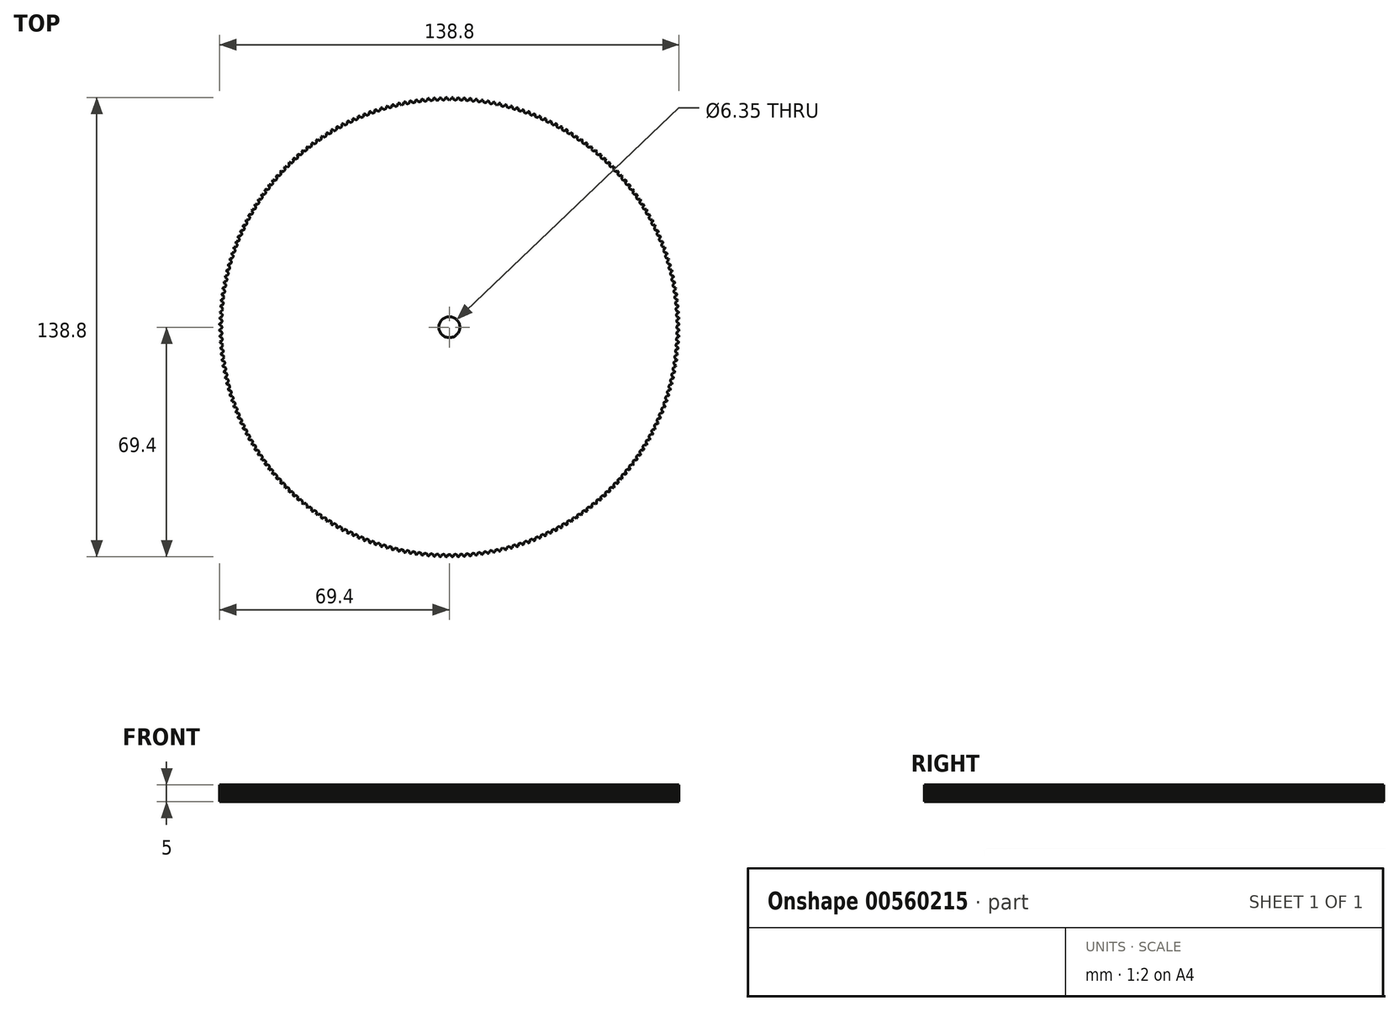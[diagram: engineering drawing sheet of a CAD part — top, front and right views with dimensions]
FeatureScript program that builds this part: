
annotation { "Feature Type Name" : "Feature", "Feature Type Description" : "" }
export const myFeature = defineFeature(function(context is Context, id is Id, definition is map)
    precondition{}
    {
        {
            var Q0;
            Q0=qCreatedBy(makeId("Top.planeOp"),FACE);
            var sketch = newSketch(context, id + "F0", { "sketchPlane" : qUnion([Q0])});
            skLineSegment(sketch, "E0", {"start": v(0.77, -69.4) * mm, "end": v(1.05, -69.4) * mm});
            skLineSegment(sketch, "E1", {"start": v(1.05, -69.4) * mm, "end": v(1.15, -69.36) * mm});
            skLineSegment(sketch, "E2", {"start": v(1.15, -69.36) * mm, "end": v(1.2, -69.27) * mm});
            skLineSegment(sketch, "E3", {"start": v(1.2, -69.27) * mm, "end": v(1.21, -69.18) * mm});
            skLineSegment(sketch, "E4", {"start": v(1.21, -69.18) * mm, "end": v(1.24, -69.08) * mm});
            skLineSegment(sketch, "E5", {"start": v(1.24, -69.08) * mm, "end": v(1.28, -68.99) * mm});
            skLineSegment(sketch, "E6", {"start": v(1.28, -68.99) * mm, "end": v(1.34, -68.9) * mm});
            skLineSegment(sketch, "E7", {"start": v(1.34, -68.9) * mm, "end": v(1.43, -68.8) * mm});
            skLineSegment(sketch, "E8", {"start": v(1.43, -68.8) * mm, "end": v(1.54, -68.74) * mm});
            skLineSegment(sketch, "E9", {"start": v(1.54, -68.74) * mm, "end": v(1.67, -68.7) * mm});
            skLineSegment(sketch, "E10", {"start": v(1.67, -68.7) * mm, "end": v(1.8, -68.68) * mm});
            skLineSegment(sketch, "E11", {"start": v(1.8, -68.68) * mm, "end": v(1.93, -68.69) * mm});
            skLineSegment(sketch, "E12", {"start": v(1.93, -68.69) * mm, "end": v(2.06, -68.73) * mm});
            skLineSegment(sketch, "E13", {"start": v(2.06, -68.73) * mm, "end": v(2.17, -68.79) * mm});
            skLineSegment(sketch, "E14", {"start": v(2.17, -68.79) * mm, "end": v(2.27, -68.87) * mm});
            skLineSegment(sketch, "E15", {"start": v(2.27, -68.87) * mm, "end": v(2.33, -68.96) * mm});
            skLineSegment(sketch, "E16", {"start": v(2.33, -68.96) * mm, "end": v(2.37, -69.05) * mm});
            skLineSegment(sketch, "E17", {"start": v(2.37, -69.05) * mm, "end": v(2.4, -69.14) * mm});
            skLineSegment(sketch, "E18", {"start": v(2.4, -69.14) * mm, "end": v(2.43, -69.24) * mm});
            skLineSegment(sketch, "E19", {"start": v(2.43, -69.24) * mm, "end": v(2.49, -69.33) * mm});
            skLineSegment(sketch, "E20", {"start": v(2.49, -69.33) * mm, "end": v(2.59, -69.36) * mm});
            skLineSegment(sketch, "E21", {"start": v(2.59, -69.36) * mm, "end": v(2.86, -69.35) * mm});
            skLineSegment(sketch, "E22", {"start": v(2.86, -69.35) * mm, "end": v(2.96, -69.3) * mm});
            skLineSegment(sketch, "E23", {"start": v(2.96, -69.3) * mm, "end": v(3, -69.22) * mm});
            skLineSegment(sketch, "E24", {"start": v(3, -69.22) * mm, "end": v(3.02, -69.12) * mm});
            skLineSegment(sketch, "E25", {"start": v(3.02, -69.12) * mm, "end": v(3.05, -69.02) * mm});
            skLineSegment(sketch, "E26", {"start": v(3.05, -69.02) * mm, "end": v(3.09, -68.93) * mm});
            skLineSegment(sketch, "E27", {"start": v(3.09, -68.93) * mm, "end": v(3.14, -68.84) * mm});
            skLineSegment(sketch, "E28", {"start": v(3.14, -68.84) * mm, "end": v(3.23, -68.75) * mm});
            skLineSegment(sketch, "E29", {"start": v(3.23, -68.75) * mm, "end": v(3.34, -68.68) * mm});
            skLineSegment(sketch, "E30", {"start": v(3.34, -68.68) * mm, "end": v(3.47, -68.63) * mm});
            skLineSegment(sketch, "E31", {"start": v(3.47, -68.63) * mm, "end": v(3.6, -68.6) * mm});
            skLineSegment(sketch, "E32", {"start": v(3.6, -68.6) * mm, "end": v(3.73, -68.62) * mm});
            skLineSegment(sketch, "E33", {"start": v(3.73, -68.62) * mm, "end": v(3.85, -68.65) * mm});
            skLineSegment(sketch, "E34", {"start": v(3.85, -68.65) * mm, "end": v(3.97, -68.7) * mm});
            skLineSegment(sketch, "E35", {"start": v(3.97, -68.7) * mm, "end": v(4.07, -68.79) * mm});
            skLineSegment(sketch, "E36", {"start": v(4.07, -68.79) * mm, "end": v(4.13, -68.87) * mm});
            skLineSegment(sketch, "E37", {"start": v(4.13, -68.87) * mm, "end": v(4.18, -68.96) * mm});
            skLineSegment(sketch, "E38", {"start": v(4.18, -68.96) * mm, "end": v(4.22, -69.06) * mm});
            skLineSegment(sketch, "E39", {"start": v(4.22, -69.06) * mm, "end": v(4.24, -69.15) * mm});
            skLineSegment(sketch, "E40", {"start": v(4.24, -69.15) * mm, "end": v(4.3, -69.24) * mm});
            skLineSegment(sketch, "E41", {"start": v(4.3, -69.24) * mm, "end": v(4.4, -69.26) * mm});
            skLineSegment(sketch, "E42", {"start": v(4.4, -69.26) * mm, "end": v(4.68, -69.25) * mm});
            skLineSegment(sketch, "E43", {"start": v(4.68, -69.25) * mm, "end": v(4.77, -69.2) * mm});
            skLineSegment(sketch, "E44", {"start": v(4.77, -69.2) * mm, "end": v(4.82, -69.12) * mm});
            skLineSegment(sketch, "E45", {"start": v(4.82, -69.12) * mm, "end": v(4.83, -69.02) * mm});
            skLineSegment(sketch, "E46", {"start": v(4.83, -69.02) * mm, "end": v(4.86, -68.92) * mm});
            skLineSegment(sketch, "E47", {"start": v(4.86, -68.92) * mm, "end": v(4.9, -68.82) * mm});
            skLineSegment(sketch, "E48", {"start": v(4.9, -68.82) * mm, "end": v(4.94, -68.73) * mm});
            skLineSegment(sketch, "E49", {"start": v(4.94, -68.73) * mm, "end": v(5.03, -68.64) * mm});
            skLineSegment(sketch, "E50", {"start": v(5.03, -68.64) * mm, "end": v(5.14, -68.56) * mm});
            skLineSegment(sketch, "E51", {"start": v(5.14, -68.56) * mm, "end": v(5.26, -68.52) * mm});
            skLineSegment(sketch, "E52", {"start": v(5.26, -68.52) * mm, "end": v(5.4, -68.5) * mm});
            skLineSegment(sketch, "E53", {"start": v(5.4, -68.5) * mm, "end": v(5.52, -68.5) * mm});
            skLineSegment(sketch, "E54", {"start": v(5.52, -68.5) * mm, "end": v(5.65, -68.52) * mm});
            skLineSegment(sketch, "E55", {"start": v(5.65, -68.52) * mm, "end": v(5.77, -68.58) * mm});
            skLineSegment(sketch, "E56", {"start": v(5.77, -68.58) * mm, "end": v(5.87, -68.66) * mm});
            skLineSegment(sketch, "E57", {"start": v(5.87, -68.66) * mm, "end": v(5.93, -68.74) * mm});
            skLineSegment(sketch, "E58", {"start": v(5.93, -68.74) * mm, "end": v(5.98, -68.83) * mm});
            skLineSegment(sketch, "E59", {"start": v(5.98, -68.83) * mm, "end": v(6.02, -68.92) * mm});
            skLineSegment(sketch, "E60", {"start": v(6.02, -68.92) * mm, "end": v(6.05, -69.02) * mm});
            skLineSegment(sketch, "E61", {"start": v(6.05, -69.02) * mm, "end": v(6.1, -69.1) * mm});
            skLineSegment(sketch, "E62", {"start": v(6.1, -69.1) * mm, "end": v(6.21, -69.13) * mm});
            skLineSegment(sketch, "E63", {"start": v(6.21, -69.13) * mm, "end": v(6.49, -69.1) * mm});
            skLineSegment(sketch, "E64", {"start": v(6.49, -69.1) * mm, "end": v(6.58, -69.06) * mm});
            skLineSegment(sketch, "E65", {"start": v(6.58, -69.06) * mm, "end": v(6.63, -68.97) * mm});
            skLineSegment(sketch, "E66", {"start": v(6.63, -68.97) * mm, "end": v(6.64, -68.87) * mm});
            skLineSegment(sketch, "E67", {"start": v(6.64, -68.87) * mm, "end": v(6.66, -68.77) * mm});
            skLineSegment(sketch, "E68", {"start": v(6.66, -68.77) * mm, "end": v(6.7, -68.67) * mm});
            skLineSegment(sketch, "E69", {"start": v(6.7, -68.67) * mm, "end": v(6.74, -68.58) * mm});
            skLineSegment(sketch, "E70", {"start": v(6.74, -68.58) * mm, "end": v(6.83, -68.48) * mm});
            skLineSegment(sketch, "E71", {"start": v(6.83, -68.48) * mm, "end": v(6.93, -68.4) * mm});
            skLineSegment(sketch, "E72", {"start": v(6.93, -68.4) * mm, "end": v(7.05, -68.35) * mm});
            skLineSegment(sketch, "E73", {"start": v(7.05, -68.35) * mm, "end": v(7.18, -68.33) * mm});
            skLineSegment(sketch, "E74", {"start": v(7.18, -68.33) * mm, "end": v(7.31, -68.33) * mm});
            skLineSegment(sketch, "E75", {"start": v(7.31, -68.33) * mm, "end": v(7.44, -68.35) * mm});
            skLineSegment(sketch, "E76", {"start": v(7.44, -68.35) * mm, "end": v(7.56, -68.4) * mm});
            skLineSegment(sketch, "E77", {"start": v(7.56, -68.4) * mm, "end": v(7.67, -68.48) * mm});
            skLineSegment(sketch, "E78", {"start": v(7.67, -68.48) * mm, "end": v(7.73, -68.56) * mm});
            skLineSegment(sketch, "E79", {"start": v(7.73, -68.56) * mm, "end": v(7.78, -68.65) * mm});
            skLineSegment(sketch, "E80", {"start": v(7.78, -68.65) * mm, "end": v(7.83, -68.74) * mm});
            skLineSegment(sketch, "E81", {"start": v(7.83, -68.74) * mm, "end": v(7.86, -68.84) * mm});
            skLineSegment(sketch, "E82", {"start": v(7.86, -68.84) * mm, "end": v(7.92, -68.92) * mm});
            skLineSegment(sketch, "E83", {"start": v(7.92, -68.92) * mm, "end": v(8.02, -68.94) * mm});
            skLineSegment(sketch, "E84", {"start": v(8.02, -68.94) * mm, "end": v(8.3, -68.9) * mm});
            skLineSegment(sketch, "E85", {"start": v(8.3, -68.9) * mm, "end": v(8.4, -68.86) * mm});
            skLineSegment(sketch, "E86", {"start": v(8.4, -68.86) * mm, "end": v(8.43, -68.77) * mm});
            skLineSegment(sketch, "E87", {"start": v(8.43, -68.77) * mm, "end": v(8.44, -68.67) * mm});
            skLineSegment(sketch, "E88", {"start": v(8.44, -68.67) * mm, "end": v(8.46, -68.57) * mm});
            skLineSegment(sketch, "E89", {"start": v(8.46, -68.57) * mm, "end": v(8.49, -68.47) * mm});
            skLineSegment(sketch, "E90", {"start": v(8.49, -68.47) * mm, "end": v(8.53, -68.38) * mm});
            skLineSegment(sketch, "E91", {"start": v(8.53, -68.38) * mm, "end": v(8.62, -68.28) * mm});
            skLineSegment(sketch, "E92", {"start": v(8.62, -68.28) * mm, "end": v(8.72, -68.2) * mm});
            skLineSegment(sketch, "E93", {"start": v(8.72, -68.2) * mm, "end": v(8.84, -68.15) * mm});
            skLineSegment(sketch, "E94", {"start": v(8.84, -68.15) * mm, "end": v(8.97, -68.12) * mm});
            skLineSegment(sketch, "E95", {"start": v(8.97, -68.12) * mm, "end": v(9.1, -68.11) * mm});
            skLineSegment(sketch, "E96", {"start": v(9.1, -68.11) * mm, "end": v(9.23, -68.13) * mm});
            skLineSegment(sketch, "E97", {"start": v(9.23, -68.13) * mm, "end": v(9.35, -68.18) * mm});
            skLineSegment(sketch, "E98", {"start": v(9.35, -68.18) * mm, "end": v(9.46, -68.26) * mm});
            skLineSegment(sketch, "E99", {"start": v(9.46, -68.26) * mm, "end": v(9.52, -68.34) * mm});
            skLineSegment(sketch, "E100", {"start": v(9.52, -68.34) * mm, "end": v(9.58, -68.42) * mm});
            skLineSegment(sketch, "E101", {"start": v(9.58, -68.42) * mm, "end": v(9.62, -68.51) * mm});
            skLineSegment(sketch, "E102", {"start": v(9.62, -68.51) * mm, "end": v(9.66, -68.6) * mm});
            skLineSegment(sketch, "E103", {"start": v(9.66, -68.6) * mm, "end": v(9.72, -68.69) * mm});
            skLineSegment(sketch, "E104", {"start": v(9.72, -68.69) * mm, "end": v(9.82, -68.7) * mm});
            skLineSegment(sketch, "E105", {"start": v(9.82, -68.7) * mm, "end": v(10.1, -68.67) * mm});
            skLineSegment(sketch, "E106", {"start": v(10.1, -68.67) * mm, "end": v(10.19, -68.62) * mm});
            skLineSegment(sketch, "E107", {"start": v(10.19, -68.62) * mm, "end": v(10.23, -68.53) * mm});
            skLineSegment(sketch, "E108", {"start": v(10.23, -68.53) * mm, "end": v(10.23, -68.43) * mm});
            skLineSegment(sketch, "E109", {"start": v(10.23, -68.43) * mm, "end": v(10.25, -68.33) * mm});
            skLineSegment(sketch, "E110", {"start": v(10.25, -68.33) * mm, "end": v(10.28, -68.23) * mm});
            skLineSegment(sketch, "E111", {"start": v(10.28, -68.23) * mm, "end": v(10.32, -68.13) * mm});
            skLineSegment(sketch, "E112", {"start": v(10.32, -68.13) * mm, "end": v(10.4, -68.03) * mm});
            skLineSegment(sketch, "E113", {"start": v(10.4, -68.03) * mm, "end": v(10.5, -67.95) * mm});
            skLineSegment(sketch, "E114", {"start": v(10.5, -67.95) * mm, "end": v(10.62, -67.9) * mm});
            skLineSegment(sketch, "E115", {"start": v(10.62, -67.9) * mm, "end": v(10.75, -67.86) * mm});
            skLineSegment(sketch, "E116", {"start": v(10.75, -67.86) * mm, "end": v(10.88, -67.85) * mm});
            skLineSegment(sketch, "E117", {"start": v(10.88, -67.85) * mm, "end": v(11, -67.87) * mm});
            skLineSegment(sketch, "E118", {"start": v(11, -67.87) * mm, "end": v(11.13, -67.91) * mm});
            skLineSegment(sketch, "E119", {"start": v(11.13, -67.91) * mm, "end": v(11.24, -67.99) * mm});
            skLineSegment(sketch, "E120", {"start": v(11.24, -67.99) * mm, "end": v(11.3, -68.07) * mm});
            skLineSegment(sketch, "E121", {"start": v(11.3, -68.07) * mm, "end": v(11.37, -68.15) * mm});
            skLineSegment(sketch, "E122", {"start": v(11.37, -68.15) * mm, "end": v(11.41, -68.24) * mm});
            skLineSegment(sketch, "E123", {"start": v(11.41, -68.24) * mm, "end": v(11.45, -68.33) * mm});
            skLineSegment(sketch, "E124", {"start": v(11.45, -68.33) * mm, "end": v(11.51, -68.4) * mm});
            skLineSegment(sketch, "E125", {"start": v(11.51, -68.4) * mm, "end": v(11.62, -68.43) * mm});
            skLineSegment(sketch, "E126", {"start": v(11.62, -68.43) * mm, "end": v(11.89, -68.38) * mm});
            skLineSegment(sketch, "E127", {"start": v(11.89, -68.38) * mm, "end": v(11.98, -68.33) * mm});
            skLineSegment(sketch, "E128", {"start": v(11.98, -68.33) * mm, "end": v(12.02, -68.23) * mm});
            skLineSegment(sketch, "E129", {"start": v(12.02, -68.23) * mm, "end": v(12.02, -68.13) * mm});
            skLineSegment(sketch, "E130", {"start": v(12.02, -68.13) * mm, "end": v(12.03, -68.03) * mm});
            skLineSegment(sketch, "E131", {"start": v(12.03, -68.03) * mm, "end": v(12.06, -67.94) * mm});
            skLineSegment(sketch, "E132", {"start": v(12.06, -67.94) * mm, "end": v(12.1, -67.84) * mm});
            skLineSegment(sketch, "E133", {"start": v(12.1, -67.84) * mm, "end": v(12.18, -67.74) * mm});
            skLineSegment(sketch, "E134", {"start": v(12.18, -67.74) * mm, "end": v(12.28, -67.65) * mm});
            skLineSegment(sketch, "E135", {"start": v(12.28, -67.65) * mm, "end": v(12.4, -67.6) * mm});
            skLineSegment(sketch, "E136", {"start": v(12.4, -67.6) * mm, "end": v(12.52, -67.55) * mm});
            skLineSegment(sketch, "E137", {"start": v(12.52, -67.55) * mm, "end": v(12.65, -67.54) * mm});
            skLineSegment(sketch, "E138", {"start": v(12.65, -67.54) * mm, "end": v(12.78, -67.56) * mm});
            skLineSegment(sketch, "E139", {"start": v(12.78, -67.56) * mm, "end": v(12.9, -67.6) * mm});
            skLineSegment(sketch, "E140", {"start": v(12.9, -67.6) * mm, "end": v(13.02, -67.67) * mm});
            skLineSegment(sketch, "E141", {"start": v(13.02, -67.67) * mm, "end": v(13.09, -67.75) * mm});
            skLineSegment(sketch, "E142", {"start": v(13.09, -67.75) * mm, "end": v(13.15, -67.83) * mm});
            skLineSegment(sketch, "E143", {"start": v(13.15, -67.83) * mm, "end": v(13.2, -67.92) * mm});
            skLineSegment(sketch, "E144", {"start": v(13.2, -67.92) * mm, "end": v(13.23, -68) * mm});
            skLineSegment(sketch, "E145", {"start": v(13.23, -68) * mm, "end": v(13.3, -68.08) * mm});
            skLineSegment(sketch, "E146", {"start": v(13.3, -68.08) * mm, "end": v(13.4, -68.1) * mm});
            skLineSegment(sketch, "E147", {"start": v(13.4, -68.1) * mm, "end": v(13.67, -68.04) * mm});
            skLineSegment(sketch, "E148", {"start": v(13.67, -68.04) * mm, "end": v(13.77, -68) * mm});
            skLineSegment(sketch, "E149", {"start": v(13.77, -68) * mm, "end": v(13.8, -67.9) * mm});
            skLineSegment(sketch, "E150", {"start": v(13.8, -67.9) * mm, "end": v(13.8, -67.8) * mm});
            skLineSegment(sketch, "E151", {"start": v(13.8, -67.8) * mm, "end": v(13.81, -67.7) * mm});
            skLineSegment(sketch, "E152", {"start": v(13.81, -67.7) * mm, "end": v(13.83, -67.6) * mm});
            skLineSegment(sketch, "E153", {"start": v(13.83, -67.6) * mm, "end": v(13.87, -67.5) * mm});
            skLineSegment(sketch, "E154", {"start": v(13.87, -67.5) * mm, "end": v(13.95, -67.4) * mm});
            skLineSegment(sketch, "E155", {"start": v(13.95, -67.4) * mm, "end": v(14.04, -67.3) * mm});
            skLineSegment(sketch, "E156", {"start": v(14.04, -67.3) * mm, "end": v(14.16, -67.24) * mm});
            skLineSegment(sketch, "E157", {"start": v(14.16, -67.24) * mm, "end": v(14.28, -67.2) * mm});
            skLineSegment(sketch, "E158", {"start": v(14.28, -67.2) * mm, "end": v(14.42, -67.19) * mm});
            skLineSegment(sketch, "E159", {"start": v(14.42, -67.19) * mm, "end": v(14.55, -67.2) * mm});
            skLineSegment(sketch, "E160", {"start": v(14.55, -67.2) * mm, "end": v(14.67, -67.24) * mm});
            skLineSegment(sketch, "E161", {"start": v(14.67, -67.24) * mm, "end": v(14.78, -67.3) * mm});
            skLineSegment(sketch, "E162", {"start": v(14.78, -67.3) * mm, "end": v(14.86, -67.38) * mm});
            skLineSegment(sketch, "E163", {"start": v(14.86, -67.38) * mm, "end": v(14.92, -67.46) * mm});
            skLineSegment(sketch, "E164", {"start": v(14.92, -67.46) * mm, "end": v(14.97, -67.55) * mm});
            skLineSegment(sketch, "E165", {"start": v(14.97, -67.55) * mm, "end": v(15, -67.64) * mm});
            skLineSegment(sketch, "E166", {"start": v(15, -67.64) * mm, "end": v(15.08, -67.71) * mm});
            skLineSegment(sketch, "E167", {"start": v(15.08, -67.71) * mm, "end": v(15.18, -67.72) * mm});
            skLineSegment(sketch, "E168", {"start": v(15.18, -67.72) * mm, "end": v(15.45, -67.66) * mm});
            skLineSegment(sketch, "E169", {"start": v(15.45, -67.66) * mm, "end": v(15.54, -67.6) * mm});
            skLineSegment(sketch, "E170", {"start": v(15.54, -67.6) * mm, "end": v(15.57, -67.51) * mm});
            skLineSegment(sketch, "E171", {"start": v(15.57, -67.51) * mm, "end": v(15.57, -67.41) * mm});
            skLineSegment(sketch, "E172", {"start": v(15.57, -67.41) * mm, "end": v(15.58, -67.31) * mm});
            skLineSegment(sketch, "E173", {"start": v(15.58, -67.31) * mm, "end": v(15.6, -67.21) * mm});
            skLineSegment(sketch, "E174", {"start": v(15.6, -67.21) * mm, "end": v(15.63, -67.11) * mm});
            skLineSegment(sketch, "E175", {"start": v(15.63, -67.11) * mm, "end": v(15.7, -67) * mm});
            skLineSegment(sketch, "E176", {"start": v(15.7, -67) * mm, "end": v(15.8, -66.92) * mm});
            skLineSegment(sketch, "E177", {"start": v(15.8, -66.92) * mm, "end": v(15.91, -66.85) * mm});
            skLineSegment(sketch, "E178", {"start": v(15.91, -66.85) * mm, "end": v(16.04, -66.8) * mm});
            skLineSegment(sketch, "E179", {"start": v(16.04, -66.8) * mm, "end": v(16.17, -66.79) * mm});
            skLineSegment(sketch, "E180", {"start": v(16.17, -66.79) * mm, "end": v(16.3, -66.8) * mm});
            skLineSegment(sketch, "E181", {"start": v(16.3, -66.8) * mm, "end": v(16.43, -66.83) * mm});
            skLineSegment(sketch, "E182", {"start": v(16.43, -66.83) * mm, "end": v(16.54, -66.9) * mm});
            skLineSegment(sketch, "E183", {"start": v(16.54, -66.9) * mm, "end": v(16.61, -66.97) * mm});
            skLineSegment(sketch, "E184", {"start": v(16.61, -66.97) * mm, "end": v(16.68, -67.05) * mm});
            skLineSegment(sketch, "E185", {"start": v(16.68, -67.05) * mm, "end": v(16.73, -67.13) * mm});
            skLineSegment(sketch, "E186", {"start": v(16.73, -67.13) * mm, "end": v(16.77, -67.22) * mm});
            skLineSegment(sketch, "E187", {"start": v(16.77, -67.22) * mm, "end": v(16.84, -67.3) * mm});
            skLineSegment(sketch, "E188", {"start": v(16.84, -67.3) * mm, "end": v(16.95, -67.3) * mm});
            skLineSegment(sketch, "E189", {"start": v(16.95, -67.3) * mm, "end": v(17.22, -67.24) * mm});
            skLineSegment(sketch, "E190", {"start": v(17.22, -67.24) * mm, "end": v(17.3, -67.18) * mm});
            skLineSegment(sketch, "E191", {"start": v(17.3, -67.18) * mm, "end": v(17.33, -67.08) * mm});
            skLineSegment(sketch, "E192", {"start": v(17.33, -67.08) * mm, "end": v(17.33, -66.98) * mm});
            skLineSegment(sketch, "E193", {"start": v(17.33, -66.98) * mm, "end": v(17.33, -66.88) * mm});
            skLineSegment(sketch, "E194", {"start": v(17.33, -66.88) * mm, "end": v(17.35, -66.78) * mm});
            skLineSegment(sketch, "E195", {"start": v(17.35, -66.78) * mm, "end": v(17.38, -66.68) * mm});
            skLineSegment(sketch, "E196", {"start": v(17.38, -66.68) * mm, "end": v(17.45, -66.57) * mm});
            skLineSegment(sketch, "E197", {"start": v(17.45, -66.57) * mm, "end": v(17.55, -66.48) * mm});
            skLineSegment(sketch, "E198", {"start": v(17.55, -66.48) * mm, "end": v(17.66, -66.4) * mm});
            skLineSegment(sketch, "E199", {"start": v(17.66, -66.4) * mm, "end": v(17.78, -66.36) * mm});
            skLineSegment(sketch, "E200", {"start": v(17.78, -66.36) * mm, "end": v(17.91, -66.34) * mm});
            skLineSegment(sketch, "E201", {"start": v(17.91, -66.34) * mm, "end": v(18.04, -66.35) * mm});
            skLineSegment(sketch, "E202", {"start": v(18.04, -66.35) * mm, "end": v(18.17, -66.38) * mm});
            skLineSegment(sketch, "E203", {"start": v(18.17, -66.38) * mm, "end": v(18.29, -66.44) * mm});
            skLineSegment(sketch, "E204", {"start": v(18.29, -66.44) * mm, "end": v(18.36, -66.51) * mm});
            skLineSegment(sketch, "E205", {"start": v(18.36, -66.51) * mm, "end": v(18.43, -66.59) * mm});
            skLineSegment(sketch, "E206", {"start": v(18.43, -66.59) * mm, "end": v(18.48, -66.67) * mm});
            skLineSegment(sketch, "E207", {"start": v(18.48, -66.67) * mm, "end": v(18.53, -66.76) * mm});
            skLineSegment(sketch, "E208", {"start": v(18.53, -66.76) * mm, "end": v(18.6, -66.83) * mm});
            skLineSegment(sketch, "E209", {"start": v(18.6, -66.83) * mm, "end": v(18.7, -66.84) * mm});
            skLineSegment(sketch, "E210", {"start": v(18.7, -66.84) * mm, "end": v(18.97, -66.76) * mm});
            skLineSegment(sketch, "E211", {"start": v(18.97, -66.76) * mm, "end": v(19.06, -66.7) * mm});
            skLineSegment(sketch, "E212", {"start": v(19.06, -66.7) * mm, "end": v(19.08, -66.6) * mm});
            skLineSegment(sketch, "E213", {"start": v(19.08, -66.6) * mm, "end": v(19.08, -66.5) * mm});
            skLineSegment(sketch, "E214", {"start": v(19.08, -66.5) * mm, "end": v(19.08, -66.4) * mm});
            skLineSegment(sketch, "E215", {"start": v(19.08, -66.4) * mm, "end": v(19.1, -66.3) * mm});
            skLineSegment(sketch, "E216", {"start": v(19.1, -66.3) * mm, "end": v(19.12, -66.2) * mm});
            skLineSegment(sketch, "E217", {"start": v(19.12, -66.2) * mm, "end": v(19.2, -66.1) * mm});
            skLineSegment(sketch, "E218", {"start": v(19.2, -66.1) * mm, "end": v(19.28, -66) * mm});
            skLineSegment(sketch, "E219", {"start": v(19.28, -66) * mm, "end": v(19.4, -65.92) * mm});
            skLineSegment(sketch, "E220", {"start": v(19.4, -65.92) * mm, "end": v(19.51, -65.87) * mm});
            skLineSegment(sketch, "E221", {"start": v(19.51, -65.87) * mm, "end": v(19.64, -65.85) * mm});
            skLineSegment(sketch, "E222", {"start": v(19.64, -65.85) * mm, "end": v(19.77, -65.85) * mm});
            skLineSegment(sketch, "E223", {"start": v(19.77, -65.85) * mm, "end": v(19.9, -65.88) * mm});
            skLineSegment(sketch, "E224", {"start": v(19.9, -65.88) * mm, "end": v(20.02, -65.94) * mm});
            skLineSegment(sketch, "E225", {"start": v(20.02, -65.94) * mm, "end": v(20.1, -66) * mm});
            skLineSegment(sketch, "E226", {"start": v(20.1, -66) * mm, "end": v(20.16, -66.08) * mm});
            skLineSegment(sketch, "E227", {"start": v(20.16, -66.08) * mm, "end": v(20.22, -66.16) * mm});
            skLineSegment(sketch, "E228", {"start": v(20.22, -66.16) * mm, "end": v(20.27, -66.25) * mm});
            skLineSegment(sketch, "E229", {"start": v(20.27, -66.25) * mm, "end": v(20.34, -66.32) * mm});
            skLineSegment(sketch, "E230", {"start": v(20.34, -66.32) * mm, "end": v(20.45, -66.32) * mm});
            skLineSegment(sketch, "E231", {"start": v(20.45, -66.32) * mm, "end": v(20.71, -66.24) * mm});
            skLineSegment(sketch, "E232", {"start": v(20.71, -66.24) * mm, "end": v(20.8, -66.18) * mm});
            skLineSegment(sketch, "E233", {"start": v(20.8, -66.18) * mm, "end": v(20.82, -66.08) * mm});
            skLineSegment(sketch, "E234", {"start": v(20.82, -66.08) * mm, "end": v(20.81, -65.98) * mm});
            skLineSegment(sketch, "E235", {"start": v(20.81, -65.98) * mm, "end": v(20.81, -65.88) * mm});
            skLineSegment(sketch, "E236", {"start": v(20.81, -65.88) * mm, "end": v(20.82, -65.78) * mm});
            skLineSegment(sketch, "E237", {"start": v(20.82, -65.78) * mm, "end": v(20.85, -65.68) * mm});
            skLineSegment(sketch, "E238", {"start": v(20.85, -65.68) * mm, "end": v(20.91, -65.57) * mm});
            skLineSegment(sketch, "E239", {"start": v(20.91, -65.57) * mm, "end": v(21, -65.47) * mm});
            skLineSegment(sketch, "E240", {"start": v(21, -65.47) * mm, "end": v(21.1, -65.4) * mm});
            skLineSegment(sketch, "E241", {"start": v(21.1, -65.4) * mm, "end": v(21.23, -65.34) * mm});
            skLineSegment(sketch, "E242", {"start": v(21.23, -65.34) * mm, "end": v(21.36, -65.31) * mm});
            skLineSegment(sketch, "E243", {"start": v(21.36, -65.31) * mm, "end": v(21.5, -65.31) * mm});
            skLineSegment(sketch, "E244", {"start": v(21.5, -65.31) * mm, "end": v(21.62, -65.34) * mm});
            skLineSegment(sketch, "E245", {"start": v(21.62, -65.34) * mm, "end": v(21.74, -65.4) * mm});
            skLineSegment(sketch, "E246", {"start": v(21.74, -65.4) * mm, "end": v(21.82, -65.46) * mm});
            skLineSegment(sketch, "E247", {"start": v(21.82, -65.46) * mm, "end": v(21.89, -65.53) * mm});
            skLineSegment(sketch, "E248", {"start": v(21.89, -65.53) * mm, "end": v(21.95, -65.61) * mm});
            skLineSegment(sketch, "E249", {"start": v(21.95, -65.61) * mm, "end": v(22, -65.7) * mm});
            skLineSegment(sketch, "E250", {"start": v(22, -65.7) * mm, "end": v(22.07, -65.76) * mm});
            skLineSegment(sketch, "E251", {"start": v(22.07, -65.76) * mm, "end": v(22.18, -65.77) * mm});
            skLineSegment(sketch, "E252", {"start": v(22.18, -65.77) * mm, "end": v(22.44, -65.68) * mm});
            skLineSegment(sketch, "E253", {"start": v(22.44, -65.68) * mm, "end": v(22.52, -65.61) * mm});
            skLineSegment(sketch, "E254", {"start": v(22.52, -65.61) * mm, "end": v(22.54, -65.51) * mm});
            skLineSegment(sketch, "E255", {"start": v(22.54, -65.51) * mm, "end": v(22.53, -65.41) * mm});
            skLineSegment(sketch, "E256", {"start": v(22.53, -65.41) * mm, "end": v(22.53, -65.31) * mm});
            skLineSegment(sketch, "E257", {"start": v(22.53, -65.31) * mm, "end": v(22.54, -65.21) * mm});
            skLineSegment(sketch, "E258", {"start": v(22.54, -65.21) * mm, "end": v(22.56, -65.11) * mm});
            skLineSegment(sketch, "E259", {"start": v(22.56, -65.11) * mm, "end": v(22.62, -65) * mm});
            skLineSegment(sketch, "E260", {"start": v(22.62, -65) * mm, "end": v(22.7, -64.9) * mm});
            skLineSegment(sketch, "E261", {"start": v(22.7, -64.9) * mm, "end": v(22.81, -64.82) * mm});
            skLineSegment(sketch, "E262", {"start": v(22.81, -64.82) * mm, "end": v(22.93, -64.76) * mm});
            skLineSegment(sketch, "E263", {"start": v(22.93, -64.76) * mm, "end": v(23.06, -64.73) * mm});
            skLineSegment(sketch, "E264", {"start": v(23.06, -64.73) * mm, "end": v(23.2, -64.73) * mm});
            skLineSegment(sketch, "E265", {"start": v(23.2, -64.73) * mm, "end": v(23.32, -64.75) * mm});
            skLineSegment(sketch, "E266", {"start": v(23.32, -64.75) * mm, "end": v(23.44, -64.8) * mm});
            skLineSegment(sketch, "E267", {"start": v(23.44, -64.8) * mm, "end": v(23.52, -64.86) * mm});
            skLineSegment(sketch, "E268", {"start": v(23.52, -64.86) * mm, "end": v(23.6, -64.94) * mm});
            skLineSegment(sketch, "E269", {"start": v(23.6, -64.94) * mm, "end": v(23.66, -65.02) * mm});
            skLineSegment(sketch, "E270", {"start": v(23.66, -65.02) * mm, "end": v(23.7, -65.1) * mm});
            skLineSegment(sketch, "E271", {"start": v(23.7, -65.1) * mm, "end": v(23.79, -65.16) * mm});
            skLineSegment(sketch, "E272", {"start": v(23.79, -65.16) * mm, "end": v(23.9, -65.16) * mm});
            skLineSegment(sketch, "E273", {"start": v(23.9, -65.16) * mm, "end": v(24.15, -65.07) * mm});
            skLineSegment(sketch, "E274", {"start": v(24.15, -65.07) * mm, "end": v(24.23, -65) * mm});
            skLineSegment(sketch, "E275", {"start": v(24.23, -65) * mm, "end": v(24.25, -64.9) * mm});
            skLineSegment(sketch, "E276", {"start": v(24.25, -64.9) * mm, "end": v(24.23, -64.8) * mm});
            skLineSegment(sketch, "E277", {"start": v(24.23, -64.8) * mm, "end": v(24.23, -64.7) * mm});
            skLineSegment(sketch, "E278", {"start": v(24.23, -64.7) * mm, "end": v(24.24, -64.6) * mm});
            skLineSegment(sketch, "E279", {"start": v(24.24, -64.6) * mm, "end": v(24.26, -64.5) * mm});
            skLineSegment(sketch, "E280", {"start": v(24.26, -64.5) * mm, "end": v(24.32, -64.38) * mm});
            skLineSegment(sketch, "E281", {"start": v(24.32, -64.38) * mm, "end": v(24.4, -64.28) * mm});
            skLineSegment(sketch, "E282", {"start": v(24.4, -64.28) * mm, "end": v(24.5, -64.2) * mm});
            skLineSegment(sketch, "E283", {"start": v(24.5, -64.2) * mm, "end": v(24.62, -64.14) * mm});
            skLineSegment(sketch, "E284", {"start": v(24.62, -64.14) * mm, "end": v(24.75, -64.1) * mm});
            skLineSegment(sketch, "E285", {"start": v(24.75, -64.1) * mm, "end": v(24.88, -64.1) * mm});
            skLineSegment(sketch, "E286", {"start": v(24.88, -64.1) * mm, "end": v(25, -64.12) * mm});
            skLineSegment(sketch, "E287", {"start": v(25, -64.12) * mm, "end": v(25.13, -64.16) * mm});
            skLineSegment(sketch, "E288", {"start": v(25.13, -64.16) * mm, "end": v(25.21, -64.23) * mm});
            skLineSegment(sketch, "E289", {"start": v(25.21, -64.23) * mm, "end": v(25.29, -64.3) * mm});
            skLineSegment(sketch, "E290", {"start": v(25.29, -64.3) * mm, "end": v(25.35, -64.37) * mm});
            skLineSegment(sketch, "E291", {"start": v(25.35, -64.37) * mm, "end": v(25.4, -64.46) * mm});
            skLineSegment(sketch, "E292", {"start": v(25.4, -64.46) * mm, "end": v(25.48, -64.52) * mm});
            skLineSegment(sketch, "E293", {"start": v(25.48, -64.52) * mm, "end": v(25.6, -64.51) * mm});
            skLineSegment(sketch, "E294", {"start": v(25.6, -64.51) * mm, "end": v(25.85, -64.41) * mm});
            skLineSegment(sketch, "E295", {"start": v(25.85, -64.41) * mm, "end": v(25.93, -64.34) * mm});
            skLineSegment(sketch, "E296", {"start": v(25.93, -64.34) * mm, "end": v(25.94, -64.24) * mm});
            skLineSegment(sketch, "E297", {"start": v(25.94, -64.24) * mm, "end": v(25.92, -64.15) * mm});
            skLineSegment(sketch, "E298", {"start": v(25.92, -64.15) * mm, "end": v(25.92, -64.05) * mm});
            skLineSegment(sketch, "E299", {"start": v(25.92, -64.05) * mm, "end": v(25.92, -63.94) * mm});
            skLineSegment(sketch, "E300", {"start": v(25.92, -63.94) * mm, "end": v(25.94, -63.84) * mm});
            skLineSegment(sketch, "E301", {"start": v(25.94, -63.84) * mm, "end": v(26, -63.72) * mm});
            skLineSegment(sketch, "E302", {"start": v(26, -63.72) * mm, "end": v(26.07, -63.62) * mm});
            skLineSegment(sketch, "E303", {"start": v(26.07, -63.62) * mm, "end": v(26.18, -63.54) * mm});
            skLineSegment(sketch, "E304", {"start": v(26.18, -63.54) * mm, "end": v(26.3, -63.47) * mm});
            skLineSegment(sketch, "E305", {"start": v(26.3, -63.47) * mm, "end": v(26.42, -63.44) * mm});
            skLineSegment(sketch, "E306", {"start": v(26.42, -63.44) * mm, "end": v(26.55, -63.42) * mm});
            skLineSegment(sketch, "E307", {"start": v(26.55, -63.42) * mm, "end": v(26.68, -63.44) * mm});
            skLineSegment(sketch, "E308", {"start": v(26.68, -63.44) * mm, "end": v(26.8, -63.48) * mm});
            skLineSegment(sketch, "E309", {"start": v(26.8, -63.48) * mm, "end": v(26.89, -63.54) * mm});
            skLineSegment(sketch, "E310", {"start": v(26.89, -63.54) * mm, "end": v(26.96, -63.61) * mm});
            skLineSegment(sketch, "E311", {"start": v(26.96, -63.61) * mm, "end": v(27.03, -63.69) * mm});
            skLineSegment(sketch, "E312", {"start": v(27.03, -63.69) * mm, "end": v(27.08, -63.77) * mm});
            skLineSegment(sketch, "E313", {"start": v(27.08, -63.77) * mm, "end": v(27.16, -63.83) * mm});
            skLineSegment(sketch, "E314", {"start": v(27.16, -63.83) * mm, "end": v(27.27, -63.82) * mm});
            skLineSegment(sketch, "E315", {"start": v(27.27, -63.82) * mm, "end": v(27.52, -63.71) * mm});
            skLineSegment(sketch, "E316", {"start": v(27.52, -63.71) * mm, "end": v(27.6, -63.64) * mm});
            skLineSegment(sketch, "E317", {"start": v(27.6, -63.64) * mm, "end": v(27.61, -63.54) * mm});
            skLineSegment(sketch, "E318", {"start": v(27.61, -63.54) * mm, "end": v(27.6, -63.45) * mm});
            skLineSegment(sketch, "E319", {"start": v(27.6, -63.45) * mm, "end": v(27.58, -63.34) * mm});
            skLineSegment(sketch, "E320", {"start": v(27.58, -63.34) * mm, "end": v(27.59, -63.24) * mm});
            skLineSegment(sketch, "E321", {"start": v(27.59, -63.24) * mm, "end": v(27.6, -63.14) * mm});
            skLineSegment(sketch, "E322", {"start": v(27.6, -63.14) * mm, "end": v(27.65, -63.02) * mm});
            skLineSegment(sketch, "E323", {"start": v(27.65, -63.02) * mm, "end": v(27.73, -62.92) * mm});
            skLineSegment(sketch, "E324", {"start": v(27.73, -62.92) * mm, "end": v(27.83, -62.83) * mm});
            skLineSegment(sketch, "E325", {"start": v(27.83, -62.83) * mm, "end": v(27.94, -62.76) * mm});
            skLineSegment(sketch, "E326", {"start": v(27.94, -62.76) * mm, "end": v(28.07, -62.72) * mm});
            skLineSegment(sketch, "E327", {"start": v(28.07, -62.72) * mm, "end": v(28.2, -62.7) * mm});
            skLineSegment(sketch, "E328", {"start": v(28.2, -62.7) * mm, "end": v(28.33, -62.72) * mm});
            skLineSegment(sketch, "E329", {"start": v(28.33, -62.72) * mm, "end": v(28.45, -62.76) * mm});
            skLineSegment(sketch, "E330", {"start": v(28.45, -62.76) * mm, "end": v(28.54, -62.82) * mm});
            skLineSegment(sketch, "E331", {"start": v(28.54, -62.82) * mm, "end": v(28.62, -62.88) * mm});
            skLineSegment(sketch, "E332", {"start": v(28.62, -62.88) * mm, "end": v(28.69, -62.96) * mm});
            skLineSegment(sketch, "E333", {"start": v(28.69, -62.96) * mm, "end": v(28.74, -63.04) * mm});
            skLineSegment(sketch, "E334", {"start": v(28.74, -63.04) * mm, "end": v(28.83, -63.1) * mm});
            skLineSegment(sketch, "E335", {"start": v(28.83, -63.1) * mm, "end": v(28.93, -63.09) * mm});
            skLineSegment(sketch, "E336", {"start": v(28.93, -63.09) * mm, "end": v(29.18, -62.97) * mm});
            skLineSegment(sketch, "E337", {"start": v(29.18, -62.97) * mm, "end": v(29.26, -62.9) * mm});
            skLineSegment(sketch, "E338", {"start": v(29.26, -62.9) * mm, "end": v(29.27, -62.8) * mm});
            skLineSegment(sketch, "E339", {"start": v(29.27, -62.8) * mm, "end": v(29.24, -62.7) * mm});
            skLineSegment(sketch, "E340", {"start": v(29.24, -62.7) * mm, "end": v(29.23, -62.6) * mm});
            skLineSegment(sketch, "E341", {"start": v(29.23, -62.6) * mm, "end": v(29.23, -62.5) * mm});
            skLineSegment(sketch, "E342", {"start": v(29.23, -62.5) * mm, "end": v(29.24, -62.4) * mm});
            skLineSegment(sketch, "E343", {"start": v(29.24, -62.4) * mm, "end": v(29.3, -62.28) * mm});
            skLineSegment(sketch, "E344", {"start": v(29.3, -62.28) * mm, "end": v(29.37, -62.17) * mm});
            skLineSegment(sketch, "E345", {"start": v(29.37, -62.17) * mm, "end": v(29.46, -62.08) * mm});
            skLineSegment(sketch, "E346", {"start": v(29.46, -62.08) * mm, "end": v(29.58, -62.01) * mm});
            skLineSegment(sketch, "E347", {"start": v(29.58, -62.01) * mm, "end": v(29.7, -61.97) * mm});
            skLineSegment(sketch, "E348", {"start": v(29.7, -61.97) * mm, "end": v(29.83, -61.95) * mm});
            skLineSegment(sketch, "E349", {"start": v(29.83, -61.95) * mm, "end": v(29.96, -61.96) * mm});
            skLineSegment(sketch, "E350", {"start": v(29.96, -61.96) * mm, "end": v(30.09, -62) * mm});
            skLineSegment(sketch, "E351", {"start": v(30.09, -62) * mm, "end": v(30.17, -62.05) * mm});
            skLineSegment(sketch, "E352", {"start": v(30.17, -62.05) * mm, "end": v(30.25, -62.11) * mm});
            skLineSegment(sketch, "E353", {"start": v(30.25, -62.11) * mm, "end": v(30.32, -62.19) * mm});
            skLineSegment(sketch, "E354", {"start": v(30.32, -62.19) * mm, "end": v(30.38, -62.27) * mm});
            skLineSegment(sketch, "E355", {"start": v(30.38, -62.27) * mm, "end": v(30.47, -62.32) * mm});
            skLineSegment(sketch, "E356", {"start": v(30.47, -62.32) * mm, "end": v(30.57, -62.3) * mm});
            skLineSegment(sketch, "E357", {"start": v(30.57, -62.3) * mm, "end": v(30.82, -62.19) * mm});
            skLineSegment(sketch, "E358", {"start": v(30.82, -62.19) * mm, "end": v(30.9, -62.11) * mm});
            skLineSegment(sketch, "E359", {"start": v(30.9, -62.11) * mm, "end": v(30.9, -62.01) * mm});
            skLineSegment(sketch, "E360", {"start": v(30.9, -62.01) * mm, "end": v(30.88, -61.91) * mm});
            skLineSegment(sketch, "E361", {"start": v(30.88, -61.91) * mm, "end": v(30.86, -61.81) * mm});
            skLineSegment(sketch, "E362", {"start": v(30.86, -61.81) * mm, "end": v(30.86, -61.71) * mm});
            skLineSegment(sketch, "E363", {"start": v(30.86, -61.71) * mm, "end": v(30.87, -61.6) * mm});
            skLineSegment(sketch, "E364", {"start": v(30.87, -61.6) * mm, "end": v(30.91, -61.49) * mm});
            skLineSegment(sketch, "E365", {"start": v(30.91, -61.49) * mm, "end": v(30.99, -61.38) * mm});
            skLineSegment(sketch, "E366", {"start": v(30.99, -61.38) * mm, "end": v(31.08, -61.29) * mm});
            skLineSegment(sketch, "E367", {"start": v(31.08, -61.29) * mm, "end": v(31.2, -61.22) * mm});
            skLineSegment(sketch, "E368", {"start": v(31.2, -61.22) * mm, "end": v(31.31, -61.17) * mm});
            skLineSegment(sketch, "E369", {"start": v(31.31, -61.17) * mm, "end": v(31.44, -61.15) * mm});
            skLineSegment(sketch, "E370", {"start": v(31.44, -61.15) * mm, "end": v(31.57, -61.15) * mm});
            skLineSegment(sketch, "E371", {"start": v(31.57, -61.15) * mm, "end": v(31.7, -61.19) * mm});
            skLineSegment(sketch, "E372", {"start": v(31.7, -61.19) * mm, "end": v(31.79, -61.24) * mm});
            skLineSegment(sketch, "E373", {"start": v(31.79, -61.24) * mm, "end": v(31.87, -61.3) * mm});
            skLineSegment(sketch, "E374", {"start": v(31.87, -61.3) * mm, "end": v(31.94, -61.37) * mm});
            skLineSegment(sketch, "E375", {"start": v(31.94, -61.37) * mm, "end": v(32, -61.45) * mm});
            skLineSegment(sketch, "E376", {"start": v(32, -61.45) * mm, "end": v(32.09, -61.5) * mm});
            skLineSegment(sketch, "E377", {"start": v(32.09, -61.5) * mm, "end": v(32.2, -61.49) * mm});
            skLineSegment(sketch, "E378", {"start": v(32.2, -61.49) * mm, "end": v(32.44, -61.36) * mm});
            skLineSegment(sketch, "E379", {"start": v(32.44, -61.36) * mm, "end": v(32.51, -61.28) * mm});
            skLineSegment(sketch, "E380", {"start": v(32.51, -61.28) * mm, "end": v(32.51, -61.18) * mm});
            skLineSegment(sketch, "E381", {"start": v(32.51, -61.18) * mm, "end": v(32.49, -61.08) * mm});
            skLineSegment(sketch, "E382", {"start": v(32.49, -61.08) * mm, "end": v(32.47, -60.99) * mm});
            skLineSegment(sketch, "E383", {"start": v(32.47, -60.99) * mm, "end": v(32.46, -60.88) * mm});
            skLineSegment(sketch, "E384", {"start": v(32.46, -60.88) * mm, "end": v(32.47, -60.78) * mm});
            skLineSegment(sketch, "E385", {"start": v(32.47, -60.78) * mm, "end": v(32.51, -60.66) * mm});
            skLineSegment(sketch, "E386", {"start": v(32.51, -60.66) * mm, "end": v(32.58, -60.55) * mm});
            skLineSegment(sketch, "E387", {"start": v(32.58, -60.55) * mm, "end": v(32.67, -60.45) * mm});
            skLineSegment(sketch, "E388", {"start": v(32.67, -60.45) * mm, "end": v(32.78, -60.38) * mm});
            skLineSegment(sketch, "E389", {"start": v(32.78, -60.38) * mm, "end": v(32.9, -60.33) * mm});
            skLineSegment(sketch, "E390", {"start": v(32.9, -60.33) * mm, "end": v(33.03, -60.3) * mm});
            skLineSegment(sketch, "E391", {"start": v(33.03, -60.3) * mm, "end": v(33.16, -60.3) * mm});
            skLineSegment(sketch, "E392", {"start": v(33.16, -60.3) * mm, "end": v(33.3, -60.34) * mm});
            skLineSegment(sketch, "E393", {"start": v(33.3, -60.34) * mm, "end": v(33.38, -60.39) * mm});
            skLineSegment(sketch, "E394", {"start": v(33.38, -60.39) * mm, "end": v(33.46, -60.45) * mm});
            skLineSegment(sketch, "E395", {"start": v(33.46, -60.45) * mm, "end": v(33.54, -60.51) * mm});
            skLineSegment(sketch, "E396", {"start": v(33.54, -60.51) * mm, "end": v(33.6, -60.6) * mm});
            skLineSegment(sketch, "E397", {"start": v(33.6, -60.6) * mm, "end": v(33.69, -60.64) * mm});
            skLineSegment(sketch, "E398", {"start": v(33.69, -60.64) * mm, "end": v(33.8, -60.62) * mm});
            skLineSegment(sketch, "E399", {"start": v(33.8, -60.62) * mm, "end": v(34.03, -60.49) * mm});
            skLineSegment(sketch, "E400", {"start": v(34.03, -60.49) * mm, "end": v(34.1, -60.4) * mm});
            skLineSegment(sketch, "E401", {"start": v(34.1, -60.4) * mm, "end": v(34.1, -60.3) * mm});
            skLineSegment(sketch, "E402", {"start": v(34.1, -60.3) * mm, "end": v(34.07, -60.21) * mm});
            skLineSegment(sketch, "E403", {"start": v(34.07, -60.21) * mm, "end": v(34.05, -60.11) * mm});
            skLineSegment(sketch, "E404", {"start": v(34.05, -60.11) * mm, "end": v(34.05, -60.01) * mm});
            skLineSegment(sketch, "E405", {"start": v(34.05, -60.01) * mm, "end": v(34.05, -59.9) * mm});
            skLineSegment(sketch, "E406", {"start": v(34.05, -59.9) * mm, "end": v(34.09, -59.78) * mm});
            skLineSegment(sketch, "E407", {"start": v(34.09, -59.78) * mm, "end": v(34.16, -59.67) * mm});
            skLineSegment(sketch, "E408", {"start": v(34.16, -59.67) * mm, "end": v(34.24, -59.58) * mm});
            skLineSegment(sketch, "E409", {"start": v(34.24, -59.58) * mm, "end": v(34.35, -59.5) * mm});
            skLineSegment(sketch, "E410", {"start": v(34.35, -59.5) * mm, "end": v(34.47, -59.44) * mm});
            skLineSegment(sketch, "E411", {"start": v(34.47, -59.44) * mm, "end": v(34.6, -59.42) * mm});
            skLineSegment(sketch, "E412", {"start": v(34.6, -59.42) * mm, "end": v(34.73, -59.41) * mm});
            skLineSegment(sketch, "E413", {"start": v(34.73, -59.41) * mm, "end": v(34.86, -59.44) * mm});
            skLineSegment(sketch, "E414", {"start": v(34.86, -59.44) * mm, "end": v(34.95, -59.5) * mm});
            skLineSegment(sketch, "E415", {"start": v(34.95, -59.5) * mm, "end": v(35.03, -59.55) * mm});
            skLineSegment(sketch, "E416", {"start": v(35.03, -59.55) * mm, "end": v(35.1, -59.62) * mm});
            skLineSegment(sketch, "E417", {"start": v(35.1, -59.62) * mm, "end": v(35.18, -59.7) * mm});
            skLineSegment(sketch, "E418", {"start": v(35.18, -59.7) * mm, "end": v(35.26, -59.74) * mm});
            skLineSegment(sketch, "E419", {"start": v(35.26, -59.74) * mm, "end": v(35.37, -59.72) * mm});
            skLineSegment(sketch, "E420", {"start": v(35.37, -59.72) * mm, "end": v(35.6, -59.58) * mm});
            skLineSegment(sketch, "E421", {"start": v(35.6, -59.58) * mm, "end": v(35.67, -59.5) * mm});
            skLineSegment(sketch, "E422", {"start": v(35.67, -59.5) * mm, "end": v(35.67, -59.4) * mm});
            skLineSegment(sketch, "E423", {"start": v(35.67, -59.4) * mm, "end": v(35.64, -59.3) * mm});
            skLineSegment(sketch, "E424", {"start": v(35.64, -59.3) * mm, "end": v(35.62, -59.2) * mm});
            skLineSegment(sketch, "E425", {"start": v(35.62, -59.2) * mm, "end": v(35.6, -59.1) * mm});
            skLineSegment(sketch, "E426", {"start": v(35.6, -59.1) * mm, "end": v(35.6, -59) * mm});
            skLineSegment(sketch, "E427", {"start": v(35.6, -59) * mm, "end": v(35.64, -58.87) * mm});
            skLineSegment(sketch, "E428", {"start": v(35.64, -58.87) * mm, "end": v(35.7, -58.76) * mm});
            skLineSegment(sketch, "E429", {"start": v(35.7, -58.76) * mm, "end": v(35.8, -58.66) * mm});
            skLineSegment(sketch, "E430", {"start": v(35.8, -58.66) * mm, "end": v(35.9, -58.58) * mm});
            skLineSegment(sketch, "E431", {"start": v(35.9, -58.58) * mm, "end": v(36.02, -58.52) * mm});
            skLineSegment(sketch, "E432", {"start": v(36.02, -58.52) * mm, "end": v(36.14, -58.49) * mm});
            skLineSegment(sketch, "E433", {"start": v(36.14, -58.49) * mm, "end": v(36.27, -58.49) * mm});
            skLineSegment(sketch, "E434", {"start": v(36.27, -58.49) * mm, "end": v(36.4, -58.51) * mm});
            skLineSegment(sketch, "E435", {"start": v(36.4, -58.51) * mm, "end": v(36.5, -58.56) * mm});
            skLineSegment(sketch, "E436", {"start": v(36.5, -58.56) * mm, "end": v(36.58, -58.61) * mm});
            skLineSegment(sketch, "E437", {"start": v(36.58, -58.61) * mm, "end": v(36.66, -58.68) * mm});
            skLineSegment(sketch, "E438", {"start": v(36.66, -58.68) * mm, "end": v(36.73, -58.75) * mm});
            skLineSegment(sketch, "E439", {"start": v(36.73, -58.75) * mm, "end": v(36.81, -58.8) * mm});
            skLineSegment(sketch, "E440", {"start": v(36.81, -58.8) * mm, "end": v(36.92, -58.77) * mm});
            skLineSegment(sketch, "E441", {"start": v(36.92, -58.77) * mm, "end": v(37.15, -58.62) * mm});
            skLineSegment(sketch, "E442", {"start": v(37.15, -58.62) * mm, "end": v(37.22, -58.54) * mm});
            skLineSegment(sketch, "E443", {"start": v(37.22, -58.54) * mm, "end": v(37.21, -58.44) * mm});
            skLineSegment(sketch, "E444", {"start": v(37.21, -58.44) * mm, "end": v(37.18, -58.35) * mm});
            skLineSegment(sketch, "E445", {"start": v(37.18, -58.35) * mm, "end": v(37.15, -58.25) * mm});
            skLineSegment(sketch, "E446", {"start": v(37.15, -58.25) * mm, "end": v(37.14, -58.15) * mm});
            skLineSegment(sketch, "E447", {"start": v(37.14, -58.15) * mm, "end": v(37.14, -58.05) * mm});
            skLineSegment(sketch, "E448", {"start": v(37.14, -58.05) * mm, "end": v(37.17, -57.92) * mm});
            skLineSegment(sketch, "E449", {"start": v(37.17, -57.92) * mm, "end": v(37.23, -57.8) * mm});
            skLineSegment(sketch, "E450", {"start": v(37.23, -57.8) * mm, "end": v(37.32, -57.7) * mm});
            skLineSegment(sketch, "E451", {"start": v(37.32, -57.7) * mm, "end": v(37.42, -57.62) * mm});
            skLineSegment(sketch, "E452", {"start": v(37.42, -57.62) * mm, "end": v(37.54, -57.56) * mm});
            skLineSegment(sketch, "E453", {"start": v(37.54, -57.56) * mm, "end": v(37.66, -57.52) * mm});
            skLineSegment(sketch, "E454", {"start": v(37.66, -57.52) * mm, "end": v(37.8, -57.52) * mm});
            skLineSegment(sketch, "E455", {"start": v(37.8, -57.52) * mm, "end": v(37.92, -57.54) * mm});
            skLineSegment(sketch, "E456", {"start": v(37.92, -57.54) * mm, "end": v(38.02, -57.58) * mm});
            skLineSegment(sketch, "E457", {"start": v(38.02, -57.58) * mm, "end": v(38.1, -57.63) * mm});
            skLineSegment(sketch, "E458", {"start": v(38.1, -57.63) * mm, "end": v(38.18, -57.7) * mm});
            skLineSegment(sketch, "E459", {"start": v(38.18, -57.7) * mm, "end": v(38.25, -57.77) * mm});
            skLineSegment(sketch, "E460", {"start": v(38.25, -57.77) * mm, "end": v(38.34, -57.81) * mm});
            skLineSegment(sketch, "E461", {"start": v(38.34, -57.81) * mm, "end": v(38.44, -57.78) * mm});
            skLineSegment(sketch, "E462", {"start": v(38.44, -57.78) * mm, "end": v(38.67, -57.63) * mm});
            skLineSegment(sketch, "E463", {"start": v(38.67, -57.63) * mm, "end": v(38.74, -57.55) * mm});
            skLineSegment(sketch, "E464", {"start": v(38.74, -57.55) * mm, "end": v(38.73, -57.45) * mm});
            skLineSegment(sketch, "E465", {"start": v(38.73, -57.45) * mm, "end": v(38.7, -57.35) * mm});
            skLineSegment(sketch, "E466", {"start": v(38.7, -57.35) * mm, "end": v(38.67, -57.26) * mm});
            skLineSegment(sketch, "E467", {"start": v(38.67, -57.26) * mm, "end": v(38.65, -57.16) * mm});
            skLineSegment(sketch, "E468", {"start": v(38.65, -57.16) * mm, "end": v(38.65, -57.05) * mm});
            skLineSegment(sketch, "E469", {"start": v(38.65, -57.05) * mm, "end": v(38.67, -56.93) * mm});
            skLineSegment(sketch, "E470", {"start": v(38.67, -56.93) * mm, "end": v(38.73, -56.8) * mm});
            skLineSegment(sketch, "E471", {"start": v(38.73, -56.8) * mm, "end": v(38.81, -56.7) * mm});
            skLineSegment(sketch, "E472", {"start": v(38.81, -56.7) * mm, "end": v(38.91, -56.62) * mm});
            skLineSegment(sketch, "E473", {"start": v(38.91, -56.62) * mm, "end": v(39.03, -56.56) * mm});
            skLineSegment(sketch, "E474", {"start": v(39.03, -56.56) * mm, "end": v(39.16, -56.52) * mm});
            skLineSegment(sketch, "E475", {"start": v(39.16, -56.52) * mm, "end": v(39.29, -56.5) * mm});
            skLineSegment(sketch, "E476", {"start": v(39.29, -56.5) * mm, "end": v(39.41, -56.53) * mm});
            skLineSegment(sketch, "E477", {"start": v(39.41, -56.53) * mm, "end": v(39.5, -56.57) * mm});
            skLineSegment(sketch, "E478", {"start": v(39.5, -56.57) * mm, "end": v(39.6, -56.62) * mm});
            skLineSegment(sketch, "E479", {"start": v(39.6, -56.62) * mm, "end": v(39.68, -56.68) * mm});
            skLineSegment(sketch, "E480", {"start": v(39.68, -56.68) * mm, "end": v(39.75, -56.75) * mm});
            skLineSegment(sketch, "E481", {"start": v(39.75, -56.75) * mm, "end": v(39.84, -56.79) * mm});
            skLineSegment(sketch, "E482", {"start": v(39.84, -56.79) * mm, "end": v(39.94, -56.76) * mm});
            skLineSegment(sketch, "E483", {"start": v(39.94, -56.76) * mm, "end": v(40.17, -56.6) * mm});
            skLineSegment(sketch, "E484", {"start": v(40.17, -56.6) * mm, "end": v(40.23, -56.51) * mm});
            skLineSegment(sketch, "E485", {"start": v(40.23, -56.51) * mm, "end": v(40.22, -56.41) * mm});
            skLineSegment(sketch, "E486", {"start": v(40.22, -56.41) * mm, "end": v(40.18, -56.32) * mm});
            skLineSegment(sketch, "E487", {"start": v(40.18, -56.32) * mm, "end": v(40.15, -56.23) * mm});
            skLineSegment(sketch, "E488", {"start": v(40.15, -56.23) * mm, "end": v(40.13, -56.13) * mm});
            skLineSegment(sketch, "E489", {"start": v(40.13, -56.13) * mm, "end": v(40.13, -56.02) * mm});
            skLineSegment(sketch, "E490", {"start": v(40.13, -56.02) * mm, "end": v(40.15, -55.9) * mm});
            skLineSegment(sketch, "E491", {"start": v(40.15, -55.9) * mm, "end": v(40.2, -55.78) * mm});
            skLineSegment(sketch, "E492", {"start": v(40.2, -55.78) * mm, "end": v(40.28, -55.67) * mm});
            skLineSegment(sketch, "E493", {"start": v(40.28, -55.67) * mm, "end": v(40.38, -55.58) * mm});
            skLineSegment(sketch, "E494", {"start": v(40.38, -55.58) * mm, "end": v(40.5, -55.52) * mm});
            skLineSegment(sketch, "E495", {"start": v(40.5, -55.52) * mm, "end": v(40.62, -55.47) * mm});
            skLineSegment(sketch, "E496", {"start": v(40.62, -55.47) * mm, "end": v(40.75, -55.46) * mm});
            skLineSegment(sketch, "E497", {"start": v(40.75, -55.46) * mm, "end": v(40.88, -55.47) * mm});
            skLineSegment(sketch, "E498", {"start": v(40.88, -55.47) * mm, "end": v(40.98, -55.51) * mm});
            skLineSegment(sketch, "E499", {"start": v(40.98, -55.51) * mm, "end": v(41.07, -55.56) * mm});
            skLineSegment(sketch, "E500", {"start": v(41.07, -55.56) * mm, "end": v(41.15, -55.62) * mm});
            skLineSegment(sketch, "E501", {"start": v(41.15, -55.62) * mm, "end": v(41.22, -55.69) * mm});
            skLineSegment(sketch, "E502", {"start": v(41.22, -55.69) * mm, "end": v(41.31, -55.73) * mm});
            skLineSegment(sketch, "E503", {"start": v(41.31, -55.73) * mm, "end": v(41.42, -55.7) * mm});
            skLineSegment(sketch, "E504", {"start": v(41.42, -55.7) * mm, "end": v(41.64, -55.53) * mm});
            skLineSegment(sketch, "E505", {"start": v(41.64, -55.53) * mm, "end": v(41.7, -55.44) * mm});
            skLineSegment(sketch, "E506", {"start": v(41.7, -55.44) * mm, "end": v(41.69, -55.34) * mm});
            skLineSegment(sketch, "E507", {"start": v(41.69, -55.34) * mm, "end": v(41.64, -55.25) * mm});
            skLineSegment(sketch, "E508", {"start": v(41.64, -55.25) * mm, "end": v(41.6, -55.16) * mm});
            skLineSegment(sketch, "E509", {"start": v(41.6, -55.16) * mm, "end": v(41.59, -55.06) * mm});
            skLineSegment(sketch, "E510", {"start": v(41.59, -55.06) * mm, "end": v(41.58, -54.95) * mm});
            skLineSegment(sketch, "E511", {"start": v(41.58, -54.95) * mm, "end": v(41.6, -54.82) * mm});
            skLineSegment(sketch, "E512", {"start": v(41.6, -54.82) * mm, "end": v(41.65, -54.7) * mm});
            skLineSegment(sketch, "E513", {"start": v(41.65, -54.7) * mm, "end": v(41.73, -54.6) * mm});
            skLineSegment(sketch, "E514", {"start": v(41.73, -54.6) * mm, "end": v(41.82, -54.5) * mm});
            skLineSegment(sketch, "E515", {"start": v(41.82, -54.5) * mm, "end": v(41.94, -54.44) * mm});
            skLineSegment(sketch, "E516", {"start": v(41.94, -54.44) * mm, "end": v(42.06, -54.4) * mm});
            skLineSegment(sketch, "E517", {"start": v(42.06, -54.4) * mm, "end": v(42.19, -54.37) * mm});
            skLineSegment(sketch, "E518", {"start": v(42.19, -54.37) * mm, "end": v(42.32, -54.38) * mm});
            skLineSegment(sketch, "E519", {"start": v(42.32, -54.38) * mm, "end": v(42.42, -54.42) * mm});
            skLineSegment(sketch, "E520", {"start": v(42.42, -54.42) * mm, "end": v(42.5, -54.47) * mm});
            skLineSegment(sketch, "E521", {"start": v(42.5, -54.47) * mm, "end": v(42.6, -54.52) * mm});
            skLineSegment(sketch, "E522", {"start": v(42.6, -54.52) * mm, "end": v(42.67, -54.59) * mm});
            skLineSegment(sketch, "E523", {"start": v(42.67, -54.59) * mm, "end": v(42.76, -54.62) * mm});
            skLineSegment(sketch, "E524", {"start": v(42.76, -54.62) * mm, "end": v(42.86, -54.59) * mm});
            skLineSegment(sketch, "E525", {"start": v(42.86, -54.59) * mm, "end": v(43.08, -54.42) * mm});
            skLineSegment(sketch, "E526", {"start": v(43.08, -54.42) * mm, "end": v(43.13, -54.33) * mm});
            skLineSegment(sketch, "E527", {"start": v(43.13, -54.33) * mm, "end": v(43.12, -54.23) * mm});
            skLineSegment(sketch, "E528", {"start": v(43.12, -54.23) * mm, "end": v(43.07, -54.14) * mm});
            skLineSegment(sketch, "E529", {"start": v(43.07, -54.14) * mm, "end": v(43.04, -54.05) * mm});
            skLineSegment(sketch, "E530", {"start": v(43.04, -54.05) * mm, "end": v(43.02, -53.95) * mm});
            skLineSegment(sketch, "E531", {"start": v(43.02, -53.95) * mm, "end": v(43, -53.85) * mm});
            skLineSegment(sketch, "E532", {"start": v(43, -53.85) * mm, "end": v(43.02, -53.72) * mm});
            skLineSegment(sketch, "E533", {"start": v(43.02, -53.72) * mm, "end": v(43.07, -53.6) * mm});
            skLineSegment(sketch, "E534", {"start": v(43.07, -53.6) * mm, "end": v(43.14, -53.49) * mm});
            skLineSegment(sketch, "E535", {"start": v(43.14, -53.49) * mm, "end": v(43.24, -53.4) * mm});
            skLineSegment(sketch, "E536", {"start": v(43.24, -53.4) * mm, "end": v(43.35, -53.32) * mm});
            skLineSegment(sketch, "E537", {"start": v(43.35, -53.32) * mm, "end": v(43.47, -53.27) * mm});
            skLineSegment(sketch, "E538", {"start": v(43.47, -53.27) * mm, "end": v(43.6, -53.25) * mm});
            skLineSegment(sketch, "E539", {"start": v(43.6, -53.25) * mm, "end": v(43.73, -53.26) * mm});
            skLineSegment(sketch, "E540", {"start": v(43.73, -53.26) * mm, "end": v(43.83, -53.3) * mm});
            skLineSegment(sketch, "E541", {"start": v(43.83, -53.3) * mm, "end": v(43.92, -53.34) * mm});
            skLineSegment(sketch, "E542", {"start": v(43.92, -53.34) * mm, "end": v(44, -53.39) * mm});
            skLineSegment(sketch, "E543", {"start": v(44, -53.39) * mm, "end": v(44.08, -53.45) * mm});
            skLineSegment(sketch, "E544", {"start": v(44.08, -53.45) * mm, "end": v(44.17, -53.49) * mm});
            skLineSegment(sketch, "E545", {"start": v(44.17, -53.49) * mm, "end": v(44.27, -53.45) * mm});
            skLineSegment(sketch, "E546", {"start": v(44.27, -53.45) * mm, "end": v(44.49, -53.27) * mm});
            skLineSegment(sketch, "E547", {"start": v(44.49, -53.27) * mm, "end": v(44.54, -53.18) * mm});
            skLineSegment(sketch, "E548", {"start": v(44.54, -53.18) * mm, "end": v(44.52, -53.08) * mm});
            skLineSegment(sketch, "E549", {"start": v(44.52, -53.08) * mm, "end": v(44.48, -53) * mm});
            skLineSegment(sketch, "E550", {"start": v(44.48, -53) * mm, "end": v(44.44, -52.9) * mm});
            skLineSegment(sketch, "E551", {"start": v(44.44, -52.9) * mm, "end": v(44.41, -52.8) * mm});
            skLineSegment(sketch, "E552", {"start": v(44.41, -52.8) * mm, "end": v(44.4, -52.7) * mm});
            skLineSegment(sketch, "E553", {"start": v(44.4, -52.7) * mm, "end": v(44.41, -52.57) * mm});
            skLineSegment(sketch, "E554", {"start": v(44.41, -52.57) * mm, "end": v(44.46, -52.45) * mm});
            skLineSegment(sketch, "E555", {"start": v(44.46, -52.45) * mm, "end": v(44.53, -52.34) * mm});
            skLineSegment(sketch, "E556", {"start": v(44.53, -52.34) * mm, "end": v(44.62, -52.24) * mm});
            skLineSegment(sketch, "E557", {"start": v(44.62, -52.24) * mm, "end": v(44.73, -52.17) * mm});
            skLineSegment(sketch, "E558", {"start": v(44.73, -52.17) * mm, "end": v(44.85, -52.12) * mm});
            skLineSegment(sketch, "E559", {"start": v(44.85, -52.12) * mm, "end": v(44.98, -52.1) * mm});
            skLineSegment(sketch, "E560", {"start": v(44.98, -52.1) * mm, "end": v(45.1, -52.1) * mm});
            skLineSegment(sketch, "E561", {"start": v(45.1, -52.1) * mm, "end": v(45.2, -52.13) * mm});
            skLineSegment(sketch, "E562", {"start": v(45.2, -52.13) * mm, "end": v(45.3, -52.17) * mm});
            skLineSegment(sketch, "E563", {"start": v(45.3, -52.17) * mm, "end": v(45.39, -52.22) * mm});
            skLineSegment(sketch, "E564", {"start": v(45.39, -52.22) * mm, "end": v(45.46, -52.28) * mm});
            skLineSegment(sketch, "E565", {"start": v(45.46, -52.28) * mm, "end": v(45.56, -52.31) * mm});
            skLineSegment(sketch, "E566", {"start": v(45.56, -52.31) * mm, "end": v(45.66, -52.27) * mm});
            skLineSegment(sketch, "E567", {"start": v(45.66, -52.27) * mm, "end": v(45.86, -52.1) * mm});
            skLineSegment(sketch, "E568", {"start": v(45.86, -52.1) * mm, "end": v(45.92, -52) * mm});
            skLineSegment(sketch, "E569", {"start": v(45.92, -52) * mm, "end": v(45.9, -51.9) * mm});
            skLineSegment(sketch, "E570", {"start": v(45.9, -51.9) * mm, "end": v(45.85, -51.81) * mm});
            skLineSegment(sketch, "E571", {"start": v(45.85, -51.81) * mm, "end": v(45.8, -51.72) * mm});
            skLineSegment(sketch, "E572", {"start": v(45.8, -51.72) * mm, "end": v(45.78, -51.62) * mm});
            skLineSegment(sketch, "E573", {"start": v(45.78, -51.62) * mm, "end": v(45.76, -51.52) * mm});
            skLineSegment(sketch, "E574", {"start": v(45.76, -51.52) * mm, "end": v(45.77, -51.4) * mm});
            skLineSegment(sketch, "E575", {"start": v(45.77, -51.4) * mm, "end": v(45.82, -51.27) * mm});
            skLineSegment(sketch, "E576", {"start": v(45.82, -51.27) * mm, "end": v(45.88, -51.15) * mm});
            skLineSegment(sketch, "E577", {"start": v(45.88, -51.15) * mm, "end": v(45.97, -51.06) * mm});
            skLineSegment(sketch, "E578", {"start": v(45.97, -51.06) * mm, "end": v(46.08, -50.98) * mm});
            skLineSegment(sketch, "E579", {"start": v(46.08, -50.98) * mm, "end": v(46.2, -50.92) * mm});
            skLineSegment(sketch, "E580", {"start": v(46.2, -50.92) * mm, "end": v(46.32, -50.9) * mm});
            skLineSegment(sketch, "E581", {"start": v(46.32, -50.9) * mm, "end": v(46.46, -50.9) * mm});
            skLineSegment(sketch, "E582", {"start": v(46.46, -50.9) * mm, "end": v(46.55, -50.93) * mm});
            skLineSegment(sketch, "E583", {"start": v(46.55, -50.93) * mm, "end": v(46.65, -50.96) * mm});
            skLineSegment(sketch, "E584", {"start": v(46.65, -50.96) * mm, "end": v(46.74, -51.01) * mm});
            skLineSegment(sketch, "E585", {"start": v(46.74, -51.01) * mm, "end": v(46.82, -51.07) * mm});
            skLineSegment(sketch, "E586", {"start": v(46.82, -51.07) * mm, "end": v(46.91, -51.1) * mm});
            skLineSegment(sketch, "E587", {"start": v(46.91, -51.1) * mm, "end": v(47.01, -51.06) * mm});
            skLineSegment(sketch, "E588", {"start": v(47.01, -51.06) * mm, "end": v(47.21, -50.87) * mm});
            skLineSegment(sketch, "E589", {"start": v(47.21, -50.87) * mm, "end": v(47.26, -50.78) * mm});
            skLineSegment(sketch, "E590", {"start": v(47.26, -50.78) * mm, "end": v(47.24, -50.68) * mm});
            skLineSegment(sketch, "E591", {"start": v(47.24, -50.68) * mm, "end": v(47.19, -50.6) * mm});
            skLineSegment(sketch, "E592", {"start": v(47.19, -50.6) * mm, "end": v(47.15, -50.5) * mm});
            skLineSegment(sketch, "E593", {"start": v(47.15, -50.5) * mm, "end": v(47.12, -50.4) * mm});
            skLineSegment(sketch, "E594", {"start": v(47.12, -50.4) * mm, "end": v(47.1, -50.3) * mm});
            skLineSegment(sketch, "E595", {"start": v(47.1, -50.3) * mm, "end": v(47.1, -50.18) * mm});
            skLineSegment(sketch, "E596", {"start": v(47.1, -50.18) * mm, "end": v(47.14, -50.05) * mm});
            skLineSegment(sketch, "E597", {"start": v(47.14, -50.05) * mm, "end": v(47.2, -49.94) * mm});
            skLineSegment(sketch, "E598", {"start": v(47.2, -49.94) * mm, "end": v(47.3, -49.84) * mm});
            skLineSegment(sketch, "E599", {"start": v(47.3, -49.84) * mm, "end": v(47.4, -49.75) * mm});
            skLineSegment(sketch, "E600", {"start": v(47.4, -49.75) * mm, "end": v(47.51, -49.7) * mm});
            skLineSegment(sketch, "E601", {"start": v(47.51, -49.7) * mm, "end": v(47.64, -49.67) * mm});
            skLineSegment(sketch, "E602", {"start": v(47.64, -49.67) * mm, "end": v(47.77, -49.66) * mm});
            skLineSegment(sketch, "E603", {"start": v(47.77, -49.66) * mm, "end": v(47.87, -49.69) * mm});
            skLineSegment(sketch, "E604", {"start": v(47.87, -49.69) * mm, "end": v(47.97, -49.73) * mm});
            skLineSegment(sketch, "E605", {"start": v(47.97, -49.73) * mm, "end": v(48.06, -49.77) * mm});
            skLineSegment(sketch, "E606", {"start": v(48.06, -49.77) * mm, "end": v(48.14, -49.83) * mm});
            skLineSegment(sketch, "E607", {"start": v(48.14, -49.83) * mm, "end": v(48.23, -49.86) * mm});
            skLineSegment(sketch, "E608", {"start": v(48.23, -49.86) * mm, "end": v(48.33, -49.81) * mm});
            skLineSegment(sketch, "E609", {"start": v(48.33, -49.81) * mm, "end": v(48.53, -49.62) * mm});
            skLineSegment(sketch, "E610", {"start": v(48.53, -49.62) * mm, "end": v(48.58, -49.52) * mm});
            skLineSegment(sketch, "E611", {"start": v(48.58, -49.52) * mm, "end": v(48.55, -49.43) * mm});
            skLineSegment(sketch, "E612", {"start": v(48.55, -49.43) * mm, "end": v(48.5, -49.34) * mm});
            skLineSegment(sketch, "E613", {"start": v(48.5, -49.34) * mm, "end": v(48.45, -49.25) * mm});
            skLineSegment(sketch, "E614", {"start": v(48.45, -49.25) * mm, "end": v(48.42, -49.16) * mm});
            skLineSegment(sketch, "E615", {"start": v(48.42, -49.16) * mm, "end": v(48.4, -49.06) * mm});
            skLineSegment(sketch, "E616", {"start": v(48.4, -49.06) * mm, "end": v(48.4, -48.92) * mm});
            skLineSegment(sketch, "E617", {"start": v(48.4, -48.92) * mm, "end": v(48.44, -48.8) * mm});
            skLineSegment(sketch, "E618", {"start": v(48.44, -48.8) * mm, "end": v(48.5, -48.68) * mm});
            skLineSegment(sketch, "E619", {"start": v(48.5, -48.68) * mm, "end": v(48.58, -48.58) * mm});
            skLineSegment(sketch, "E620", {"start": v(48.58, -48.58) * mm, "end": v(48.68, -48.5) * mm});
            skLineSegment(sketch, "E621", {"start": v(48.68, -48.5) * mm, "end": v(48.8, -48.44) * mm});
            skLineSegment(sketch, "E622", {"start": v(48.8, -48.44) * mm, "end": v(48.92, -48.4) * mm});
            skLineSegment(sketch, "E623", {"start": v(48.92, -48.4) * mm, "end": v(49.06, -48.4) * mm});
            skLineSegment(sketch, "E624", {"start": v(49.06, -48.4) * mm, "end": v(49.16, -48.42) * mm});
            skLineSegment(sketch, "E625", {"start": v(49.16, -48.42) * mm, "end": v(49.25, -48.45) * mm});
            skLineSegment(sketch, "E626", {"start": v(49.25, -48.45) * mm, "end": v(49.34, -48.5) * mm});
            skLineSegment(sketch, "E627", {"start": v(49.34, -48.5) * mm, "end": v(49.43, -48.55) * mm});
            skLineSegment(sketch, "E628", {"start": v(49.43, -48.55) * mm, "end": v(49.52, -48.58) * mm});
            skLineSegment(sketch, "E629", {"start": v(49.52, -48.58) * mm, "end": v(49.62, -48.53) * mm});
            skLineSegment(sketch, "E630", {"start": v(49.62, -48.53) * mm, "end": v(49.81, -48.33) * mm});
            skLineSegment(sketch, "E631", {"start": v(49.81, -48.33) * mm, "end": v(49.86, -48.23) * mm});
            skLineSegment(sketch, "E632", {"start": v(49.86, -48.23) * mm, "end": v(49.83, -48.14) * mm});
            skLineSegment(sketch, "E633", {"start": v(49.83, -48.14) * mm, "end": v(49.77, -48.06) * mm});
            skLineSegment(sketch, "E634", {"start": v(49.77, -48.06) * mm, "end": v(49.73, -47.97) * mm});
            skLineSegment(sketch, "E635", {"start": v(49.73, -47.97) * mm, "end": v(49.69, -47.87) * mm});
            skLineSegment(sketch, "E636", {"start": v(49.69, -47.87) * mm, "end": v(49.66, -47.77) * mm});
            skLineSegment(sketch, "E637", {"start": v(49.66, -47.77) * mm, "end": v(49.67, -47.64) * mm});
            skLineSegment(sketch, "E638", {"start": v(49.67, -47.64) * mm, "end": v(49.7, -47.51) * mm});
            skLineSegment(sketch, "E639", {"start": v(49.7, -47.51) * mm, "end": v(49.75, -47.4) * mm});
            skLineSegment(sketch, "E640", {"start": v(49.75, -47.4) * mm, "end": v(49.84, -47.3) * mm});
            skLineSegment(sketch, "E641", {"start": v(49.84, -47.3) * mm, "end": v(49.94, -47.2) * mm});
            skLineSegment(sketch, "E642", {"start": v(49.94, -47.2) * mm, "end": v(50.05, -47.14) * mm});
            skLineSegment(sketch, "E643", {"start": v(50.05, -47.14) * mm, "end": v(50.18, -47.1) * mm});
            skLineSegment(sketch, "E644", {"start": v(50.18, -47.1) * mm, "end": v(50.3, -47.1) * mm});
            skLineSegment(sketch, "E645", {"start": v(50.3, -47.1) * mm, "end": v(50.4, -47.12) * mm});
            skLineSegment(sketch, "E646", {"start": v(50.4, -47.12) * mm, "end": v(50.5, -47.15) * mm});
            skLineSegment(sketch, "E647", {"start": v(50.5, -47.15) * mm, "end": v(50.6, -47.19) * mm});
            skLineSegment(sketch, "E648", {"start": v(50.6, -47.19) * mm, "end": v(50.68, -47.24) * mm});
            skLineSegment(sketch, "E649", {"start": v(50.68, -47.24) * mm, "end": v(50.78, -47.26) * mm});
            skLineSegment(sketch, "E650", {"start": v(50.78, -47.26) * mm, "end": v(50.87, -47.21) * mm});
            skLineSegment(sketch, "E651", {"start": v(50.87, -47.21) * mm, "end": v(51.06, -47.01) * mm});
            skLineSegment(sketch, "E652", {"start": v(51.06, -47.01) * mm, "end": v(51.1, -46.91) * mm});
            skLineSegment(sketch, "E653", {"start": v(51.1, -46.91) * mm, "end": v(51.07, -46.82) * mm});
            skLineSegment(sketch, "E654", {"start": v(51.07, -46.82) * mm, "end": v(51.01, -46.74) * mm});
            skLineSegment(sketch, "E655", {"start": v(51.01, -46.74) * mm, "end": v(50.96, -46.65) * mm});
            skLineSegment(sketch, "E656", {"start": v(50.96, -46.65) * mm, "end": v(50.93, -46.56) * mm});
            skLineSegment(sketch, "E657", {"start": v(50.93, -46.56) * mm, "end": v(50.9, -46.46) * mm});
            skLineSegment(sketch, "E658", {"start": v(50.9, -46.46) * mm, "end": v(50.9, -46.32) * mm});
            skLineSegment(sketch, "E659", {"start": v(50.9, -46.32) * mm, "end": v(50.92, -46.2) * mm});
            skLineSegment(sketch, "E660", {"start": v(50.92, -46.2) * mm, "end": v(50.98, -46.08) * mm});
            skLineSegment(sketch, "E661", {"start": v(50.98, -46.08) * mm, "end": v(51.06, -45.97) * mm});
            skLineSegment(sketch, "E662", {"start": v(51.06, -45.97) * mm, "end": v(51.15, -45.88) * mm});
            skLineSegment(sketch, "E663", {"start": v(51.15, -45.88) * mm, "end": v(51.27, -45.82) * mm});
            skLineSegment(sketch, "E664", {"start": v(51.27, -45.82) * mm, "end": v(51.4, -45.77) * mm});
            skLineSegment(sketch, "E665", {"start": v(51.4, -45.77) * mm, "end": v(51.52, -45.76) * mm});
            skLineSegment(sketch, "E666", {"start": v(51.52, -45.76) * mm, "end": v(51.62, -45.78) * mm});
            skLineSegment(sketch, "E667", {"start": v(51.62, -45.78) * mm, "end": v(51.72, -45.8) * mm});
            skLineSegment(sketch, "E668", {"start": v(51.72, -45.8) * mm, "end": v(51.81, -45.85) * mm});
            skLineSegment(sketch, "E669", {"start": v(51.81, -45.85) * mm, "end": v(51.9, -45.9) * mm});
            skLineSegment(sketch, "E670", {"start": v(51.9, -45.9) * mm, "end": v(52, -45.92) * mm});
            skLineSegment(sketch, "E671", {"start": v(52, -45.92) * mm, "end": v(52.1, -45.86) * mm});
            skLineSegment(sketch, "E672", {"start": v(52.1, -45.86) * mm, "end": v(52.27, -45.66) * mm});
            skLineSegment(sketch, "E673", {"start": v(52.27, -45.66) * mm, "end": v(52.31, -45.56) * mm});
            skLineSegment(sketch, "E674", {"start": v(52.31, -45.56) * mm, "end": v(52.28, -45.46) * mm});
            skLineSegment(sketch, "E675", {"start": v(52.28, -45.46) * mm, "end": v(52.22, -45.39) * mm});
            skLineSegment(sketch, "E676", {"start": v(52.22, -45.39) * mm, "end": v(52.17, -45.3) * mm});
            skLineSegment(sketch, "E677", {"start": v(52.17, -45.3) * mm, "end": v(52.13, -45.2) * mm});
            skLineSegment(sketch, "E678", {"start": v(52.13, -45.2) * mm, "end": v(52.1, -45.1) * mm});
            skLineSegment(sketch, "E679", {"start": v(52.1, -45.1) * mm, "end": v(52.1, -44.98) * mm});
            skLineSegment(sketch, "E680", {"start": v(52.1, -44.98) * mm, "end": v(52.12, -44.85) * mm});
            skLineSegment(sketch, "E681", {"start": v(52.12, -44.85) * mm, "end": v(52.17, -44.73) * mm});
            skLineSegment(sketch, "E682", {"start": v(52.17, -44.73) * mm, "end": v(52.24, -44.62) * mm});
            skLineSegment(sketch, "E683", {"start": v(52.24, -44.62) * mm, "end": v(52.34, -44.53) * mm});
            skLineSegment(sketch, "E684", {"start": v(52.34, -44.53) * mm, "end": v(52.45, -44.46) * mm});
            skLineSegment(sketch, "E685", {"start": v(52.45, -44.46) * mm, "end": v(52.57, -44.41) * mm});
            skLineSegment(sketch, "E686", {"start": v(52.57, -44.41) * mm, "end": v(52.7, -44.4) * mm});
            skLineSegment(sketch, "E687", {"start": v(52.7, -44.4) * mm, "end": v(52.8, -44.41) * mm});
            skLineSegment(sketch, "E688", {"start": v(52.8, -44.41) * mm, "end": v(52.9, -44.44) * mm});
            skLineSegment(sketch, "E689", {"start": v(52.9, -44.44) * mm, "end": v(53, -44.48) * mm});
            skLineSegment(sketch, "E690", {"start": v(53, -44.48) * mm, "end": v(53.08, -44.52) * mm});
            skLineSegment(sketch, "E691", {"start": v(53.08, -44.52) * mm, "end": v(53.18, -44.54) * mm});
            skLineSegment(sketch, "E692", {"start": v(53.18, -44.54) * mm, "end": v(53.27, -44.49) * mm});
            skLineSegment(sketch, "E693", {"start": v(53.27, -44.49) * mm, "end": v(53.45, -44.27) * mm});
            skLineSegment(sketch, "E694", {"start": v(53.45, -44.27) * mm, "end": v(53.49, -44.17) * mm});
            skLineSegment(sketch, "E695", {"start": v(53.49, -44.17) * mm, "end": v(53.45, -44.08) * mm});
            skLineSegment(sketch, "E696", {"start": v(53.45, -44.08) * mm, "end": v(53.39, -44) * mm});
            skLineSegment(sketch, "E697", {"start": v(53.39, -44) * mm, "end": v(53.34, -43.92) * mm});
            skLineSegment(sketch, "E698", {"start": v(53.34, -43.92) * mm, "end": v(53.3, -43.83) * mm});
            skLineSegment(sketch, "E699", {"start": v(53.3, -43.83) * mm, "end": v(53.26, -43.73) * mm});
            skLineSegment(sketch, "E700", {"start": v(53.26, -43.73) * mm, "end": v(53.25, -43.6) * mm});
            skLineSegment(sketch, "E701", {"start": v(53.25, -43.6) * mm, "end": v(53.27, -43.47) * mm});
            skLineSegment(sketch, "E702", {"start": v(53.27, -43.47) * mm, "end": v(53.32, -43.35) * mm});
            skLineSegment(sketch, "E703", {"start": v(53.32, -43.35) * mm, "end": v(53.4, -43.24) * mm});
            skLineSegment(sketch, "E704", {"start": v(53.4, -43.24) * mm, "end": v(53.49, -43.14) * mm});
            skLineSegment(sketch, "E705", {"start": v(53.49, -43.14) * mm, "end": v(53.6, -43.07) * mm});
            skLineSegment(sketch, "E706", {"start": v(53.6, -43.07) * mm, "end": v(53.72, -43.02) * mm});
            skLineSegment(sketch, "E707", {"start": v(53.72, -43.02) * mm, "end": v(53.85, -43) * mm});
            skLineSegment(sketch, "E708", {"start": v(53.85, -43) * mm, "end": v(53.95, -43.02) * mm});
            skLineSegment(sketch, "E709", {"start": v(53.95, -43.02) * mm, "end": v(54.05, -43.04) * mm});
            skLineSegment(sketch, "E710", {"start": v(54.05, -43.04) * mm, "end": v(54.14, -43.07) * mm});
            skLineSegment(sketch, "E711", {"start": v(54.14, -43.07) * mm, "end": v(54.23, -43.12) * mm});
            skLineSegment(sketch, "E712", {"start": v(54.23, -43.12) * mm, "end": v(54.33, -43.13) * mm});
            skLineSegment(sketch, "E713", {"start": v(54.33, -43.13) * mm, "end": v(54.42, -43.08) * mm});
            skLineSegment(sketch, "E714", {"start": v(54.42, -43.08) * mm, "end": v(54.59, -42.86) * mm});
            skLineSegment(sketch, "E715", {"start": v(54.59, -42.86) * mm, "end": v(54.62, -42.76) * mm});
            skLineSegment(sketch, "E716", {"start": v(54.62, -42.76) * mm, "end": v(54.59, -42.67) * mm});
            skLineSegment(sketch, "E717", {"start": v(54.59, -42.67) * mm, "end": v(54.52, -42.6) * mm});
            skLineSegment(sketch, "E718", {"start": v(54.52, -42.6) * mm, "end": v(54.47, -42.5) * mm});
            skLineSegment(sketch, "E719", {"start": v(54.47, -42.5) * mm, "end": v(54.42, -42.42) * mm});
            skLineSegment(sketch, "E720", {"start": v(54.42, -42.42) * mm, "end": v(54.38, -42.32) * mm});
            skLineSegment(sketch, "E721", {"start": v(54.38, -42.32) * mm, "end": v(54.37, -42.19) * mm});
            skLineSegment(sketch, "E722", {"start": v(54.37, -42.19) * mm, "end": v(54.4, -42.06) * mm});
            skLineSegment(sketch, "E723", {"start": v(54.4, -42.06) * mm, "end": v(54.44, -41.94) * mm});
            skLineSegment(sketch, "E724", {"start": v(54.44, -41.94) * mm, "end": v(54.5, -41.82) * mm});
            skLineSegment(sketch, "E725", {"start": v(54.5, -41.82) * mm, "end": v(54.6, -41.73) * mm});
            skLineSegment(sketch, "E726", {"start": v(54.6, -41.73) * mm, "end": v(54.7, -41.65) * mm});
            skLineSegment(sketch, "E727", {"start": v(54.7, -41.65) * mm, "end": v(54.82, -41.6) * mm});
            skLineSegment(sketch, "E728", {"start": v(54.82, -41.6) * mm, "end": v(54.95, -41.58) * mm});
            skLineSegment(sketch, "E729", {"start": v(54.95, -41.58) * mm, "end": v(55.06, -41.59) * mm});
            skLineSegment(sketch, "E730", {"start": v(55.06, -41.59) * mm, "end": v(55.16, -41.6) * mm});
            skLineSegment(sketch, "E731", {"start": v(55.16, -41.6) * mm, "end": v(55.25, -41.64) * mm});
            skLineSegment(sketch, "E732", {"start": v(55.25, -41.64) * mm, "end": v(55.34, -41.69) * mm});
            skLineSegment(sketch, "E733", {"start": v(55.34, -41.69) * mm, "end": v(55.44, -41.7) * mm});
            skLineSegment(sketch, "E734", {"start": v(55.44, -41.7) * mm, "end": v(55.53, -41.64) * mm});
            skLineSegment(sketch, "E735", {"start": v(55.53, -41.64) * mm, "end": v(55.7, -41.42) * mm});
            skLineSegment(sketch, "E736", {"start": v(55.7, -41.42) * mm, "end": v(55.73, -41.31) * mm});
            skLineSegment(sketch, "E737", {"start": v(55.73, -41.31) * mm, "end": v(55.69, -41.22) * mm});
            skLineSegment(sketch, "E738", {"start": v(55.69, -41.22) * mm, "end": v(55.62, -41.15) * mm});
            skLineSegment(sketch, "E739", {"start": v(55.62, -41.15) * mm, "end": v(55.56, -41.07) * mm});
            skLineSegment(sketch, "E740", {"start": v(55.56, -41.07) * mm, "end": v(55.51, -40.98) * mm});
            skLineSegment(sketch, "E741", {"start": v(55.51, -40.98) * mm, "end": v(55.47, -40.88) * mm});
            skLineSegment(sketch, "E742", {"start": v(55.47, -40.88) * mm, "end": v(55.46, -40.75) * mm});
            skLineSegment(sketch, "E743", {"start": v(55.46, -40.75) * mm, "end": v(55.47, -40.62) * mm});
            skLineSegment(sketch, "E744", {"start": v(55.47, -40.62) * mm, "end": v(55.52, -40.5) * mm});
            skLineSegment(sketch, "E745", {"start": v(55.52, -40.5) * mm, "end": v(55.58, -40.38) * mm});
            skLineSegment(sketch, "E746", {"start": v(55.58, -40.38) * mm, "end": v(55.67, -40.28) * mm});
            skLineSegment(sketch, "E747", {"start": v(55.67, -40.28) * mm, "end": v(55.78, -40.2) * mm});
            skLineSegment(sketch, "E748", {"start": v(55.78, -40.2) * mm, "end": v(55.9, -40.15) * mm});
            skLineSegment(sketch, "E749", {"start": v(55.9, -40.15) * mm, "end": v(56.02, -40.13) * mm});
            skLineSegment(sketch, "E750", {"start": v(56.02, -40.13) * mm, "end": v(56.13, -40.13) * mm});
            skLineSegment(sketch, "E751", {"start": v(56.13, -40.13) * mm, "end": v(56.23, -40.15) * mm});
            skLineSegment(sketch, "E752", {"start": v(56.23, -40.15) * mm, "end": v(56.32, -40.18) * mm});
            skLineSegment(sketch, "E753", {"start": v(56.32, -40.18) * mm, "end": v(56.41, -40.22) * mm});
            skLineSegment(sketch, "E754", {"start": v(56.41, -40.22) * mm, "end": v(56.51, -40.23) * mm});
            skLineSegment(sketch, "E755", {"start": v(56.51, -40.23) * mm, "end": v(56.6, -40.17) * mm});
            skLineSegment(sketch, "E756", {"start": v(56.6, -40.17) * mm, "end": v(56.76, -39.94) * mm});
            skLineSegment(sketch, "E757", {"start": v(56.76, -39.94) * mm, "end": v(56.79, -39.84) * mm});
            skLineSegment(sketch, "E758", {"start": v(56.79, -39.84) * mm, "end": v(56.75, -39.75) * mm});
            skLineSegment(sketch, "E759", {"start": v(56.75, -39.75) * mm, "end": v(56.68, -39.68) * mm});
            skLineSegment(sketch, "E760", {"start": v(56.68, -39.68) * mm, "end": v(56.62, -39.6) * mm});
            skLineSegment(sketch, "E761", {"start": v(56.62, -39.6) * mm, "end": v(56.57, -39.5) * mm});
            skLineSegment(sketch, "E762", {"start": v(56.57, -39.5) * mm, "end": v(56.53, -39.41) * mm});
            skLineSegment(sketch, "E763", {"start": v(56.53, -39.41) * mm, "end": v(56.5, -39.29) * mm});
            skLineSegment(sketch, "E764", {"start": v(56.5, -39.29) * mm, "end": v(56.52, -39.16) * mm});
            skLineSegment(sketch, "E765", {"start": v(56.52, -39.16) * mm, "end": v(56.56, -39.03) * mm});
            skLineSegment(sketch, "E766", {"start": v(56.56, -39.03) * mm, "end": v(56.62, -38.91) * mm});
            skLineSegment(sketch, "E767", {"start": v(56.62, -38.91) * mm, "end": v(56.7, -38.81) * mm});
            skLineSegment(sketch, "E768", {"start": v(56.7, -38.81) * mm, "end": v(56.8, -38.73) * mm});
            skLineSegment(sketch, "E769", {"start": v(56.8, -38.73) * mm, "end": v(56.93, -38.67) * mm});
            skLineSegment(sketch, "E770", {"start": v(56.93, -38.67) * mm, "end": v(57.05, -38.65) * mm});
            skLineSegment(sketch, "E771", {"start": v(57.05, -38.65) * mm, "end": v(57.16, -38.65) * mm});
            skLineSegment(sketch, "E772", {"start": v(57.16, -38.65) * mm, "end": v(57.26, -38.67) * mm});
            skLineSegment(sketch, "E773", {"start": v(57.26, -38.67) * mm, "end": v(57.35, -38.7) * mm});
            skLineSegment(sketch, "E774", {"start": v(57.35, -38.7) * mm, "end": v(57.45, -38.73) * mm});
            skLineSegment(sketch, "E775", {"start": v(57.45, -38.73) * mm, "end": v(57.55, -38.74) * mm});
            skLineSegment(sketch, "E776", {"start": v(57.55, -38.74) * mm, "end": v(57.63, -38.67) * mm});
            skLineSegment(sketch, "E777", {"start": v(57.63, -38.67) * mm, "end": v(57.78, -38.44) * mm});
            skLineSegment(sketch, "E778", {"start": v(57.78, -38.44) * mm, "end": v(57.81, -38.34) * mm});
            skLineSegment(sketch, "E779", {"start": v(57.81, -38.34) * mm, "end": v(57.77, -38.25) * mm});
            skLineSegment(sketch, "E780", {"start": v(57.77, -38.25) * mm, "end": v(57.7, -38.18) * mm});
            skLineSegment(sketch, "E781", {"start": v(57.7, -38.18) * mm, "end": v(57.63, -38.1) * mm});
            skLineSegment(sketch, "E782", {"start": v(57.63, -38.1) * mm, "end": v(57.58, -38.02) * mm});
            skLineSegment(sketch, "E783", {"start": v(57.58, -38.02) * mm, "end": v(57.54, -37.92) * mm});
            skLineSegment(sketch, "E784", {"start": v(57.54, -37.92) * mm, "end": v(57.52, -37.8) * mm});
            skLineSegment(sketch, "E785", {"start": v(57.52, -37.8) * mm, "end": v(57.52, -37.66) * mm});
            skLineSegment(sketch, "E786", {"start": v(57.52, -37.66) * mm, "end": v(57.56, -37.54) * mm});
            skLineSegment(sketch, "E787", {"start": v(57.56, -37.54) * mm, "end": v(57.62, -37.42) * mm});
            skLineSegment(sketch, "E788", {"start": v(57.62, -37.42) * mm, "end": v(57.7, -37.32) * mm});
            skLineSegment(sketch, "E789", {"start": v(57.7, -37.32) * mm, "end": v(57.8, -37.23) * mm});
            skLineSegment(sketch, "E790", {"start": v(57.8, -37.23) * mm, "end": v(57.92, -37.17) * mm});
            skLineSegment(sketch, "E791", {"start": v(57.92, -37.17) * mm, "end": v(58.05, -37.14) * mm});
            skLineSegment(sketch, "E792", {"start": v(58.05, -37.14) * mm, "end": v(58.15, -37.14) * mm});
            skLineSegment(sketch, "E793", {"start": v(58.15, -37.14) * mm, "end": v(58.25, -37.15) * mm});
            skLineSegment(sketch, "E794", {"start": v(58.25, -37.15) * mm, "end": v(58.35, -37.18) * mm});
            skLineSegment(sketch, "E795", {"start": v(58.35, -37.18) * mm, "end": v(58.44, -37.21) * mm});
            skLineSegment(sketch, "E796", {"start": v(58.44, -37.21) * mm, "end": v(58.54, -37.22) * mm});
            skLineSegment(sketch, "E797", {"start": v(58.54, -37.22) * mm, "end": v(58.62, -37.15) * mm});
            skLineSegment(sketch, "E798", {"start": v(58.62, -37.15) * mm, "end": v(58.77, -36.92) * mm});
            skLineSegment(sketch, "E799", {"start": v(58.77, -36.92) * mm, "end": v(58.8, -36.82) * mm});
            skLineSegment(sketch, "E800", {"start": v(58.8, -36.82) * mm, "end": v(58.75, -36.73) * mm});
            skLineSegment(sketch, "E801", {"start": v(58.75, -36.73) * mm, "end": v(58.68, -36.66) * mm});
            skLineSegment(sketch, "E802", {"start": v(58.68, -36.66) * mm, "end": v(58.61, -36.58) * mm});
            skLineSegment(sketch, "E803", {"start": v(58.61, -36.58) * mm, "end": v(58.56, -36.5) * mm});
            skLineSegment(sketch, "E804", {"start": v(58.56, -36.5) * mm, "end": v(58.51, -36.4) * mm});
            skLineSegment(sketch, "E805", {"start": v(58.51, -36.4) * mm, "end": v(58.49, -36.27) * mm});
            skLineSegment(sketch, "E806", {"start": v(58.49, -36.27) * mm, "end": v(58.49, -36.14) * mm});
            skLineSegment(sketch, "E807", {"start": v(58.49, -36.14) * mm, "end": v(58.52, -36.02) * mm});
            skLineSegment(sketch, "E808", {"start": v(58.52, -36.02) * mm, "end": v(58.58, -35.9) * mm});
            skLineSegment(sketch, "E809", {"start": v(58.58, -35.9) * mm, "end": v(58.66, -35.8) * mm});
            skLineSegment(sketch, "E810", {"start": v(58.66, -35.8) * mm, "end": v(58.76, -35.7) * mm});
            skLineSegment(sketch, "E811", {"start": v(58.76, -35.7) * mm, "end": v(58.87, -35.64) * mm});
            skLineSegment(sketch, "E812", {"start": v(58.87, -35.64) * mm, "end": v(59, -35.6) * mm});
            skLineSegment(sketch, "E813", {"start": v(59, -35.6) * mm, "end": v(59.1, -35.6) * mm});
            skLineSegment(sketch, "E814", {"start": v(59.1, -35.6) * mm, "end": v(59.2, -35.62) * mm});
            skLineSegment(sketch, "E815", {"start": v(59.2, -35.62) * mm, "end": v(59.3, -35.64) * mm});
            skLineSegment(sketch, "E816", {"start": v(59.3, -35.64) * mm, "end": v(59.4, -35.67) * mm});
            skLineSegment(sketch, "E817", {"start": v(59.4, -35.67) * mm, "end": v(59.5, -35.67) * mm});
            skLineSegment(sketch, "E818", {"start": v(59.5, -35.67) * mm, "end": v(59.58, -35.6) * mm});
            skLineSegment(sketch, "E819", {"start": v(59.58, -35.6) * mm, "end": v(59.72, -35.37) * mm});
            skLineSegment(sketch, "E820", {"start": v(59.72, -35.37) * mm, "end": v(59.74, -35.26) * mm});
            skLineSegment(sketch, "E821", {"start": v(59.74, -35.26) * mm, "end": v(59.7, -35.18) * mm});
            skLineSegment(sketch, "E822", {"start": v(59.7, -35.18) * mm, "end": v(59.62, -35.1) * mm});
            skLineSegment(sketch, "E823", {"start": v(59.62, -35.1) * mm, "end": v(59.55, -35.03) * mm});
            skLineSegment(sketch, "E824", {"start": v(59.55, -35.03) * mm, "end": v(59.5, -34.95) * mm});
            skLineSegment(sketch, "E825", {"start": v(59.5, -34.95) * mm, "end": v(59.44, -34.86) * mm});
            skLineSegment(sketch, "E826", {"start": v(59.44, -34.86) * mm, "end": v(59.41, -34.73) * mm});
            skLineSegment(sketch, "E827", {"start": v(59.41, -34.73) * mm, "end": v(59.42, -34.6) * mm});
            skLineSegment(sketch, "E828", {"start": v(59.42, -34.6) * mm, "end": v(59.44, -34.47) * mm});
            skLineSegment(sketch, "E829", {"start": v(59.44, -34.47) * mm, "end": v(59.5, -34.35) * mm});
            skLineSegment(sketch, "E830", {"start": v(59.5, -34.35) * mm, "end": v(59.58, -34.24) * mm});
            skLineSegment(sketch, "E831", {"start": v(59.58, -34.24) * mm, "end": v(59.67, -34.16) * mm});
            skLineSegment(sketch, "E832", {"start": v(59.67, -34.16) * mm, "end": v(59.78, -34.09) * mm});
            skLineSegment(sketch, "E833", {"start": v(59.78, -34.09) * mm, "end": v(59.9, -34.05) * mm});
            skLineSegment(sketch, "E834", {"start": v(59.9, -34.05) * mm, "end": v(60.01, -34.05) * mm});
            skLineSegment(sketch, "E835", {"start": v(60.01, -34.05) * mm, "end": v(60.11, -34.05) * mm});
            skLineSegment(sketch, "E836", {"start": v(60.11, -34.05) * mm, "end": v(60.21, -34.07) * mm});
            skLineSegment(sketch, "E837", {"start": v(60.21, -34.07) * mm, "end": v(60.3, -34.1) * mm});
            skLineSegment(sketch, "E838", {"start": v(60.3, -34.1) * mm, "end": v(60.4, -34.1) * mm});
            skLineSegment(sketch, "E839", {"start": v(60.4, -34.1) * mm, "end": v(60.49, -34.03) * mm});
            skLineSegment(sketch, "E840", {"start": v(60.49, -34.03) * mm, "end": v(60.62, -33.8) * mm});
            skLineSegment(sketch, "E841", {"start": v(60.62, -33.8) * mm, "end": v(60.64, -33.69) * mm});
            skLineSegment(sketch, "E842", {"start": v(60.64, -33.69) * mm, "end": v(60.6, -33.6) * mm});
            skLineSegment(sketch, "E843", {"start": v(60.6, -33.6) * mm, "end": v(60.51, -33.54) * mm});
            skLineSegment(sketch, "E844", {"start": v(60.51, -33.54) * mm, "end": v(60.45, -33.46) * mm});
            skLineSegment(sketch, "E845", {"start": v(60.45, -33.46) * mm, "end": v(60.39, -33.38) * mm});
            skLineSegment(sketch, "E846", {"start": v(60.39, -33.38) * mm, "end": v(60.34, -33.3) * mm});
            skLineSegment(sketch, "E847", {"start": v(60.34, -33.3) * mm, "end": v(60.3, -33.16) * mm});
            skLineSegment(sketch, "E848", {"start": v(60.3, -33.16) * mm, "end": v(60.3, -33.03) * mm});
            skLineSegment(sketch, "E849", {"start": v(60.3, -33.03) * mm, "end": v(60.33, -32.9) * mm});
            skLineSegment(sketch, "E850", {"start": v(60.33, -32.9) * mm, "end": v(60.38, -32.78) * mm});
            skLineSegment(sketch, "E851", {"start": v(60.38, -32.78) * mm, "end": v(60.45, -32.67) * mm});
            skLineSegment(sketch, "E852", {"start": v(60.45, -32.67) * mm, "end": v(60.55, -32.58) * mm});
            skLineSegment(sketch, "E853", {"start": v(60.55, -32.58) * mm, "end": v(60.66, -32.51) * mm});
            skLineSegment(sketch, "E854", {"start": v(60.66, -32.51) * mm, "end": v(60.78, -32.47) * mm});
            skLineSegment(sketch, "E855", {"start": v(60.78, -32.47) * mm, "end": v(60.88, -32.46) * mm});
            skLineSegment(sketch, "E856", {"start": v(60.88, -32.46) * mm, "end": v(60.99, -32.47) * mm});
            skLineSegment(sketch, "E857", {"start": v(60.99, -32.47) * mm, "end": v(61.08, -32.49) * mm});
            skLineSegment(sketch, "E858", {"start": v(61.08, -32.49) * mm, "end": v(61.18, -32.51) * mm});
            skLineSegment(sketch, "E859", {"start": v(61.18, -32.51) * mm, "end": v(61.28, -32.51) * mm});
            skLineSegment(sketch, "E860", {"start": v(61.28, -32.51) * mm, "end": v(61.36, -32.44) * mm});
            skLineSegment(sketch, "E861", {"start": v(61.36, -32.44) * mm, "end": v(61.49, -32.2) * mm});
            skLineSegment(sketch, "E862", {"start": v(61.49, -32.2) * mm, "end": v(61.5, -32.09) * mm});
            skLineSegment(sketch, "E863", {"start": v(61.5, -32.09) * mm, "end": v(61.45, -32) * mm});
            skLineSegment(sketch, "E864", {"start": v(61.45, -32) * mm, "end": v(61.37, -31.94) * mm});
            skLineSegment(sketch, "E865", {"start": v(61.37, -31.94) * mm, "end": v(61.3, -31.87) * mm});
            skLineSegment(sketch, "E866", {"start": v(61.3, -31.87) * mm, "end": v(61.24, -31.79) * mm});
            skLineSegment(sketch, "E867", {"start": v(61.24, -31.79) * mm, "end": v(61.19, -31.7) * mm});
            skLineSegment(sketch, "E868", {"start": v(61.19, -31.7) * mm, "end": v(61.15, -31.57) * mm});
            skLineSegment(sketch, "E869", {"start": v(61.15, -31.57) * mm, "end": v(61.15, -31.44) * mm});
            skLineSegment(sketch, "E870", {"start": v(61.15, -31.44) * mm, "end": v(61.17, -31.31) * mm});
            skLineSegment(sketch, "E871", {"start": v(61.17, -31.31) * mm, "end": v(61.22, -31.2) * mm});
            skLineSegment(sketch, "E872", {"start": v(61.22, -31.2) * mm, "end": v(61.29, -31.08) * mm});
            skLineSegment(sketch, "E873", {"start": v(61.29, -31.08) * mm, "end": v(61.38, -30.99) * mm});
            skLineSegment(sketch, "E874", {"start": v(61.38, -30.99) * mm, "end": v(61.49, -30.91) * mm});
            skLineSegment(sketch, "E875", {"start": v(61.49, -30.91) * mm, "end": v(61.6, -30.87) * mm});
            skLineSegment(sketch, "E876", {"start": v(61.6, -30.87) * mm, "end": v(61.71, -30.86) * mm});
            skLineSegment(sketch, "E877", {"start": v(61.71, -30.86) * mm, "end": v(61.81, -30.86) * mm});
            skLineSegment(sketch, "E878", {"start": v(61.81, -30.86) * mm, "end": v(61.91, -30.88) * mm});
            skLineSegment(sketch, "E879", {"start": v(61.91, -30.88) * mm, "end": v(62.01, -30.9) * mm});
            skLineSegment(sketch, "E880", {"start": v(62.01, -30.9) * mm, "end": v(62.11, -30.9) * mm});
            skLineSegment(sketch, "E881", {"start": v(62.11, -30.9) * mm, "end": v(62.19, -30.82) * mm});
            skLineSegment(sketch, "E882", {"start": v(62.19, -30.82) * mm, "end": v(62.3, -30.57) * mm});
            skLineSegment(sketch, "E883", {"start": v(62.3, -30.57) * mm, "end": v(62.32, -30.47) * mm});
            skLineSegment(sketch, "E884", {"start": v(62.32, -30.47) * mm, "end": v(62.27, -30.38) * mm});
            skLineSegment(sketch, "E885", {"start": v(62.27, -30.38) * mm, "end": v(62.19, -30.32) * mm});
            skLineSegment(sketch, "E886", {"start": v(62.19, -30.32) * mm, "end": v(62.11, -30.25) * mm});
            skLineSegment(sketch, "E887", {"start": v(62.11, -30.25) * mm, "end": v(62.05, -30.17) * mm});
            skLineSegment(sketch, "E888", {"start": v(62.05, -30.17) * mm, "end": v(62, -30.09) * mm});
            skLineSegment(sketch, "E889", {"start": v(62, -30.09) * mm, "end": v(61.96, -29.96) * mm});
            skLineSegment(sketch, "E890", {"start": v(61.96, -29.96) * mm, "end": v(61.95, -29.83) * mm});
            skLineSegment(sketch, "E891", {"start": v(61.95, -29.83) * mm, "end": v(61.97, -29.7) * mm});
            skLineSegment(sketch, "E892", {"start": v(61.97, -29.7) * mm, "end": v(62.01, -29.58) * mm});
            skLineSegment(sketch, "E893", {"start": v(62.01, -29.58) * mm, "end": v(62.08, -29.46) * mm});
            skLineSegment(sketch, "E894", {"start": v(62.08, -29.46) * mm, "end": v(62.17, -29.37) * mm});
            skLineSegment(sketch, "E895", {"start": v(62.17, -29.37) * mm, "end": v(62.28, -29.3) * mm});
            skLineSegment(sketch, "E896", {"start": v(62.28, -29.3) * mm, "end": v(62.4, -29.24) * mm});
            skLineSegment(sketch, "E897", {"start": v(62.4, -29.24) * mm, "end": v(62.5, -29.23) * mm});
            skLineSegment(sketch, "E898", {"start": v(62.5, -29.23) * mm, "end": v(62.6, -29.23) * mm});
            skLineSegment(sketch, "E899", {"start": v(62.6, -29.23) * mm, "end": v(62.7, -29.24) * mm});
            skLineSegment(sketch, "E900", {"start": v(62.7, -29.24) * mm, "end": v(62.8, -29.27) * mm});
            skLineSegment(sketch, "E901", {"start": v(62.8, -29.27) * mm, "end": v(62.9, -29.26) * mm});
            skLineSegment(sketch, "E902", {"start": v(62.9, -29.26) * mm, "end": v(62.97, -29.18) * mm});
            skLineSegment(sketch, "E903", {"start": v(62.97, -29.18) * mm, "end": v(63.09, -28.93) * mm});
            skLineSegment(sketch, "E904", {"start": v(63.09, -28.93) * mm, "end": v(63.1, -28.83) * mm});
            skLineSegment(sketch, "E905", {"start": v(63.1, -28.83) * mm, "end": v(63.04, -28.74) * mm});
            skLineSegment(sketch, "E906", {"start": v(63.04, -28.74) * mm, "end": v(62.96, -28.69) * mm});
            skLineSegment(sketch, "E907", {"start": v(62.96, -28.69) * mm, "end": v(62.88, -28.62) * mm});
            skLineSegment(sketch, "E908", {"start": v(62.88, -28.62) * mm, "end": v(62.82, -28.54) * mm});
            skLineSegment(sketch, "E909", {"start": v(62.82, -28.54) * mm, "end": v(62.76, -28.45) * mm});
            skLineSegment(sketch, "E910", {"start": v(62.76, -28.45) * mm, "end": v(62.72, -28.33) * mm});
            skLineSegment(sketch, "E911", {"start": v(62.72, -28.33) * mm, "end": v(62.7, -28.2) * mm});
            skLineSegment(sketch, "E912", {"start": v(62.7, -28.2) * mm, "end": v(62.72, -28.07) * mm});
            skLineSegment(sketch, "E913", {"start": v(62.72, -28.07) * mm, "end": v(62.76, -27.94) * mm});
            skLineSegment(sketch, "E914", {"start": v(62.76, -27.94) * mm, "end": v(62.83, -27.83) * mm});
            skLineSegment(sketch, "E915", {"start": v(62.83, -27.83) * mm, "end": v(62.92, -27.73) * mm});
            skLineSegment(sketch, "E916", {"start": v(62.92, -27.73) * mm, "end": v(63.02, -27.65) * mm});
            skLineSegment(sketch, "E917", {"start": v(63.02, -27.65) * mm, "end": v(63.14, -27.6) * mm});
            skLineSegment(sketch, "E918", {"start": v(63.14, -27.6) * mm, "end": v(63.24, -27.59) * mm});
            skLineSegment(sketch, "E919", {"start": v(63.24, -27.59) * mm, "end": v(63.34, -27.58) * mm});
            skLineSegment(sketch, "E920", {"start": v(63.34, -27.58) * mm, "end": v(63.45, -27.6) * mm});
            skLineSegment(sketch, "E921", {"start": v(63.45, -27.6) * mm, "end": v(63.54, -27.61) * mm});
            skLineSegment(sketch, "E922", {"start": v(63.54, -27.61) * mm, "end": v(63.64, -27.6) * mm});
            skLineSegment(sketch, "E923", {"start": v(63.64, -27.6) * mm, "end": v(63.71, -27.52) * mm});
            skLineSegment(sketch, "E924", {"start": v(63.71, -27.52) * mm, "end": v(63.82, -27.27) * mm});
            skLineSegment(sketch, "E925", {"start": v(63.82, -27.27) * mm, "end": v(63.83, -27.16) * mm});
            skLineSegment(sketch, "E926", {"start": v(63.83, -27.16) * mm, "end": v(63.77, -27.08) * mm});
            skLineSegment(sketch, "E927", {"start": v(63.77, -27.08) * mm, "end": v(63.69, -27.03) * mm});
            skLineSegment(sketch, "E928", {"start": v(63.69, -27.03) * mm, "end": v(63.61, -26.96) * mm});
            skLineSegment(sketch, "E929", {"start": v(63.61, -26.96) * mm, "end": v(63.54, -26.89) * mm});
            skLineSegment(sketch, "E930", {"start": v(63.54, -26.89) * mm, "end": v(63.48, -26.8) * mm});
            skLineSegment(sketch, "E931", {"start": v(63.48, -26.8) * mm, "end": v(63.44, -26.68) * mm});
            skLineSegment(sketch, "E932", {"start": v(63.44, -26.68) * mm, "end": v(63.42, -26.55) * mm});
            skLineSegment(sketch, "E933", {"start": v(63.42, -26.55) * mm, "end": v(63.44, -26.42) * mm});
            skLineSegment(sketch, "E934", {"start": v(63.44, -26.42) * mm, "end": v(63.47, -26.3) * mm});
            skLineSegment(sketch, "E935", {"start": v(63.47, -26.3) * mm, "end": v(63.54, -26.18) * mm});
            skLineSegment(sketch, "E936", {"start": v(63.54, -26.18) * mm, "end": v(63.62, -26.07) * mm});
            skLineSegment(sketch, "E937", {"start": v(63.62, -26.07) * mm, "end": v(63.72, -26) * mm});
            skLineSegment(sketch, "E938", {"start": v(63.72, -26) * mm, "end": v(63.84, -25.94) * mm});
            skLineSegment(sketch, "E939", {"start": v(63.84, -25.94) * mm, "end": v(63.94, -25.92) * mm});
            skLineSegment(sketch, "E940", {"start": v(63.94, -25.92) * mm, "end": v(64.05, -25.92) * mm});
            skLineSegment(sketch, "E941", {"start": v(64.05, -25.92) * mm, "end": v(64.15, -25.92) * mm});
            skLineSegment(sketch, "E942", {"start": v(64.15, -25.92) * mm, "end": v(64.24, -25.94) * mm});
            skLineSegment(sketch, "E943", {"start": v(64.24, -25.94) * mm, "end": v(64.34, -25.93) * mm});
            skLineSegment(sketch, "E944", {"start": v(64.34, -25.93) * mm, "end": v(64.41, -25.85) * mm});
            skLineSegment(sketch, "E945", {"start": v(64.41, -25.85) * mm, "end": v(64.51, -25.6) * mm});
            skLineSegment(sketch, "E946", {"start": v(64.51, -25.6) * mm, "end": v(64.52, -25.48) * mm});
            skLineSegment(sketch, "E947", {"start": v(64.52, -25.48) * mm, "end": v(64.46, -25.4) * mm});
            skLineSegment(sketch, "E948", {"start": v(64.46, -25.4) * mm, "end": v(64.37, -25.35) * mm});
            skLineSegment(sketch, "E949", {"start": v(64.37, -25.35) * mm, "end": v(64.3, -25.29) * mm});
            skLineSegment(sketch, "E950", {"start": v(64.3, -25.29) * mm, "end": v(64.23, -25.21) * mm});
            skLineSegment(sketch, "E951", {"start": v(64.23, -25.21) * mm, "end": v(64.16, -25.13) * mm});
            skLineSegment(sketch, "E952", {"start": v(64.16, -25.13) * mm, "end": v(64.12, -25) * mm});
            skLineSegment(sketch, "E953", {"start": v(64.12, -25) * mm, "end": v(64.1, -24.88) * mm});
            skLineSegment(sketch, "E954", {"start": v(64.1, -24.88) * mm, "end": v(64.1, -24.75) * mm});
            skLineSegment(sketch, "E955", {"start": v(64.1, -24.75) * mm, "end": v(64.14, -24.62) * mm});
            skLineSegment(sketch, "E956", {"start": v(64.14, -24.62) * mm, "end": v(64.2, -24.5) * mm});
            skLineSegment(sketch, "E957", {"start": v(64.2, -24.5) * mm, "end": v(64.28, -24.4) * mm});
            skLineSegment(sketch, "E958", {"start": v(64.28, -24.4) * mm, "end": v(64.38, -24.32) * mm});
            skLineSegment(sketch, "E959", {"start": v(64.38, -24.32) * mm, "end": v(64.5, -24.26) * mm});
            skLineSegment(sketch, "E960", {"start": v(64.5, -24.26) * mm, "end": v(64.6, -24.24) * mm});
            skLineSegment(sketch, "E961", {"start": v(64.6, -24.24) * mm, "end": v(64.7, -24.23) * mm});
            skLineSegment(sketch, "E962", {"start": v(64.7, -24.23) * mm, "end": v(64.8, -24.23) * mm});
            skLineSegment(sketch, "E963", {"start": v(64.8, -24.23) * mm, "end": v(64.9, -24.25) * mm});
            skLineSegment(sketch, "E964", {"start": v(64.9, -24.25) * mm, "end": v(65, -24.23) * mm});
            skLineSegment(sketch, "E965", {"start": v(65, -24.23) * mm, "end": v(65.07, -24.15) * mm});
            skLineSegment(sketch, "E966", {"start": v(65.07, -24.15) * mm, "end": v(65.16, -23.9) * mm});
            skLineSegment(sketch, "E967", {"start": v(65.16, -23.9) * mm, "end": v(65.16, -23.79) * mm});
            skLineSegment(sketch, "E968", {"start": v(65.16, -23.79) * mm, "end": v(65.1, -23.7) * mm});
            skLineSegment(sketch, "E969", {"start": v(65.1, -23.7) * mm, "end": v(65.02, -23.66) * mm});
            skLineSegment(sketch, "E970", {"start": v(65.02, -23.66) * mm, "end": v(64.94, -23.6) * mm});
            skLineSegment(sketch, "E971", {"start": v(64.94, -23.6) * mm, "end": v(64.86, -23.52) * mm});
            skLineSegment(sketch, "E972", {"start": v(64.86, -23.52) * mm, "end": v(64.8, -23.44) * mm});
            skLineSegment(sketch, "E973", {"start": v(64.8, -23.44) * mm, "end": v(64.75, -23.32) * mm});
            skLineSegment(sketch, "E974", {"start": v(64.75, -23.32) * mm, "end": v(64.73, -23.2) * mm});
            skLineSegment(sketch, "E975", {"start": v(64.73, -23.2) * mm, "end": v(64.73, -23.06) * mm});
            skLineSegment(sketch, "E976", {"start": v(64.73, -23.06) * mm, "end": v(64.76, -22.93) * mm});
            skLineSegment(sketch, "E977", {"start": v(64.76, -22.93) * mm, "end": v(64.82, -22.81) * mm});
            skLineSegment(sketch, "E978", {"start": v(64.82, -22.81) * mm, "end": v(64.9, -22.7) * mm});
            skLineSegment(sketch, "E979", {"start": v(64.9, -22.7) * mm, "end": v(65, -22.62) * mm});
            skLineSegment(sketch, "E980", {"start": v(65, -22.62) * mm, "end": v(65.11, -22.56) * mm});
            skLineSegment(sketch, "E981", {"start": v(65.11, -22.56) * mm, "end": v(65.21, -22.54) * mm});
            skLineSegment(sketch, "E982", {"start": v(65.21, -22.54) * mm, "end": v(65.31, -22.53) * mm});
            skLineSegment(sketch, "E983", {"start": v(65.31, -22.53) * mm, "end": v(65.41, -22.53) * mm});
            skLineSegment(sketch, "E984", {"start": v(65.41, -22.53) * mm, "end": v(65.51, -22.54) * mm});
            skLineSegment(sketch, "E985", {"start": v(65.51, -22.54) * mm, "end": v(65.61, -22.52) * mm});
            skLineSegment(sketch, "E986", {"start": v(65.61, -22.52) * mm, "end": v(65.68, -22.44) * mm});
            skLineSegment(sketch, "E987", {"start": v(65.68, -22.44) * mm, "end": v(65.77, -22.18) * mm});
            skLineSegment(sketch, "E988", {"start": v(65.77, -22.18) * mm, "end": v(65.76, -22.07) * mm});
            skLineSegment(sketch, "E989", {"start": v(65.76, -22.07) * mm, "end": v(65.7, -22) * mm});
            skLineSegment(sketch, "E990", {"start": v(65.7, -22) * mm, "end": v(65.61, -21.95) * mm});
            skLineSegment(sketch, "E991", {"start": v(65.61, -21.95) * mm, "end": v(65.53, -21.89) * mm});
            skLineSegment(sketch, "E992", {"start": v(65.53, -21.89) * mm, "end": v(65.46, -21.82) * mm});
            skLineSegment(sketch, "E993", {"start": v(65.46, -21.82) * mm, "end": v(65.4, -21.74) * mm});
            skLineSegment(sketch, "E994", {"start": v(65.4, -21.74) * mm, "end": v(65.34, -21.62) * mm});
            skLineSegment(sketch, "E995", {"start": v(65.34, -21.62) * mm, "end": v(65.31, -21.5) * mm});
            skLineSegment(sketch, "E996", {"start": v(65.31, -21.5) * mm, "end": v(65.31, -21.36) * mm});
            skLineSegment(sketch, "E997", {"start": v(65.31, -21.36) * mm, "end": v(65.34, -21.23) * mm});
            skLineSegment(sketch, "E998", {"start": v(65.34, -21.23) * mm, "end": v(65.4, -21.1) * mm});
            skLineSegment(sketch, "E999", {"start": v(65.4, -21.1) * mm, "end": v(65.47, -21) * mm});
            skLineSegment(sketch, "E1000", {"start": v(65.47, -21) * mm, "end": v(65.57, -20.91) * mm});
            skLineSegment(sketch, "E1001", {"start": v(65.57, -20.91) * mm, "end": v(65.68, -20.85) * mm});
            skLineSegment(sketch, "E1002", {"start": v(65.68, -20.85) * mm, "end": v(65.78, -20.82) * mm});
            skLineSegment(sketch, "E1003", {"start": v(65.78, -20.82) * mm, "end": v(65.88, -20.81) * mm});
            skLineSegment(sketch, "E1004", {"start": v(65.88, -20.81) * mm, "end": v(65.98, -20.81) * mm});
            skLineSegment(sketch, "E1005", {"start": v(65.98, -20.81) * mm, "end": v(66.08, -20.82) * mm});
            skLineSegment(sketch, "E1006", {"start": v(66.08, -20.82) * mm, "end": v(66.18, -20.8) * mm});
            skLineSegment(sketch, "E1007", {"start": v(66.18, -20.8) * mm, "end": v(66.24, -20.71) * mm});
            skLineSegment(sketch, "E1008", {"start": v(66.24, -20.71) * mm, "end": v(66.32, -20.45) * mm});
            skLineSegment(sketch, "E1009", {"start": v(66.32, -20.45) * mm, "end": v(66.32, -20.34) * mm});
            skLineSegment(sketch, "E1010", {"start": v(66.32, -20.34) * mm, "end": v(66.25, -20.27) * mm});
            skLineSegment(sketch, "E1011", {"start": v(66.25, -20.27) * mm, "end": v(66.16, -20.22) * mm});
            skLineSegment(sketch, "E1012", {"start": v(66.16, -20.22) * mm, "end": v(66.08, -20.16) * mm});
            skLineSegment(sketch, "E1013", {"start": v(66.08, -20.16) * mm, "end": v(66, -20.1) * mm});
            skLineSegment(sketch, "E1014", {"start": v(66, -20.1) * mm, "end": v(65.94, -20.02) * mm});
            skLineSegment(sketch, "E1015", {"start": v(65.94, -20.02) * mm, "end": v(65.88, -19.9) * mm});
            skLineSegment(sketch, "E1016", {"start": v(65.88, -19.9) * mm, "end": v(65.85, -19.77) * mm});
            skLineSegment(sketch, "E1017", {"start": v(65.85, -19.77) * mm, "end": v(65.85, -19.64) * mm});
            skLineSegment(sketch, "E1018", {"start": v(65.85, -19.64) * mm, "end": v(65.87, -19.51) * mm});
            skLineSegment(sketch, "E1019", {"start": v(65.87, -19.51) * mm, "end": v(65.92, -19.4) * mm});
            skLineSegment(sketch, "E1020", {"start": v(65.92, -19.4) * mm, "end": v(66, -19.28) * mm});
            skLineSegment(sketch, "E1021", {"start": v(66, -19.28) * mm, "end": v(66.1, -19.2) * mm});
            skLineSegment(sketch, "E1022", {"start": v(66.1, -19.2) * mm, "end": v(66.2, -19.12) * mm});
            skLineSegment(sketch, "E1023", {"start": v(66.2, -19.12) * mm, "end": v(66.3, -19.1) * mm});
            skLineSegment(sketch, "E1024", {"start": v(66.3, -19.1) * mm, "end": v(66.4, -19.08) * mm});
            skLineSegment(sketch, "E1025", {"start": v(66.4, -19.08) * mm, "end": v(66.5, -19.08) * mm});
            skLineSegment(sketch, "E1026", {"start": v(66.5, -19.08) * mm, "end": v(66.6, -19.08) * mm});
            skLineSegment(sketch, "E1027", {"start": v(66.6, -19.08) * mm, "end": v(66.7, -19.06) * mm});
            skLineSegment(sketch, "E1028", {"start": v(66.7, -19.06) * mm, "end": v(66.76, -18.97) * mm});
            skLineSegment(sketch, "E1029", {"start": v(66.76, -18.97) * mm, "end": v(66.84, -18.7) * mm});
            skLineSegment(sketch, "E1030", {"start": v(66.84, -18.7) * mm, "end": v(66.83, -18.6) * mm});
            skLineSegment(sketch, "E1031", {"start": v(66.83, -18.6) * mm, "end": v(66.76, -18.53) * mm});
            skLineSegment(sketch, "E1032", {"start": v(66.76, -18.53) * mm, "end": v(66.67, -18.48) * mm});
            skLineSegment(sketch, "E1033", {"start": v(66.67, -18.48) * mm, "end": v(66.59, -18.43) * mm});
            skLineSegment(sketch, "E1034", {"start": v(66.59, -18.43) * mm, "end": v(66.51, -18.36) * mm});
            skLineSegment(sketch, "E1035", {"start": v(66.51, -18.36) * mm, "end": v(66.44, -18.29) * mm});
            skLineSegment(sketch, "E1036", {"start": v(66.44, -18.29) * mm, "end": v(66.38, -18.17) * mm});
            skLineSegment(sketch, "E1037", {"start": v(66.38, -18.17) * mm, "end": v(66.35, -18.04) * mm});
            skLineSegment(sketch, "E1038", {"start": v(66.35, -18.04) * mm, "end": v(66.34, -17.91) * mm});
            skLineSegment(sketch, "E1039", {"start": v(66.34, -17.91) * mm, "end": v(66.36, -17.78) * mm});
            skLineSegment(sketch, "E1040", {"start": v(66.36, -17.78) * mm, "end": v(66.4, -17.66) * mm});
            skLineSegment(sketch, "E1041", {"start": v(66.4, -17.66) * mm, "end": v(66.48, -17.55) * mm});
            skLineSegment(sketch, "E1042", {"start": v(66.48, -17.55) * mm, "end": v(66.57, -17.45) * mm});
            skLineSegment(sketch, "E1043", {"start": v(66.57, -17.45) * mm, "end": v(66.68, -17.38) * mm});
            skLineSegment(sketch, "E1044", {"start": v(66.68, -17.38) * mm, "end": v(66.78, -17.35) * mm});
            skLineSegment(sketch, "E1045", {"start": v(66.78, -17.35) * mm, "end": v(66.88, -17.33) * mm});
            skLineSegment(sketch, "E1046", {"start": v(66.88, -17.33) * mm, "end": v(66.98, -17.33) * mm});
            skLineSegment(sketch, "E1047", {"start": v(66.98, -17.33) * mm, "end": v(67.08, -17.33) * mm});
            skLineSegment(sketch, "E1048", {"start": v(67.08, -17.33) * mm, "end": v(67.18, -17.3) * mm});
            skLineSegment(sketch, "E1049", {"start": v(67.18, -17.3) * mm, "end": v(67.24, -17.22) * mm});
            skLineSegment(sketch, "E1050", {"start": v(67.24, -17.22) * mm, "end": v(67.3, -16.95) * mm});
            skLineSegment(sketch, "E1051", {"start": v(67.3, -16.95) * mm, "end": v(67.3, -16.84) * mm});
            skLineSegment(sketch, "E1052", {"start": v(67.3, -16.84) * mm, "end": v(67.22, -16.77) * mm});
            skLineSegment(sketch, "E1053", {"start": v(67.22, -16.77) * mm, "end": v(67.13, -16.73) * mm});
            skLineSegment(sketch, "E1054", {"start": v(67.13, -16.73) * mm, "end": v(67.05, -16.68) * mm});
            skLineSegment(sketch, "E1055", {"start": v(67.05, -16.68) * mm, "end": v(66.97, -16.61) * mm});
            skLineSegment(sketch, "E1056", {"start": v(66.97, -16.61) * mm, "end": v(66.9, -16.54) * mm});
            skLineSegment(sketch, "E1057", {"start": v(66.9, -16.54) * mm, "end": v(66.83, -16.43) * mm});
            skLineSegment(sketch, "E1058", {"start": v(66.83, -16.43) * mm, "end": v(66.8, -16.3) * mm});
            skLineSegment(sketch, "E1059", {"start": v(66.8, -16.3) * mm, "end": v(66.79, -16.17) * mm});
            skLineSegment(sketch, "E1060", {"start": v(66.79, -16.17) * mm, "end": v(66.8, -16.04) * mm});
            skLineSegment(sketch, "E1061", {"start": v(66.8, -16.04) * mm, "end": v(66.85, -15.91) * mm});
            skLineSegment(sketch, "E1062", {"start": v(66.85, -15.91) * mm, "end": v(66.92, -15.8) * mm});
            skLineSegment(sketch, "E1063", {"start": v(66.92, -15.8) * mm, "end": v(67, -15.7) * mm});
            skLineSegment(sketch, "E1064", {"start": v(67, -15.7) * mm, "end": v(67.11, -15.63) * mm});
            skLineSegment(sketch, "E1065", {"start": v(67.11, -15.63) * mm, "end": v(67.21, -15.6) * mm});
            skLineSegment(sketch, "E1066", {"start": v(67.21, -15.6) * mm, "end": v(67.31, -15.58) * mm});
            skLineSegment(sketch, "E1067", {"start": v(67.31, -15.58) * mm, "end": v(67.41, -15.57) * mm});
            skLineSegment(sketch, "E1068", {"start": v(67.41, -15.57) * mm, "end": v(67.51, -15.57) * mm});
            skLineSegment(sketch, "E1069", {"start": v(67.51, -15.57) * mm, "end": v(67.6, -15.54) * mm});
            skLineSegment(sketch, "E1070", {"start": v(67.6, -15.54) * mm, "end": v(67.66, -15.45) * mm});
            skLineSegment(sketch, "E1071", {"start": v(67.66, -15.45) * mm, "end": v(67.72, -15.18) * mm});
            skLineSegment(sketch, "E1072", {"start": v(67.72, -15.18) * mm, "end": v(67.71, -15.08) * mm});
            skLineSegment(sketch, "E1073", {"start": v(67.71, -15.08) * mm, "end": v(67.64, -15) * mm});
            skLineSegment(sketch, "E1074", {"start": v(67.64, -15) * mm, "end": v(67.55, -14.97) * mm});
            skLineSegment(sketch, "E1075", {"start": v(67.55, -14.97) * mm, "end": v(67.46, -14.92) * mm});
            skLineSegment(sketch, "E1076", {"start": v(67.46, -14.92) * mm, "end": v(67.38, -14.86) * mm});
            skLineSegment(sketch, "E1077", {"start": v(67.38, -14.86) * mm, "end": v(67.3, -14.78) * mm});
            skLineSegment(sketch, "E1078", {"start": v(67.3, -14.78) * mm, "end": v(67.24, -14.67) * mm});
            skLineSegment(sketch, "E1079", {"start": v(67.24, -14.67) * mm, "end": v(67.2, -14.55) * mm});
            skLineSegment(sketch, "E1080", {"start": v(67.2, -14.55) * mm, "end": v(67.19, -14.42) * mm});
            skLineSegment(sketch, "E1081", {"start": v(67.19, -14.42) * mm, "end": v(67.2, -14.28) * mm});
            skLineSegment(sketch, "E1082", {"start": v(67.2, -14.28) * mm, "end": v(67.24, -14.16) * mm});
            skLineSegment(sketch, "E1083", {"start": v(67.24, -14.16) * mm, "end": v(67.3, -14.04) * mm});
            skLineSegment(sketch, "E1084", {"start": v(67.3, -14.04) * mm, "end": v(67.4, -13.95) * mm});
            skLineSegment(sketch, "E1085", {"start": v(67.4, -13.95) * mm, "end": v(67.5, -13.87) * mm});
            skLineSegment(sketch, "E1086", {"start": v(67.5, -13.87) * mm, "end": v(67.6, -13.83) * mm});
            skLineSegment(sketch, "E1087", {"start": v(67.6, -13.83) * mm, "end": v(67.7, -13.81) * mm});
            skLineSegment(sketch, "E1088", {"start": v(67.7, -13.81) * mm, "end": v(67.8, -13.8) * mm});
            skLineSegment(sketch, "E1089", {"start": v(67.8, -13.8) * mm, "end": v(67.9, -13.8) * mm});
            skLineSegment(sketch, "E1090", {"start": v(67.9, -13.8) * mm, "end": v(68, -13.77) * mm});
            skLineSegment(sketch, "E1091", {"start": v(68, -13.77) * mm, "end": v(68.04, -13.67) * mm});
            skLineSegment(sketch, "E1092", {"start": v(68.04, -13.67) * mm, "end": v(68.1, -13.4) * mm});
            skLineSegment(sketch, "E1093", {"start": v(68.1, -13.4) * mm, "end": v(68.08, -13.3) * mm});
            skLineSegment(sketch, "E1094", {"start": v(68.08, -13.3) * mm, "end": v(68, -13.23) * mm});
            skLineSegment(sketch, "E1095", {"start": v(68, -13.23) * mm, "end": v(67.92, -13.2) * mm});
            skLineSegment(sketch, "E1096", {"start": v(67.92, -13.2) * mm, "end": v(67.83, -13.15) * mm});
            skLineSegment(sketch, "E1097", {"start": v(67.83, -13.15) * mm, "end": v(67.75, -13.09) * mm});
            skLineSegment(sketch, "E1098", {"start": v(67.75, -13.09) * mm, "end": v(67.67, -13.02) * mm});
            skLineSegment(sketch, "E1099", {"start": v(67.67, -13.02) * mm, "end": v(67.6, -12.9) * mm});
            skLineSegment(sketch, "E1100", {"start": v(67.6, -12.9) * mm, "end": v(67.56, -12.78) * mm});
            skLineSegment(sketch, "E1101", {"start": v(67.56, -12.78) * mm, "end": v(67.54, -12.65) * mm});
            skLineSegment(sketch, "E1102", {"start": v(67.54, -12.65) * mm, "end": v(67.55, -12.52) * mm});
            skLineSegment(sketch, "E1103", {"start": v(67.55, -12.52) * mm, "end": v(67.6, -12.4) * mm});
            skLineSegment(sketch, "E1104", {"start": v(67.6, -12.4) * mm, "end": v(67.65, -12.28) * mm});
            skLineSegment(sketch, "E1105", {"start": v(67.65, -12.28) * mm, "end": v(67.74, -12.18) * mm});
            skLineSegment(sketch, "E1106", {"start": v(67.74, -12.18) * mm, "end": v(67.84, -12.1) * mm});
            skLineSegment(sketch, "E1107", {"start": v(67.84, -12.1) * mm, "end": v(67.94, -12.06) * mm});
            skLineSegment(sketch, "E1108", {"start": v(67.94, -12.06) * mm, "end": v(68.03, -12.03) * mm});
            skLineSegment(sketch, "E1109", {"start": v(68.03, -12.03) * mm, "end": v(68.13, -12.02) * mm});
            skLineSegment(sketch, "E1110", {"start": v(68.13, -12.02) * mm, "end": v(68.23, -12.02) * mm});
            skLineSegment(sketch, "E1111", {"start": v(68.23, -12.02) * mm, "end": v(68.33, -11.98) * mm});
            skLineSegment(sketch, "E1112", {"start": v(68.33, -11.98) * mm, "end": v(68.38, -11.89) * mm});
            skLineSegment(sketch, "E1113", {"start": v(68.38, -11.89) * mm, "end": v(68.43, -11.62) * mm});
            skLineSegment(sketch, "E1114", {"start": v(68.43, -11.62) * mm, "end": v(68.4, -11.51) * mm});
            skLineSegment(sketch, "E1115", {"start": v(68.4, -11.51) * mm, "end": v(68.33, -11.45) * mm});
            skLineSegment(sketch, "E1116", {"start": v(68.33, -11.45) * mm, "end": v(68.24, -11.41) * mm});
            skLineSegment(sketch, "E1117", {"start": v(68.24, -11.41) * mm, "end": v(68.15, -11.37) * mm});
            skLineSegment(sketch, "E1118", {"start": v(68.15, -11.37) * mm, "end": v(68.07, -11.3) * mm});
            skLineSegment(sketch, "E1119", {"start": v(68.07, -11.3) * mm, "end": v(67.99, -11.24) * mm});
            skLineSegment(sketch, "E1120", {"start": v(67.99, -11.24) * mm, "end": v(67.91, -11.13) * mm});
            skLineSegment(sketch, "E1121", {"start": v(67.91, -11.13) * mm, "end": v(67.87, -11) * mm});
            skLineSegment(sketch, "E1122", {"start": v(67.87, -11) * mm, "end": v(67.85, -10.88) * mm});
            skLineSegment(sketch, "E1123", {"start": v(67.85, -10.88) * mm, "end": v(67.86, -10.75) * mm});
            skLineSegment(sketch, "E1124", {"start": v(67.86, -10.75) * mm, "end": v(67.9, -10.62) * mm});
            skLineSegment(sketch, "E1125", {"start": v(67.9, -10.62) * mm, "end": v(67.95, -10.5) * mm});
            skLineSegment(sketch, "E1126", {"start": v(67.95, -10.5) * mm, "end": v(68.03, -10.4) * mm});
            skLineSegment(sketch, "E1127", {"start": v(68.03, -10.4) * mm, "end": v(68.13, -10.32) * mm});
            skLineSegment(sketch, "E1128", {"start": v(68.13, -10.32) * mm, "end": v(68.23, -10.28) * mm});
            skLineSegment(sketch, "E1129", {"start": v(68.23, -10.28) * mm, "end": v(68.33, -10.25) * mm});
            skLineSegment(sketch, "E1130", {"start": v(68.33, -10.25) * mm, "end": v(68.42, -10.23) * mm});
            skLineSegment(sketch, "E1131", {"start": v(68.42, -10.23) * mm, "end": v(68.53, -10.23) * mm});
            skLineSegment(sketch, "E1132", {"start": v(68.53, -10.23) * mm, "end": v(68.62, -10.19) * mm});
            skLineSegment(sketch, "E1133", {"start": v(68.62, -10.19) * mm, "end": v(68.67, -10.1) * mm});
            skLineSegment(sketch, "E1134", {"start": v(68.67, -10.1) * mm, "end": v(68.7, -9.82) * mm});
            skLineSegment(sketch, "E1135", {"start": v(68.7, -9.82) * mm, "end": v(68.69, -9.72) * mm});
            skLineSegment(sketch, "E1136", {"start": v(68.69, -9.72) * mm, "end": v(68.6, -9.66) * mm});
            skLineSegment(sketch, "E1137", {"start": v(68.6, -9.66) * mm, "end": v(68.51, -9.62) * mm});
            skLineSegment(sketch, "E1138", {"start": v(68.51, -9.62) * mm, "end": v(68.42, -9.58) * mm});
            skLineSegment(sketch, "E1139", {"start": v(68.42, -9.58) * mm, "end": v(68.34, -9.52) * mm});
            skLineSegment(sketch, "E1140", {"start": v(68.34, -9.52) * mm, "end": v(68.26, -9.46) * mm});
            skLineSegment(sketch, "E1141", {"start": v(68.26, -9.46) * mm, "end": v(68.18, -9.35) * mm});
            skLineSegment(sketch, "E1142", {"start": v(68.18, -9.35) * mm, "end": v(68.13, -9.23) * mm});
            skLineSegment(sketch, "E1143", {"start": v(68.13, -9.23) * mm, "end": v(68.11, -9.1) * mm});
            skLineSegment(sketch, "E1144", {"start": v(68.11, -9.1) * mm, "end": v(68.12, -8.97) * mm});
            skLineSegment(sketch, "E1145", {"start": v(68.12, -8.97) * mm, "end": v(68.15, -8.84) * mm});
            skLineSegment(sketch, "E1146", {"start": v(68.15, -8.84) * mm, "end": v(68.2, -8.72) * mm});
            skLineSegment(sketch, "E1147", {"start": v(68.2, -8.72) * mm, "end": v(68.28, -8.62) * mm});
            skLineSegment(sketch, "E1148", {"start": v(68.28, -8.62) * mm, "end": v(68.38, -8.53) * mm});
            skLineSegment(sketch, "E1149", {"start": v(68.38, -8.53) * mm, "end": v(68.47, -8.49) * mm});
            skLineSegment(sketch, "E1150", {"start": v(68.47, -8.49) * mm, "end": v(68.57, -8.46) * mm});
            skLineSegment(sketch, "E1151", {"start": v(68.57, -8.46) * mm, "end": v(68.67, -8.44) * mm});
            skLineSegment(sketch, "E1152", {"start": v(68.67, -8.44) * mm, "end": v(68.77, -8.43) * mm});
            skLineSegment(sketch, "E1153", {"start": v(68.77, -8.43) * mm, "end": v(68.86, -8.4) * mm});
            skLineSegment(sketch, "E1154", {"start": v(68.86, -8.4) * mm, "end": v(68.9, -8.3) * mm});
            skLineSegment(sketch, "E1155", {"start": v(68.9, -8.3) * mm, "end": v(68.94, -8.02) * mm});
            skLineSegment(sketch, "E1156", {"start": v(68.94, -8.02) * mm, "end": v(68.92, -7.92) * mm});
            skLineSegment(sketch, "E1157", {"start": v(68.92, -7.92) * mm, "end": v(68.84, -7.86) * mm});
            skLineSegment(sketch, "E1158", {"start": v(68.84, -7.86) * mm, "end": v(68.74, -7.83) * mm});
            skLineSegment(sketch, "E1159", {"start": v(68.74, -7.83) * mm, "end": v(68.65, -7.78) * mm});
            skLineSegment(sketch, "E1160", {"start": v(68.65, -7.78) * mm, "end": v(68.56, -7.73) * mm});
            skLineSegment(sketch, "E1161", {"start": v(68.56, -7.73) * mm, "end": v(68.48, -7.67) * mm});
            skLineSegment(sketch, "E1162", {"start": v(68.48, -7.67) * mm, "end": v(68.4, -7.56) * mm});
            skLineSegment(sketch, "E1163", {"start": v(68.4, -7.56) * mm, "end": v(68.35, -7.44) * mm});
            skLineSegment(sketch, "E1164", {"start": v(68.35, -7.44) * mm, "end": v(68.33, -7.31) * mm});
            skLineSegment(sketch, "E1165", {"start": v(68.33, -7.31) * mm, "end": v(68.33, -7.18) * mm});
            skLineSegment(sketch, "E1166", {"start": v(68.33, -7.18) * mm, "end": v(68.35, -7.05) * mm});
            skLineSegment(sketch, "E1167", {"start": v(68.35, -7.05) * mm, "end": v(68.4, -6.93) * mm});
            skLineSegment(sketch, "E1168", {"start": v(68.4, -6.93) * mm, "end": v(68.48, -6.83) * mm});
            skLineSegment(sketch, "E1169", {"start": v(68.48, -6.83) * mm, "end": v(68.58, -6.74) * mm});
            skLineSegment(sketch, "E1170", {"start": v(68.58, -6.74) * mm, "end": v(68.67, -6.7) * mm});
            skLineSegment(sketch, "E1171", {"start": v(68.67, -6.7) * mm, "end": v(68.77, -6.66) * mm});
            skLineSegment(sketch, "E1172", {"start": v(68.77, -6.66) * mm, "end": v(68.87, -6.64) * mm});
            skLineSegment(sketch, "E1173", {"start": v(68.87, -6.64) * mm, "end": v(68.97, -6.63) * mm});
            skLineSegment(sketch, "E1174", {"start": v(68.97, -6.63) * mm, "end": v(69.06, -6.58) * mm});
            skLineSegment(sketch, "E1175", {"start": v(69.06, -6.58) * mm, "end": v(69.1, -6.49) * mm});
            skLineSegment(sketch, "E1176", {"start": v(69.1, -6.49) * mm, "end": v(69.13, -6.21) * mm});
            skLineSegment(sketch, "E1177", {"start": v(69.13, -6.21) * mm, "end": v(69.1, -6.11) * mm});
            skLineSegment(sketch, "E1178", {"start": v(69.1, -6.11) * mm, "end": v(69.02, -6.05) * mm});
            skLineSegment(sketch, "E1179", {"start": v(69.02, -6.05) * mm, "end": v(68.92, -6.02) * mm});
            skLineSegment(sketch, "E1180", {"start": v(68.92, -6.02) * mm, "end": v(68.83, -5.98) * mm});
            skLineSegment(sketch, "E1181", {"start": v(68.83, -5.98) * mm, "end": v(68.74, -5.93) * mm});
            skLineSegment(sketch, "E1182", {"start": v(68.74, -5.93) * mm, "end": v(68.66, -5.87) * mm});
            skLineSegment(sketch, "E1183", {"start": v(68.66, -5.87) * mm, "end": v(68.58, -5.77) * mm});
            skLineSegment(sketch, "E1184", {"start": v(68.58, -5.77) * mm, "end": v(68.52, -5.65) * mm});
            skLineSegment(sketch, "E1185", {"start": v(68.52, -5.65) * mm, "end": v(68.5, -5.52) * mm});
            skLineSegment(sketch, "E1186", {"start": v(68.5, -5.52) * mm, "end": v(68.5, -5.4) * mm});
            skLineSegment(sketch, "E1187", {"start": v(68.5, -5.4) * mm, "end": v(68.52, -5.26) * mm});
            skLineSegment(sketch, "E1188", {"start": v(68.52, -5.26) * mm, "end": v(68.56, -5.14) * mm});
            skLineSegment(sketch, "E1189", {"start": v(68.56, -5.14) * mm, "end": v(68.64, -5.03) * mm});
            skLineSegment(sketch, "E1190", {"start": v(68.64, -5.03) * mm, "end": v(68.73, -4.94) * mm});
            skLineSegment(sketch, "E1191", {"start": v(68.73, -4.94) * mm, "end": v(68.82, -4.9) * mm});
            skLineSegment(sketch, "E1192", {"start": v(68.82, -4.9) * mm, "end": v(68.92, -4.86) * mm});
            skLineSegment(sketch, "E1193", {"start": v(68.92, -4.86) * mm, "end": v(69.02, -4.83) * mm});
            skLineSegment(sketch, "E1194", {"start": v(69.02, -4.83) * mm, "end": v(69.12, -4.82) * mm});
            skLineSegment(sketch, "E1195", {"start": v(69.12, -4.82) * mm, "end": v(69.2, -4.77) * mm});
            skLineSegment(sketch, "E1196", {"start": v(69.2, -4.77) * mm, "end": v(69.25, -4.68) * mm});
            skLineSegment(sketch, "E1197", {"start": v(69.25, -4.68) * mm, "end": v(69.26, -4.4) * mm});
            skLineSegment(sketch, "E1198", {"start": v(69.26, -4.4) * mm, "end": v(69.24, -4.3) * mm});
            skLineSegment(sketch, "E1199", {"start": v(69.24, -4.3) * mm, "end": v(69.15, -4.24) * mm});
            skLineSegment(sketch, "E1200", {"start": v(69.15, -4.24) * mm, "end": v(69.06, -4.22) * mm});
            skLineSegment(sketch, "E1201", {"start": v(69.06, -4.22) * mm, "end": v(68.96, -4.18) * mm});
            skLineSegment(sketch, "E1202", {"start": v(68.96, -4.18) * mm, "end": v(68.87, -4.13) * mm});
            skLineSegment(sketch, "E1203", {"start": v(68.87, -4.13) * mm, "end": v(68.79, -4.07) * mm});
            skLineSegment(sketch, "E1204", {"start": v(68.79, -4.07) * mm, "end": v(68.7, -3.97) * mm});
            skLineSegment(sketch, "E1205", {"start": v(68.7, -3.97) * mm, "end": v(68.65, -3.85) * mm});
            skLineSegment(sketch, "E1206", {"start": v(68.65, -3.85) * mm, "end": v(68.62, -3.73) * mm});
            skLineSegment(sketch, "E1207", {"start": v(68.62, -3.73) * mm, "end": v(68.6, -3.6) * mm});
            skLineSegment(sketch, "E1208", {"start": v(68.6, -3.6) * mm, "end": v(68.63, -3.47) * mm});
            skLineSegment(sketch, "E1209", {"start": v(68.63, -3.47) * mm, "end": v(68.68, -3.34) * mm});
            skLineSegment(sketch, "E1210", {"start": v(68.68, -3.34) * mm, "end": v(68.75, -3.23) * mm});
            skLineSegment(sketch, "E1211", {"start": v(68.75, -3.23) * mm, "end": v(68.84, -3.14) * mm});
            skLineSegment(sketch, "E1212", {"start": v(68.84, -3.14) * mm, "end": v(68.93, -3.1) * mm});
            skLineSegment(sketch, "E1213", {"start": v(68.93, -3.1) * mm, "end": v(69.02, -3.05) * mm});
            skLineSegment(sketch, "E1214", {"start": v(69.02, -3.05) * mm, "end": v(69.12, -3.02) * mm});
            skLineSegment(sketch, "E1215", {"start": v(69.12, -3.02) * mm, "end": v(69.22, -3) * mm});
            skLineSegment(sketch, "E1216", {"start": v(69.22, -3) * mm, "end": v(69.3, -2.96) * mm});
            skLineSegment(sketch, "E1217", {"start": v(69.3, -2.96) * mm, "end": v(69.35, -2.86) * mm});
            skLineSegment(sketch, "E1218", {"start": v(69.35, -2.86) * mm, "end": v(69.36, -2.59) * mm});
            skLineSegment(sketch, "E1219", {"start": v(69.36, -2.59) * mm, "end": v(69.33, -2.49) * mm});
            skLineSegment(sketch, "E1220", {"start": v(69.33, -2.49) * mm, "end": v(69.24, -2.43) * mm});
            skLineSegment(sketch, "E1221", {"start": v(69.24, -2.43) * mm, "end": v(69.14, -2.4) * mm});
            skLineSegment(sketch, "E1222", {"start": v(69.14, -2.4) * mm, "end": v(69.05, -2.37) * mm});
            skLineSegment(sketch, "E1223", {"start": v(69.05, -2.37) * mm, "end": v(68.96, -2.33) * mm});
            skLineSegment(sketch, "E1224", {"start": v(68.96, -2.33) * mm, "end": v(68.87, -2.27) * mm});
            skLineSegment(sketch, "E1225", {"start": v(68.87, -2.27) * mm, "end": v(68.79, -2.17) * mm});
            skLineSegment(sketch, "E1226", {"start": v(68.79, -2.17) * mm, "end": v(68.73, -2.06) * mm});
            skLineSegment(sketch, "E1227", {"start": v(68.73, -2.06) * mm, "end": v(68.69, -1.93) * mm});
            skLineSegment(sketch, "E1228", {"start": v(68.69, -1.93) * mm, "end": v(68.68, -1.8) * mm});
            skLineSegment(sketch, "E1229", {"start": v(68.68, -1.8) * mm, "end": v(68.7, -1.67) * mm});
            skLineSegment(sketch, "E1230", {"start": v(68.7, -1.67) * mm, "end": v(68.74, -1.54) * mm});
            skLineSegment(sketch, "E1231", {"start": v(68.74, -1.54) * mm, "end": v(68.8, -1.43) * mm});
            skLineSegment(sketch, "E1232", {"start": v(68.8, -1.43) * mm, "end": v(68.9, -1.34) * mm});
            skLineSegment(sketch, "E1233", {"start": v(68.9, -1.34) * mm, "end": v(68.99, -1.28) * mm});
            skLineSegment(sketch, "E1234", {"start": v(68.99, -1.28) * mm, "end": v(69.08, -1.24) * mm});
            skLineSegment(sketch, "E1235", {"start": v(69.08, -1.24) * mm, "end": v(69.18, -1.21) * mm});
            skLineSegment(sketch, "E1236", {"start": v(69.18, -1.21) * mm, "end": v(69.27, -1.2) * mm});
            skLineSegment(sketch, "E1237", {"start": v(69.27, -1.2) * mm, "end": v(69.36, -1.15) * mm});
            skLineSegment(sketch, "E1238", {"start": v(69.36, -1.15) * mm, "end": v(69.4, -1.05) * mm});
            skLineSegment(sketch, "E1239", {"start": v(69.4, -1.05) * mm, "end": v(69.4, -0.77) * mm});
            skLineSegment(sketch, "E1240", {"start": v(69.4, -0.77) * mm, "end": v(69.37, -0.67) * mm});
            skLineSegment(sketch, "E1241", {"start": v(69.37, -0.67) * mm, "end": v(69.28, -0.62) * mm});
            skLineSegment(sketch, "E1242", {"start": v(69.28, -0.62) * mm, "end": v(69.18, -0.6) * mm});
            skLineSegment(sketch, "E1243", {"start": v(69.18, -0.6) * mm, "end": v(69.09, -0.57) * mm});
            skLineSegment(sketch, "E1244", {"start": v(69.09, -0.57) * mm, "end": v(69, -0.52) * mm});
            skLineSegment(sketch, "E1245", {"start": v(69, -0.52) * mm, "end": v(68.9, -0.47) * mm});
            skLineSegment(sketch, "E1246", {"start": v(68.9, -0.47) * mm, "end": v(68.82, -0.37) * mm});
            skLineSegment(sketch, "E1247", {"start": v(68.82, -0.37) * mm, "end": v(68.76, -0.26) * mm});
            skLineSegment(sketch, "E1248", {"start": v(68.76, -0.26) * mm, "end": v(68.72, -0.13) * mm});
            skLineSegment(sketch, "E1249", {"start": v(68.72, -0.13) * mm, "end": v(68.7, 0) * mm});
            skLineSegment(sketch, "E1250", {"start": v(68.7, 0) * mm, "end": v(68.72, 0.13) * mm});
            skLineSegment(sketch, "E1251", {"start": v(68.72, 0.13) * mm, "end": v(68.76, 0.26) * mm});
            skLineSegment(sketch, "E1252", {"start": v(68.76, 0.26) * mm, "end": v(68.82, 0.37) * mm});
            skLineSegment(sketch, "E1253", {"start": v(68.82, 0.37) * mm, "end": v(68.9, 0.47) * mm});
            skLineSegment(sketch, "E1254", {"start": v(68.9, 0.47) * mm, "end": v(69, 0.52) * mm});
            skLineSegment(sketch, "E1255", {"start": v(69, 0.52) * mm, "end": v(69.09, 0.57) * mm});
            skLineSegment(sketch, "E1256", {"start": v(69.09, 0.57) * mm, "end": v(69.18, 0.6) * mm});
            skLineSegment(sketch, "E1257", {"start": v(69.18, 0.6) * mm, "end": v(69.28, 0.62) * mm});
            skLineSegment(sketch, "E1258", {"start": v(69.28, 0.62) * mm, "end": v(69.37, 0.67) * mm});
            skLineSegment(sketch, "E1259", {"start": v(69.37, 0.67) * mm, "end": v(69.4, 0.77) * mm});
            skLineSegment(sketch, "E1260", {"start": v(69.4, 0.77) * mm, "end": v(69.4, 1.05) * mm});
            skLineSegment(sketch, "E1261", {"start": v(69.4, 1.05) * mm, "end": v(69.36, 1.15) * mm});
            skLineSegment(sketch, "E1262", {"start": v(69.36, 1.15) * mm, "end": v(69.27, 1.2) * mm});
            skLineSegment(sketch, "E1263", {"start": v(69.27, 1.2) * mm, "end": v(69.18, 1.21) * mm});
            skLineSegment(sketch, "E1264", {"start": v(69.18, 1.21) * mm, "end": v(69.08, 1.24) * mm});
            skLineSegment(sketch, "E1265", {"start": v(69.08, 1.24) * mm, "end": v(68.99, 1.28) * mm});
            skLineSegment(sketch, "E1266", {"start": v(68.99, 1.28) * mm, "end": v(68.9, 1.34) * mm});
            skLineSegment(sketch, "E1267", {"start": v(68.9, 1.34) * mm, "end": v(68.8, 1.43) * mm});
            skLineSegment(sketch, "E1268", {"start": v(68.8, 1.43) * mm, "end": v(68.74, 1.54) * mm});
            skLineSegment(sketch, "E1269", {"start": v(68.74, 1.54) * mm, "end": v(68.7, 1.67) * mm});
            skLineSegment(sketch, "E1270", {"start": v(68.7, 1.67) * mm, "end": v(68.68, 1.8) * mm});
            skLineSegment(sketch, "E1271", {"start": v(68.68, 1.8) * mm, "end": v(68.69, 1.93) * mm});
            skLineSegment(sketch, "E1272", {"start": v(68.69, 1.93) * mm, "end": v(68.73, 2.06) * mm});
            skLineSegment(sketch, "E1273", {"start": v(68.73, 2.06) * mm, "end": v(68.79, 2.17) * mm});
            skLineSegment(sketch, "E1274", {"start": v(68.79, 2.17) * mm, "end": v(68.87, 2.27) * mm});
            skLineSegment(sketch, "E1275", {"start": v(68.87, 2.27) * mm, "end": v(68.96, 2.33) * mm});
            skLineSegment(sketch, "E1276", {"start": v(68.96, 2.33) * mm, "end": v(69.05, 2.37) * mm});
            skLineSegment(sketch, "E1277", {"start": v(69.05, 2.37) * mm, "end": v(69.14, 2.4) * mm});
            skLineSegment(sketch, "E1278", {"start": v(69.14, 2.4) * mm, "end": v(69.24, 2.43) * mm});
            skLineSegment(sketch, "E1279", {"start": v(69.24, 2.43) * mm, "end": v(69.33, 2.49) * mm});
            skLineSegment(sketch, "E1280", {"start": v(69.33, 2.49) * mm, "end": v(69.36, 2.59) * mm});
            skLineSegment(sketch, "E1281", {"start": v(69.36, 2.59) * mm, "end": v(69.35, 2.86) * mm});
            skLineSegment(sketch, "E1282", {"start": v(69.35, 2.86) * mm, "end": v(69.3, 2.96) * mm});
            skLineSegment(sketch, "E1283", {"start": v(69.3, 2.96) * mm, "end": v(69.22, 3) * mm});
            skLineSegment(sketch, "E1284", {"start": v(69.22, 3) * mm, "end": v(69.12, 3.02) * mm});
            skLineSegment(sketch, "E1285", {"start": v(69.12, 3.02) * mm, "end": v(69.02, 3.05) * mm});
            skLineSegment(sketch, "E1286", {"start": v(69.02, 3.05) * mm, "end": v(68.93, 3.09) * mm});
            skLineSegment(sketch, "E1287", {"start": v(68.93, 3.09) * mm, "end": v(68.84, 3.14) * mm});
            skLineSegment(sketch, "E1288", {"start": v(68.84, 3.14) * mm, "end": v(68.75, 3.23) * mm});
            skLineSegment(sketch, "E1289", {"start": v(68.75, 3.23) * mm, "end": v(68.68, 3.34) * mm});
            skLineSegment(sketch, "E1290", {"start": v(68.68, 3.34) * mm, "end": v(68.63, 3.47) * mm});
            skLineSegment(sketch, "E1291", {"start": v(68.63, 3.47) * mm, "end": v(68.6, 3.6) * mm});
            skLineSegment(sketch, "E1292", {"start": v(68.6, 3.6) * mm, "end": v(68.62, 3.73) * mm});
            skLineSegment(sketch, "E1293", {"start": v(68.62, 3.73) * mm, "end": v(68.65, 3.85) * mm});
            skLineSegment(sketch, "E1294", {"start": v(68.65, 3.85) * mm, "end": v(68.7, 3.97) * mm});
            skLineSegment(sketch, "E1295", {"start": v(68.7, 3.97) * mm, "end": v(68.79, 4.07) * mm});
            skLineSegment(sketch, "E1296", {"start": v(68.79, 4.07) * mm, "end": v(68.87, 4.13) * mm});
            skLineSegment(sketch, "E1297", {"start": v(68.87, 4.13) * mm, "end": v(68.96, 4.18) * mm});
            skLineSegment(sketch, "E1298", {"start": v(68.96, 4.18) * mm, "end": v(69.06, 4.22) * mm});
            skLineSegment(sketch, "E1299", {"start": v(69.06, 4.22) * mm, "end": v(69.15, 4.24) * mm});
            skLineSegment(sketch, "E1300", {"start": v(69.15, 4.24) * mm, "end": v(69.24, 4.3) * mm});
            skLineSegment(sketch, "E1301", {"start": v(69.24, 4.3) * mm, "end": v(69.26, 4.4) * mm});
            skLineSegment(sketch, "E1302", {"start": v(69.26, 4.4) * mm, "end": v(69.25, 4.68) * mm});
            skLineSegment(sketch, "E1303", {"start": v(69.25, 4.68) * mm, "end": v(69.2, 4.77) * mm});
            skLineSegment(sketch, "E1304", {"start": v(69.2, 4.77) * mm, "end": v(69.12, 4.82) * mm});
            skLineSegment(sketch, "E1305", {"start": v(69.12, 4.82) * mm, "end": v(69.02, 4.83) * mm});
            skLineSegment(sketch, "E1306", {"start": v(69.02, 4.83) * mm, "end": v(68.92, 4.86) * mm});
            skLineSegment(sketch, "E1307", {"start": v(68.92, 4.86) * mm, "end": v(68.82, 4.9) * mm});
            skLineSegment(sketch, "E1308", {"start": v(68.82, 4.9) * mm, "end": v(68.73, 4.94) * mm});
            skLineSegment(sketch, "E1309", {"start": v(68.73, 4.94) * mm, "end": v(68.64, 5.03) * mm});
            skLineSegment(sketch, "E1310", {"start": v(68.64, 5.03) * mm, "end": v(68.56, 5.14) * mm});
            skLineSegment(sketch, "E1311", {"start": v(68.56, 5.14) * mm, "end": v(68.52, 5.26) * mm});
            skLineSegment(sketch, "E1312", {"start": v(68.52, 5.26) * mm, "end": v(68.5, 5.4) * mm});
            skLineSegment(sketch, "E1313", {"start": v(68.5, 5.4) * mm, "end": v(68.5, 5.52) * mm});
            skLineSegment(sketch, "E1314", {"start": v(68.5, 5.52) * mm, "end": v(68.52, 5.65) * mm});
            skLineSegment(sketch, "E1315", {"start": v(68.52, 5.65) * mm, "end": v(68.58, 5.77) * mm});
            skLineSegment(sketch, "E1316", {"start": v(68.58, 5.77) * mm, "end": v(68.66, 5.87) * mm});
            skLineSegment(sketch, "E1317", {"start": v(68.66, 5.87) * mm, "end": v(68.74, 5.93) * mm});
            skLineSegment(sketch, "E1318", {"start": v(68.74, 5.93) * mm, "end": v(68.83, 5.98) * mm});
            skLineSegment(sketch, "E1319", {"start": v(68.83, 5.98) * mm, "end": v(68.92, 6.02) * mm});
            skLineSegment(sketch, "E1320", {"start": v(68.92, 6.02) * mm, "end": v(69.02, 6.05) * mm});
            skLineSegment(sketch, "E1321", {"start": v(69.02, 6.05) * mm, "end": v(69.1, 6.1) * mm});
            skLineSegment(sketch, "E1322", {"start": v(69.1, 6.1) * mm, "end": v(69.13, 6.21) * mm});
            skLineSegment(sketch, "E1323", {"start": v(69.13, 6.21) * mm, "end": v(69.1, 6.49) * mm});
            skLineSegment(sketch, "E1324", {"start": v(69.1, 6.49) * mm, "end": v(69.06, 6.58) * mm});
            skLineSegment(sketch, "E1325", {"start": v(69.06, 6.58) * mm, "end": v(68.97, 6.63) * mm});
            skLineSegment(sketch, "E1326", {"start": v(68.97, 6.63) * mm, "end": v(68.87, 6.64) * mm});
            skLineSegment(sketch, "E1327", {"start": v(68.87, 6.64) * mm, "end": v(68.77, 6.66) * mm});
            skLineSegment(sketch, "E1328", {"start": v(68.77, 6.66) * mm, "end": v(68.67, 6.7) * mm});
            skLineSegment(sketch, "E1329", {"start": v(68.67, 6.7) * mm, "end": v(68.58, 6.74) * mm});
            skLineSegment(sketch, "E1330", {"start": v(68.58, 6.74) * mm, "end": v(68.48, 6.83) * mm});
            skLineSegment(sketch, "E1331", {"start": v(68.48, 6.83) * mm, "end": v(68.4, 6.93) * mm});
            skLineSegment(sketch, "E1332", {"start": v(68.4, 6.93) * mm, "end": v(68.35, 7.05) * mm});
            skLineSegment(sketch, "E1333", {"start": v(68.35, 7.05) * mm, "end": v(68.33, 7.18) * mm});
            skLineSegment(sketch, "E1334", {"start": v(68.33, 7.18) * mm, "end": v(68.33, 7.31) * mm});
            skLineSegment(sketch, "E1335", {"start": v(68.33, 7.31) * mm, "end": v(68.35, 7.44) * mm});
            skLineSegment(sketch, "E1336", {"start": v(68.35, 7.44) * mm, "end": v(68.4, 7.56) * mm});
            skLineSegment(sketch, "E1337", {"start": v(68.4, 7.56) * mm, "end": v(68.48, 7.67) * mm});
            skLineSegment(sketch, "E1338", {"start": v(68.48, 7.67) * mm, "end": v(68.56, 7.73) * mm});
            skLineSegment(sketch, "E1339", {"start": v(68.56, 7.73) * mm, "end": v(68.65, 7.78) * mm});
            skLineSegment(sketch, "E1340", {"start": v(68.65, 7.78) * mm, "end": v(68.74, 7.83) * mm});
            skLineSegment(sketch, "E1341", {"start": v(68.74, 7.83) * mm, "end": v(68.84, 7.86) * mm});
            skLineSegment(sketch, "E1342", {"start": v(68.84, 7.86) * mm, "end": v(68.92, 7.92) * mm});
            skLineSegment(sketch, "E1343", {"start": v(68.92, 7.92) * mm, "end": v(68.94, 8.02) * mm});
            skLineSegment(sketch, "E1344", {"start": v(68.94, 8.02) * mm, "end": v(68.9, 8.3) * mm});
            skLineSegment(sketch, "E1345", {"start": v(68.9, 8.3) * mm, "end": v(68.86, 8.4) * mm});
            skLineSegment(sketch, "E1346", {"start": v(68.86, 8.4) * mm, "end": v(68.77, 8.43) * mm});
            skLineSegment(sketch, "E1347", {"start": v(68.77, 8.43) * mm, "end": v(68.67, 8.44) * mm});
            skLineSegment(sketch, "E1348", {"start": v(68.67, 8.44) * mm, "end": v(68.57, 8.46) * mm});
            skLineSegment(sketch, "E1349", {"start": v(68.57, 8.46) * mm, "end": v(68.47, 8.49) * mm});
            skLineSegment(sketch, "E1350", {"start": v(68.47, 8.49) * mm, "end": v(68.38, 8.53) * mm});
            skLineSegment(sketch, "E1351", {"start": v(68.38, 8.53) * mm, "end": v(68.28, 8.62) * mm});
            skLineSegment(sketch, "E1352", {"start": v(68.28, 8.62) * mm, "end": v(68.2, 8.72) * mm});
            skLineSegment(sketch, "E1353", {"start": v(68.2, 8.72) * mm, "end": v(68.15, 8.84) * mm});
            skLineSegment(sketch, "E1354", {"start": v(68.15, 8.84) * mm, "end": v(68.12, 8.97) * mm});
            skLineSegment(sketch, "E1355", {"start": v(68.12, 8.97) * mm, "end": v(68.11, 9.1) * mm});
            skLineSegment(sketch, "E1356", {"start": v(68.11, 9.1) * mm, "end": v(68.13, 9.23) * mm});
            skLineSegment(sketch, "E1357", {"start": v(68.13, 9.23) * mm, "end": v(68.18, 9.35) * mm});
            skLineSegment(sketch, "E1358", {"start": v(68.18, 9.35) * mm, "end": v(68.26, 9.46) * mm});
            skLineSegment(sketch, "E1359", {"start": v(68.26, 9.46) * mm, "end": v(68.34, 9.52) * mm});
            skLineSegment(sketch, "E1360", {"start": v(68.34, 9.52) * mm, "end": v(68.42, 9.58) * mm});
            skLineSegment(sketch, "E1361", {"start": v(68.42, 9.58) * mm, "end": v(68.51, 9.62) * mm});
            skLineSegment(sketch, "E1362", {"start": v(68.51, 9.62) * mm, "end": v(68.6, 9.66) * mm});
            skLineSegment(sketch, "E1363", {"start": v(68.6, 9.66) * mm, "end": v(68.69, 9.72) * mm});
            skLineSegment(sketch, "E1364", {"start": v(68.69, 9.72) * mm, "end": v(68.7, 9.82) * mm});
            skLineSegment(sketch, "E1365", {"start": v(68.7, 9.82) * mm, "end": v(68.67, 10.1) * mm});
            skLineSegment(sketch, "E1366", {"start": v(68.67, 10.1) * mm, "end": v(68.62, 10.19) * mm});
            skLineSegment(sketch, "E1367", {"start": v(68.62, 10.19) * mm, "end": v(68.53, 10.23) * mm});
            skLineSegment(sketch, "E1368", {"start": v(68.53, 10.23) * mm, "end": v(68.43, 10.23) * mm});
            skLineSegment(sketch, "E1369", {"start": v(68.43, 10.23) * mm, "end": v(68.33, 10.25) * mm});
            skLineSegment(sketch, "E1370", {"start": v(68.33, 10.25) * mm, "end": v(68.23, 10.28) * mm});
            skLineSegment(sketch, "E1371", {"start": v(68.23, 10.28) * mm, "end": v(68.13, 10.32) * mm});
            skLineSegment(sketch, "E1372", {"start": v(68.13, 10.32) * mm, "end": v(68.03, 10.4) * mm});
            skLineSegment(sketch, "E1373", {"start": v(68.03, 10.4) * mm, "end": v(67.95, 10.5) * mm});
            skLineSegment(sketch, "E1374", {"start": v(67.95, 10.5) * mm, "end": v(67.9, 10.62) * mm});
            skLineSegment(sketch, "E1375", {"start": v(67.9, 10.62) * mm, "end": v(67.86, 10.75) * mm});
            skLineSegment(sketch, "E1376", {"start": v(67.86, 10.75) * mm, "end": v(67.85, 10.88) * mm});
            skLineSegment(sketch, "E1377", {"start": v(67.85, 10.88) * mm, "end": v(67.87, 11) * mm});
            skLineSegment(sketch, "E1378", {"start": v(67.87, 11) * mm, "end": v(67.91, 11.13) * mm});
            skLineSegment(sketch, "E1379", {"start": v(67.91, 11.13) * mm, "end": v(67.99, 11.24) * mm});
            skLineSegment(sketch, "E1380", {"start": v(67.99, 11.24) * mm, "end": v(68.07, 11.3) * mm});
            skLineSegment(sketch, "E1381", {"start": v(68.07, 11.3) * mm, "end": v(68.15, 11.37) * mm});
            skLineSegment(sketch, "E1382", {"start": v(68.15, 11.37) * mm, "end": v(68.24, 11.41) * mm});
            skLineSegment(sketch, "E1383", {"start": v(68.24, 11.41) * mm, "end": v(68.33, 11.45) * mm});
            skLineSegment(sketch, "E1384", {"start": v(68.33, 11.45) * mm, "end": v(68.4, 11.51) * mm});
            skLineSegment(sketch, "E1385", {"start": v(68.4, 11.51) * mm, "end": v(68.43, 11.62) * mm});
            skLineSegment(sketch, "E1386", {"start": v(68.43, 11.62) * mm, "end": v(68.38, 11.89) * mm});
            skLineSegment(sketch, "E1387", {"start": v(68.38, 11.89) * mm, "end": v(68.33, 11.98) * mm});
            skLineSegment(sketch, "E1388", {"start": v(68.33, 11.98) * mm, "end": v(68.23, 12.02) * mm});
            skLineSegment(sketch, "E1389", {"start": v(68.23, 12.02) * mm, "end": v(68.13, 12.02) * mm});
            skLineSegment(sketch, "E1390", {"start": v(68.13, 12.02) * mm, "end": v(68.03, 12.03) * mm});
            skLineSegment(sketch, "E1391", {"start": v(68.03, 12.03) * mm, "end": v(67.94, 12.06) * mm});
            skLineSegment(sketch, "E1392", {"start": v(67.94, 12.06) * mm, "end": v(67.84, 12.1) * mm});
            skLineSegment(sketch, "E1393", {"start": v(67.84, 12.1) * mm, "end": v(67.74, 12.18) * mm});
            skLineSegment(sketch, "E1394", {"start": v(67.74, 12.18) * mm, "end": v(67.65, 12.28) * mm});
            skLineSegment(sketch, "E1395", {"start": v(67.65, 12.28) * mm, "end": v(67.6, 12.4) * mm});
            skLineSegment(sketch, "E1396", {"start": v(67.6, 12.4) * mm, "end": v(67.55, 12.52) * mm});
            skLineSegment(sketch, "E1397", {"start": v(67.55, 12.52) * mm, "end": v(67.54, 12.65) * mm});
            skLineSegment(sketch, "E1398", {"start": v(67.54, 12.65) * mm, "end": v(67.56, 12.78) * mm});
            skLineSegment(sketch, "E1399", {"start": v(67.56, 12.78) * mm, "end": v(67.6, 12.9) * mm});
            skLineSegment(sketch, "E1400", {"start": v(67.6, 12.9) * mm, "end": v(67.67, 13.02) * mm});
            skLineSegment(sketch, "E1401", {"start": v(67.67, 13.02) * mm, "end": v(67.75, 13.09) * mm});
            skLineSegment(sketch, "E1402", {"start": v(67.75, 13.09) * mm, "end": v(67.83, 13.15) * mm});
            skLineSegment(sketch, "E1403", {"start": v(67.83, 13.15) * mm, "end": v(67.92, 13.2) * mm});
            skLineSegment(sketch, "E1404", {"start": v(67.92, 13.2) * mm, "end": v(68, 13.23) * mm});
            skLineSegment(sketch, "E1405", {"start": v(68, 13.23) * mm, "end": v(68.08, 13.3) * mm});
            skLineSegment(sketch, "E1406", {"start": v(68.08, 13.3) * mm, "end": v(68.1, 13.4) * mm});
            skLineSegment(sketch, "E1407", {"start": v(68.1, 13.4) * mm, "end": v(68.04, 13.67) * mm});
            skLineSegment(sketch, "E1408", {"start": v(68.04, 13.67) * mm, "end": v(68, 13.77) * mm});
            skLineSegment(sketch, "E1409", {"start": v(68, 13.77) * mm, "end": v(67.9, 13.8) * mm});
            skLineSegment(sketch, "E1410", {"start": v(67.9, 13.8) * mm, "end": v(67.8, 13.8) * mm});
            skLineSegment(sketch, "E1411", {"start": v(67.8, 13.8) * mm, "end": v(67.7, 13.81) * mm});
            skLineSegment(sketch, "E1412", {"start": v(67.7, 13.81) * mm, "end": v(67.6, 13.83) * mm});
            skLineSegment(sketch, "E1413", {"start": v(67.6, 13.83) * mm, "end": v(67.5, 13.87) * mm});
            skLineSegment(sketch, "E1414", {"start": v(67.5, 13.87) * mm, "end": v(67.4, 13.95) * mm});
            skLineSegment(sketch, "E1415", {"start": v(67.4, 13.95) * mm, "end": v(67.3, 14.04) * mm});
            skLineSegment(sketch, "E1416", {"start": v(67.3, 14.04) * mm, "end": v(67.24, 14.16) * mm});
            skLineSegment(sketch, "E1417", {"start": v(67.24, 14.16) * mm, "end": v(67.2, 14.28) * mm});
            skLineSegment(sketch, "E1418", {"start": v(67.2, 14.28) * mm, "end": v(67.19, 14.42) * mm});
            skLineSegment(sketch, "E1419", {"start": v(67.19, 14.42) * mm, "end": v(67.2, 14.55) * mm});
            skLineSegment(sketch, "E1420", {"start": v(67.2, 14.55) * mm, "end": v(67.24, 14.67) * mm});
            skLineSegment(sketch, "E1421", {"start": v(67.24, 14.67) * mm, "end": v(67.3, 14.78) * mm});
            skLineSegment(sketch, "E1422", {"start": v(67.3, 14.78) * mm, "end": v(67.38, 14.86) * mm});
            skLineSegment(sketch, "E1423", {"start": v(67.38, 14.86) * mm, "end": v(67.46, 14.92) * mm});
            skLineSegment(sketch, "E1424", {"start": v(67.46, 14.92) * mm, "end": v(67.55, 14.97) * mm});
            skLineSegment(sketch, "E1425", {"start": v(67.55, 14.97) * mm, "end": v(67.64, 15) * mm});
            skLineSegment(sketch, "E1426", {"start": v(67.64, 15) * mm, "end": v(67.71, 15.08) * mm});
            skLineSegment(sketch, "E1427", {"start": v(67.71, 15.08) * mm, "end": v(67.72, 15.18) * mm});
            skLineSegment(sketch, "E1428", {"start": v(67.72, 15.18) * mm, "end": v(67.66, 15.45) * mm});
            skLineSegment(sketch, "E1429", {"start": v(67.66, 15.45) * mm, "end": v(67.6, 15.54) * mm});
            skLineSegment(sketch, "E1430", {"start": v(67.6, 15.54) * mm, "end": v(67.51, 15.57) * mm});
            skLineSegment(sketch, "E1431", {"start": v(67.51, 15.57) * mm, "end": v(67.41, 15.57) * mm});
            skLineSegment(sketch, "E1432", {"start": v(67.41, 15.57) * mm, "end": v(67.31, 15.58) * mm});
            skLineSegment(sketch, "E1433", {"start": v(67.31, 15.58) * mm, "end": v(67.21, 15.6) * mm});
            skLineSegment(sketch, "E1434", {"start": v(67.21, 15.6) * mm, "end": v(67.11, 15.63) * mm});
            skLineSegment(sketch, "E1435", {"start": v(67.11, 15.63) * mm, "end": v(67, 15.7) * mm});
            skLineSegment(sketch, "E1436", {"start": v(67, 15.7) * mm, "end": v(66.92, 15.8) * mm});
            skLineSegment(sketch, "E1437", {"start": v(66.92, 15.8) * mm, "end": v(66.85, 15.91) * mm});
            skLineSegment(sketch, "E1438", {"start": v(66.85, 15.91) * mm, "end": v(66.8, 16.04) * mm});
            skLineSegment(sketch, "E1439", {"start": v(66.8, 16.04) * mm, "end": v(66.79, 16.17) * mm});
            skLineSegment(sketch, "E1440", {"start": v(66.79, 16.17) * mm, "end": v(66.8, 16.3) * mm});
            skLineSegment(sketch, "E1441", {"start": v(66.8, 16.3) * mm, "end": v(66.83, 16.43) * mm});
            skLineSegment(sketch, "E1442", {"start": v(66.83, 16.43) * mm, "end": v(66.9, 16.54) * mm});
            skLineSegment(sketch, "E1443", {"start": v(66.9, 16.54) * mm, "end": v(66.97, 16.61) * mm});
            skLineSegment(sketch, "E1444", {"start": v(66.97, 16.61) * mm, "end": v(67.05, 16.68) * mm});
            skLineSegment(sketch, "E1445", {"start": v(67.05, 16.68) * mm, "end": v(67.13, 16.73) * mm});
            skLineSegment(sketch, "E1446", {"start": v(67.13, 16.73) * mm, "end": v(67.22, 16.77) * mm});
            skLineSegment(sketch, "E1447", {"start": v(67.22, 16.77) * mm, "end": v(67.3, 16.84) * mm});
            skLineSegment(sketch, "E1448", {"start": v(67.3, 16.84) * mm, "end": v(67.3, 16.95) * mm});
            skLineSegment(sketch, "E1449", {"start": v(67.3, 16.95) * mm, "end": v(67.24, 17.22) * mm});
            skLineSegment(sketch, "E1450", {"start": v(67.24, 17.22) * mm, "end": v(67.18, 17.3) * mm});
            skLineSegment(sketch, "E1451", {"start": v(67.18, 17.3) * mm, "end": v(67.08, 17.33) * mm});
            skLineSegment(sketch, "E1452", {"start": v(67.08, 17.33) * mm, "end": v(66.98, 17.33) * mm});
            skLineSegment(sketch, "E1453", {"start": v(66.98, 17.33) * mm, "end": v(66.88, 17.33) * mm});
            skLineSegment(sketch, "E1454", {"start": v(66.88, 17.33) * mm, "end": v(66.78, 17.35) * mm});
            skLineSegment(sketch, "E1455", {"start": v(66.78, 17.35) * mm, "end": v(66.68, 17.38) * mm});
            skLineSegment(sketch, "E1456", {"start": v(66.68, 17.38) * mm, "end": v(66.57, 17.45) * mm});
            skLineSegment(sketch, "E1457", {"start": v(66.57, 17.45) * mm, "end": v(66.48, 17.55) * mm});
            skLineSegment(sketch, "E1458", {"start": v(66.48, 17.55) * mm, "end": v(66.4, 17.66) * mm});
            skLineSegment(sketch, "E1459", {"start": v(66.4, 17.66) * mm, "end": v(66.36, 17.78) * mm});
            skLineSegment(sketch, "E1460", {"start": v(66.36, 17.78) * mm, "end": v(66.34, 17.91) * mm});
            skLineSegment(sketch, "E1461", {"start": v(66.34, 17.91) * mm, "end": v(66.35, 18.04) * mm});
            skLineSegment(sketch, "E1462", {"start": v(66.35, 18.04) * mm, "end": v(66.38, 18.17) * mm});
            skLineSegment(sketch, "E1463", {"start": v(66.38, 18.17) * mm, "end": v(66.44, 18.29) * mm});
            skLineSegment(sketch, "E1464", {"start": v(66.44, 18.29) * mm, "end": v(66.51, 18.36) * mm});
            skLineSegment(sketch, "E1465", {"start": v(66.51, 18.36) * mm, "end": v(66.59, 18.43) * mm});
            skLineSegment(sketch, "E1466", {"start": v(66.59, 18.43) * mm, "end": v(66.67, 18.48) * mm});
            skLineSegment(sketch, "E1467", {"start": v(66.67, 18.48) * mm, "end": v(66.76, 18.53) * mm});
            skLineSegment(sketch, "E1468", {"start": v(66.76, 18.53) * mm, "end": v(66.83, 18.6) * mm});
            skLineSegment(sketch, "E1469", {"start": v(66.83, 18.6) * mm, "end": v(66.84, 18.7) * mm});
            skLineSegment(sketch, "E1470", {"start": v(66.84, 18.7) * mm, "end": v(66.76, 18.97) * mm});
            skLineSegment(sketch, "E1471", {"start": v(66.76, 18.97) * mm, "end": v(66.7, 19.06) * mm});
            skLineSegment(sketch, "E1472", {"start": v(66.7, 19.06) * mm, "end": v(66.6, 19.08) * mm});
            skLineSegment(sketch, "E1473", {"start": v(66.6, 19.08) * mm, "end": v(66.5, 19.08) * mm});
            skLineSegment(sketch, "E1474", {"start": v(66.5, 19.08) * mm, "end": v(66.4, 19.08) * mm});
            skLineSegment(sketch, "E1475", {"start": v(66.4, 19.08) * mm, "end": v(66.3, 19.1) * mm});
            skLineSegment(sketch, "E1476", {"start": v(66.3, 19.1) * mm, "end": v(66.2, 19.12) * mm});
            skLineSegment(sketch, "E1477", {"start": v(66.2, 19.12) * mm, "end": v(66.1, 19.2) * mm});
            skLineSegment(sketch, "E1478", {"start": v(66.1, 19.2) * mm, "end": v(66, 19.28) * mm});
            skLineSegment(sketch, "E1479", {"start": v(66, 19.28) * mm, "end": v(65.92, 19.4) * mm});
            skLineSegment(sketch, "E1480", {"start": v(65.92, 19.4) * mm, "end": v(65.87, 19.51) * mm});
            skLineSegment(sketch, "E1481", {"start": v(65.87, 19.51) * mm, "end": v(65.85, 19.64) * mm});
            skLineSegment(sketch, "E1482", {"start": v(65.85, 19.64) * mm, "end": v(65.85, 19.77) * mm});
            skLineSegment(sketch, "E1483", {"start": v(65.85, 19.77) * mm, "end": v(65.88, 19.9) * mm});
            skLineSegment(sketch, "E1484", {"start": v(65.88, 19.9) * mm, "end": v(65.94, 20.02) * mm});
            skLineSegment(sketch, "E1485", {"start": v(65.94, 20.02) * mm, "end": v(66, 20.1) * mm});
            skLineSegment(sketch, "E1486", {"start": v(66, 20.1) * mm, "end": v(66.08, 20.16) * mm});
            skLineSegment(sketch, "E1487", {"start": v(66.08, 20.16) * mm, "end": v(66.16, 20.22) * mm});
            skLineSegment(sketch, "E1488", {"start": v(66.16, 20.22) * mm, "end": v(66.25, 20.27) * mm});
            skLineSegment(sketch, "E1489", {"start": v(66.25, 20.27) * mm, "end": v(66.32, 20.34) * mm});
            skLineSegment(sketch, "E1490", {"start": v(66.32, 20.34) * mm, "end": v(66.32, 20.45) * mm});
            skLineSegment(sketch, "E1491", {"start": v(66.32, 20.45) * mm, "end": v(66.24, 20.71) * mm});
            skLineSegment(sketch, "E1492", {"start": v(66.24, 20.71) * mm, "end": v(66.18, 20.8) * mm});
            skLineSegment(sketch, "E1493", {"start": v(66.18, 20.8) * mm, "end": v(66.08, 20.82) * mm});
            skLineSegment(sketch, "E1494", {"start": v(66.08, 20.82) * mm, "end": v(65.98, 20.81) * mm});
            skLineSegment(sketch, "E1495", {"start": v(65.98, 20.81) * mm, "end": v(65.88, 20.81) * mm});
            skLineSegment(sketch, "E1496", {"start": v(65.88, 20.81) * mm, "end": v(65.78, 20.82) * mm});
            skLineSegment(sketch, "E1497", {"start": v(65.78, 20.82) * mm, "end": v(65.68, 20.85) * mm});
            skLineSegment(sketch, "E1498", {"start": v(65.68, 20.85) * mm, "end": v(65.57, 20.91) * mm});
            skLineSegment(sketch, "E1499", {"start": v(65.57, 20.91) * mm, "end": v(65.47, 21) * mm});
            skLineSegment(sketch, "E1500", {"start": v(65.47, 21) * mm, "end": v(65.4, 21.1) * mm});
            skLineSegment(sketch, "E1501", {"start": v(65.4, 21.1) * mm, "end": v(65.34, 21.23) * mm});
            skLineSegment(sketch, "E1502", {"start": v(65.34, 21.23) * mm, "end": v(65.31, 21.36) * mm});
            skLineSegment(sketch, "E1503", {"start": v(65.31, 21.36) * mm, "end": v(65.31, 21.5) * mm});
            skLineSegment(sketch, "E1504", {"start": v(65.31, 21.5) * mm, "end": v(65.34, 21.62) * mm});
            skLineSegment(sketch, "E1505", {"start": v(65.34, 21.62) * mm, "end": v(65.4, 21.74) * mm});
            skLineSegment(sketch, "E1506", {"start": v(65.4, 21.74) * mm, "end": v(65.46, 21.82) * mm});
            skLineSegment(sketch, "E1507", {"start": v(65.46, 21.82) * mm, "end": v(65.53, 21.89) * mm});
            skLineSegment(sketch, "E1508", {"start": v(65.53, 21.89) * mm, "end": v(65.61, 21.95) * mm});
            skLineSegment(sketch, "E1509", {"start": v(65.61, 21.95) * mm, "end": v(65.7, 22) * mm});
            skLineSegment(sketch, "E1510", {"start": v(65.7, 22) * mm, "end": v(65.76, 22.07) * mm});
            skLineSegment(sketch, "E1511", {"start": v(65.76, 22.07) * mm, "end": v(65.77, 22.18) * mm});
            skLineSegment(sketch, "E1512", {"start": v(65.77, 22.18) * mm, "end": v(65.68, 22.44) * mm});
            skLineSegment(sketch, "E1513", {"start": v(65.68, 22.44) * mm, "end": v(65.61, 22.52) * mm});
            skLineSegment(sketch, "E1514", {"start": v(65.61, 22.52) * mm, "end": v(65.51, 22.54) * mm});
            skLineSegment(sketch, "E1515", {"start": v(65.51, 22.54) * mm, "end": v(65.41, 22.53) * mm});
            skLineSegment(sketch, "E1516", {"start": v(65.41, 22.53) * mm, "end": v(65.31, 22.53) * mm});
            skLineSegment(sketch, "E1517", {"start": v(65.31, 22.53) * mm, "end": v(65.21, 22.54) * mm});
            skLineSegment(sketch, "E1518", {"start": v(65.21, 22.54) * mm, "end": v(65.11, 22.56) * mm});
            skLineSegment(sketch, "E1519", {"start": v(65.11, 22.56) * mm, "end": v(65, 22.62) * mm});
            skLineSegment(sketch, "E1520", {"start": v(65, 22.62) * mm, "end": v(64.9, 22.7) * mm});
            skLineSegment(sketch, "E1521", {"start": v(64.9, 22.7) * mm, "end": v(64.82, 22.81) * mm});
            skLineSegment(sketch, "E1522", {"start": v(64.82, 22.81) * mm, "end": v(64.76, 22.93) * mm});
            skLineSegment(sketch, "E1523", {"start": v(64.76, 22.93) * mm, "end": v(64.73, 23.06) * mm});
            skLineSegment(sketch, "E1524", {"start": v(64.73, 23.06) * mm, "end": v(64.73, 23.2) * mm});
            skLineSegment(sketch, "E1525", {"start": v(64.73, 23.2) * mm, "end": v(64.75, 23.32) * mm});
            skLineSegment(sketch, "E1526", {"start": v(64.75, 23.32) * mm, "end": v(64.8, 23.44) * mm});
            skLineSegment(sketch, "E1527", {"start": v(64.8, 23.44) * mm, "end": v(64.86, 23.52) * mm});
            skLineSegment(sketch, "E1528", {"start": v(64.86, 23.52) * mm, "end": v(64.94, 23.6) * mm});
            skLineSegment(sketch, "E1529", {"start": v(64.94, 23.6) * mm, "end": v(65.02, 23.66) * mm});
            skLineSegment(sketch, "E1530", {"start": v(65.02, 23.66) * mm, "end": v(65.1, 23.7) * mm});
            skLineSegment(sketch, "E1531", {"start": v(65.1, 23.7) * mm, "end": v(65.16, 23.79) * mm});
            skLineSegment(sketch, "E1532", {"start": v(65.16, 23.79) * mm, "end": v(65.16, 23.9) * mm});
            skLineSegment(sketch, "E1533", {"start": v(65.16, 23.9) * mm, "end": v(65.07, 24.15) * mm});
            skLineSegment(sketch, "E1534", {"start": v(65.07, 24.15) * mm, "end": v(65, 24.23) * mm});
            skLineSegment(sketch, "E1535", {"start": v(65, 24.23) * mm, "end": v(64.9, 24.25) * mm});
            skLineSegment(sketch, "E1536", {"start": v(64.9, 24.25) * mm, "end": v(64.8, 24.23) * mm});
            skLineSegment(sketch, "E1537", {"start": v(64.8, 24.23) * mm, "end": v(64.7, 24.23) * mm});
            skLineSegment(sketch, "E1538", {"start": v(64.7, 24.23) * mm, "end": v(64.6, 24.24) * mm});
            skLineSegment(sketch, "E1539", {"start": v(64.6, 24.24) * mm, "end": v(64.5, 24.26) * mm});
            skLineSegment(sketch, "E1540", {"start": v(64.5, 24.26) * mm, "end": v(64.38, 24.32) * mm});
            skLineSegment(sketch, "E1541", {"start": v(64.38, 24.32) * mm, "end": v(64.28, 24.4) * mm});
            skLineSegment(sketch, "E1542", {"start": v(64.28, 24.4) * mm, "end": v(64.2, 24.5) * mm});
            skLineSegment(sketch, "E1543", {"start": v(64.2, 24.5) * mm, "end": v(64.14, 24.62) * mm});
            skLineSegment(sketch, "E1544", {"start": v(64.14, 24.62) * mm, "end": v(64.1, 24.75) * mm});
            skLineSegment(sketch, "E1545", {"start": v(64.1, 24.75) * mm, "end": v(64.1, 24.88) * mm});
            skLineSegment(sketch, "E1546", {"start": v(64.1, 24.88) * mm, "end": v(64.12, 25) * mm});
            skLineSegment(sketch, "E1547", {"start": v(64.12, 25) * mm, "end": v(64.16, 25.13) * mm});
            skLineSegment(sketch, "E1548", {"start": v(64.16, 25.13) * mm, "end": v(64.23, 25.21) * mm});
            skLineSegment(sketch, "E1549", {"start": v(64.23, 25.21) * mm, "end": v(64.3, 25.29) * mm});
            skLineSegment(sketch, "E1550", {"start": v(64.3, 25.29) * mm, "end": v(64.37, 25.35) * mm});
            skLineSegment(sketch, "E1551", {"start": v(64.37, 25.35) * mm, "end": v(64.46, 25.4) * mm});
            skLineSegment(sketch, "E1552", {"start": v(64.46, 25.4) * mm, "end": v(64.52, 25.48) * mm});
            skLineSegment(sketch, "E1553", {"start": v(64.52, 25.48) * mm, "end": v(64.51, 25.6) * mm});
            skLineSegment(sketch, "E1554", {"start": v(64.51, 25.6) * mm, "end": v(64.41, 25.85) * mm});
            skLineSegment(sketch, "E1555", {"start": v(64.41, 25.85) * mm, "end": v(64.34, 25.93) * mm});
            skLineSegment(sketch, "E1556", {"start": v(64.34, 25.93) * mm, "end": v(64.24, 25.94) * mm});
            skLineSegment(sketch, "E1557", {"start": v(64.24, 25.94) * mm, "end": v(64.15, 25.92) * mm});
            skLineSegment(sketch, "E1558", {"start": v(64.15, 25.92) * mm, "end": v(64.05, 25.92) * mm});
            skLineSegment(sketch, "E1559", {"start": v(64.05, 25.92) * mm, "end": v(63.94, 25.92) * mm});
            skLineSegment(sketch, "E1560", {"start": v(63.94, 25.92) * mm, "end": v(63.84, 25.94) * mm});
            skLineSegment(sketch, "E1561", {"start": v(63.84, 25.94) * mm, "end": v(63.72, 26) * mm});
            skLineSegment(sketch, "E1562", {"start": v(63.72, 26) * mm, "end": v(63.62, 26.07) * mm});
            skLineSegment(sketch, "E1563", {"start": v(63.62, 26.07) * mm, "end": v(63.54, 26.18) * mm});
            skLineSegment(sketch, "E1564", {"start": v(63.54, 26.18) * mm, "end": v(63.47, 26.3) * mm});
            skLineSegment(sketch, "E1565", {"start": v(63.47, 26.3) * mm, "end": v(63.44, 26.42) * mm});
            skLineSegment(sketch, "E1566", {"start": v(63.44, 26.42) * mm, "end": v(63.42, 26.55) * mm});
            skLineSegment(sketch, "E1567", {"start": v(63.42, 26.55) * mm, "end": v(63.44, 26.68) * mm});
            skLineSegment(sketch, "E1568", {"start": v(63.44, 26.68) * mm, "end": v(63.48, 26.8) * mm});
            skLineSegment(sketch, "E1569", {"start": v(63.48, 26.8) * mm, "end": v(63.54, 26.89) * mm});
            skLineSegment(sketch, "E1570", {"start": v(63.54, 26.89) * mm, "end": v(63.61, 26.96) * mm});
            skLineSegment(sketch, "E1571", {"start": v(63.61, 26.96) * mm, "end": v(63.69, 27.03) * mm});
            skLineSegment(sketch, "E1572", {"start": v(63.69, 27.03) * mm, "end": v(63.77, 27.08) * mm});
            skLineSegment(sketch, "E1573", {"start": v(63.77, 27.08) * mm, "end": v(63.83, 27.16) * mm});
            skLineSegment(sketch, "E1574", {"start": v(63.83, 27.16) * mm, "end": v(63.82, 27.27) * mm});
            skLineSegment(sketch, "E1575", {"start": v(63.82, 27.27) * mm, "end": v(63.71, 27.52) * mm});
            skLineSegment(sketch, "E1576", {"start": v(63.71, 27.52) * mm, "end": v(63.64, 27.6) * mm});
            skLineSegment(sketch, "E1577", {"start": v(63.64, 27.6) * mm, "end": v(63.54, 27.61) * mm});
            skLineSegment(sketch, "E1578", {"start": v(63.54, 27.61) * mm, "end": v(63.45, 27.6) * mm});
            skLineSegment(sketch, "E1579", {"start": v(63.45, 27.6) * mm, "end": v(63.34, 27.58) * mm});
            skLineSegment(sketch, "E1580", {"start": v(63.34, 27.58) * mm, "end": v(63.24, 27.59) * mm});
            skLineSegment(sketch, "E1581", {"start": v(63.24, 27.59) * mm, "end": v(63.14, 27.6) * mm});
            skLineSegment(sketch, "E1582", {"start": v(63.14, 27.6) * mm, "end": v(63.02, 27.65) * mm});
            skLineSegment(sketch, "E1583", {"start": v(63.02, 27.65) * mm, "end": v(62.92, 27.73) * mm});
            skLineSegment(sketch, "E1584", {"start": v(62.92, 27.73) * mm, "end": v(62.83, 27.83) * mm});
            skLineSegment(sketch, "E1585", {"start": v(62.83, 27.83) * mm, "end": v(62.76, 27.94) * mm});
            skLineSegment(sketch, "E1586", {"start": v(62.76, 27.94) * mm, "end": v(62.72, 28.07) * mm});
            skLineSegment(sketch, "E1587", {"start": v(62.72, 28.07) * mm, "end": v(62.7, 28.2) * mm});
            skLineSegment(sketch, "E1588", {"start": v(62.7, 28.2) * mm, "end": v(62.72, 28.33) * mm});
            skLineSegment(sketch, "E1589", {"start": v(62.72, 28.33) * mm, "end": v(62.76, 28.45) * mm});
            skLineSegment(sketch, "E1590", {"start": v(62.76, 28.45) * mm, "end": v(62.82, 28.54) * mm});
            skLineSegment(sketch, "E1591", {"start": v(62.82, 28.54) * mm, "end": v(62.88, 28.62) * mm});
            skLineSegment(sketch, "E1592", {"start": v(62.88, 28.62) * mm, "end": v(62.96, 28.69) * mm});
            skLineSegment(sketch, "E1593", {"start": v(62.96, 28.69) * mm, "end": v(63.04, 28.74) * mm});
            skLineSegment(sketch, "E1594", {"start": v(63.04, 28.74) * mm, "end": v(63.1, 28.83) * mm});
            skLineSegment(sketch, "E1595", {"start": v(63.1, 28.83) * mm, "end": v(63.09, 28.93) * mm});
            skLineSegment(sketch, "E1596", {"start": v(63.09, 28.93) * mm, "end": v(62.97, 29.18) * mm});
            skLineSegment(sketch, "E1597", {"start": v(62.97, 29.18) * mm, "end": v(62.9, 29.26) * mm});
            skLineSegment(sketch, "E1598", {"start": v(62.9, 29.26) * mm, "end": v(62.8, 29.27) * mm});
            skLineSegment(sketch, "E1599", {"start": v(62.8, 29.27) * mm, "end": v(62.7, 29.24) * mm});
            skLineSegment(sketch, "E1600", {"start": v(62.7, 29.24) * mm, "end": v(62.6, 29.23) * mm});
            skLineSegment(sketch, "E1601", {"start": v(62.6, 29.23) * mm, "end": v(62.5, 29.23) * mm});
            skLineSegment(sketch, "E1602", {"start": v(62.5, 29.23) * mm, "end": v(62.4, 29.24) * mm});
            skLineSegment(sketch, "E1603", {"start": v(62.4, 29.24) * mm, "end": v(62.28, 29.3) * mm});
            skLineSegment(sketch, "E1604", {"start": v(62.28, 29.3) * mm, "end": v(62.17, 29.37) * mm});
            skLineSegment(sketch, "E1605", {"start": v(62.17, 29.37) * mm, "end": v(62.08, 29.46) * mm});
            skLineSegment(sketch, "E1606", {"start": v(62.08, 29.46) * mm, "end": v(62.01, 29.58) * mm});
            skLineSegment(sketch, "E1607", {"start": v(62.01, 29.58) * mm, "end": v(61.97, 29.7) * mm});
            skLineSegment(sketch, "E1608", {"start": v(61.97, 29.7) * mm, "end": v(61.95, 29.83) * mm});
            skLineSegment(sketch, "E1609", {"start": v(61.95, 29.83) * mm, "end": v(61.96, 29.96) * mm});
            skLineSegment(sketch, "E1610", {"start": v(61.96, 29.96) * mm, "end": v(62, 30.09) * mm});
            skLineSegment(sketch, "E1611", {"start": v(62, 30.09) * mm, "end": v(62.05, 30.17) * mm});
            skLineSegment(sketch, "E1612", {"start": v(62.05, 30.17) * mm, "end": v(62.11, 30.25) * mm});
            skLineSegment(sketch, "E1613", {"start": v(62.11, 30.25) * mm, "end": v(62.19, 30.32) * mm});
            skLineSegment(sketch, "E1614", {"start": v(62.19, 30.32) * mm, "end": v(62.27, 30.38) * mm});
            skLineSegment(sketch, "E1615", {"start": v(62.27, 30.38) * mm, "end": v(62.32, 30.47) * mm});
            skLineSegment(sketch, "E1616", {"start": v(62.32, 30.47) * mm, "end": v(62.3, 30.57) * mm});
            skLineSegment(sketch, "E1617", {"start": v(62.3, 30.57) * mm, "end": v(62.19, 30.82) * mm});
            skLineSegment(sketch, "E1618", {"start": v(62.19, 30.82) * mm, "end": v(62.11, 30.9) * mm});
            skLineSegment(sketch, "E1619", {"start": v(62.11, 30.9) * mm, "end": v(62.01, 30.9) * mm});
            skLineSegment(sketch, "E1620", {"start": v(62.01, 30.9) * mm, "end": v(61.91, 30.88) * mm});
            skLineSegment(sketch, "E1621", {"start": v(61.91, 30.88) * mm, "end": v(61.81, 30.86) * mm});
            skLineSegment(sketch, "E1622", {"start": v(61.81, 30.86) * mm, "end": v(61.71, 30.86) * mm});
            skLineSegment(sketch, "E1623", {"start": v(61.71, 30.86) * mm, "end": v(61.6, 30.87) * mm});
            skLineSegment(sketch, "E1624", {"start": v(61.6, 30.87) * mm, "end": v(61.49, 30.91) * mm});
            skLineSegment(sketch, "E1625", {"start": v(61.49, 30.91) * mm, "end": v(61.38, 30.99) * mm});
            skLineSegment(sketch, "E1626", {"start": v(61.38, 30.99) * mm, "end": v(61.29, 31.08) * mm});
            skLineSegment(sketch, "E1627", {"start": v(61.29, 31.08) * mm, "end": v(61.22, 31.2) * mm});
            skLineSegment(sketch, "E1628", {"start": v(61.22, 31.2) * mm, "end": v(61.17, 31.31) * mm});
            skLineSegment(sketch, "E1629", {"start": v(61.17, 31.31) * mm, "end": v(61.15, 31.44) * mm});
            skLineSegment(sketch, "E1630", {"start": v(61.15, 31.44) * mm, "end": v(61.15, 31.57) * mm});
            skLineSegment(sketch, "E1631", {"start": v(61.15, 31.57) * mm, "end": v(61.19, 31.7) * mm});
            skLineSegment(sketch, "E1632", {"start": v(61.19, 31.7) * mm, "end": v(61.24, 31.79) * mm});
            skLineSegment(sketch, "E1633", {"start": v(61.24, 31.79) * mm, "end": v(61.3, 31.87) * mm});
            skLineSegment(sketch, "E1634", {"start": v(61.3, 31.87) * mm, "end": v(61.37, 31.94) * mm});
            skLineSegment(sketch, "E1635", {"start": v(61.37, 31.94) * mm, "end": v(61.45, 32) * mm});
            skLineSegment(sketch, "E1636", {"start": v(61.45, 32) * mm, "end": v(61.5, 32.09) * mm});
            skLineSegment(sketch, "E1637", {"start": v(61.5, 32.09) * mm, "end": v(61.49, 32.2) * mm});
            skLineSegment(sketch, "E1638", {"start": v(61.49, 32.2) * mm, "end": v(61.36, 32.44) * mm});
            skLineSegment(sketch, "E1639", {"start": v(61.36, 32.44) * mm, "end": v(61.28, 32.51) * mm});
            skLineSegment(sketch, "E1640", {"start": v(61.28, 32.51) * mm, "end": v(61.18, 32.51) * mm});
            skLineSegment(sketch, "E1641", {"start": v(61.18, 32.51) * mm, "end": v(61.08, 32.49) * mm});
            skLineSegment(sketch, "E1642", {"start": v(61.08, 32.49) * mm, "end": v(60.99, 32.47) * mm});
            skLineSegment(sketch, "E1643", {"start": v(60.99, 32.47) * mm, "end": v(60.88, 32.46) * mm});
            skLineSegment(sketch, "E1644", {"start": v(60.88, 32.46) * mm, "end": v(60.78, 32.47) * mm});
            skLineSegment(sketch, "E1645", {"start": v(60.78, 32.47) * mm, "end": v(60.66, 32.51) * mm});
            skLineSegment(sketch, "E1646", {"start": v(60.66, 32.51) * mm, "end": v(60.55, 32.58) * mm});
            skLineSegment(sketch, "E1647", {"start": v(60.55, 32.58) * mm, "end": v(60.45, 32.67) * mm});
            skLineSegment(sketch, "E1648", {"start": v(60.45, 32.67) * mm, "end": v(60.38, 32.78) * mm});
            skLineSegment(sketch, "E1649", {"start": v(60.38, 32.78) * mm, "end": v(60.33, 32.9) * mm});
            skLineSegment(sketch, "E1650", {"start": v(60.33, 32.9) * mm, "end": v(60.3, 33.03) * mm});
            skLineSegment(sketch, "E1651", {"start": v(60.3, 33.03) * mm, "end": v(60.3, 33.16) * mm});
            skLineSegment(sketch, "E1652", {"start": v(60.3, 33.16) * mm, "end": v(60.34, 33.3) * mm});
            skLineSegment(sketch, "E1653", {"start": v(60.34, 33.3) * mm, "end": v(60.39, 33.38) * mm});
            skLineSegment(sketch, "E1654", {"start": v(60.39, 33.38) * mm, "end": v(60.45, 33.46) * mm});
            skLineSegment(sketch, "E1655", {"start": v(60.45, 33.46) * mm, "end": v(60.51, 33.54) * mm});
            skLineSegment(sketch, "E1656", {"start": v(60.51, 33.54) * mm, "end": v(60.6, 33.6) * mm});
            skLineSegment(sketch, "E1657", {"start": v(60.6, 33.6) * mm, "end": v(60.64, 33.69) * mm});
            skLineSegment(sketch, "E1658", {"start": v(60.64, 33.69) * mm, "end": v(60.62, 33.8) * mm});
            skLineSegment(sketch, "E1659", {"start": v(60.62, 33.8) * mm, "end": v(60.49, 34.03) * mm});
            skLineSegment(sketch, "E1660", {"start": v(60.49, 34.03) * mm, "end": v(60.4, 34.1) * mm});
            skLineSegment(sketch, "E1661", {"start": v(60.4, 34.1) * mm, "end": v(60.3, 34.1) * mm});
            skLineSegment(sketch, "E1662", {"start": v(60.3, 34.1) * mm, "end": v(60.21, 34.07) * mm});
            skLineSegment(sketch, "E1663", {"start": v(60.21, 34.07) * mm, "end": v(60.11, 34.05) * mm});
            skLineSegment(sketch, "E1664", {"start": v(60.11, 34.05) * mm, "end": v(60.01, 34.05) * mm});
            skLineSegment(sketch, "E1665", {"start": v(60.01, 34.05) * mm, "end": v(59.9, 34.05) * mm});
            skLineSegment(sketch, "E1666", {"start": v(59.9, 34.05) * mm, "end": v(59.78, 34.09) * mm});
            skLineSegment(sketch, "E1667", {"start": v(59.78, 34.09) * mm, "end": v(59.67, 34.16) * mm});
            skLineSegment(sketch, "E1668", {"start": v(59.67, 34.16) * mm, "end": v(59.58, 34.24) * mm});
            skLineSegment(sketch, "E1669", {"start": v(59.58, 34.24) * mm, "end": v(59.5, 34.35) * mm});
            skLineSegment(sketch, "E1670", {"start": v(59.5, 34.35) * mm, "end": v(59.44, 34.47) * mm});
            skLineSegment(sketch, "E1671", {"start": v(59.44, 34.47) * mm, "end": v(59.42, 34.6) * mm});
            skLineSegment(sketch, "E1672", {"start": v(59.42, 34.6) * mm, "end": v(59.41, 34.73) * mm});
            skLineSegment(sketch, "E1673", {"start": v(59.41, 34.73) * mm, "end": v(59.44, 34.86) * mm});
            skLineSegment(sketch, "E1674", {"start": v(59.44, 34.86) * mm, "end": v(59.5, 34.95) * mm});
            skLineSegment(sketch, "E1675", {"start": v(59.5, 34.95) * mm, "end": v(59.55, 35.03) * mm});
            skLineSegment(sketch, "E1676", {"start": v(59.55, 35.03) * mm, "end": v(59.62, 35.1) * mm});
            skLineSegment(sketch, "E1677", {"start": v(59.62, 35.1) * mm, "end": v(59.7, 35.18) * mm});
            skLineSegment(sketch, "E1678", {"start": v(59.7, 35.18) * mm, "end": v(59.74, 35.26) * mm});
            skLineSegment(sketch, "E1679", {"start": v(59.74, 35.26) * mm, "end": v(59.72, 35.37) * mm});
            skLineSegment(sketch, "E1680", {"start": v(59.72, 35.37) * mm, "end": v(59.58, 35.6) * mm});
            skLineSegment(sketch, "E1681", {"start": v(59.58, 35.6) * mm, "end": v(59.5, 35.67) * mm});
            skLineSegment(sketch, "E1682", {"start": v(59.5, 35.67) * mm, "end": v(59.4, 35.67) * mm});
            skLineSegment(sketch, "E1683", {"start": v(59.4, 35.67) * mm, "end": v(59.3, 35.64) * mm});
            skLineSegment(sketch, "E1684", {"start": v(59.3, 35.64) * mm, "end": v(59.2, 35.62) * mm});
            skLineSegment(sketch, "E1685", {"start": v(59.2, 35.62) * mm, "end": v(59.1, 35.6) * mm});
            skLineSegment(sketch, "E1686", {"start": v(59.1, 35.6) * mm, "end": v(59, 35.6) * mm});
            skLineSegment(sketch, "E1687", {"start": v(59, 35.6) * mm, "end": v(58.87, 35.64) * mm});
            skLineSegment(sketch, "E1688", {"start": v(58.87, 35.64) * mm, "end": v(58.76, 35.7) * mm});
            skLineSegment(sketch, "E1689", {"start": v(58.76, 35.7) * mm, "end": v(58.66, 35.8) * mm});
            skLineSegment(sketch, "E1690", {"start": v(58.66, 35.8) * mm, "end": v(58.58, 35.9) * mm});
            skLineSegment(sketch, "E1691", {"start": v(58.58, 35.9) * mm, "end": v(58.52, 36.02) * mm});
            skLineSegment(sketch, "E1692", {"start": v(58.52, 36.02) * mm, "end": v(58.49, 36.14) * mm});
            skLineSegment(sketch, "E1693", {"start": v(58.49, 36.14) * mm, "end": v(58.49, 36.27) * mm});
            skLineSegment(sketch, "E1694", {"start": v(58.49, 36.27) * mm, "end": v(58.51, 36.4) * mm});
            skLineSegment(sketch, "E1695", {"start": v(58.51, 36.4) * mm, "end": v(58.56, 36.5) * mm});
            skLineSegment(sketch, "E1696", {"start": v(58.56, 36.5) * mm, "end": v(58.61, 36.58) * mm});
            skLineSegment(sketch, "E1697", {"start": v(58.61, 36.58) * mm, "end": v(58.68, 36.66) * mm});
            skLineSegment(sketch, "E1698", {"start": v(58.68, 36.66) * mm, "end": v(58.75, 36.73) * mm});
            skLineSegment(sketch, "E1699", {"start": v(58.75, 36.73) * mm, "end": v(58.8, 36.81) * mm});
            skLineSegment(sketch, "E1700", {"start": v(58.8, 36.81) * mm, "end": v(58.77, 36.92) * mm});
            skLineSegment(sketch, "E1701", {"start": v(58.77, 36.92) * mm, "end": v(58.62, 37.15) * mm});
            skLineSegment(sketch, "E1702", {"start": v(58.62, 37.15) * mm, "end": v(58.54, 37.22) * mm});
            skLineSegment(sketch, "E1703", {"start": v(58.54, 37.22) * mm, "end": v(58.44, 37.21) * mm});
            skLineSegment(sketch, "E1704", {"start": v(58.44, 37.21) * mm, "end": v(58.35, 37.18) * mm});
            skLineSegment(sketch, "E1705", {"start": v(58.35, 37.18) * mm, "end": v(58.25, 37.15) * mm});
            skLineSegment(sketch, "E1706", {"start": v(58.25, 37.15) * mm, "end": v(58.15, 37.14) * mm});
            skLineSegment(sketch, "E1707", {"start": v(58.15, 37.14) * mm, "end": v(58.05, 37.14) * mm});
            skLineSegment(sketch, "E1708", {"start": v(58.05, 37.14) * mm, "end": v(57.92, 37.17) * mm});
            skLineSegment(sketch, "E1709", {"start": v(57.92, 37.17) * mm, "end": v(57.8, 37.23) * mm});
            skLineSegment(sketch, "E1710", {"start": v(57.8, 37.23) * mm, "end": v(57.7, 37.32) * mm});
            skLineSegment(sketch, "E1711", {"start": v(57.7, 37.32) * mm, "end": v(57.62, 37.42) * mm});
            skLineSegment(sketch, "E1712", {"start": v(57.62, 37.42) * mm, "end": v(57.56, 37.54) * mm});
            skLineSegment(sketch, "E1713", {"start": v(57.56, 37.54) * mm, "end": v(57.52, 37.66) * mm});
            skLineSegment(sketch, "E1714", {"start": v(57.52, 37.66) * mm, "end": v(57.52, 37.8) * mm});
            skLineSegment(sketch, "E1715", {"start": v(57.52, 37.8) * mm, "end": v(57.54, 37.92) * mm});
            skLineSegment(sketch, "E1716", {"start": v(57.54, 37.92) * mm, "end": v(57.58, 38.02) * mm});
            skLineSegment(sketch, "E1717", {"start": v(57.58, 38.02) * mm, "end": v(57.63, 38.1) * mm});
            skLineSegment(sketch, "E1718", {"start": v(57.63, 38.1) * mm, "end": v(57.7, 38.18) * mm});
            skLineSegment(sketch, "E1719", {"start": v(57.7, 38.18) * mm, "end": v(57.77, 38.25) * mm});
            skLineSegment(sketch, "E1720", {"start": v(57.77, 38.25) * mm, "end": v(57.81, 38.34) * mm});
            skLineSegment(sketch, "E1721", {"start": v(57.81, 38.34) * mm, "end": v(57.78, 38.44) * mm});
            skLineSegment(sketch, "E1722", {"start": v(57.78, 38.44) * mm, "end": v(57.63, 38.67) * mm});
            skLineSegment(sketch, "E1723", {"start": v(57.63, 38.67) * mm, "end": v(57.55, 38.74) * mm});
            skLineSegment(sketch, "E1724", {"start": v(57.55, 38.74) * mm, "end": v(57.45, 38.73) * mm});
            skLineSegment(sketch, "E1725", {"start": v(57.45, 38.73) * mm, "end": v(57.35, 38.7) * mm});
            skLineSegment(sketch, "E1726", {"start": v(57.35, 38.7) * mm, "end": v(57.26, 38.67) * mm});
            skLineSegment(sketch, "E1727", {"start": v(57.26, 38.67) * mm, "end": v(57.16, 38.65) * mm});
            skLineSegment(sketch, "E1728", {"start": v(57.16, 38.65) * mm, "end": v(57.05, 38.65) * mm});
            skLineSegment(sketch, "E1729", {"start": v(57.05, 38.65) * mm, "end": v(56.93, 38.67) * mm});
            skLineSegment(sketch, "E1730", {"start": v(56.93, 38.67) * mm, "end": v(56.8, 38.73) * mm});
            skLineSegment(sketch, "E1731", {"start": v(56.8, 38.73) * mm, "end": v(56.7, 38.81) * mm});
            skLineSegment(sketch, "E1732", {"start": v(56.7, 38.81) * mm, "end": v(56.62, 38.91) * mm});
            skLineSegment(sketch, "E1733", {"start": v(56.62, 38.91) * mm, "end": v(56.56, 39.03) * mm});
            skLineSegment(sketch, "E1734", {"start": v(56.56, 39.03) * mm, "end": v(56.52, 39.16) * mm});
            skLineSegment(sketch, "E1735", {"start": v(56.52, 39.16) * mm, "end": v(56.5, 39.29) * mm});
            skLineSegment(sketch, "E1736", {"start": v(56.5, 39.29) * mm, "end": v(56.53, 39.41) * mm});
            skLineSegment(sketch, "E1737", {"start": v(56.53, 39.41) * mm, "end": v(56.57, 39.5) * mm});
            skLineSegment(sketch, "E1738", {"start": v(56.57, 39.5) * mm, "end": v(56.62, 39.6) * mm});
            skLineSegment(sketch, "E1739", {"start": v(56.62, 39.6) * mm, "end": v(56.68, 39.68) * mm});
            skLineSegment(sketch, "E1740", {"start": v(56.68, 39.68) * mm, "end": v(56.75, 39.75) * mm});
            skLineSegment(sketch, "E1741", {"start": v(56.75, 39.75) * mm, "end": v(56.79, 39.84) * mm});
            skLineSegment(sketch, "E1742", {"start": v(56.79, 39.84) * mm, "end": v(56.76, 39.94) * mm});
            skLineSegment(sketch, "E1743", {"start": v(56.76, 39.94) * mm, "end": v(56.6, 40.17) * mm});
            skLineSegment(sketch, "E1744", {"start": v(56.6, 40.17) * mm, "end": v(56.51, 40.23) * mm});
            skLineSegment(sketch, "E1745", {"start": v(56.51, 40.23) * mm, "end": v(56.41, 40.22) * mm});
            skLineSegment(sketch, "E1746", {"start": v(56.41, 40.22) * mm, "end": v(56.32, 40.18) * mm});
            skLineSegment(sketch, "E1747", {"start": v(56.32, 40.18) * mm, "end": v(56.23, 40.15) * mm});
            skLineSegment(sketch, "E1748", {"start": v(56.23, 40.15) * mm, "end": v(56.13, 40.13) * mm});
            skLineSegment(sketch, "E1749", {"start": v(56.13, 40.13) * mm, "end": v(56.02, 40.13) * mm});
            skLineSegment(sketch, "E1750", {"start": v(56.02, 40.13) * mm, "end": v(55.9, 40.15) * mm});
            skLineSegment(sketch, "E1751", {"start": v(55.9, 40.15) * mm, "end": v(55.78, 40.2) * mm});
            skLineSegment(sketch, "E1752", {"start": v(55.78, 40.2) * mm, "end": v(55.67, 40.28) * mm});
            skLineSegment(sketch, "E1753", {"start": v(55.67, 40.28) * mm, "end": v(55.58, 40.38) * mm});
            skLineSegment(sketch, "E1754", {"start": v(55.58, 40.38) * mm, "end": v(55.52, 40.5) * mm});
            skLineSegment(sketch, "E1755", {"start": v(55.52, 40.5) * mm, "end": v(55.47, 40.62) * mm});
            skLineSegment(sketch, "E1756", {"start": v(55.47, 40.62) * mm, "end": v(55.46, 40.75) * mm});
            skLineSegment(sketch, "E1757", {"start": v(55.46, 40.75) * mm, "end": v(55.47, 40.88) * mm});
            skLineSegment(sketch, "E1758", {"start": v(55.47, 40.88) * mm, "end": v(55.51, 40.98) * mm});
            skLineSegment(sketch, "E1759", {"start": v(55.51, 40.98) * mm, "end": v(55.56, 41.07) * mm});
            skLineSegment(sketch, "E1760", {"start": v(55.56, 41.07) * mm, "end": v(55.62, 41.15) * mm});
            skLineSegment(sketch, "E1761", {"start": v(55.62, 41.15) * mm, "end": v(55.69, 41.22) * mm});
            skLineSegment(sketch, "E1762", {"start": v(55.69, 41.22) * mm, "end": v(55.73, 41.31) * mm});
            skLineSegment(sketch, "E1763", {"start": v(55.73, 41.31) * mm, "end": v(55.7, 41.42) * mm});
            skLineSegment(sketch, "E1764", {"start": v(55.7, 41.42) * mm, "end": v(55.53, 41.64) * mm});
            skLineSegment(sketch, "E1765", {"start": v(55.53, 41.64) * mm, "end": v(55.44, 41.7) * mm});
            skLineSegment(sketch, "E1766", {"start": v(55.44, 41.7) * mm, "end": v(55.34, 41.69) * mm});
            skLineSegment(sketch, "E1767", {"start": v(55.34, 41.69) * mm, "end": v(55.25, 41.64) * mm});
            skLineSegment(sketch, "E1768", {"start": v(55.25, 41.64) * mm, "end": v(55.16, 41.6) * mm});
            skLineSegment(sketch, "E1769", {"start": v(55.16, 41.6) * mm, "end": v(55.06, 41.59) * mm});
            skLineSegment(sketch, "E1770", {"start": v(55.06, 41.59) * mm, "end": v(54.95, 41.58) * mm});
            skLineSegment(sketch, "E1771", {"start": v(54.95, 41.58) * mm, "end": v(54.82, 41.6) * mm});
            skLineSegment(sketch, "E1772", {"start": v(54.82, 41.6) * mm, "end": v(54.7, 41.65) * mm});
            skLineSegment(sketch, "E1773", {"start": v(54.7, 41.65) * mm, "end": v(54.6, 41.73) * mm});
            skLineSegment(sketch, "E1774", {"start": v(54.6, 41.73) * mm, "end": v(54.5, 41.82) * mm});
            skLineSegment(sketch, "E1775", {"start": v(54.5, 41.82) * mm, "end": v(54.44, 41.94) * mm});
            skLineSegment(sketch, "E1776", {"start": v(54.44, 41.94) * mm, "end": v(54.4, 42.06) * mm});
            skLineSegment(sketch, "E1777", {"start": v(54.4, 42.06) * mm, "end": v(54.37, 42.19) * mm});
            skLineSegment(sketch, "E1778", {"start": v(54.37, 42.19) * mm, "end": v(54.38, 42.32) * mm});
            skLineSegment(sketch, "E1779", {"start": v(54.38, 42.32) * mm, "end": v(54.42, 42.42) * mm});
            skLineSegment(sketch, "E1780", {"start": v(54.42, 42.42) * mm, "end": v(54.47, 42.5) * mm});
            skLineSegment(sketch, "E1781", {"start": v(54.47, 42.5) * mm, "end": v(54.52, 42.6) * mm});
            skLineSegment(sketch, "E1782", {"start": v(54.52, 42.6) * mm, "end": v(54.59, 42.67) * mm});
            skLineSegment(sketch, "E1783", {"start": v(54.59, 42.67) * mm, "end": v(54.62, 42.76) * mm});
            skLineSegment(sketch, "E1784", {"start": v(54.62, 42.76) * mm, "end": v(54.59, 42.86) * mm});
            skLineSegment(sketch, "E1785", {"start": v(54.59, 42.86) * mm, "end": v(54.42, 43.08) * mm});
            skLineSegment(sketch, "E1786", {"start": v(54.42, 43.08) * mm, "end": v(54.33, 43.13) * mm});
            skLineSegment(sketch, "E1787", {"start": v(54.33, 43.13) * mm, "end": v(54.23, 43.12) * mm});
            skLineSegment(sketch, "E1788", {"start": v(54.23, 43.12) * mm, "end": v(54.14, 43.07) * mm});
            skLineSegment(sketch, "E1789", {"start": v(54.14, 43.07) * mm, "end": v(54.05, 43.04) * mm});
            skLineSegment(sketch, "E1790", {"start": v(54.05, 43.04) * mm, "end": v(53.95, 43.02) * mm});
            skLineSegment(sketch, "E1791", {"start": v(53.95, 43.02) * mm, "end": v(53.85, 43) * mm});
            skLineSegment(sketch, "E1792", {"start": v(53.85, 43) * mm, "end": v(53.72, 43.02) * mm});
            skLineSegment(sketch, "E1793", {"start": v(53.72, 43.02) * mm, "end": v(53.6, 43.07) * mm});
            skLineSegment(sketch, "E1794", {"start": v(53.6, 43.07) * mm, "end": v(53.49, 43.14) * mm});
            skLineSegment(sketch, "E1795", {"start": v(53.49, 43.14) * mm, "end": v(53.4, 43.24) * mm});
            skLineSegment(sketch, "E1796", {"start": v(53.4, 43.24) * mm, "end": v(53.32, 43.35) * mm});
            skLineSegment(sketch, "E1797", {"start": v(53.32, 43.35) * mm, "end": v(53.27, 43.47) * mm});
            skLineSegment(sketch, "E1798", {"start": v(53.27, 43.47) * mm, "end": v(53.25, 43.6) * mm});
            skLineSegment(sketch, "E1799", {"start": v(53.25, 43.6) * mm, "end": v(53.26, 43.73) * mm});
            skLineSegment(sketch, "E1800", {"start": v(53.26, 43.73) * mm, "end": v(53.3, 43.83) * mm});
            skLineSegment(sketch, "E1801", {"start": v(53.3, 43.83) * mm, "end": v(53.34, 43.92) * mm});
            skLineSegment(sketch, "E1802", {"start": v(53.34, 43.92) * mm, "end": v(53.39, 44) * mm});
            skLineSegment(sketch, "E1803", {"start": v(53.39, 44) * mm, "end": v(53.45, 44.08) * mm});
            skLineSegment(sketch, "E1804", {"start": v(53.45, 44.08) * mm, "end": v(53.49, 44.17) * mm});
            skLineSegment(sketch, "E1805", {"start": v(53.49, 44.17) * mm, "end": v(53.45, 44.27) * mm});
            skLineSegment(sketch, "E1806", {"start": v(53.45, 44.27) * mm, "end": v(53.27, 44.49) * mm});
            skLineSegment(sketch, "E1807", {"start": v(53.27, 44.49) * mm, "end": v(53.18, 44.54) * mm});
            skLineSegment(sketch, "E1808", {"start": v(53.18, 44.54) * mm, "end": v(53.08, 44.52) * mm});
            skLineSegment(sketch, "E1809", {"start": v(53.08, 44.52) * mm, "end": v(53, 44.48) * mm});
            skLineSegment(sketch, "E1810", {"start": v(53, 44.48) * mm, "end": v(52.9, 44.44) * mm});
            skLineSegment(sketch, "E1811", {"start": v(52.9, 44.44) * mm, "end": v(52.8, 44.41) * mm});
            skLineSegment(sketch, "E1812", {"start": v(52.8, 44.41) * mm, "end": v(52.7, 44.4) * mm});
            skLineSegment(sketch, "E1813", {"start": v(52.7, 44.4) * mm, "end": v(52.57, 44.41) * mm});
            skLineSegment(sketch, "E1814", {"start": v(52.57, 44.41) * mm, "end": v(52.45, 44.46) * mm});
            skLineSegment(sketch, "E1815", {"start": v(52.45, 44.46) * mm, "end": v(52.34, 44.53) * mm});
            skLineSegment(sketch, "E1816", {"start": v(52.34, 44.53) * mm, "end": v(52.24, 44.62) * mm});
            skLineSegment(sketch, "E1817", {"start": v(52.24, 44.62) * mm, "end": v(52.17, 44.73) * mm});
            skLineSegment(sketch, "E1818", {"start": v(52.17, 44.73) * mm, "end": v(52.12, 44.85) * mm});
            skLineSegment(sketch, "E1819", {"start": v(52.12, 44.85) * mm, "end": v(52.1, 44.98) * mm});
            skLineSegment(sketch, "E1820", {"start": v(52.1, 44.98) * mm, "end": v(52.1, 45.1) * mm});
            skLineSegment(sketch, "E1821", {"start": v(52.1, 45.1) * mm, "end": v(52.13, 45.2) * mm});
            skLineSegment(sketch, "E1822", {"start": v(52.13, 45.2) * mm, "end": v(52.17, 45.3) * mm});
            skLineSegment(sketch, "E1823", {"start": v(52.17, 45.3) * mm, "end": v(52.22, 45.39) * mm});
            skLineSegment(sketch, "E1824", {"start": v(52.22, 45.39) * mm, "end": v(52.28, 45.46) * mm});
            skLineSegment(sketch, "E1825", {"start": v(52.28, 45.46) * mm, "end": v(52.31, 45.56) * mm});
            skLineSegment(sketch, "E1826", {"start": v(52.31, 45.56) * mm, "end": v(52.27, 45.66) * mm});
            skLineSegment(sketch, "E1827", {"start": v(52.27, 45.66) * mm, "end": v(52.1, 45.86) * mm});
            skLineSegment(sketch, "E1828", {"start": v(52.1, 45.86) * mm, "end": v(52, 45.92) * mm});
            skLineSegment(sketch, "E1829", {"start": v(52, 45.92) * mm, "end": v(51.9, 45.9) * mm});
            skLineSegment(sketch, "E1830", {"start": v(51.9, 45.9) * mm, "end": v(51.81, 45.85) * mm});
            skLineSegment(sketch, "E1831", {"start": v(51.81, 45.85) * mm, "end": v(51.72, 45.8) * mm});
            skLineSegment(sketch, "E1832", {"start": v(51.72, 45.8) * mm, "end": v(51.62, 45.78) * mm});
            skLineSegment(sketch, "E1833", {"start": v(51.62, 45.78) * mm, "end": v(51.52, 45.76) * mm});
            skLineSegment(sketch, "E1834", {"start": v(51.52, 45.76) * mm, "end": v(51.4, 45.77) * mm});
            skLineSegment(sketch, "E1835", {"start": v(51.4, 45.77) * mm, "end": v(51.27, 45.82) * mm});
            skLineSegment(sketch, "E1836", {"start": v(51.27, 45.82) * mm, "end": v(51.15, 45.88) * mm});
            skLineSegment(sketch, "E1837", {"start": v(51.15, 45.88) * mm, "end": v(51.06, 45.97) * mm});
            skLineSegment(sketch, "E1838", {"start": v(51.06, 45.97) * mm, "end": v(50.98, 46.08) * mm});
            skLineSegment(sketch, "E1839", {"start": v(50.98, 46.08) * mm, "end": v(50.92, 46.2) * mm});
            skLineSegment(sketch, "E1840", {"start": v(50.92, 46.2) * mm, "end": v(50.9, 46.32) * mm});
            skLineSegment(sketch, "E1841", {"start": v(50.9, 46.32) * mm, "end": v(50.9, 46.46) * mm});
            skLineSegment(sketch, "E1842", {"start": v(50.9, 46.46) * mm, "end": v(50.93, 46.55) * mm});
            skLineSegment(sketch, "E1843", {"start": v(50.93, 46.55) * mm, "end": v(50.96, 46.65) * mm});
            skLineSegment(sketch, "E1844", {"start": v(50.96, 46.65) * mm, "end": v(51.01, 46.74) * mm});
            skLineSegment(sketch, "E1845", {"start": v(51.01, 46.74) * mm, "end": v(51.07, 46.82) * mm});
            skLineSegment(sketch, "E1846", {"start": v(51.07, 46.82) * mm, "end": v(51.1, 46.91) * mm});
            skLineSegment(sketch, "E1847", {"start": v(51.1, 46.91) * mm, "end": v(51.06, 47.01) * mm});
            skLineSegment(sketch, "E1848", {"start": v(51.06, 47.01) * mm, "end": v(50.87, 47.21) * mm});
            skLineSegment(sketch, "E1849", {"start": v(50.87, 47.21) * mm, "end": v(50.78, 47.26) * mm});
            skLineSegment(sketch, "E1850", {"start": v(50.78, 47.26) * mm, "end": v(50.68, 47.24) * mm});
            skLineSegment(sketch, "E1851", {"start": v(50.68, 47.24) * mm, "end": v(50.6, 47.19) * mm});
            skLineSegment(sketch, "E1852", {"start": v(50.6, 47.19) * mm, "end": v(50.5, 47.15) * mm});
            skLineSegment(sketch, "E1853", {"start": v(50.5, 47.15) * mm, "end": v(50.4, 47.12) * mm});
            skLineSegment(sketch, "E1854", {"start": v(50.4, 47.12) * mm, "end": v(50.3, 47.1) * mm});
            skLineSegment(sketch, "E1855", {"start": v(50.3, 47.1) * mm, "end": v(50.18, 47.1) * mm});
            skLineSegment(sketch, "E1856", {"start": v(50.18, 47.1) * mm, "end": v(50.05, 47.14) * mm});
            skLineSegment(sketch, "E1857", {"start": v(50.05, 47.14) * mm, "end": v(49.94, 47.2) * mm});
            skLineSegment(sketch, "E1858", {"start": v(49.94, 47.2) * mm, "end": v(49.84, 47.3) * mm});
            skLineSegment(sketch, "E1859", {"start": v(49.84, 47.3) * mm, "end": v(49.75, 47.4) * mm});
            skLineSegment(sketch, "E1860", {"start": v(49.75, 47.4) * mm, "end": v(49.7, 47.51) * mm});
            skLineSegment(sketch, "E1861", {"start": v(49.7, 47.51) * mm, "end": v(49.67, 47.64) * mm});
            skLineSegment(sketch, "E1862", {"start": v(49.67, 47.64) * mm, "end": v(49.66, 47.77) * mm});
            skLineSegment(sketch, "E1863", {"start": v(49.66, 47.77) * mm, "end": v(49.69, 47.87) * mm});
            skLineSegment(sketch, "E1864", {"start": v(49.69, 47.87) * mm, "end": v(49.73, 47.97) * mm});
            skLineSegment(sketch, "E1865", {"start": v(49.73, 47.97) * mm, "end": v(49.77, 48.06) * mm});
            skLineSegment(sketch, "E1866", {"start": v(49.77, 48.06) * mm, "end": v(49.83, 48.14) * mm});
            skLineSegment(sketch, "E1867", {"start": v(49.83, 48.14) * mm, "end": v(49.86, 48.23) * mm});
            skLineSegment(sketch, "E1868", {"start": v(49.86, 48.23) * mm, "end": v(49.81, 48.33) * mm});
            skLineSegment(sketch, "E1869", {"start": v(49.81, 48.33) * mm, "end": v(49.62, 48.53) * mm});
            skLineSegment(sketch, "E1870", {"start": v(49.62, 48.53) * mm, "end": v(49.52, 48.58) * mm});
            skLineSegment(sketch, "E1871", {"start": v(49.52, 48.58) * mm, "end": v(49.43, 48.55) * mm});
            skLineSegment(sketch, "E1872", {"start": v(49.43, 48.55) * mm, "end": v(49.34, 48.5) * mm});
            skLineSegment(sketch, "E1873", {"start": v(49.34, 48.5) * mm, "end": v(49.25, 48.45) * mm});
            skLineSegment(sketch, "E1874", {"start": v(49.25, 48.45) * mm, "end": v(49.16, 48.42) * mm});
            skLineSegment(sketch, "E1875", {"start": v(49.16, 48.42) * mm, "end": v(49.06, 48.4) * mm});
            skLineSegment(sketch, "E1876", {"start": v(49.06, 48.4) * mm, "end": v(48.92, 48.4) * mm});
            skLineSegment(sketch, "E1877", {"start": v(48.92, 48.4) * mm, "end": v(48.8, 48.44) * mm});
            skLineSegment(sketch, "E1878", {"start": v(48.8, 48.44) * mm, "end": v(48.68, 48.5) * mm});
            skLineSegment(sketch, "E1879", {"start": v(48.68, 48.5) * mm, "end": v(48.58, 48.58) * mm});
            skLineSegment(sketch, "E1880", {"start": v(48.58, 48.58) * mm, "end": v(48.5, 48.68) * mm});
            skLineSegment(sketch, "E1881", {"start": v(48.5, 48.68) * mm, "end": v(48.44, 48.8) * mm});
            skLineSegment(sketch, "E1882", {"start": v(48.44, 48.8) * mm, "end": v(48.4, 48.92) * mm});
            skLineSegment(sketch, "E1883", {"start": v(48.4, 48.92) * mm, "end": v(48.4, 49.06) * mm});
            skLineSegment(sketch, "E1884", {"start": v(48.4, 49.06) * mm, "end": v(48.42, 49.16) * mm});
            skLineSegment(sketch, "E1885", {"start": v(48.42, 49.16) * mm, "end": v(48.45, 49.25) * mm});
            skLineSegment(sketch, "E1886", {"start": v(48.45, 49.25) * mm, "end": v(48.5, 49.34) * mm});
            skLineSegment(sketch, "E1887", {"start": v(48.5, 49.34) * mm, "end": v(48.55, 49.43) * mm});
            skLineSegment(sketch, "E1888", {"start": v(48.55, 49.43) * mm, "end": v(48.58, 49.52) * mm});
            skLineSegment(sketch, "E1889", {"start": v(48.58, 49.52) * mm, "end": v(48.53, 49.62) * mm});
            skLineSegment(sketch, "E1890", {"start": v(48.53, 49.62) * mm, "end": v(48.33, 49.81) * mm});
            skLineSegment(sketch, "E1891", {"start": v(48.33, 49.81) * mm, "end": v(48.23, 49.86) * mm});
            skLineSegment(sketch, "E1892", {"start": v(48.23, 49.86) * mm, "end": v(48.14, 49.83) * mm});
            skLineSegment(sketch, "E1893", {"start": v(48.14, 49.83) * mm, "end": v(48.06, 49.77) * mm});
            skLineSegment(sketch, "E1894", {"start": v(48.06, 49.77) * mm, "end": v(47.97, 49.73) * mm});
            skLineSegment(sketch, "E1895", {"start": v(47.97, 49.73) * mm, "end": v(47.87, 49.69) * mm});
            skLineSegment(sketch, "E1896", {"start": v(47.87, 49.69) * mm, "end": v(47.77, 49.66) * mm});
            skLineSegment(sketch, "E1897", {"start": v(47.77, 49.66) * mm, "end": v(47.64, 49.67) * mm});
            skLineSegment(sketch, "E1898", {"start": v(47.64, 49.67) * mm, "end": v(47.51, 49.7) * mm});
            skLineSegment(sketch, "E1899", {"start": v(47.51, 49.7) * mm, "end": v(47.4, 49.75) * mm});
            skLineSegment(sketch, "E1900", {"start": v(47.4, 49.75) * mm, "end": v(47.3, 49.84) * mm});
            skLineSegment(sketch, "E1901", {"start": v(47.3, 49.84) * mm, "end": v(47.2, 49.94) * mm});
            skLineSegment(sketch, "E1902", {"start": v(47.2, 49.94) * mm, "end": v(47.14, 50.05) * mm});
            skLineSegment(sketch, "E1903", {"start": v(47.14, 50.05) * mm, "end": v(47.1, 50.18) * mm});
            skLineSegment(sketch, "E1904", {"start": v(47.1, 50.18) * mm, "end": v(47.1, 50.3) * mm});
            skLineSegment(sketch, "E1905", {"start": v(47.1, 50.3) * mm, "end": v(47.12, 50.4) * mm});
            skLineSegment(sketch, "E1906", {"start": v(47.12, 50.4) * mm, "end": v(47.15, 50.5) * mm});
            skLineSegment(sketch, "E1907", {"start": v(47.15, 50.5) * mm, "end": v(47.19, 50.6) * mm});
            skLineSegment(sketch, "E1908", {"start": v(47.19, 50.6) * mm, "end": v(47.24, 50.68) * mm});
            skLineSegment(sketch, "E1909", {"start": v(47.24, 50.68) * mm, "end": v(47.26, 50.78) * mm});
            skLineSegment(sketch, "E1910", {"start": v(47.26, 50.78) * mm, "end": v(47.21, 50.87) * mm});
            skLineSegment(sketch, "E1911", {"start": v(47.21, 50.87) * mm, "end": v(47.01, 51.06) * mm});
            skLineSegment(sketch, "E1912", {"start": v(47.01, 51.06) * mm, "end": v(46.91, 51.1) * mm});
            skLineSegment(sketch, "E1913", {"start": v(46.91, 51.1) * mm, "end": v(46.82, 51.07) * mm});
            skLineSegment(sketch, "E1914", {"start": v(46.82, 51.07) * mm, "end": v(46.74, 51.01) * mm});
            skLineSegment(sketch, "E1915", {"start": v(46.74, 51.01) * mm, "end": v(46.65, 50.96) * mm});
            skLineSegment(sketch, "E1916", {"start": v(46.65, 50.96) * mm, "end": v(46.56, 50.93) * mm});
            skLineSegment(sketch, "E1917", {"start": v(46.56, 50.93) * mm, "end": v(46.46, 50.9) * mm});
            skLineSegment(sketch, "E1918", {"start": v(46.46, 50.9) * mm, "end": v(46.32, 50.9) * mm});
            skLineSegment(sketch, "E1919", {"start": v(46.32, 50.9) * mm, "end": v(46.2, 50.92) * mm});
            skLineSegment(sketch, "E1920", {"start": v(46.2, 50.92) * mm, "end": v(46.08, 50.98) * mm});
            skLineSegment(sketch, "E1921", {"start": v(46.08, 50.98) * mm, "end": v(45.97, 51.06) * mm});
            skLineSegment(sketch, "E1922", {"start": v(45.97, 51.06) * mm, "end": v(45.88, 51.15) * mm});
            skLineSegment(sketch, "E1923", {"start": v(45.88, 51.15) * mm, "end": v(45.82, 51.27) * mm});
            skLineSegment(sketch, "E1924", {"start": v(45.82, 51.27) * mm, "end": v(45.77, 51.4) * mm});
            skLineSegment(sketch, "E1925", {"start": v(45.77, 51.4) * mm, "end": v(45.76, 51.52) * mm});
            skLineSegment(sketch, "E1926", {"start": v(45.76, 51.52) * mm, "end": v(45.78, 51.62) * mm});
            skLineSegment(sketch, "E1927", {"start": v(45.78, 51.62) * mm, "end": v(45.8, 51.72) * mm});
            skLineSegment(sketch, "E1928", {"start": v(45.8, 51.72) * mm, "end": v(45.85, 51.81) * mm});
            skLineSegment(sketch, "E1929", {"start": v(45.85, 51.81) * mm, "end": v(45.9, 51.9) * mm});
            skLineSegment(sketch, "E1930", {"start": v(45.9, 51.9) * mm, "end": v(45.92, 52) * mm});
            skLineSegment(sketch, "E1931", {"start": v(45.92, 52) * mm, "end": v(45.86, 52.1) * mm});
            skLineSegment(sketch, "E1932", {"start": v(45.86, 52.1) * mm, "end": v(45.66, 52.27) * mm});
            skLineSegment(sketch, "E1933", {"start": v(45.66, 52.27) * mm, "end": v(45.56, 52.31) * mm});
            skLineSegment(sketch, "E1934", {"start": v(45.56, 52.31) * mm, "end": v(45.46, 52.28) * mm});
            skLineSegment(sketch, "E1935", {"start": v(45.46, 52.28) * mm, "end": v(45.39, 52.22) * mm});
            skLineSegment(sketch, "E1936", {"start": v(45.39, 52.22) * mm, "end": v(45.3, 52.17) * mm});
            skLineSegment(sketch, "E1937", {"start": v(45.3, 52.17) * mm, "end": v(45.2, 52.13) * mm});
            skLineSegment(sketch, "E1938", {"start": v(45.2, 52.13) * mm, "end": v(45.1, 52.1) * mm});
            skLineSegment(sketch, "E1939", {"start": v(45.1, 52.1) * mm, "end": v(44.98, 52.1) * mm});
            skLineSegment(sketch, "E1940", {"start": v(44.98, 52.1) * mm, "end": v(44.85, 52.12) * mm});
            skLineSegment(sketch, "E1941", {"start": v(44.85, 52.12) * mm, "end": v(44.73, 52.17) * mm});
            skLineSegment(sketch, "E1942", {"start": v(44.73, 52.17) * mm, "end": v(44.62, 52.24) * mm});
            skLineSegment(sketch, "E1943", {"start": v(44.62, 52.24) * mm, "end": v(44.53, 52.34) * mm});
            skLineSegment(sketch, "E1944", {"start": v(44.53, 52.34) * mm, "end": v(44.46, 52.45) * mm});
            skLineSegment(sketch, "E1945", {"start": v(44.46, 52.45) * mm, "end": v(44.41, 52.57) * mm});
            skLineSegment(sketch, "E1946", {"start": v(44.41, 52.57) * mm, "end": v(44.4, 52.7) * mm});
            skLineSegment(sketch, "E1947", {"start": v(44.4, 52.7) * mm, "end": v(44.41, 52.8) * mm});
            skLineSegment(sketch, "E1948", {"start": v(44.41, 52.8) * mm, "end": v(44.44, 52.9) * mm});
            skLineSegment(sketch, "E1949", {"start": v(44.44, 52.9) * mm, "end": v(44.48, 53) * mm});
            skLineSegment(sketch, "E1950", {"start": v(44.48, 53) * mm, "end": v(44.52, 53.08) * mm});
            skLineSegment(sketch, "E1951", {"start": v(44.52, 53.08) * mm, "end": v(44.54, 53.18) * mm});
            skLineSegment(sketch, "E1952", {"start": v(44.54, 53.18) * mm, "end": v(44.49, 53.27) * mm});
            skLineSegment(sketch, "E1953", {"start": v(44.49, 53.27) * mm, "end": v(44.27, 53.45) * mm});
            skLineSegment(sketch, "E1954", {"start": v(44.27, 53.45) * mm, "end": v(44.17, 53.49) * mm});
            skLineSegment(sketch, "E1955", {"start": v(44.17, 53.49) * mm, "end": v(44.08, 53.45) * mm});
            skLineSegment(sketch, "E1956", {"start": v(44.08, 53.45) * mm, "end": v(44, 53.39) * mm});
            skLineSegment(sketch, "E1957", {"start": v(44, 53.39) * mm, "end": v(43.92, 53.34) * mm});
            skLineSegment(sketch, "E1958", {"start": v(43.92, 53.34) * mm, "end": v(43.83, 53.3) * mm});
            skLineSegment(sketch, "E1959", {"start": v(43.83, 53.3) * mm, "end": v(43.73, 53.26) * mm});
            skLineSegment(sketch, "E1960", {"start": v(43.73, 53.26) * mm, "end": v(43.6, 53.25) * mm});
            skLineSegment(sketch, "E1961", {"start": v(43.6, 53.25) * mm, "end": v(43.47, 53.27) * mm});
            skLineSegment(sketch, "E1962", {"start": v(43.47, 53.27) * mm, "end": v(43.35, 53.32) * mm});
            skLineSegment(sketch, "E1963", {"start": v(43.35, 53.32) * mm, "end": v(43.24, 53.4) * mm});
            skLineSegment(sketch, "E1964", {"start": v(43.24, 53.4) * mm, "end": v(43.14, 53.49) * mm});
            skLineSegment(sketch, "E1965", {"start": v(43.14, 53.49) * mm, "end": v(43.07, 53.6) * mm});
            skLineSegment(sketch, "E1966", {"start": v(43.07, 53.6) * mm, "end": v(43.02, 53.72) * mm});
            skLineSegment(sketch, "E1967", {"start": v(43.02, 53.72) * mm, "end": v(43, 53.85) * mm});
            skLineSegment(sketch, "E1968", {"start": v(43, 53.85) * mm, "end": v(43.02, 53.95) * mm});
            skLineSegment(sketch, "E1969", {"start": v(43.02, 53.95) * mm, "end": v(43.04, 54.05) * mm});
            skLineSegment(sketch, "E1970", {"start": v(43.04, 54.05) * mm, "end": v(43.07, 54.14) * mm});
            skLineSegment(sketch, "E1971", {"start": v(43.07, 54.14) * mm, "end": v(43.12, 54.23) * mm});
            skLineSegment(sketch, "E1972", {"start": v(43.12, 54.23) * mm, "end": v(43.13, 54.33) * mm});
            skLineSegment(sketch, "E1973", {"start": v(43.13, 54.33) * mm, "end": v(43.08, 54.42) * mm});
            skLineSegment(sketch, "E1974", {"start": v(43.08, 54.42) * mm, "end": v(42.86, 54.59) * mm});
            skLineSegment(sketch, "E1975", {"start": v(42.86, 54.59) * mm, "end": v(42.76, 54.62) * mm});
            skLineSegment(sketch, "E1976", {"start": v(42.76, 54.62) * mm, "end": v(42.67, 54.59) * mm});
            skLineSegment(sketch, "E1977", {"start": v(42.67, 54.59) * mm, "end": v(42.6, 54.52) * mm});
            skLineSegment(sketch, "E1978", {"start": v(42.6, 54.52) * mm, "end": v(42.5, 54.47) * mm});
            skLineSegment(sketch, "E1979", {"start": v(42.5, 54.47) * mm, "end": v(42.42, 54.42) * mm});
            skLineSegment(sketch, "E1980", {"start": v(42.42, 54.42) * mm, "end": v(42.32, 54.38) * mm});
            skLineSegment(sketch, "E1981", {"start": v(42.32, 54.38) * mm, "end": v(42.19, 54.37) * mm});
            skLineSegment(sketch, "E1982", {"start": v(42.19, 54.37) * mm, "end": v(42.06, 54.4) * mm});
            skLineSegment(sketch, "E1983", {"start": v(42.06, 54.4) * mm, "end": v(41.94, 54.44) * mm});
            skLineSegment(sketch, "E1984", {"start": v(41.94, 54.44) * mm, "end": v(41.82, 54.5) * mm});
            skLineSegment(sketch, "E1985", {"start": v(41.82, 54.5) * mm, "end": v(41.73, 54.6) * mm});
            skLineSegment(sketch, "E1986", {"start": v(41.73, 54.6) * mm, "end": v(41.65, 54.7) * mm});
            skLineSegment(sketch, "E1987", {"start": v(41.65, 54.7) * mm, "end": v(41.6, 54.82) * mm});
            skLineSegment(sketch, "E1988", {"start": v(41.6, 54.82) * mm, "end": v(41.58, 54.95) * mm});
            skLineSegment(sketch, "E1989", {"start": v(41.58, 54.95) * mm, "end": v(41.59, 55.06) * mm});
            skLineSegment(sketch, "E1990", {"start": v(41.59, 55.06) * mm, "end": v(41.6, 55.16) * mm});
            skLineSegment(sketch, "E1991", {"start": v(41.6, 55.16) * mm, "end": v(41.64, 55.25) * mm});
            skLineSegment(sketch, "E1992", {"start": v(41.64, 55.25) * mm, "end": v(41.69, 55.34) * mm});
            skLineSegment(sketch, "E1993", {"start": v(41.69, 55.34) * mm, "end": v(41.7, 55.44) * mm});
            skLineSegment(sketch, "E1994", {"start": v(41.7, 55.44) * mm, "end": v(41.64, 55.53) * mm});
            skLineSegment(sketch, "E1995", {"start": v(41.64, 55.53) * mm, "end": v(41.42, 55.7) * mm});
            skLineSegment(sketch, "E1996", {"start": v(41.42, 55.7) * mm, "end": v(41.31, 55.73) * mm});
            skLineSegment(sketch, "E1997", {"start": v(41.31, 55.73) * mm, "end": v(41.22, 55.69) * mm});
            skLineSegment(sketch, "E1998", {"start": v(41.22, 55.69) * mm, "end": v(41.15, 55.62) * mm});
            skLineSegment(sketch, "E1999", {"start": v(41.15, 55.62) * mm, "end": v(41.07, 55.56) * mm});
            skLineSegment(sketch, "E2000", {"start": v(41.07, 55.56) * mm, "end": v(40.98, 55.51) * mm});
            skLineSegment(sketch, "E2001", {"start": v(40.98, 55.51) * mm, "end": v(40.88, 55.47) * mm});
            skLineSegment(sketch, "E2002", {"start": v(40.88, 55.47) * mm, "end": v(40.75, 55.46) * mm});
            skLineSegment(sketch, "E2003", {"start": v(40.75, 55.46) * mm, "end": v(40.62, 55.47) * mm});
            skLineSegment(sketch, "E2004", {"start": v(40.62, 55.47) * mm, "end": v(40.5, 55.52) * mm});
            skLineSegment(sketch, "E2005", {"start": v(40.5, 55.52) * mm, "end": v(40.38, 55.58) * mm});
            skLineSegment(sketch, "E2006", {"start": v(40.38, 55.58) * mm, "end": v(40.28, 55.67) * mm});
            skLineSegment(sketch, "E2007", {"start": v(40.28, 55.67) * mm, "end": v(40.2, 55.78) * mm});
            skLineSegment(sketch, "E2008", {"start": v(40.2, 55.78) * mm, "end": v(40.15, 55.9) * mm});
            skLineSegment(sketch, "E2009", {"start": v(40.15, 55.9) * mm, "end": v(40.13, 56.02) * mm});
            skLineSegment(sketch, "E2010", {"start": v(40.13, 56.02) * mm, "end": v(40.13, 56.13) * mm});
            skLineSegment(sketch, "E2011", {"start": v(40.13, 56.13) * mm, "end": v(40.15, 56.23) * mm});
            skLineSegment(sketch, "E2012", {"start": v(40.15, 56.23) * mm, "end": v(40.18, 56.32) * mm});
            skLineSegment(sketch, "E2013", {"start": v(40.18, 56.32) * mm, "end": v(40.22, 56.41) * mm});
            skLineSegment(sketch, "E2014", {"start": v(40.22, 56.41) * mm, "end": v(40.23, 56.51) * mm});
            skLineSegment(sketch, "E2015", {"start": v(40.23, 56.51) * mm, "end": v(40.17, 56.6) * mm});
            skLineSegment(sketch, "E2016", {"start": v(40.17, 56.6) * mm, "end": v(39.94, 56.76) * mm});
            skLineSegment(sketch, "E2017", {"start": v(39.94, 56.76) * mm, "end": v(39.84, 56.79) * mm});
            skLineSegment(sketch, "E2018", {"start": v(39.84, 56.79) * mm, "end": v(39.75, 56.75) * mm});
            skLineSegment(sketch, "E2019", {"start": v(39.75, 56.75) * mm, "end": v(39.68, 56.68) * mm});
            skLineSegment(sketch, "E2020", {"start": v(39.68, 56.68) * mm, "end": v(39.6, 56.62) * mm});
            skLineSegment(sketch, "E2021", {"start": v(39.6, 56.62) * mm, "end": v(39.5, 56.57) * mm});
            skLineSegment(sketch, "E2022", {"start": v(39.5, 56.57) * mm, "end": v(39.41, 56.53) * mm});
            skLineSegment(sketch, "E2023", {"start": v(39.41, 56.53) * mm, "end": v(39.29, 56.5) * mm});
            skLineSegment(sketch, "E2024", {"start": v(39.29, 56.5) * mm, "end": v(39.16, 56.52) * mm});
            skLineSegment(sketch, "E2025", {"start": v(39.16, 56.52) * mm, "end": v(39.03, 56.56) * mm});
            skLineSegment(sketch, "E2026", {"start": v(39.03, 56.56) * mm, "end": v(38.91, 56.62) * mm});
            skLineSegment(sketch, "E2027", {"start": v(38.91, 56.62) * mm, "end": v(38.81, 56.7) * mm});
            skLineSegment(sketch, "E2028", {"start": v(38.81, 56.7) * mm, "end": v(38.73, 56.8) * mm});
            skLineSegment(sketch, "E2029", {"start": v(38.73, 56.8) * mm, "end": v(38.67, 56.93) * mm});
            skLineSegment(sketch, "E2030", {"start": v(38.67, 56.93) * mm, "end": v(38.65, 57.05) * mm});
            skLineSegment(sketch, "E2031", {"start": v(38.65, 57.05) * mm, "end": v(38.65, 57.16) * mm});
            skLineSegment(sketch, "E2032", {"start": v(38.65, 57.16) * mm, "end": v(38.67, 57.26) * mm});
            skLineSegment(sketch, "E2033", {"start": v(38.67, 57.26) * mm, "end": v(38.7, 57.35) * mm});
            skLineSegment(sketch, "E2034", {"start": v(38.7, 57.35) * mm, "end": v(38.73, 57.45) * mm});
            skLineSegment(sketch, "E2035", {"start": v(38.73, 57.45) * mm, "end": v(38.74, 57.55) * mm});
            skLineSegment(sketch, "E2036", {"start": v(38.74, 57.55) * mm, "end": v(38.67, 57.63) * mm});
            skLineSegment(sketch, "E2037", {"start": v(38.67, 57.63) * mm, "end": v(38.44, 57.78) * mm});
            skLineSegment(sketch, "E2038", {"start": v(38.44, 57.78) * mm, "end": v(38.34, 57.81) * mm});
            skLineSegment(sketch, "E2039", {"start": v(38.34, 57.81) * mm, "end": v(38.25, 57.77) * mm});
            skLineSegment(sketch, "E2040", {"start": v(38.25, 57.77) * mm, "end": v(38.18, 57.7) * mm});
            skLineSegment(sketch, "E2041", {"start": v(38.18, 57.7) * mm, "end": v(38.1, 57.63) * mm});
            skLineSegment(sketch, "E2042", {"start": v(38.1, 57.63) * mm, "end": v(38.02, 57.58) * mm});
            skLineSegment(sketch, "E2043", {"start": v(38.02, 57.58) * mm, "end": v(37.92, 57.54) * mm});
            skLineSegment(sketch, "E2044", {"start": v(37.92, 57.54) * mm, "end": v(37.8, 57.52) * mm});
            skLineSegment(sketch, "E2045", {"start": v(37.8, 57.52) * mm, "end": v(37.66, 57.52) * mm});
            skLineSegment(sketch, "E2046", {"start": v(37.66, 57.52) * mm, "end": v(37.54, 57.56) * mm});
            skLineSegment(sketch, "E2047", {"start": v(37.54, 57.56) * mm, "end": v(37.42, 57.62) * mm});
            skLineSegment(sketch, "E2048", {"start": v(37.42, 57.62) * mm, "end": v(37.32, 57.7) * mm});
            skLineSegment(sketch, "E2049", {"start": v(37.32, 57.7) * mm, "end": v(37.23, 57.8) * mm});
            skLineSegment(sketch, "E2050", {"start": v(37.23, 57.8) * mm, "end": v(37.17, 57.92) * mm});
            skLineSegment(sketch, "E2051", {"start": v(37.17, 57.92) * mm, "end": v(37.14, 58.05) * mm});
            skLineSegment(sketch, "E2052", {"start": v(37.14, 58.05) * mm, "end": v(37.14, 58.15) * mm});
            skLineSegment(sketch, "E2053", {"start": v(37.14, 58.15) * mm, "end": v(37.15, 58.25) * mm});
            skLineSegment(sketch, "E2054", {"start": v(37.15, 58.25) * mm, "end": v(37.18, 58.35) * mm});
            skLineSegment(sketch, "E2055", {"start": v(37.18, 58.35) * mm, "end": v(37.21, 58.44) * mm});
            skLineSegment(sketch, "E2056", {"start": v(37.21, 58.44) * mm, "end": v(37.22, 58.54) * mm});
            skLineSegment(sketch, "E2057", {"start": v(37.22, 58.54) * mm, "end": v(37.15, 58.62) * mm});
            skLineSegment(sketch, "E2058", {"start": v(37.15, 58.62) * mm, "end": v(36.92, 58.77) * mm});
            skLineSegment(sketch, "E2059", {"start": v(36.92, 58.77) * mm, "end": v(36.82, 58.8) * mm});
            skLineSegment(sketch, "E2060", {"start": v(36.82, 58.8) * mm, "end": v(36.73, 58.75) * mm});
            skLineSegment(sketch, "E2061", {"start": v(36.73, 58.75) * mm, "end": v(36.66, 58.68) * mm});
            skLineSegment(sketch, "E2062", {"start": v(36.66, 58.68) * mm, "end": v(36.58, 58.61) * mm});
            skLineSegment(sketch, "E2063", {"start": v(36.58, 58.61) * mm, "end": v(36.5, 58.56) * mm});
            skLineSegment(sketch, "E2064", {"start": v(36.5, 58.56) * mm, "end": v(36.4, 58.51) * mm});
            skLineSegment(sketch, "E2065", {"start": v(36.4, 58.51) * mm, "end": v(36.27, 58.49) * mm});
            skLineSegment(sketch, "E2066", {"start": v(36.27, 58.49) * mm, "end": v(36.14, 58.49) * mm});
            skLineSegment(sketch, "E2067", {"start": v(36.14, 58.49) * mm, "end": v(36.02, 58.52) * mm});
            skLineSegment(sketch, "E2068", {"start": v(36.02, 58.52) * mm, "end": v(35.9, 58.58) * mm});
            skLineSegment(sketch, "E2069", {"start": v(35.9, 58.58) * mm, "end": v(35.8, 58.66) * mm});
            skLineSegment(sketch, "E2070", {"start": v(35.8, 58.66) * mm, "end": v(35.7, 58.76) * mm});
            skLineSegment(sketch, "E2071", {"start": v(35.7, 58.76) * mm, "end": v(35.64, 58.87) * mm});
            skLineSegment(sketch, "E2072", {"start": v(35.64, 58.87) * mm, "end": v(35.6, 59) * mm});
            skLineSegment(sketch, "E2073", {"start": v(35.6, 59) * mm, "end": v(35.6, 59.1) * mm});
            skLineSegment(sketch, "E2074", {"start": v(35.6, 59.1) * mm, "end": v(35.62, 59.2) * mm});
            skLineSegment(sketch, "E2075", {"start": v(35.62, 59.2) * mm, "end": v(35.64, 59.3) * mm});
            skLineSegment(sketch, "E2076", {"start": v(35.64, 59.3) * mm, "end": v(35.67, 59.4) * mm});
            skLineSegment(sketch, "E2077", {"start": v(35.67, 59.4) * mm, "end": v(35.67, 59.5) * mm});
            skLineSegment(sketch, "E2078", {"start": v(35.67, 59.5) * mm, "end": v(35.6, 59.58) * mm});
            skLineSegment(sketch, "E2079", {"start": v(35.6, 59.58) * mm, "end": v(35.37, 59.72) * mm});
            skLineSegment(sketch, "E2080", {"start": v(35.37, 59.72) * mm, "end": v(35.26, 59.74) * mm});
            skLineSegment(sketch, "E2081", {"start": v(35.26, 59.74) * mm, "end": v(35.18, 59.7) * mm});
            skLineSegment(sketch, "E2082", {"start": v(35.18, 59.7) * mm, "end": v(35.1, 59.62) * mm});
            skLineSegment(sketch, "E2083", {"start": v(35.1, 59.62) * mm, "end": v(35.03, 59.55) * mm});
            skLineSegment(sketch, "E2084", {"start": v(35.03, 59.55) * mm, "end": v(34.95, 59.5) * mm});
            skLineSegment(sketch, "E2085", {"start": v(34.95, 59.5) * mm, "end": v(34.86, 59.44) * mm});
            skLineSegment(sketch, "E2086", {"start": v(34.86, 59.44) * mm, "end": v(34.73, 59.41) * mm});
            skLineSegment(sketch, "E2087", {"start": v(34.73, 59.41) * mm, "end": v(34.6, 59.42) * mm});
            skLineSegment(sketch, "E2088", {"start": v(34.6, 59.42) * mm, "end": v(34.47, 59.44) * mm});
            skLineSegment(sketch, "E2089", {"start": v(34.47, 59.44) * mm, "end": v(34.35, 59.5) * mm});
            skLineSegment(sketch, "E2090", {"start": v(34.35, 59.5) * mm, "end": v(34.24, 59.58) * mm});
            skLineSegment(sketch, "E2091", {"start": v(34.24, 59.58) * mm, "end": v(34.16, 59.67) * mm});
            skLineSegment(sketch, "E2092", {"start": v(34.16, 59.67) * mm, "end": v(34.09, 59.78) * mm});
            skLineSegment(sketch, "E2093", {"start": v(34.09, 59.78) * mm, "end": v(34.05, 59.9) * mm});
            skLineSegment(sketch, "E2094", {"start": v(34.05, 59.9) * mm, "end": v(34.05, 60.01) * mm});
            skLineSegment(sketch, "E2095", {"start": v(34.05, 60.01) * mm, "end": v(34.05, 60.11) * mm});
            skLineSegment(sketch, "E2096", {"start": v(34.05, 60.11) * mm, "end": v(34.07, 60.21) * mm});
            skLineSegment(sketch, "E2097", {"start": v(34.07, 60.21) * mm, "end": v(34.1, 60.3) * mm});
            skLineSegment(sketch, "E2098", {"start": v(34.1, 60.3) * mm, "end": v(34.1, 60.4) * mm});
            skLineSegment(sketch, "E2099", {"start": v(34.1, 60.4) * mm, "end": v(34.03, 60.49) * mm});
            skLineSegment(sketch, "E2100", {"start": v(34.03, 60.49) * mm, "end": v(33.8, 60.62) * mm});
            skLineSegment(sketch, "E2101", {"start": v(33.8, 60.62) * mm, "end": v(33.69, 60.64) * mm});
            skLineSegment(sketch, "E2102", {"start": v(33.69, 60.64) * mm, "end": v(33.6, 60.6) * mm});
            skLineSegment(sketch, "E2103", {"start": v(33.6, 60.6) * mm, "end": v(33.54, 60.51) * mm});
            skLineSegment(sketch, "E2104", {"start": v(33.54, 60.51) * mm, "end": v(33.46, 60.45) * mm});
            skLineSegment(sketch, "E2105", {"start": v(33.46, 60.45) * mm, "end": v(33.38, 60.39) * mm});
            skLineSegment(sketch, "E2106", {"start": v(33.38, 60.39) * mm, "end": v(33.3, 60.34) * mm});
            skLineSegment(sketch, "E2107", {"start": v(33.3, 60.34) * mm, "end": v(33.16, 60.3) * mm});
            skLineSegment(sketch, "E2108", {"start": v(33.16, 60.3) * mm, "end": v(33.03, 60.3) * mm});
            skLineSegment(sketch, "E2109", {"start": v(33.03, 60.3) * mm, "end": v(32.9, 60.33) * mm});
            skLineSegment(sketch, "E2110", {"start": v(32.9, 60.33) * mm, "end": v(32.78, 60.38) * mm});
            skLineSegment(sketch, "E2111", {"start": v(32.78, 60.38) * mm, "end": v(32.67, 60.45) * mm});
            skLineSegment(sketch, "E2112", {"start": v(32.67, 60.45) * mm, "end": v(32.58, 60.55) * mm});
            skLineSegment(sketch, "E2113", {"start": v(32.58, 60.55) * mm, "end": v(32.51, 60.66) * mm});
            skLineSegment(sketch, "E2114", {"start": v(32.51, 60.66) * mm, "end": v(32.47, 60.78) * mm});
            skLineSegment(sketch, "E2115", {"start": v(32.47, 60.78) * mm, "end": v(32.46, 60.88) * mm});
            skLineSegment(sketch, "E2116", {"start": v(32.46, 60.88) * mm, "end": v(32.47, 60.99) * mm});
            skLineSegment(sketch, "E2117", {"start": v(32.47, 60.99) * mm, "end": v(32.49, 61.08) * mm});
            skLineSegment(sketch, "E2118", {"start": v(32.49, 61.08) * mm, "end": v(32.51, 61.18) * mm});
            skLineSegment(sketch, "E2119", {"start": v(32.51, 61.18) * mm, "end": v(32.51, 61.28) * mm});
            skLineSegment(sketch, "E2120", {"start": v(32.51, 61.28) * mm, "end": v(32.44, 61.36) * mm});
            skLineSegment(sketch, "E2121", {"start": v(32.44, 61.36) * mm, "end": v(32.2, 61.49) * mm});
            skLineSegment(sketch, "E2122", {"start": v(32.2, 61.49) * mm, "end": v(32.09, 61.5) * mm});
            skLineSegment(sketch, "E2123", {"start": v(32.09, 61.5) * mm, "end": v(32, 61.45) * mm});
            skLineSegment(sketch, "E2124", {"start": v(32, 61.45) * mm, "end": v(31.94, 61.37) * mm});
            skLineSegment(sketch, "E2125", {"start": v(31.94, 61.37) * mm, "end": v(31.87, 61.3) * mm});
            skLineSegment(sketch, "E2126", {"start": v(31.87, 61.3) * mm, "end": v(31.79, 61.24) * mm});
            skLineSegment(sketch, "E2127", {"start": v(31.79, 61.24) * mm, "end": v(31.7, 61.19) * mm});
            skLineSegment(sketch, "E2128", {"start": v(31.7, 61.19) * mm, "end": v(31.57, 61.15) * mm});
            skLineSegment(sketch, "E2129", {"start": v(31.57, 61.15) * mm, "end": v(31.44, 61.15) * mm});
            skLineSegment(sketch, "E2130", {"start": v(31.44, 61.15) * mm, "end": v(31.31, 61.17) * mm});
            skLineSegment(sketch, "E2131", {"start": v(31.31, 61.17) * mm, "end": v(31.2, 61.22) * mm});
            skLineSegment(sketch, "E2132", {"start": v(31.2, 61.22) * mm, "end": v(31.08, 61.29) * mm});
            skLineSegment(sketch, "E2133", {"start": v(31.08, 61.29) * mm, "end": v(30.99, 61.38) * mm});
            skLineSegment(sketch, "E2134", {"start": v(30.99, 61.38) * mm, "end": v(30.91, 61.49) * mm});
            skLineSegment(sketch, "E2135", {"start": v(30.91, 61.49) * mm, "end": v(30.87, 61.6) * mm});
            skLineSegment(sketch, "E2136", {"start": v(30.87, 61.6) * mm, "end": v(30.86, 61.71) * mm});
            skLineSegment(sketch, "E2137", {"start": v(30.86, 61.71) * mm, "end": v(30.86, 61.81) * mm});
            skLineSegment(sketch, "E2138", {"start": v(30.86, 61.81) * mm, "end": v(30.88, 61.91) * mm});
            skLineSegment(sketch, "E2139", {"start": v(30.88, 61.91) * mm, "end": v(30.9, 62.01) * mm});
            skLineSegment(sketch, "E2140", {"start": v(30.9, 62.01) * mm, "end": v(30.9, 62.11) * mm});
            skLineSegment(sketch, "E2141", {"start": v(30.9, 62.11) * mm, "end": v(30.82, 62.19) * mm});
            skLineSegment(sketch, "E2142", {"start": v(30.82, 62.19) * mm, "end": v(30.57, 62.3) * mm});
            skLineSegment(sketch, "E2143", {"start": v(30.57, 62.3) * mm, "end": v(30.47, 62.32) * mm});
            skLineSegment(sketch, "E2144", {"start": v(30.47, 62.32) * mm, "end": v(30.38, 62.27) * mm});
            skLineSegment(sketch, "E2145", {"start": v(30.38, 62.27) * mm, "end": v(30.32, 62.19) * mm});
            skLineSegment(sketch, "E2146", {"start": v(30.32, 62.19) * mm, "end": v(30.25, 62.11) * mm});
            skLineSegment(sketch, "E2147", {"start": v(30.25, 62.11) * mm, "end": v(30.17, 62.05) * mm});
            skLineSegment(sketch, "E2148", {"start": v(30.17, 62.05) * mm, "end": v(30.09, 62) * mm});
            skLineSegment(sketch, "E2149", {"start": v(30.09, 62) * mm, "end": v(29.96, 61.96) * mm});
            skLineSegment(sketch, "E2150", {"start": v(29.96, 61.96) * mm, "end": v(29.83, 61.95) * mm});
            skLineSegment(sketch, "E2151", {"start": v(29.83, 61.95) * mm, "end": v(29.7, 61.97) * mm});
            skLineSegment(sketch, "E2152", {"start": v(29.7, 61.97) * mm, "end": v(29.58, 62.01) * mm});
            skLineSegment(sketch, "E2153", {"start": v(29.58, 62.01) * mm, "end": v(29.46, 62.08) * mm});
            skLineSegment(sketch, "E2154", {"start": v(29.46, 62.08) * mm, "end": v(29.37, 62.17) * mm});
            skLineSegment(sketch, "E2155", {"start": v(29.37, 62.17) * mm, "end": v(29.3, 62.28) * mm});
            skLineSegment(sketch, "E2156", {"start": v(29.3, 62.28) * mm, "end": v(29.24, 62.4) * mm});
            skLineSegment(sketch, "E2157", {"start": v(29.24, 62.4) * mm, "end": v(29.23, 62.5) * mm});
            skLineSegment(sketch, "E2158", {"start": v(29.23, 62.5) * mm, "end": v(29.23, 62.6) * mm});
            skLineSegment(sketch, "E2159", {"start": v(29.23, 62.6) * mm, "end": v(29.24, 62.7) * mm});
            skLineSegment(sketch, "E2160", {"start": v(29.24, 62.7) * mm, "end": v(29.27, 62.8) * mm});
            skLineSegment(sketch, "E2161", {"start": v(29.27, 62.8) * mm, "end": v(29.26, 62.9) * mm});
            skLineSegment(sketch, "E2162", {"start": v(29.26, 62.9) * mm, "end": v(29.18, 62.97) * mm});
            skLineSegment(sketch, "E2163", {"start": v(29.18, 62.97) * mm, "end": v(28.93, 63.09) * mm});
            skLineSegment(sketch, "E2164", {"start": v(28.93, 63.09) * mm, "end": v(28.83, 63.1) * mm});
            skLineSegment(sketch, "E2165", {"start": v(28.83, 63.1) * mm, "end": v(28.74, 63.04) * mm});
            skLineSegment(sketch, "E2166", {"start": v(28.74, 63.04) * mm, "end": v(28.69, 62.96) * mm});
            skLineSegment(sketch, "E2167", {"start": v(28.69, 62.96) * mm, "end": v(28.62, 62.88) * mm});
            skLineSegment(sketch, "E2168", {"start": v(28.62, 62.88) * mm, "end": v(28.54, 62.82) * mm});
            skLineSegment(sketch, "E2169", {"start": v(28.54, 62.82) * mm, "end": v(28.45, 62.76) * mm});
            skLineSegment(sketch, "E2170", {"start": v(28.45, 62.76) * mm, "end": v(28.33, 62.72) * mm});
            skLineSegment(sketch, "E2171", {"start": v(28.33, 62.72) * mm, "end": v(28.2, 62.7) * mm});
            skLineSegment(sketch, "E2172", {"start": v(28.2, 62.7) * mm, "end": v(28.07, 62.72) * mm});
            skLineSegment(sketch, "E2173", {"start": v(28.07, 62.72) * mm, "end": v(27.94, 62.76) * mm});
            skLineSegment(sketch, "E2174", {"start": v(27.94, 62.76) * mm, "end": v(27.83, 62.83) * mm});
            skLineSegment(sketch, "E2175", {"start": v(27.83, 62.83) * mm, "end": v(27.73, 62.92) * mm});
            skLineSegment(sketch, "E2176", {"start": v(27.73, 62.92) * mm, "end": v(27.65, 63.02) * mm});
            skLineSegment(sketch, "E2177", {"start": v(27.65, 63.02) * mm, "end": v(27.6, 63.14) * mm});
            skLineSegment(sketch, "E2178", {"start": v(27.6, 63.14) * mm, "end": v(27.59, 63.24) * mm});
            skLineSegment(sketch, "E2179", {"start": v(27.59, 63.24) * mm, "end": v(27.58, 63.34) * mm});
            skLineSegment(sketch, "E2180", {"start": v(27.58, 63.34) * mm, "end": v(27.6, 63.45) * mm});
            skLineSegment(sketch, "E2181", {"start": v(27.6, 63.45) * mm, "end": v(27.61, 63.54) * mm});
            skLineSegment(sketch, "E2182", {"start": v(27.61, 63.54) * mm, "end": v(27.6, 63.64) * mm});
            skLineSegment(sketch, "E2183", {"start": v(27.6, 63.64) * mm, "end": v(27.52, 63.71) * mm});
            skLineSegment(sketch, "E2184", {"start": v(27.52, 63.71) * mm, "end": v(27.27, 63.82) * mm});
            skLineSegment(sketch, "E2185", {"start": v(27.27, 63.82) * mm, "end": v(27.16, 63.83) * mm});
            skLineSegment(sketch, "E2186", {"start": v(27.16, 63.83) * mm, "end": v(27.08, 63.77) * mm});
            skLineSegment(sketch, "E2187", {"start": v(27.08, 63.77) * mm, "end": v(27.03, 63.69) * mm});
            skLineSegment(sketch, "E2188", {"start": v(27.03, 63.69) * mm, "end": v(26.96, 63.61) * mm});
            skLineSegment(sketch, "E2189", {"start": v(26.96, 63.61) * mm, "end": v(26.89, 63.54) * mm});
            skLineSegment(sketch, "E2190", {"start": v(26.89, 63.54) * mm, "end": v(26.8, 63.48) * mm});
            skLineSegment(sketch, "E2191", {"start": v(26.8, 63.48) * mm, "end": v(26.68, 63.44) * mm});
            skLineSegment(sketch, "E2192", {"start": v(26.68, 63.44) * mm, "end": v(26.55, 63.42) * mm});
            skLineSegment(sketch, "E2193", {"start": v(26.55, 63.42) * mm, "end": v(26.42, 63.44) * mm});
            skLineSegment(sketch, "E2194", {"start": v(26.42, 63.44) * mm, "end": v(26.3, 63.47) * mm});
            skLineSegment(sketch, "E2195", {"start": v(26.3, 63.47) * mm, "end": v(26.18, 63.54) * mm});
            skLineSegment(sketch, "E2196", {"start": v(26.18, 63.54) * mm, "end": v(26.07, 63.62) * mm});
            skLineSegment(sketch, "E2197", {"start": v(26.07, 63.62) * mm, "end": v(26, 63.72) * mm});
            skLineSegment(sketch, "E2198", {"start": v(26, 63.72) * mm, "end": v(25.94, 63.84) * mm});
            skLineSegment(sketch, "E2199", {"start": v(25.94, 63.84) * mm, "end": v(25.92, 63.94) * mm});
            skLineSegment(sketch, "E2200", {"start": v(25.92, 63.94) * mm, "end": v(25.92, 64.05) * mm});
            skLineSegment(sketch, "E2201", {"start": v(25.92, 64.05) * mm, "end": v(25.92, 64.15) * mm});
            skLineSegment(sketch, "E2202", {"start": v(25.92, 64.15) * mm, "end": v(25.94, 64.24) * mm});
            skLineSegment(sketch, "E2203", {"start": v(25.94, 64.24) * mm, "end": v(25.93, 64.34) * mm});
            skLineSegment(sketch, "E2204", {"start": v(25.93, 64.34) * mm, "end": v(25.85, 64.41) * mm});
            skLineSegment(sketch, "E2205", {"start": v(25.85, 64.41) * mm, "end": v(25.6, 64.51) * mm});
            skLineSegment(sketch, "E2206", {"start": v(25.6, 64.51) * mm, "end": v(25.48, 64.52) * mm});
            skLineSegment(sketch, "E2207", {"start": v(25.48, 64.52) * mm, "end": v(25.4, 64.46) * mm});
            skLineSegment(sketch, "E2208", {"start": v(25.4, 64.46) * mm, "end": v(25.35, 64.37) * mm});
            skLineSegment(sketch, "E2209", {"start": v(25.35, 64.37) * mm, "end": v(25.29, 64.3) * mm});
            skLineSegment(sketch, "E2210", {"start": v(25.29, 64.3) * mm, "end": v(25.21, 64.23) * mm});
            skLineSegment(sketch, "E2211", {"start": v(25.21, 64.23) * mm, "end": v(25.13, 64.16) * mm});
            skLineSegment(sketch, "E2212", {"start": v(25.13, 64.16) * mm, "end": v(25, 64.12) * mm});
            skLineSegment(sketch, "E2213", {"start": v(25, 64.12) * mm, "end": v(24.88, 64.1) * mm});
            skLineSegment(sketch, "E2214", {"start": v(24.88, 64.1) * mm, "end": v(24.75, 64.1) * mm});
            skLineSegment(sketch, "E2215", {"start": v(24.75, 64.1) * mm, "end": v(24.62, 64.14) * mm});
            skLineSegment(sketch, "E2216", {"start": v(24.62, 64.14) * mm, "end": v(24.5, 64.2) * mm});
            skLineSegment(sketch, "E2217", {"start": v(24.5, 64.2) * mm, "end": v(24.4, 64.28) * mm});
            skLineSegment(sketch, "E2218", {"start": v(24.4, 64.28) * mm, "end": v(24.32, 64.38) * mm});
            skLineSegment(sketch, "E2219", {"start": v(24.32, 64.38) * mm, "end": v(24.26, 64.5) * mm});
            skLineSegment(sketch, "E2220", {"start": v(24.26, 64.5) * mm, "end": v(24.24, 64.6) * mm});
            skLineSegment(sketch, "E2221", {"start": v(24.24, 64.6) * mm, "end": v(24.23, 64.7) * mm});
            skLineSegment(sketch, "E2222", {"start": v(24.23, 64.7) * mm, "end": v(24.23, 64.8) * mm});
            skLineSegment(sketch, "E2223", {"start": v(24.23, 64.8) * mm, "end": v(24.25, 64.9) * mm});
            skLineSegment(sketch, "E2224", {"start": v(24.25, 64.9) * mm, "end": v(24.23, 65) * mm});
            skLineSegment(sketch, "E2225", {"start": v(24.23, 65) * mm, "end": v(24.15, 65.07) * mm});
            skLineSegment(sketch, "E2226", {"start": v(24.15, 65.07) * mm, "end": v(23.9, 65.16) * mm});
            skLineSegment(sketch, "E2227", {"start": v(23.9, 65.16) * mm, "end": v(23.79, 65.16) * mm});
            skLineSegment(sketch, "E2228", {"start": v(23.79, 65.16) * mm, "end": v(23.7, 65.1) * mm});
            skLineSegment(sketch, "E2229", {"start": v(23.7, 65.1) * mm, "end": v(23.66, 65.02) * mm});
            skLineSegment(sketch, "E2230", {"start": v(23.66, 65.02) * mm, "end": v(23.6, 64.94) * mm});
            skLineSegment(sketch, "E2231", {"start": v(23.6, 64.94) * mm, "end": v(23.52, 64.86) * mm});
            skLineSegment(sketch, "E2232", {"start": v(23.52, 64.86) * mm, "end": v(23.44, 64.8) * mm});
            skLineSegment(sketch, "E2233", {"start": v(23.44, 64.8) * mm, "end": v(23.32, 64.75) * mm});
            skLineSegment(sketch, "E2234", {"start": v(23.32, 64.75) * mm, "end": v(23.2, 64.73) * mm});
            skLineSegment(sketch, "E2235", {"start": v(23.2, 64.73) * mm, "end": v(23.06, 64.73) * mm});
            skLineSegment(sketch, "E2236", {"start": v(23.06, 64.73) * mm, "end": v(22.93, 64.76) * mm});
            skLineSegment(sketch, "E2237", {"start": v(22.93, 64.76) * mm, "end": v(22.81, 64.82) * mm});
            skLineSegment(sketch, "E2238", {"start": v(22.81, 64.82) * mm, "end": v(22.7, 64.9) * mm});
            skLineSegment(sketch, "E2239", {"start": v(22.7, 64.9) * mm, "end": v(22.62, 65) * mm});
            skLineSegment(sketch, "E2240", {"start": v(22.62, 65) * mm, "end": v(22.56, 65.11) * mm});
            skLineSegment(sketch, "E2241", {"start": v(22.56, 65.11) * mm, "end": v(22.54, 65.21) * mm});
            skLineSegment(sketch, "E2242", {"start": v(22.54, 65.21) * mm, "end": v(22.53, 65.31) * mm});
            skLineSegment(sketch, "E2243", {"start": v(22.53, 65.31) * mm, "end": v(22.53, 65.41) * mm});
            skLineSegment(sketch, "E2244", {"start": v(22.53, 65.41) * mm, "end": v(22.54, 65.51) * mm});
            skLineSegment(sketch, "E2245", {"start": v(22.54, 65.51) * mm, "end": v(22.52, 65.61) * mm});
            skLineSegment(sketch, "E2246", {"start": v(22.52, 65.61) * mm, "end": v(22.44, 65.68) * mm});
            skLineSegment(sketch, "E2247", {"start": v(22.44, 65.68) * mm, "end": v(22.18, 65.77) * mm});
            skLineSegment(sketch, "E2248", {"start": v(22.18, 65.77) * mm, "end": v(22.07, 65.76) * mm});
            skLineSegment(sketch, "E2249", {"start": v(22.07, 65.76) * mm, "end": v(22, 65.7) * mm});
            skLineSegment(sketch, "E2250", {"start": v(22, 65.7) * mm, "end": v(21.95, 65.61) * mm});
            skLineSegment(sketch, "E2251", {"start": v(21.95, 65.61) * mm, "end": v(21.89, 65.53) * mm});
            skLineSegment(sketch, "E2252", {"start": v(21.89, 65.53) * mm, "end": v(21.82, 65.46) * mm});
            skLineSegment(sketch, "E2253", {"start": v(21.82, 65.46) * mm, "end": v(21.74, 65.4) * mm});
            skLineSegment(sketch, "E2254", {"start": v(21.74, 65.4) * mm, "end": v(21.62, 65.34) * mm});
            skLineSegment(sketch, "E2255", {"start": v(21.62, 65.34) * mm, "end": v(21.5, 65.31) * mm});
            skLineSegment(sketch, "E2256", {"start": v(21.5, 65.31) * mm, "end": v(21.36, 65.31) * mm});
            skLineSegment(sketch, "E2257", {"start": v(21.36, 65.31) * mm, "end": v(21.23, 65.34) * mm});
            skLineSegment(sketch, "E2258", {"start": v(21.23, 65.34) * mm, "end": v(21.1, 65.4) * mm});
            skLineSegment(sketch, "E2259", {"start": v(21.1, 65.4) * mm, "end": v(21, 65.47) * mm});
            skLineSegment(sketch, "E2260", {"start": v(21, 65.47) * mm, "end": v(20.91, 65.57) * mm});
            skLineSegment(sketch, "E2261", {"start": v(20.91, 65.57) * mm, "end": v(20.85, 65.68) * mm});
            skLineSegment(sketch, "E2262", {"start": v(20.85, 65.68) * mm, "end": v(20.82, 65.78) * mm});
            skLineSegment(sketch, "E2263", {"start": v(20.82, 65.78) * mm, "end": v(20.81, 65.88) * mm});
            skLineSegment(sketch, "E2264", {"start": v(20.81, 65.88) * mm, "end": v(20.81, 65.98) * mm});
            skLineSegment(sketch, "E2265", {"start": v(20.81, 65.98) * mm, "end": v(20.82, 66.08) * mm});
            skLineSegment(sketch, "E2266", {"start": v(20.82, 66.08) * mm, "end": v(20.8, 66.18) * mm});
            skLineSegment(sketch, "E2267", {"start": v(20.8, 66.18) * mm, "end": v(20.71, 66.24) * mm});
            skLineSegment(sketch, "E2268", {"start": v(20.71, 66.24) * mm, "end": v(20.45, 66.32) * mm});
            skLineSegment(sketch, "E2269", {"start": v(20.45, 66.32) * mm, "end": v(20.34, 66.32) * mm});
            skLineSegment(sketch, "E2270", {"start": v(20.34, 66.32) * mm, "end": v(20.27, 66.25) * mm});
            skLineSegment(sketch, "E2271", {"start": v(20.27, 66.25) * mm, "end": v(20.22, 66.16) * mm});
            skLineSegment(sketch, "E2272", {"start": v(20.22, 66.16) * mm, "end": v(20.16, 66.08) * mm});
            skLineSegment(sketch, "E2273", {"start": v(20.16, 66.08) * mm, "end": v(20.1, 66) * mm});
            skLineSegment(sketch, "E2274", {"start": v(20.1, 66) * mm, "end": v(20.02, 65.94) * mm});
            skLineSegment(sketch, "E2275", {"start": v(20.02, 65.94) * mm, "end": v(19.9, 65.88) * mm});
            skLineSegment(sketch, "E2276", {"start": v(19.9, 65.88) * mm, "end": v(19.77, 65.85) * mm});
            skLineSegment(sketch, "E2277", {"start": v(19.77, 65.85) * mm, "end": v(19.64, 65.85) * mm});
            skLineSegment(sketch, "E2278", {"start": v(19.64, 65.85) * mm, "end": v(19.51, 65.87) * mm});
            skLineSegment(sketch, "E2279", {"start": v(19.51, 65.87) * mm, "end": v(19.4, 65.92) * mm});
            skLineSegment(sketch, "E2280", {"start": v(19.4, 65.92) * mm, "end": v(19.28, 66) * mm});
            skLineSegment(sketch, "E2281", {"start": v(19.28, 66) * mm, "end": v(19.2, 66.1) * mm});
            skLineSegment(sketch, "E2282", {"start": v(19.2, 66.1) * mm, "end": v(19.12, 66.2) * mm});
            skLineSegment(sketch, "E2283", {"start": v(19.12, 66.2) * mm, "end": v(19.1, 66.3) * mm});
            skLineSegment(sketch, "E2284", {"start": v(19.1, 66.3) * mm, "end": v(19.08, 66.4) * mm});
            skLineSegment(sketch, "E2285", {"start": v(19.08, 66.4) * mm, "end": v(19.08, 66.5) * mm});
            skLineSegment(sketch, "E2286", {"start": v(19.08, 66.5) * mm, "end": v(19.08, 66.6) * mm});
            skLineSegment(sketch, "E2287", {"start": v(19.08, 66.6) * mm, "end": v(19.06, 66.7) * mm});
            skLineSegment(sketch, "E2288", {"start": v(19.06, 66.7) * mm, "end": v(18.97, 66.76) * mm});
            skLineSegment(sketch, "E2289", {"start": v(18.97, 66.76) * mm, "end": v(18.7, 66.84) * mm});
            skLineSegment(sketch, "E2290", {"start": v(18.7, 66.84) * mm, "end": v(18.6, 66.83) * mm});
            skLineSegment(sketch, "E2291", {"start": v(18.6, 66.83) * mm, "end": v(18.53, 66.76) * mm});
            skLineSegment(sketch, "E2292", {"start": v(18.53, 66.76) * mm, "end": v(18.48, 66.67) * mm});
            skLineSegment(sketch, "E2293", {"start": v(18.48, 66.67) * mm, "end": v(18.43, 66.59) * mm});
            skLineSegment(sketch, "E2294", {"start": v(18.43, 66.59) * mm, "end": v(18.36, 66.51) * mm});
            skLineSegment(sketch, "E2295", {"start": v(18.36, 66.51) * mm, "end": v(18.29, 66.44) * mm});
            skLineSegment(sketch, "E2296", {"start": v(18.29, 66.44) * mm, "end": v(18.17, 66.38) * mm});
            skLineSegment(sketch, "E2297", {"start": v(18.17, 66.38) * mm, "end": v(18.04, 66.35) * mm});
            skLineSegment(sketch, "E2298", {"start": v(18.04, 66.35) * mm, "end": v(17.91, 66.34) * mm});
            skLineSegment(sketch, "E2299", {"start": v(17.91, 66.34) * mm, "end": v(17.78, 66.36) * mm});
            skLineSegment(sketch, "E2300", {"start": v(17.78, 66.36) * mm, "end": v(17.66, 66.4) * mm});
            skLineSegment(sketch, "E2301", {"start": v(17.66, 66.4) * mm, "end": v(17.55, 66.48) * mm});
            skLineSegment(sketch, "E2302", {"start": v(17.55, 66.48) * mm, "end": v(17.45, 66.57) * mm});
            skLineSegment(sketch, "E2303", {"start": v(17.45, 66.57) * mm, "end": v(17.38, 66.68) * mm});
            skLineSegment(sketch, "E2304", {"start": v(17.38, 66.68) * mm, "end": v(17.35, 66.78) * mm});
            skLineSegment(sketch, "E2305", {"start": v(17.35, 66.78) * mm, "end": v(17.33, 66.88) * mm});
            skLineSegment(sketch, "E2306", {"start": v(17.33, 66.88) * mm, "end": v(17.33, 66.98) * mm});
            skLineSegment(sketch, "E2307", {"start": v(17.33, 66.98) * mm, "end": v(17.33, 67.08) * mm});
            skLineSegment(sketch, "E2308", {"start": v(17.33, 67.08) * mm, "end": v(17.3, 67.18) * mm});
            skLineSegment(sketch, "E2309", {"start": v(17.3, 67.18) * mm, "end": v(17.22, 67.24) * mm});
            skLineSegment(sketch, "E2310", {"start": v(17.22, 67.24) * mm, "end": v(16.95, 67.3) * mm});
            skLineSegment(sketch, "E2311", {"start": v(16.95, 67.3) * mm, "end": v(16.84, 67.3) * mm});
            skLineSegment(sketch, "E2312", {"start": v(16.84, 67.3) * mm, "end": v(16.77, 67.22) * mm});
            skLineSegment(sketch, "E2313", {"start": v(16.77, 67.22) * mm, "end": v(16.73, 67.13) * mm});
            skLineSegment(sketch, "E2314", {"start": v(16.73, 67.13) * mm, "end": v(16.68, 67.05) * mm});
            skLineSegment(sketch, "E2315", {"start": v(16.68, 67.05) * mm, "end": v(16.61, 66.97) * mm});
            skLineSegment(sketch, "E2316", {"start": v(16.61, 66.97) * mm, "end": v(16.54, 66.9) * mm});
            skLineSegment(sketch, "E2317", {"start": v(16.54, 66.9) * mm, "end": v(16.43, 66.83) * mm});
            skLineSegment(sketch, "E2318", {"start": v(16.43, 66.83) * mm, "end": v(16.3, 66.8) * mm});
            skLineSegment(sketch, "E2319", {"start": v(16.3, 66.8) * mm, "end": v(16.17, 66.79) * mm});
            skLineSegment(sketch, "E2320", {"start": v(16.17, 66.79) * mm, "end": v(16.04, 66.8) * mm});
            skLineSegment(sketch, "E2321", {"start": v(16.04, 66.8) * mm, "end": v(15.91, 66.85) * mm});
            skLineSegment(sketch, "E2322", {"start": v(15.91, 66.85) * mm, "end": v(15.8, 66.92) * mm});
            skLineSegment(sketch, "E2323", {"start": v(15.8, 66.92) * mm, "end": v(15.7, 67) * mm});
            skLineSegment(sketch, "E2324", {"start": v(15.7, 67) * mm, "end": v(15.63, 67.11) * mm});
            skLineSegment(sketch, "E2325", {"start": v(15.63, 67.11) * mm, "end": v(15.6, 67.21) * mm});
            skLineSegment(sketch, "E2326", {"start": v(15.6, 67.21) * mm, "end": v(15.58, 67.31) * mm});
            skLineSegment(sketch, "E2327", {"start": v(15.58, 67.31) * mm, "end": v(15.57, 67.41) * mm});
            skLineSegment(sketch, "E2328", {"start": v(15.57, 67.41) * mm, "end": v(15.57, 67.51) * mm});
            skLineSegment(sketch, "E2329", {"start": v(15.57, 67.51) * mm, "end": v(15.54, 67.6) * mm});
            skLineSegment(sketch, "E2330", {"start": v(15.54, 67.6) * mm, "end": v(15.45, 67.66) * mm});
            skLineSegment(sketch, "E2331", {"start": v(15.45, 67.66) * mm, "end": v(15.18, 67.72) * mm});
            skLineSegment(sketch, "E2332", {"start": v(15.18, 67.72) * mm, "end": v(15.08, 67.71) * mm});
            skLineSegment(sketch, "E2333", {"start": v(15.08, 67.71) * mm, "end": v(15, 67.64) * mm});
            skLineSegment(sketch, "E2334", {"start": v(15, 67.64) * mm, "end": v(14.97, 67.55) * mm});
            skLineSegment(sketch, "E2335", {"start": v(14.97, 67.55) * mm, "end": v(14.92, 67.46) * mm});
            skLineSegment(sketch, "E2336", {"start": v(14.92, 67.46) * mm, "end": v(14.86, 67.38) * mm});
            skLineSegment(sketch, "E2337", {"start": v(14.86, 67.38) * mm, "end": v(14.78, 67.3) * mm});
            skLineSegment(sketch, "E2338", {"start": v(14.78, 67.3) * mm, "end": v(14.67, 67.24) * mm});
            skLineSegment(sketch, "E2339", {"start": v(14.67, 67.24) * mm, "end": v(14.55, 67.2) * mm});
            skLineSegment(sketch, "E2340", {"start": v(14.55, 67.2) * mm, "end": v(14.42, 67.19) * mm});
            skLineSegment(sketch, "E2341", {"start": v(14.42, 67.19) * mm, "end": v(14.28, 67.2) * mm});
            skLineSegment(sketch, "E2342", {"start": v(14.28, 67.2) * mm, "end": v(14.16, 67.24) * mm});
            skLineSegment(sketch, "E2343", {"start": v(14.16, 67.24) * mm, "end": v(14.04, 67.3) * mm});
            skLineSegment(sketch, "E2344", {"start": v(14.04, 67.3) * mm, "end": v(13.95, 67.4) * mm});
            skLineSegment(sketch, "E2345", {"start": v(13.95, 67.4) * mm, "end": v(13.87, 67.5) * mm});
            skLineSegment(sketch, "E2346", {"start": v(13.87, 67.5) * mm, "end": v(13.83, 67.6) * mm});
            skLineSegment(sketch, "E2347", {"start": v(13.83, 67.6) * mm, "end": v(13.81, 67.7) * mm});
            skLineSegment(sketch, "E2348", {"start": v(13.81, 67.7) * mm, "end": v(13.8, 67.8) * mm});
            skLineSegment(sketch, "E2349", {"start": v(13.8, 67.8) * mm, "end": v(13.8, 67.9) * mm});
            skLineSegment(sketch, "E2350", {"start": v(13.8, 67.9) * mm, "end": v(13.77, 68) * mm});
            skLineSegment(sketch, "E2351", {"start": v(13.77, 68) * mm, "end": v(13.67, 68.04) * mm});
            skLineSegment(sketch, "E2352", {"start": v(13.67, 68.04) * mm, "end": v(13.4, 68.1) * mm});
            skLineSegment(sketch, "E2353", {"start": v(13.4, 68.1) * mm, "end": v(13.3, 68.08) * mm});
            skLineSegment(sketch, "E2354", {"start": v(13.3, 68.08) * mm, "end": v(13.23, 68) * mm});
            skLineSegment(sketch, "E2355", {"start": v(13.23, 68) * mm, "end": v(13.2, 67.92) * mm});
            skLineSegment(sketch, "E2356", {"start": v(13.2, 67.92) * mm, "end": v(13.15, 67.83) * mm});
            skLineSegment(sketch, "E2357", {"start": v(13.15, 67.83) * mm, "end": v(13.09, 67.75) * mm});
            skLineSegment(sketch, "E2358", {"start": v(13.09, 67.75) * mm, "end": v(13.02, 67.67) * mm});
            skLineSegment(sketch, "E2359", {"start": v(13.02, 67.67) * mm, "end": v(12.9, 67.6) * mm});
            skLineSegment(sketch, "E2360", {"start": v(12.9, 67.6) * mm, "end": v(12.78, 67.56) * mm});
            skLineSegment(sketch, "E2361", {"start": v(12.78, 67.56) * mm, "end": v(12.65, 67.54) * mm});
            skLineSegment(sketch, "E2362", {"start": v(12.65, 67.54) * mm, "end": v(12.52, 67.55) * mm});
            skLineSegment(sketch, "E2363", {"start": v(12.52, 67.55) * mm, "end": v(12.4, 67.6) * mm});
            skLineSegment(sketch, "E2364", {"start": v(12.4, 67.6) * mm, "end": v(12.28, 67.65) * mm});
            skLineSegment(sketch, "E2365", {"start": v(12.28, 67.65) * mm, "end": v(12.18, 67.74) * mm});
            skLineSegment(sketch, "E2366", {"start": v(12.18, 67.74) * mm, "end": v(12.1, 67.84) * mm});
            skLineSegment(sketch, "E2367", {"start": v(12.1, 67.84) * mm, "end": v(12.06, 67.94) * mm});
            skLineSegment(sketch, "E2368", {"start": v(12.06, 67.94) * mm, "end": v(12.03, 68.03) * mm});
            skLineSegment(sketch, "E2369", {"start": v(12.03, 68.03) * mm, "end": v(12.02, 68.13) * mm});
            skLineSegment(sketch, "E2370", {"start": v(12.02, 68.13) * mm, "end": v(12.02, 68.23) * mm});
            skLineSegment(sketch, "E2371", {"start": v(12.02, 68.23) * mm, "end": v(11.98, 68.33) * mm});
            skLineSegment(sketch, "E2372", {"start": v(11.98, 68.33) * mm, "end": v(11.89, 68.38) * mm});
            skLineSegment(sketch, "E2373", {"start": v(11.89, 68.38) * mm, "end": v(11.62, 68.43) * mm});
            skLineSegment(sketch, "E2374", {"start": v(11.62, 68.43) * mm, "end": v(11.51, 68.4) * mm});
            skLineSegment(sketch, "E2375", {"start": v(11.51, 68.4) * mm, "end": v(11.45, 68.33) * mm});
            skLineSegment(sketch, "E2376", {"start": v(11.45, 68.33) * mm, "end": v(11.41, 68.24) * mm});
            skLineSegment(sketch, "E2377", {"start": v(11.41, 68.24) * mm, "end": v(11.37, 68.15) * mm});
            skLineSegment(sketch, "E2378", {"start": v(11.37, 68.15) * mm, "end": v(11.3, 68.07) * mm});
            skLineSegment(sketch, "E2379", {"start": v(11.3, 68.07) * mm, "end": v(11.24, 67.99) * mm});
            skLineSegment(sketch, "E2380", {"start": v(11.24, 67.99) * mm, "end": v(11.13, 67.91) * mm});
            skLineSegment(sketch, "E2381", {"start": v(11.13, 67.91) * mm, "end": v(11, 67.87) * mm});
            skLineSegment(sketch, "E2382", {"start": v(11, 67.87) * mm, "end": v(10.88, 67.85) * mm});
            skLineSegment(sketch, "E2383", {"start": v(10.88, 67.85) * mm, "end": v(10.75, 67.86) * mm});
            skLineSegment(sketch, "E2384", {"start": v(10.75, 67.86) * mm, "end": v(10.62, 67.9) * mm});
            skLineSegment(sketch, "E2385", {"start": v(10.62, 67.9) * mm, "end": v(10.5, 67.95) * mm});
            skLineSegment(sketch, "E2386", {"start": v(10.5, 67.95) * mm, "end": v(10.4, 68.03) * mm});
            skLineSegment(sketch, "E2387", {"start": v(10.4, 68.03) * mm, "end": v(10.32, 68.13) * mm});
            skLineSegment(sketch, "E2388", {"start": v(10.32, 68.13) * mm, "end": v(10.28, 68.23) * mm});
            skLineSegment(sketch, "E2389", {"start": v(10.28, 68.23) * mm, "end": v(10.25, 68.33) * mm});
            skLineSegment(sketch, "E2390", {"start": v(10.25, 68.33) * mm, "end": v(10.23, 68.42) * mm});
            skLineSegment(sketch, "E2391", {"start": v(10.23, 68.42) * mm, "end": v(10.23, 68.53) * mm});
            skLineSegment(sketch, "E2392", {"start": v(10.23, 68.53) * mm, "end": v(10.19, 68.62) * mm});
            skLineSegment(sketch, "E2393", {"start": v(10.19, 68.62) * mm, "end": v(10.1, 68.67) * mm});
            skLineSegment(sketch, "E2394", {"start": v(10.1, 68.67) * mm, "end": v(9.82, 68.7) * mm});
            skLineSegment(sketch, "E2395", {"start": v(9.82, 68.7) * mm, "end": v(9.72, 68.69) * mm});
            skLineSegment(sketch, "E2396", {"start": v(9.72, 68.69) * mm, "end": v(9.66, 68.6) * mm});
            skLineSegment(sketch, "E2397", {"start": v(9.66, 68.6) * mm, "end": v(9.62, 68.51) * mm});
            skLineSegment(sketch, "E2398", {"start": v(9.62, 68.51) * mm, "end": v(9.58, 68.42) * mm});
            skLineSegment(sketch, "E2399", {"start": v(9.58, 68.42) * mm, "end": v(9.52, 68.34) * mm});
            skLineSegment(sketch, "E2400", {"start": v(9.52, 68.34) * mm, "end": v(9.46, 68.26) * mm});
            skLineSegment(sketch, "E2401", {"start": v(9.46, 68.26) * mm, "end": v(9.35, 68.18) * mm});
            skLineSegment(sketch, "E2402", {"start": v(9.35, 68.18) * mm, "end": v(9.23, 68.13) * mm});
            skLineSegment(sketch, "E2403", {"start": v(9.23, 68.13) * mm, "end": v(9.1, 68.11) * mm});
            skLineSegment(sketch, "E2404", {"start": v(9.1, 68.11) * mm, "end": v(8.97, 68.12) * mm});
            skLineSegment(sketch, "E2405", {"start": v(8.97, 68.12) * mm, "end": v(8.84, 68.15) * mm});
            skLineSegment(sketch, "E2406", {"start": v(8.84, 68.15) * mm, "end": v(8.72, 68.2) * mm});
            skLineSegment(sketch, "E2407", {"start": v(8.72, 68.2) * mm, "end": v(8.62, 68.28) * mm});
            skLineSegment(sketch, "E2408", {"start": v(8.62, 68.28) * mm, "end": v(8.53, 68.38) * mm});
            skLineSegment(sketch, "E2409", {"start": v(8.53, 68.38) * mm, "end": v(8.49, 68.47) * mm});
            skLineSegment(sketch, "E2410", {"start": v(8.49, 68.47) * mm, "end": v(8.46, 68.57) * mm});
            skLineSegment(sketch, "E2411", {"start": v(8.46, 68.57) * mm, "end": v(8.44, 68.67) * mm});
            skLineSegment(sketch, "E2412", {"start": v(8.44, 68.67) * mm, "end": v(8.43, 68.77) * mm});
            skLineSegment(sketch, "E2413", {"start": v(8.43, 68.77) * mm, "end": v(8.4, 68.86) * mm});
            skLineSegment(sketch, "E2414", {"start": v(8.4, 68.86) * mm, "end": v(8.3, 68.9) * mm});
            skLineSegment(sketch, "E2415", {"start": v(8.3, 68.9) * mm, "end": v(8.02, 68.94) * mm});
            skLineSegment(sketch, "E2416", {"start": v(8.02, 68.94) * mm, "end": v(7.92, 68.92) * mm});
            skLineSegment(sketch, "E2417", {"start": v(7.92, 68.92) * mm, "end": v(7.86, 68.84) * mm});
            skLineSegment(sketch, "E2418", {"start": v(7.86, 68.84) * mm, "end": v(7.83, 68.74) * mm});
            skLineSegment(sketch, "E2419", {"start": v(7.83, 68.74) * mm, "end": v(7.78, 68.65) * mm});
            skLineSegment(sketch, "E2420", {"start": v(7.78, 68.65) * mm, "end": v(7.73, 68.56) * mm});
            skLineSegment(sketch, "E2421", {"start": v(7.73, 68.56) * mm, "end": v(7.67, 68.48) * mm});
            skLineSegment(sketch, "E2422", {"start": v(7.67, 68.48) * mm, "end": v(7.56, 68.4) * mm});
            skLineSegment(sketch, "E2423", {"start": v(7.56, 68.4) * mm, "end": v(7.44, 68.35) * mm});
            skLineSegment(sketch, "E2424", {"start": v(7.44, 68.35) * mm, "end": v(7.31, 68.33) * mm});
            skLineSegment(sketch, "E2425", {"start": v(7.31, 68.33) * mm, "end": v(7.18, 68.33) * mm});
            skLineSegment(sketch, "E2426", {"start": v(7.18, 68.33) * mm, "end": v(7.05, 68.35) * mm});
            skLineSegment(sketch, "E2427", {"start": v(7.05, 68.35) * mm, "end": v(6.93, 68.4) * mm});
            skLineSegment(sketch, "E2428", {"start": v(6.93, 68.4) * mm, "end": v(6.83, 68.48) * mm});
            skLineSegment(sketch, "E2429", {"start": v(6.83, 68.48) * mm, "end": v(6.74, 68.58) * mm});
            skLineSegment(sketch, "E2430", {"start": v(6.74, 68.58) * mm, "end": v(6.7, 68.67) * mm});
            skLineSegment(sketch, "E2431", {"start": v(6.7, 68.67) * mm, "end": v(6.66, 68.77) * mm});
            skLineSegment(sketch, "E2432", {"start": v(6.66, 68.77) * mm, "end": v(6.64, 68.87) * mm});
            skLineSegment(sketch, "E2433", {"start": v(6.64, 68.87) * mm, "end": v(6.63, 68.97) * mm});
            skLineSegment(sketch, "E2434", {"start": v(6.63, 68.97) * mm, "end": v(6.58, 69.06) * mm});
            skLineSegment(sketch, "E2435", {"start": v(6.58, 69.06) * mm, "end": v(6.49, 69.1) * mm});
            skLineSegment(sketch, "E2436", {"start": v(6.49, 69.1) * mm, "end": v(6.21, 69.13) * mm});
            skLineSegment(sketch, "E2437", {"start": v(6.21, 69.13) * mm, "end": v(6.11, 69.1) * mm});
            skLineSegment(sketch, "E2438", {"start": v(6.11, 69.1) * mm, "end": v(6.05, 69.02) * mm});
            skLineSegment(sketch, "E2439", {"start": v(6.05, 69.02) * mm, "end": v(6.02, 68.92) * mm});
            skLineSegment(sketch, "E2440", {"start": v(6.02, 68.92) * mm, "end": v(5.98, 68.83) * mm});
            skLineSegment(sketch, "E2441", {"start": v(5.98, 68.83) * mm, "end": v(5.93, 68.74) * mm});
            skLineSegment(sketch, "E2442", {"start": v(5.93, 68.74) * mm, "end": v(5.87, 68.66) * mm});
            skLineSegment(sketch, "E2443", {"start": v(5.87, 68.66) * mm, "end": v(5.77, 68.58) * mm});
            skLineSegment(sketch, "E2444", {"start": v(5.77, 68.58) * mm, "end": v(5.65, 68.52) * mm});
            skLineSegment(sketch, "E2445", {"start": v(5.65, 68.52) * mm, "end": v(5.52, 68.5) * mm});
            skLineSegment(sketch, "E2446", {"start": v(5.52, 68.5) * mm, "end": v(5.4, 68.5) * mm});
            skLineSegment(sketch, "E2447", {"start": v(5.4, 68.5) * mm, "end": v(5.26, 68.52) * mm});
            skLineSegment(sketch, "E2448", {"start": v(5.26, 68.52) * mm, "end": v(5.14, 68.56) * mm});
            skLineSegment(sketch, "E2449", {"start": v(5.14, 68.56) * mm, "end": v(5.03, 68.64) * mm});
            skLineSegment(sketch, "E2450", {"start": v(5.03, 68.64) * mm, "end": v(4.94, 68.73) * mm});
            skLineSegment(sketch, "E2451", {"start": v(4.94, 68.73) * mm, "end": v(4.9, 68.82) * mm});
            skLineSegment(sketch, "E2452", {"start": v(4.9, 68.82) * mm, "end": v(4.86, 68.92) * mm});
            skLineSegment(sketch, "E2453", {"start": v(4.86, 68.92) * mm, "end": v(4.83, 69.02) * mm});
            skLineSegment(sketch, "E2454", {"start": v(4.83, 69.02) * mm, "end": v(4.82, 69.12) * mm});
            skLineSegment(sketch, "E2455", {"start": v(4.82, 69.12) * mm, "end": v(4.77, 69.2) * mm});
            skLineSegment(sketch, "E2456", {"start": v(4.77, 69.2) * mm, "end": v(4.68, 69.25) * mm});
            skLineSegment(sketch, "E2457", {"start": v(4.68, 69.25) * mm, "end": v(4.4, 69.26) * mm});
            skLineSegment(sketch, "E2458", {"start": v(4.4, 69.26) * mm, "end": v(4.3, 69.24) * mm});
            skLineSegment(sketch, "E2459", {"start": v(4.3, 69.24) * mm, "end": v(4.24, 69.15) * mm});
            skLineSegment(sketch, "E2460", {"start": v(4.24, 69.15) * mm, "end": v(4.22, 69.06) * mm});
            skLineSegment(sketch, "E2461", {"start": v(4.22, 69.06) * mm, "end": v(4.18, 68.96) * mm});
            skLineSegment(sketch, "E2462", {"start": v(4.18, 68.96) * mm, "end": v(4.13, 68.87) * mm});
            skLineSegment(sketch, "E2463", {"start": v(4.13, 68.87) * mm, "end": v(4.07, 68.79) * mm});
            skLineSegment(sketch, "E2464", {"start": v(4.07, 68.79) * mm, "end": v(3.97, 68.7) * mm});
            skLineSegment(sketch, "E2465", {"start": v(3.97, 68.7) * mm, "end": v(3.85, 68.65) * mm});
            skLineSegment(sketch, "E2466", {"start": v(3.85, 68.65) * mm, "end": v(3.73, 68.62) * mm});
            skLineSegment(sketch, "E2467", {"start": v(3.73, 68.62) * mm, "end": v(3.6, 68.6) * mm});
            skLineSegment(sketch, "E2468", {"start": v(3.6, 68.6) * mm, "end": v(3.47, 68.63) * mm});
            skLineSegment(sketch, "E2469", {"start": v(3.47, 68.63) * mm, "end": v(3.34, 68.68) * mm});
            skLineSegment(sketch, "E2470", {"start": v(3.34, 68.68) * mm, "end": v(3.23, 68.75) * mm});
            skLineSegment(sketch, "E2471", {"start": v(3.23, 68.75) * mm, "end": v(3.14, 68.84) * mm});
            skLineSegment(sketch, "E2472", {"start": v(3.14, 68.84) * mm, "end": v(3.1, 68.93) * mm});
            skLineSegment(sketch, "E2473", {"start": v(3.1, 68.93) * mm, "end": v(3.05, 69.02) * mm});
            skLineSegment(sketch, "E2474", {"start": v(3.05, 69.02) * mm, "end": v(3.02, 69.12) * mm});
            skLineSegment(sketch, "E2475", {"start": v(3.02, 69.12) * mm, "end": v(3, 69.22) * mm});
            skLineSegment(sketch, "E2476", {"start": v(3, 69.22) * mm, "end": v(2.96, 69.3) * mm});
            skLineSegment(sketch, "E2477", {"start": v(2.96, 69.3) * mm, "end": v(2.86, 69.35) * mm});
            skLineSegment(sketch, "E2478", {"start": v(2.86, 69.35) * mm, "end": v(2.59, 69.36) * mm});
            skLineSegment(sketch, "E2479", {"start": v(2.59, 69.36) * mm, "end": v(2.49, 69.33) * mm});
            skLineSegment(sketch, "E2480", {"start": v(2.49, 69.33) * mm, "end": v(2.43, 69.24) * mm});
            skLineSegment(sketch, "E2481", {"start": v(2.43, 69.24) * mm, "end": v(2.4, 69.14) * mm});
            skLineSegment(sketch, "E2482", {"start": v(2.4, 69.14) * mm, "end": v(2.37, 69.05) * mm});
            skLineSegment(sketch, "E2483", {"start": v(2.37, 69.05) * mm, "end": v(2.33, 68.96) * mm});
            skLineSegment(sketch, "E2484", {"start": v(2.33, 68.96) * mm, "end": v(2.27, 68.87) * mm});
            skLineSegment(sketch, "E2485", {"start": v(2.27, 68.87) * mm, "end": v(2.17, 68.79) * mm});
            skLineSegment(sketch, "E2486", {"start": v(2.17, 68.79) * mm, "end": v(2.06, 68.73) * mm});
            skLineSegment(sketch, "E2487", {"start": v(2.06, 68.73) * mm, "end": v(1.93, 68.69) * mm});
            skLineSegment(sketch, "E2488", {"start": v(1.93, 68.69) * mm, "end": v(1.8, 68.68) * mm});
            skLineSegment(sketch, "E2489", {"start": v(1.8, 68.68) * mm, "end": v(1.67, 68.7) * mm});
            skLineSegment(sketch, "E2490", {"start": v(1.67, 68.7) * mm, "end": v(1.54, 68.74) * mm});
            skLineSegment(sketch, "E2491", {"start": v(1.54, 68.74) * mm, "end": v(1.43, 68.8) * mm});
            skLineSegment(sketch, "E2492", {"start": v(1.43, 68.8) * mm, "end": v(1.34, 68.9) * mm});
            skLineSegment(sketch, "E2493", {"start": v(1.34, 68.9) * mm, "end": v(1.28, 68.99) * mm});
            skLineSegment(sketch, "E2494", {"start": v(1.28, 68.99) * mm, "end": v(1.24, 69.08) * mm});
            skLineSegment(sketch, "E2495", {"start": v(1.24, 69.08) * mm, "end": v(1.21, 69.18) * mm});
            skLineSegment(sketch, "E2496", {"start": v(1.21, 69.18) * mm, "end": v(1.2, 69.27) * mm});
            skLineSegment(sketch, "E2497", {"start": v(1.2, 69.27) * mm, "end": v(1.15, 69.36) * mm});
            skLineSegment(sketch, "E2498", {"start": v(1.15, 69.36) * mm, "end": v(1.05, 69.4) * mm});
            skLineSegment(sketch, "E2499", {"start": v(1.05, 69.4) * mm, "end": v(0.77, 69.4) * mm});
            skLineSegment(sketch, "E2500", {"start": v(0.77, 69.4) * mm, "end": v(0.67, 69.37) * mm});
            skLineSegment(sketch, "E2501", {"start": v(0.67, 69.37) * mm, "end": v(0.62, 69.28) * mm});
            skLineSegment(sketch, "E2502", {"start": v(0.62, 69.28) * mm, "end": v(0.6, 69.18) * mm});
            skLineSegment(sketch, "E2503", {"start": v(0.6, 69.18) * mm, "end": v(0.57, 69.09) * mm});
            skLineSegment(sketch, "E2504", {"start": v(0.57, 69.09) * mm, "end": v(0.52, 69) * mm});
            skLineSegment(sketch, "E2505", {"start": v(0.52, 69) * mm, "end": v(0.47, 68.9) * mm});
            skLineSegment(sketch, "E2506", {"start": v(0.47, 68.9) * mm, "end": v(0.37, 68.82) * mm});
            skLineSegment(sketch, "E2507", {"start": v(0.37, 68.82) * mm, "end": v(0.26, 68.76) * mm});
            skLineSegment(sketch, "E2508", {"start": v(0.26, 68.76) * mm, "end": v(0.13, 68.72) * mm});
            skLineSegment(sketch, "E2509", {"start": v(0.13, 68.72) * mm, "end": v(0, 68.7) * mm});
            skLineSegment(sketch, "E2510", {"start": v(0, 68.7) * mm, "end": v(-0.13, 68.72) * mm});
            skLineSegment(sketch, "E2511", {"start": v(-0.13, 68.72) * mm, "end": v(-0.26, 68.76) * mm});
            skLineSegment(sketch, "E2512", {"start": v(-0.26, 68.76) * mm, "end": v(-0.37, 68.82) * mm});
            skLineSegment(sketch, "E2513", {"start": v(-0.37, 68.82) * mm, "end": v(-0.47, 68.9) * mm});
            skLineSegment(sketch, "E2514", {"start": v(-0.47, 68.9) * mm, "end": v(-0.52, 69) * mm});
            skLineSegment(sketch, "E2515", {"start": v(-0.52, 69) * mm, "end": v(-0.57, 69.09) * mm});
            skLineSegment(sketch, "E2516", {"start": v(-0.57, 69.09) * mm, "end": v(-0.6, 69.18) * mm});
            skLineSegment(sketch, "E2517", {"start": v(-0.6, 69.18) * mm, "end": v(-0.62, 69.28) * mm});
            skLineSegment(sketch, "E2518", {"start": v(-0.62, 69.28) * mm, "end": v(-0.67, 69.37) * mm});
            skLineSegment(sketch, "E2519", {"start": v(-0.67, 69.37) * mm, "end": v(-0.77, 69.4) * mm});
            skLineSegment(sketch, "E2520", {"start": v(-0.77, 69.4) * mm, "end": v(-1.05, 69.4) * mm});
            skLineSegment(sketch, "E2521", {"start": v(-1.05, 69.4) * mm, "end": v(-1.15, 69.36) * mm});
            skLineSegment(sketch, "E2522", {"start": v(-1.15, 69.36) * mm, "end": v(-1.2, 69.27) * mm});
            skLineSegment(sketch, "E2523", {"start": v(-1.2, 69.27) * mm, "end": v(-1.21, 69.18) * mm});
            skLineSegment(sketch, "E2524", {"start": v(-1.21, 69.18) * mm, "end": v(-1.24, 69.08) * mm});
            skLineSegment(sketch, "E2525", {"start": v(-1.24, 69.08) * mm, "end": v(-1.28, 68.99) * mm});
            skLineSegment(sketch, "E2526", {"start": v(-1.28, 68.99) * mm, "end": v(-1.34, 68.9) * mm});
            skLineSegment(sketch, "E2527", {"start": v(-1.34, 68.9) * mm, "end": v(-1.43, 68.8) * mm});
            skLineSegment(sketch, "E2528", {"start": v(-1.43, 68.8) * mm, "end": v(-1.54, 68.74) * mm});
            skLineSegment(sketch, "E2529", {"start": v(-1.54, 68.74) * mm, "end": v(-1.67, 68.7) * mm});
            skLineSegment(sketch, "E2530", {"start": v(-1.67, 68.7) * mm, "end": v(-1.8, 68.68) * mm});
            skLineSegment(sketch, "E2531", {"start": v(-1.8, 68.68) * mm, "end": v(-1.93, 68.69) * mm});
            skLineSegment(sketch, "E2532", {"start": v(-1.93, 68.69) * mm, "end": v(-2.06, 68.73) * mm});
            skLineSegment(sketch, "E2533", {"start": v(-2.06, 68.73) * mm, "end": v(-2.17, 68.79) * mm});
            skLineSegment(sketch, "E2534", {"start": v(-2.17, 68.79) * mm, "end": v(-2.27, 68.87) * mm});
            skLineSegment(sketch, "E2535", {"start": v(-2.27, 68.87) * mm, "end": v(-2.33, 68.96) * mm});
            skLineSegment(sketch, "E2536", {"start": v(-2.33, 68.96) * mm, "end": v(-2.37, 69.05) * mm});
            skLineSegment(sketch, "E2537", {"start": v(-2.37, 69.05) * mm, "end": v(-2.4, 69.14) * mm});
            skLineSegment(sketch, "E2538", {"start": v(-2.4, 69.14) * mm, "end": v(-2.43, 69.24) * mm});
            skLineSegment(sketch, "E2539", {"start": v(-2.43, 69.24) * mm, "end": v(-2.49, 69.33) * mm});
            skLineSegment(sketch, "E2540", {"start": v(-2.49, 69.33) * mm, "end": v(-2.59, 69.36) * mm});
            skLineSegment(sketch, "E2541", {"start": v(-2.59, 69.36) * mm, "end": v(-2.86, 69.35) * mm});
            skLineSegment(sketch, "E2542", {"start": v(-2.86, 69.35) * mm, "end": v(-2.96, 69.3) * mm});
            skLineSegment(sketch, "E2543", {"start": v(-2.96, 69.3) * mm, "end": v(-3, 69.22) * mm});
            skLineSegment(sketch, "E2544", {"start": v(-3, 69.22) * mm, "end": v(-3.02, 69.12) * mm});
            skLineSegment(sketch, "E2545", {"start": v(-3.02, 69.12) * mm, "end": v(-3.05, 69.02) * mm});
            skLineSegment(sketch, "E2546", {"start": v(-3.05, 69.02) * mm, "end": v(-3.09, 68.93) * mm});
            skLineSegment(sketch, "E2547", {"start": v(-3.09, 68.93) * mm, "end": v(-3.14, 68.84) * mm});
            skLineSegment(sketch, "E2548", {"start": v(-3.14, 68.84) * mm, "end": v(-3.23, 68.75) * mm});
            skLineSegment(sketch, "E2549", {"start": v(-3.23, 68.75) * mm, "end": v(-3.34, 68.68) * mm});
            skLineSegment(sketch, "E2550", {"start": v(-3.34, 68.68) * mm, "end": v(-3.47, 68.63) * mm});
            skLineSegment(sketch, "E2551", {"start": v(-3.47, 68.63) * mm, "end": v(-3.6, 68.6) * mm});
            skLineSegment(sketch, "E2552", {"start": v(-3.6, 68.6) * mm, "end": v(-3.73, 68.62) * mm});
            skLineSegment(sketch, "E2553", {"start": v(-3.73, 68.62) * mm, "end": v(-3.85, 68.65) * mm});
            skLineSegment(sketch, "E2554", {"start": v(-3.85, 68.65) * mm, "end": v(-3.97, 68.7) * mm});
            skLineSegment(sketch, "E2555", {"start": v(-3.97, 68.7) * mm, "end": v(-4.07, 68.79) * mm});
            skLineSegment(sketch, "E2556", {"start": v(-4.07, 68.79) * mm, "end": v(-4.13, 68.87) * mm});
            skLineSegment(sketch, "E2557", {"start": v(-4.13, 68.87) * mm, "end": v(-4.18, 68.96) * mm});
            skLineSegment(sketch, "E2558", {"start": v(-4.18, 68.96) * mm, "end": v(-4.22, 69.06) * mm});
            skLineSegment(sketch, "E2559", {"start": v(-4.22, 69.06) * mm, "end": v(-4.24, 69.15) * mm});
            skLineSegment(sketch, "E2560", {"start": v(-4.24, 69.15) * mm, "end": v(-4.3, 69.24) * mm});
            skLineSegment(sketch, "E2561", {"start": v(-4.3, 69.24) * mm, "end": v(-4.4, 69.26) * mm});
            skLineSegment(sketch, "E2562", {"start": v(-4.4, 69.26) * mm, "end": v(-4.68, 69.25) * mm});
            skLineSegment(sketch, "E2563", {"start": v(-4.68, 69.25) * mm, "end": v(-4.77, 69.2) * mm});
            skLineSegment(sketch, "E2564", {"start": v(-4.77, 69.2) * mm, "end": v(-4.82, 69.12) * mm});
            skLineSegment(sketch, "E2565", {"start": v(-4.82, 69.12) * mm, "end": v(-4.83, 69.02) * mm});
            skLineSegment(sketch, "E2566", {"start": v(-4.83, 69.02) * mm, "end": v(-4.86, 68.92) * mm});
            skLineSegment(sketch, "E2567", {"start": v(-4.86, 68.92) * mm, "end": v(-4.9, 68.82) * mm});
            skLineSegment(sketch, "E2568", {"start": v(-4.9, 68.82) * mm, "end": v(-4.94, 68.73) * mm});
            skLineSegment(sketch, "E2569", {"start": v(-4.94, 68.73) * mm, "end": v(-5.03, 68.64) * mm});
            skLineSegment(sketch, "E2570", {"start": v(-5.03, 68.64) * mm, "end": v(-5.14, 68.56) * mm});
            skLineSegment(sketch, "E2571", {"start": v(-5.14, 68.56) * mm, "end": v(-5.26, 68.52) * mm});
            skLineSegment(sketch, "E2572", {"start": v(-5.26, 68.52) * mm, "end": v(-5.4, 68.5) * mm});
            skLineSegment(sketch, "E2573", {"start": v(-5.4, 68.5) * mm, "end": v(-5.52, 68.5) * mm});
            skLineSegment(sketch, "E2574", {"start": v(-5.52, 68.5) * mm, "end": v(-5.65, 68.52) * mm});
            skLineSegment(sketch, "E2575", {"start": v(-5.65, 68.52) * mm, "end": v(-5.77, 68.58) * mm});
            skLineSegment(sketch, "E2576", {"start": v(-5.77, 68.58) * mm, "end": v(-5.87, 68.66) * mm});
            skLineSegment(sketch, "E2577", {"start": v(-5.87, 68.66) * mm, "end": v(-5.93, 68.74) * mm});
            skLineSegment(sketch, "E2578", {"start": v(-5.93, 68.74) * mm, "end": v(-5.98, 68.83) * mm});
            skLineSegment(sketch, "E2579", {"start": v(-5.98, 68.83) * mm, "end": v(-6.02, 68.92) * mm});
            skLineSegment(sketch, "E2580", {"start": v(-6.02, 68.92) * mm, "end": v(-6.05, 69.02) * mm});
            skLineSegment(sketch, "E2581", {"start": v(-6.05, 69.02) * mm, "end": v(-6.1, 69.1) * mm});
            skLineSegment(sketch, "E2582", {"start": v(-6.1, 69.1) * mm, "end": v(-6.21, 69.13) * mm});
            skLineSegment(sketch, "E2583", {"start": v(-6.21, 69.13) * mm, "end": v(-6.49, 69.1) * mm});
            skLineSegment(sketch, "E2584", {"start": v(-6.49, 69.1) * mm, "end": v(-6.58, 69.06) * mm});
            skLineSegment(sketch, "E2585", {"start": v(-6.58, 69.06) * mm, "end": v(-6.63, 68.97) * mm});
            skLineSegment(sketch, "E2586", {"start": v(-6.63, 68.97) * mm, "end": v(-6.64, 68.87) * mm});
            skLineSegment(sketch, "E2587", {"start": v(-6.64, 68.87) * mm, "end": v(-6.66, 68.77) * mm});
            skLineSegment(sketch, "E2588", {"start": v(-6.66, 68.77) * mm, "end": v(-6.7, 68.67) * mm});
            skLineSegment(sketch, "E2589", {"start": v(-6.7, 68.67) * mm, "end": v(-6.74, 68.58) * mm});
            skLineSegment(sketch, "E2590", {"start": v(-6.74, 68.58) * mm, "end": v(-6.83, 68.48) * mm});
            skLineSegment(sketch, "E2591", {"start": v(-6.83, 68.48) * mm, "end": v(-6.93, 68.4) * mm});
            skLineSegment(sketch, "E2592", {"start": v(-6.93, 68.4) * mm, "end": v(-7.05, 68.35) * mm});
            skLineSegment(sketch, "E2593", {"start": v(-7.05, 68.35) * mm, "end": v(-7.18, 68.33) * mm});
            skLineSegment(sketch, "E2594", {"start": v(-7.18, 68.33) * mm, "end": v(-7.31, 68.33) * mm});
            skLineSegment(sketch, "E2595", {"start": v(-7.31, 68.33) * mm, "end": v(-7.44, 68.35) * mm});
            skLineSegment(sketch, "E2596", {"start": v(-7.44, 68.35) * mm, "end": v(-7.56, 68.4) * mm});
            skLineSegment(sketch, "E2597", {"start": v(-7.56, 68.4) * mm, "end": v(-7.67, 68.48) * mm});
            skLineSegment(sketch, "E2598", {"start": v(-7.67, 68.48) * mm, "end": v(-7.73, 68.56) * mm});
            skLineSegment(sketch, "E2599", {"start": v(-7.73, 68.56) * mm, "end": v(-7.78, 68.65) * mm});
            skLineSegment(sketch, "E2600", {"start": v(-7.78, 68.65) * mm, "end": v(-7.83, 68.74) * mm});
            skLineSegment(sketch, "E2601", {"start": v(-7.83, 68.74) * mm, "end": v(-7.86, 68.84) * mm});
            skLineSegment(sketch, "E2602", {"start": v(-7.86, 68.84) * mm, "end": v(-7.92, 68.92) * mm});
            skLineSegment(sketch, "E2603", {"start": v(-7.92, 68.92) * mm, "end": v(-8.02, 68.94) * mm});
            skLineSegment(sketch, "E2604", {"start": v(-8.02, 68.94) * mm, "end": v(-8.3, 68.9) * mm});
            skLineSegment(sketch, "E2605", {"start": v(-8.3, 68.9) * mm, "end": v(-8.4, 68.86) * mm});
            skLineSegment(sketch, "E2606", {"start": v(-8.4, 68.86) * mm, "end": v(-8.43, 68.77) * mm});
            skLineSegment(sketch, "E2607", {"start": v(-8.43, 68.77) * mm, "end": v(-8.44, 68.67) * mm});
            skLineSegment(sketch, "E2608", {"start": v(-8.44, 68.67) * mm, "end": v(-8.46, 68.57) * mm});
            skLineSegment(sketch, "E2609", {"start": v(-8.46, 68.57) * mm, "end": v(-8.49, 68.47) * mm});
            skLineSegment(sketch, "E2610", {"start": v(-8.49, 68.47) * mm, "end": v(-8.53, 68.38) * mm});
            skLineSegment(sketch, "E2611", {"start": v(-8.53, 68.38) * mm, "end": v(-8.62, 68.28) * mm});
            skLineSegment(sketch, "E2612", {"start": v(-8.62, 68.28) * mm, "end": v(-8.72, 68.2) * mm});
            skLineSegment(sketch, "E2613", {"start": v(-8.72, 68.2) * mm, "end": v(-8.84, 68.15) * mm});
            skLineSegment(sketch, "E2614", {"start": v(-8.84, 68.15) * mm, "end": v(-8.97, 68.12) * mm});
            skLineSegment(sketch, "E2615", {"start": v(-8.97, 68.12) * mm, "end": v(-9.1, 68.11) * mm});
            skLineSegment(sketch, "E2616", {"start": v(-9.1, 68.11) * mm, "end": v(-9.23, 68.13) * mm});
            skLineSegment(sketch, "E2617", {"start": v(-9.23, 68.13) * mm, "end": v(-9.35, 68.18) * mm});
            skLineSegment(sketch, "E2618", {"start": v(-9.35, 68.18) * mm, "end": v(-9.46, 68.26) * mm});
            skLineSegment(sketch, "E2619", {"start": v(-9.46, 68.26) * mm, "end": v(-9.52, 68.34) * mm});
            skLineSegment(sketch, "E2620", {"start": v(-9.52, 68.34) * mm, "end": v(-9.58, 68.42) * mm});
            skLineSegment(sketch, "E2621", {"start": v(-9.58, 68.42) * mm, "end": v(-9.62, 68.51) * mm});
            skLineSegment(sketch, "E2622", {"start": v(-9.62, 68.51) * mm, "end": v(-9.66, 68.6) * mm});
            skLineSegment(sketch, "E2623", {"start": v(-9.66, 68.6) * mm, "end": v(-9.72, 68.69) * mm});
            skLineSegment(sketch, "E2624", {"start": v(-9.72, 68.69) * mm, "end": v(-9.82, 68.7) * mm});
            skLineSegment(sketch, "E2625", {"start": v(-9.82, 68.7) * mm, "end": v(-10.1, 68.67) * mm});
            skLineSegment(sketch, "E2626", {"start": v(-10.1, 68.67) * mm, "end": v(-10.19, 68.62) * mm});
            skLineSegment(sketch, "E2627", {"start": v(-10.19, 68.62) * mm, "end": v(-10.23, 68.53) * mm});
            skLineSegment(sketch, "E2628", {"start": v(-10.23, 68.53) * mm, "end": v(-10.23, 68.43) * mm});
            skLineSegment(sketch, "E2629", {"start": v(-10.23, 68.43) * mm, "end": v(-10.25, 68.33) * mm});
            skLineSegment(sketch, "E2630", {"start": v(-10.25, 68.33) * mm, "end": v(-10.28, 68.23) * mm});
            skLineSegment(sketch, "E2631", {"start": v(-10.28, 68.23) * mm, "end": v(-10.32, 68.13) * mm});
            skLineSegment(sketch, "E2632", {"start": v(-10.32, 68.13) * mm, "end": v(-10.4, 68.03) * mm});
            skLineSegment(sketch, "E2633", {"start": v(-10.4, 68.03) * mm, "end": v(-10.5, 67.95) * mm});
            skLineSegment(sketch, "E2634", {"start": v(-10.5, 67.95) * mm, "end": v(-10.62, 67.9) * mm});
            skLineSegment(sketch, "E2635", {"start": v(-10.62, 67.9) * mm, "end": v(-10.75, 67.86) * mm});
            skLineSegment(sketch, "E2636", {"start": v(-10.75, 67.86) * mm, "end": v(-10.88, 67.85) * mm});
            skLineSegment(sketch, "E2637", {"start": v(-10.88, 67.85) * mm, "end": v(-11, 67.87) * mm});
            skLineSegment(sketch, "E2638", {"start": v(-11, 67.87) * mm, "end": v(-11.13, 67.91) * mm});
            skLineSegment(sketch, "E2639", {"start": v(-11.13, 67.91) * mm, "end": v(-11.24, 67.99) * mm});
            skLineSegment(sketch, "E2640", {"start": v(-11.24, 67.99) * mm, "end": v(-11.3, 68.07) * mm});
            skLineSegment(sketch, "E2641", {"start": v(-11.3, 68.07) * mm, "end": v(-11.37, 68.15) * mm});
            skLineSegment(sketch, "E2642", {"start": v(-11.37, 68.15) * mm, "end": v(-11.41, 68.24) * mm});
            skLineSegment(sketch, "E2643", {"start": v(-11.41, 68.24) * mm, "end": v(-11.45, 68.33) * mm});
            skLineSegment(sketch, "E2644", {"start": v(-11.45, 68.33) * mm, "end": v(-11.51, 68.4) * mm});
            skLineSegment(sketch, "E2645", {"start": v(-11.51, 68.4) * mm, "end": v(-11.62, 68.43) * mm});
            skLineSegment(sketch, "E2646", {"start": v(-11.62, 68.43) * mm, "end": v(-11.89, 68.38) * mm});
            skLineSegment(sketch, "E2647", {"start": v(-11.89, 68.38) * mm, "end": v(-11.98, 68.33) * mm});
            skLineSegment(sketch, "E2648", {"start": v(-11.98, 68.33) * mm, "end": v(-12.02, 68.23) * mm});
            skLineSegment(sketch, "E2649", {"start": v(-12.02, 68.23) * mm, "end": v(-12.02, 68.13) * mm});
            skLineSegment(sketch, "E2650", {"start": v(-12.02, 68.13) * mm, "end": v(-12.03, 68.03) * mm});
            skLineSegment(sketch, "E2651", {"start": v(-12.03, 68.03) * mm, "end": v(-12.06, 67.94) * mm});
            skLineSegment(sketch, "E2652", {"start": v(-12.06, 67.94) * mm, "end": v(-12.1, 67.84) * mm});
            skLineSegment(sketch, "E2653", {"start": v(-12.1, 67.84) * mm, "end": v(-12.18, 67.74) * mm});
            skLineSegment(sketch, "E2654", {"start": v(-12.18, 67.74) * mm, "end": v(-12.28, 67.65) * mm});
            skLineSegment(sketch, "E2655", {"start": v(-12.28, 67.65) * mm, "end": v(-12.4, 67.6) * mm});
            skLineSegment(sketch, "E2656", {"start": v(-12.4, 67.6) * mm, "end": v(-12.52, 67.55) * mm});
            skLineSegment(sketch, "E2657", {"start": v(-12.52, 67.55) * mm, "end": v(-12.65, 67.54) * mm});
            skLineSegment(sketch, "E2658", {"start": v(-12.65, 67.54) * mm, "end": v(-12.78, 67.56) * mm});
            skLineSegment(sketch, "E2659", {"start": v(-12.78, 67.56) * mm, "end": v(-12.9, 67.6) * mm});
            skLineSegment(sketch, "E2660", {"start": v(-12.9, 67.6) * mm, "end": v(-13.02, 67.67) * mm});
            skLineSegment(sketch, "E2661", {"start": v(-13.02, 67.67) * mm, "end": v(-13.09, 67.75) * mm});
            skLineSegment(sketch, "E2662", {"start": v(-13.09, 67.75) * mm, "end": v(-13.15, 67.83) * mm});
            skLineSegment(sketch, "E2663", {"start": v(-13.15, 67.83) * mm, "end": v(-13.2, 67.92) * mm});
            skLineSegment(sketch, "E2664", {"start": v(-13.2, 67.92) * mm, "end": v(-13.23, 68) * mm});
            skLineSegment(sketch, "E2665", {"start": v(-13.23, 68) * mm, "end": v(-13.3, 68.08) * mm});
            skLineSegment(sketch, "E2666", {"start": v(-13.3, 68.08) * mm, "end": v(-13.4, 68.1) * mm});
            skLineSegment(sketch, "E2667", {"start": v(-13.4, 68.1) * mm, "end": v(-13.67, 68.04) * mm});
            skLineSegment(sketch, "E2668", {"start": v(-13.67, 68.04) * mm, "end": v(-13.77, 68) * mm});
            skLineSegment(sketch, "E2669", {"start": v(-13.77, 68) * mm, "end": v(-13.8, 67.9) * mm});
            skLineSegment(sketch, "E2670", {"start": v(-13.8, 67.9) * mm, "end": v(-13.8, 67.8) * mm});
            skLineSegment(sketch, "E2671", {"start": v(-13.8, 67.8) * mm, "end": v(-13.81, 67.7) * mm});
            skLineSegment(sketch, "E2672", {"start": v(-13.81, 67.7) * mm, "end": v(-13.83, 67.6) * mm});
            skLineSegment(sketch, "E2673", {"start": v(-13.83, 67.6) * mm, "end": v(-13.87, 67.5) * mm});
            skLineSegment(sketch, "E2674", {"start": v(-13.87, 67.5) * mm, "end": v(-13.95, 67.4) * mm});
            skLineSegment(sketch, "E2675", {"start": v(-13.95, 67.4) * mm, "end": v(-14.04, 67.3) * mm});
            skLineSegment(sketch, "E2676", {"start": v(-14.04, 67.3) * mm, "end": v(-14.16, 67.24) * mm});
            skLineSegment(sketch, "E2677", {"start": v(-14.16, 67.24) * mm, "end": v(-14.28, 67.2) * mm});
            skLineSegment(sketch, "E2678", {"start": v(-14.28, 67.2) * mm, "end": v(-14.42, 67.19) * mm});
            skLineSegment(sketch, "E2679", {"start": v(-14.42, 67.19) * mm, "end": v(-14.55, 67.2) * mm});
            skLineSegment(sketch, "E2680", {"start": v(-14.55, 67.2) * mm, "end": v(-14.67, 67.24) * mm});
            skLineSegment(sketch, "E2681", {"start": v(-14.67, 67.24) * mm, "end": v(-14.78, 67.3) * mm});
            skLineSegment(sketch, "E2682", {"start": v(-14.78, 67.3) * mm, "end": v(-14.86, 67.38) * mm});
            skLineSegment(sketch, "E2683", {"start": v(-14.86, 67.38) * mm, "end": v(-14.92, 67.46) * mm});
            skLineSegment(sketch, "E2684", {"start": v(-14.92, 67.46) * mm, "end": v(-14.97, 67.55) * mm});
            skLineSegment(sketch, "E2685", {"start": v(-14.97, 67.55) * mm, "end": v(-15, 67.64) * mm});
            skLineSegment(sketch, "E2686", {"start": v(-15, 67.64) * mm, "end": v(-15.08, 67.71) * mm});
            skLineSegment(sketch, "E2687", {"start": v(-15.08, 67.71) * mm, "end": v(-15.18, 67.72) * mm});
            skLineSegment(sketch, "E2688", {"start": v(-15.18, 67.72) * mm, "end": v(-15.45, 67.66) * mm});
            skLineSegment(sketch, "E2689", {"start": v(-15.45, 67.66) * mm, "end": v(-15.54, 67.6) * mm});
            skLineSegment(sketch, "E2690", {"start": v(-15.54, 67.6) * mm, "end": v(-15.57, 67.51) * mm});
            skLineSegment(sketch, "E2691", {"start": v(-15.57, 67.51) * mm, "end": v(-15.57, 67.41) * mm});
            skLineSegment(sketch, "E2692", {"start": v(-15.57, 67.41) * mm, "end": v(-15.58, 67.31) * mm});
            skLineSegment(sketch, "E2693", {"start": v(-15.58, 67.31) * mm, "end": v(-15.6, 67.21) * mm});
            skLineSegment(sketch, "E2694", {"start": v(-15.6, 67.21) * mm, "end": v(-15.63, 67.11) * mm});
            skLineSegment(sketch, "E2695", {"start": v(-15.63, 67.11) * mm, "end": v(-15.7, 67) * mm});
            skLineSegment(sketch, "E2696", {"start": v(-15.7, 67) * mm, "end": v(-15.8, 66.92) * mm});
            skLineSegment(sketch, "E2697", {"start": v(-15.8, 66.92) * mm, "end": v(-15.91, 66.85) * mm});
            skLineSegment(sketch, "E2698", {"start": v(-15.91, 66.85) * mm, "end": v(-16.04, 66.8) * mm});
            skLineSegment(sketch, "E2699", {"start": v(-16.04, 66.8) * mm, "end": v(-16.17, 66.79) * mm});
            skLineSegment(sketch, "E2700", {"start": v(-16.17, 66.79) * mm, "end": v(-16.3, 66.8) * mm});
            skLineSegment(sketch, "E2701", {"start": v(-16.3, 66.8) * mm, "end": v(-16.43, 66.83) * mm});
            skLineSegment(sketch, "E2702", {"start": v(-16.43, 66.83) * mm, "end": v(-16.54, 66.9) * mm});
            skLineSegment(sketch, "E2703", {"start": v(-16.54, 66.9) * mm, "end": v(-16.61, 66.97) * mm});
            skLineSegment(sketch, "E2704", {"start": v(-16.61, 66.97) * mm, "end": v(-16.68, 67.05) * mm});
            skLineSegment(sketch, "E2705", {"start": v(-16.68, 67.05) * mm, "end": v(-16.73, 67.13) * mm});
            skLineSegment(sketch, "E2706", {"start": v(-16.73, 67.13) * mm, "end": v(-16.77, 67.22) * mm});
            skLineSegment(sketch, "E2707", {"start": v(-16.77, 67.22) * mm, "end": v(-16.84, 67.3) * mm});
            skLineSegment(sketch, "E2708", {"start": v(-16.84, 67.3) * mm, "end": v(-16.95, 67.3) * mm});
            skLineSegment(sketch, "E2709", {"start": v(-16.95, 67.3) * mm, "end": v(-17.22, 67.24) * mm});
            skLineSegment(sketch, "E2710", {"start": v(-17.22, 67.24) * mm, "end": v(-17.3, 67.18) * mm});
            skLineSegment(sketch, "E2711", {"start": v(-17.3, 67.18) * mm, "end": v(-17.33, 67.08) * mm});
            skLineSegment(sketch, "E2712", {"start": v(-17.33, 67.08) * mm, "end": v(-17.33, 66.98) * mm});
            skLineSegment(sketch, "E2713", {"start": v(-17.33, 66.98) * mm, "end": v(-17.33, 66.88) * mm});
            skLineSegment(sketch, "E2714", {"start": v(-17.33, 66.88) * mm, "end": v(-17.35, 66.78) * mm});
            skLineSegment(sketch, "E2715", {"start": v(-17.35, 66.78) * mm, "end": v(-17.38, 66.68) * mm});
            skLineSegment(sketch, "E2716", {"start": v(-17.38, 66.68) * mm, "end": v(-17.45, 66.57) * mm});
            skLineSegment(sketch, "E2717", {"start": v(-17.45, 66.57) * mm, "end": v(-17.55, 66.48) * mm});
            skLineSegment(sketch, "E2718", {"start": v(-17.55, 66.48) * mm, "end": v(-17.66, 66.4) * mm});
            skLineSegment(sketch, "E2719", {"start": v(-17.66, 66.4) * mm, "end": v(-17.78, 66.36) * mm});
            skLineSegment(sketch, "E2720", {"start": v(-17.78, 66.36) * mm, "end": v(-17.91, 66.34) * mm});
            skLineSegment(sketch, "E2721", {"start": v(-17.91, 66.34) * mm, "end": v(-18.04, 66.35) * mm});
            skLineSegment(sketch, "E2722", {"start": v(-18.04, 66.35) * mm, "end": v(-18.17, 66.38) * mm});
            skLineSegment(sketch, "E2723", {"start": v(-18.17, 66.38) * mm, "end": v(-18.29, 66.44) * mm});
            skLineSegment(sketch, "E2724", {"start": v(-18.29, 66.44) * mm, "end": v(-18.36, 66.51) * mm});
            skLineSegment(sketch, "E2725", {"start": v(-18.36, 66.51) * mm, "end": v(-18.43, 66.59) * mm});
            skLineSegment(sketch, "E2726", {"start": v(-18.43, 66.59) * mm, "end": v(-18.48, 66.67) * mm});
            skLineSegment(sketch, "E2727", {"start": v(-18.48, 66.67) * mm, "end": v(-18.53, 66.76) * mm});
            skLineSegment(sketch, "E2728", {"start": v(-18.53, 66.76) * mm, "end": v(-18.6, 66.83) * mm});
            skLineSegment(sketch, "E2729", {"start": v(-18.6, 66.83) * mm, "end": v(-18.7, 66.84) * mm});
            skLineSegment(sketch, "E2730", {"start": v(-18.7, 66.84) * mm, "end": v(-18.97, 66.76) * mm});
            skLineSegment(sketch, "E2731", {"start": v(-18.97, 66.76) * mm, "end": v(-19.06, 66.7) * mm});
            skLineSegment(sketch, "E2732", {"start": v(-19.06, 66.7) * mm, "end": v(-19.08, 66.6) * mm});
            skLineSegment(sketch, "E2733", {"start": v(-19.08, 66.6) * mm, "end": v(-19.08, 66.5) * mm});
            skLineSegment(sketch, "E2734", {"start": v(-19.08, 66.5) * mm, "end": v(-19.08, 66.4) * mm});
            skLineSegment(sketch, "E2735", {"start": v(-19.08, 66.4) * mm, "end": v(-19.1, 66.3) * mm});
            skLineSegment(sketch, "E2736", {"start": v(-19.1, 66.3) * mm, "end": v(-19.12, 66.2) * mm});
            skLineSegment(sketch, "E2737", {"start": v(-19.12, 66.2) * mm, "end": v(-19.2, 66.1) * mm});
            skLineSegment(sketch, "E2738", {"start": v(-19.2, 66.1) * mm, "end": v(-19.28, 66) * mm});
            skLineSegment(sketch, "E2739", {"start": v(-19.28, 66) * mm, "end": v(-19.4, 65.92) * mm});
            skLineSegment(sketch, "E2740", {"start": v(-19.4, 65.92) * mm, "end": v(-19.51, 65.87) * mm});
            skLineSegment(sketch, "E2741", {"start": v(-19.51, 65.87) * mm, "end": v(-19.64, 65.85) * mm});
            skLineSegment(sketch, "E2742", {"start": v(-19.64, 65.85) * mm, "end": v(-19.77, 65.85) * mm});
            skLineSegment(sketch, "E2743", {"start": v(-19.77, 65.85) * mm, "end": v(-19.9, 65.88) * mm});
            skLineSegment(sketch, "E2744", {"start": v(-19.9, 65.88) * mm, "end": v(-20.02, 65.94) * mm});
            skLineSegment(sketch, "E2745", {"start": v(-20.02, 65.94) * mm, "end": v(-20.1, 66) * mm});
            skLineSegment(sketch, "E2746", {"start": v(-20.1, 66) * mm, "end": v(-20.16, 66.08) * mm});
            skLineSegment(sketch, "E2747", {"start": v(-20.16, 66.08) * mm, "end": v(-20.22, 66.16) * mm});
            skLineSegment(sketch, "E2748", {"start": v(-20.22, 66.16) * mm, "end": v(-20.27, 66.25) * mm});
            skLineSegment(sketch, "E2749", {"start": v(-20.27, 66.25) * mm, "end": v(-20.34, 66.32) * mm});
            skLineSegment(sketch, "E2750", {"start": v(-20.34, 66.32) * mm, "end": v(-20.45, 66.32) * mm});
            skLineSegment(sketch, "E2751", {"start": v(-20.45, 66.32) * mm, "end": v(-20.71, 66.24) * mm});
            skLineSegment(sketch, "E2752", {"start": v(-20.71, 66.24) * mm, "end": v(-20.8, 66.18) * mm});
            skLineSegment(sketch, "E2753", {"start": v(-20.8, 66.18) * mm, "end": v(-20.82, 66.08) * mm});
            skLineSegment(sketch, "E2754", {"start": v(-20.82, 66.08) * mm, "end": v(-20.81, 65.98) * mm});
            skLineSegment(sketch, "E2755", {"start": v(-20.81, 65.98) * mm, "end": v(-20.81, 65.88) * mm});
            skLineSegment(sketch, "E2756", {"start": v(-20.81, 65.88) * mm, "end": v(-20.82, 65.78) * mm});
            skLineSegment(sketch, "E2757", {"start": v(-20.82, 65.78) * mm, "end": v(-20.85, 65.68) * mm});
            skLineSegment(sketch, "E2758", {"start": v(-20.85, 65.68) * mm, "end": v(-20.91, 65.57) * mm});
            skLineSegment(sketch, "E2759", {"start": v(-20.91, 65.57) * mm, "end": v(-21, 65.47) * mm});
            skLineSegment(sketch, "E2760", {"start": v(-21, 65.47) * mm, "end": v(-21.1, 65.4) * mm});
            skLineSegment(sketch, "E2761", {"start": v(-21.1, 65.4) * mm, "end": v(-21.23, 65.34) * mm});
            skLineSegment(sketch, "E2762", {"start": v(-21.23, 65.34) * mm, "end": v(-21.36, 65.31) * mm});
            skLineSegment(sketch, "E2763", {"start": v(-21.36, 65.31) * mm, "end": v(-21.5, 65.31) * mm});
            skLineSegment(sketch, "E2764", {"start": v(-21.5, 65.31) * mm, "end": v(-21.62, 65.34) * mm});
            skLineSegment(sketch, "E2765", {"start": v(-21.62, 65.34) * mm, "end": v(-21.74, 65.4) * mm});
            skLineSegment(sketch, "E2766", {"start": v(-21.74, 65.4) * mm, "end": v(-21.82, 65.46) * mm});
            skLineSegment(sketch, "E2767", {"start": v(-21.82, 65.46) * mm, "end": v(-21.89, 65.53) * mm});
            skLineSegment(sketch, "E2768", {"start": v(-21.89, 65.53) * mm, "end": v(-21.95, 65.61) * mm});
            skLineSegment(sketch, "E2769", {"start": v(-21.95, 65.61) * mm, "end": v(-22, 65.7) * mm});
            skLineSegment(sketch, "E2770", {"start": v(-22, 65.7) * mm, "end": v(-22.07, 65.76) * mm});
            skLineSegment(sketch, "E2771", {"start": v(-22.07, 65.76) * mm, "end": v(-22.18, 65.77) * mm});
            skLineSegment(sketch, "E2772", {"start": v(-22.18, 65.77) * mm, "end": v(-22.44, 65.68) * mm});
            skLineSegment(sketch, "E2773", {"start": v(-22.44, 65.68) * mm, "end": v(-22.52, 65.61) * mm});
            skLineSegment(sketch, "E2774", {"start": v(-22.52, 65.61) * mm, "end": v(-22.54, 65.51) * mm});
            skLineSegment(sketch, "E2775", {"start": v(-22.54, 65.51) * mm, "end": v(-22.53, 65.41) * mm});
            skLineSegment(sketch, "E2776", {"start": v(-22.53, 65.41) * mm, "end": v(-22.53, 65.31) * mm});
            skLineSegment(sketch, "E2777", {"start": v(-22.53, 65.31) * mm, "end": v(-22.54, 65.21) * mm});
            skLineSegment(sketch, "E2778", {"start": v(-22.54, 65.21) * mm, "end": v(-22.56, 65.11) * mm});
            skLineSegment(sketch, "E2779", {"start": v(-22.56, 65.11) * mm, "end": v(-22.62, 65) * mm});
            skLineSegment(sketch, "E2780", {"start": v(-22.62, 65) * mm, "end": v(-22.7, 64.9) * mm});
            skLineSegment(sketch, "E2781", {"start": v(-22.7, 64.9) * mm, "end": v(-22.81, 64.82) * mm});
            skLineSegment(sketch, "E2782", {"start": v(-22.81, 64.82) * mm, "end": v(-22.93, 64.76) * mm});
            skLineSegment(sketch, "E2783", {"start": v(-22.93, 64.76) * mm, "end": v(-23.06, 64.73) * mm});
            skLineSegment(sketch, "E2784", {"start": v(-23.06, 64.73) * mm, "end": v(-23.2, 64.73) * mm});
            skLineSegment(sketch, "E2785", {"start": v(-23.2, 64.73) * mm, "end": v(-23.32, 64.75) * mm});
            skLineSegment(sketch, "E2786", {"start": v(-23.32, 64.75) * mm, "end": v(-23.44, 64.8) * mm});
            skLineSegment(sketch, "E2787", {"start": v(-23.44, 64.8) * mm, "end": v(-23.52, 64.86) * mm});
            skLineSegment(sketch, "E2788", {"start": v(-23.52, 64.86) * mm, "end": v(-23.6, 64.94) * mm});
            skLineSegment(sketch, "E2789", {"start": v(-23.6, 64.94) * mm, "end": v(-23.66, 65.02) * mm});
            skLineSegment(sketch, "E2790", {"start": v(-23.66, 65.02) * mm, "end": v(-23.7, 65.1) * mm});
            skLineSegment(sketch, "E2791", {"start": v(-23.7, 65.1) * mm, "end": v(-23.79, 65.16) * mm});
            skLineSegment(sketch, "E2792", {"start": v(-23.79, 65.16) * mm, "end": v(-23.9, 65.16) * mm});
            skLineSegment(sketch, "E2793", {"start": v(-23.9, 65.16) * mm, "end": v(-24.15, 65.07) * mm});
            skLineSegment(sketch, "E2794", {"start": v(-24.15, 65.07) * mm, "end": v(-24.23, 65) * mm});
            skLineSegment(sketch, "E2795", {"start": v(-24.23, 65) * mm, "end": v(-24.25, 64.9) * mm});
            skLineSegment(sketch, "E2796", {"start": v(-24.25, 64.9) * mm, "end": v(-24.23, 64.8) * mm});
            skLineSegment(sketch, "E2797", {"start": v(-24.23, 64.8) * mm, "end": v(-24.23, 64.7) * mm});
            skLineSegment(sketch, "E2798", {"start": v(-24.23, 64.7) * mm, "end": v(-24.24, 64.6) * mm});
            skLineSegment(sketch, "E2799", {"start": v(-24.24, 64.6) * mm, "end": v(-24.26, 64.5) * mm});
            skLineSegment(sketch, "E2800", {"start": v(-24.26, 64.5) * mm, "end": v(-24.32, 64.38) * mm});
            skLineSegment(sketch, "E2801", {"start": v(-24.32, 64.38) * mm, "end": v(-24.4, 64.28) * mm});
            skLineSegment(sketch, "E2802", {"start": v(-24.4, 64.28) * mm, "end": v(-24.5, 64.2) * mm});
            skLineSegment(sketch, "E2803", {"start": v(-24.5, 64.2) * mm, "end": v(-24.62, 64.14) * mm});
            skLineSegment(sketch, "E2804", {"start": v(-24.62, 64.14) * mm, "end": v(-24.75, 64.1) * mm});
            skLineSegment(sketch, "E2805", {"start": v(-24.75, 64.1) * mm, "end": v(-24.88, 64.1) * mm});
            skLineSegment(sketch, "E2806", {"start": v(-24.88, 64.1) * mm, "end": v(-25, 64.12) * mm});
            skLineSegment(sketch, "E2807", {"start": v(-25, 64.12) * mm, "end": v(-25.13, 64.16) * mm});
            skLineSegment(sketch, "E2808", {"start": v(-25.13, 64.16) * mm, "end": v(-25.21, 64.23) * mm});
            skLineSegment(sketch, "E2809", {"start": v(-25.21, 64.23) * mm, "end": v(-25.29, 64.3) * mm});
            skLineSegment(sketch, "E2810", {"start": v(-25.29, 64.3) * mm, "end": v(-25.35, 64.37) * mm});
            skLineSegment(sketch, "E2811", {"start": v(-25.35, 64.37) * mm, "end": v(-25.4, 64.46) * mm});
            skLineSegment(sketch, "E2812", {"start": v(-25.4, 64.46) * mm, "end": v(-25.48, 64.52) * mm});
            skLineSegment(sketch, "E2813", {"start": v(-25.48, 64.52) * mm, "end": v(-25.6, 64.51) * mm});
            skLineSegment(sketch, "E2814", {"start": v(-25.6, 64.51) * mm, "end": v(-25.85, 64.41) * mm});
            skLineSegment(sketch, "E2815", {"start": v(-25.85, 64.41) * mm, "end": v(-25.93, 64.34) * mm});
            skLineSegment(sketch, "E2816", {"start": v(-25.93, 64.34) * mm, "end": v(-25.94, 64.24) * mm});
            skLineSegment(sketch, "E2817", {"start": v(-25.94, 64.24) * mm, "end": v(-25.92, 64.15) * mm});
            skLineSegment(sketch, "E2818", {"start": v(-25.92, 64.15) * mm, "end": v(-25.92, 64.05) * mm});
            skLineSegment(sketch, "E2819", {"start": v(-25.92, 64.05) * mm, "end": v(-25.92, 63.94) * mm});
            skLineSegment(sketch, "E2820", {"start": v(-25.92, 63.94) * mm, "end": v(-25.94, 63.84) * mm});
            skLineSegment(sketch, "E2821", {"start": v(-25.94, 63.84) * mm, "end": v(-26, 63.72) * mm});
            skLineSegment(sketch, "E2822", {"start": v(-26, 63.72) * mm, "end": v(-26.07, 63.62) * mm});
            skLineSegment(sketch, "E2823", {"start": v(-26.07, 63.62) * mm, "end": v(-26.18, 63.54) * mm});
            skLineSegment(sketch, "E2824", {"start": v(-26.18, 63.54) * mm, "end": v(-26.3, 63.47) * mm});
            skLineSegment(sketch, "E2825", {"start": v(-26.3, 63.47) * mm, "end": v(-26.42, 63.44) * mm});
            skLineSegment(sketch, "E2826", {"start": v(-26.42, 63.44) * mm, "end": v(-26.55, 63.42) * mm});
            skLineSegment(sketch, "E2827", {"start": v(-26.55, 63.42) * mm, "end": v(-26.68, 63.44) * mm});
            skLineSegment(sketch, "E2828", {"start": v(-26.68, 63.44) * mm, "end": v(-26.8, 63.48) * mm});
            skLineSegment(sketch, "E2829", {"start": v(-26.8, 63.48) * mm, "end": v(-26.89, 63.54) * mm});
            skLineSegment(sketch, "E2830", {"start": v(-26.89, 63.54) * mm, "end": v(-26.96, 63.61) * mm});
            skLineSegment(sketch, "E2831", {"start": v(-26.96, 63.61) * mm, "end": v(-27.03, 63.69) * mm});
            skLineSegment(sketch, "E2832", {"start": v(-27.03, 63.69) * mm, "end": v(-27.08, 63.77) * mm});
            skLineSegment(sketch, "E2833", {"start": v(-27.08, 63.77) * mm, "end": v(-27.16, 63.83) * mm});
            skLineSegment(sketch, "E2834", {"start": v(-27.16, 63.83) * mm, "end": v(-27.27, 63.82) * mm});
            skLineSegment(sketch, "E2835", {"start": v(-27.27, 63.82) * mm, "end": v(-27.52, 63.71) * mm});
            skLineSegment(sketch, "E2836", {"start": v(-27.52, 63.71) * mm, "end": v(-27.6, 63.64) * mm});
            skLineSegment(sketch, "E2837", {"start": v(-27.6, 63.64) * mm, "end": v(-27.61, 63.54) * mm});
            skLineSegment(sketch, "E2838", {"start": v(-27.61, 63.54) * mm, "end": v(-27.6, 63.45) * mm});
            skLineSegment(sketch, "E2839", {"start": v(-27.6, 63.45) * mm, "end": v(-27.58, 63.34) * mm});
            skLineSegment(sketch, "E2840", {"start": v(-27.58, 63.34) * mm, "end": v(-27.59, 63.24) * mm});
            skLineSegment(sketch, "E2841", {"start": v(-27.59, 63.24) * mm, "end": v(-27.6, 63.14) * mm});
            skLineSegment(sketch, "E2842", {"start": v(-27.6, 63.14) * mm, "end": v(-27.65, 63.02) * mm});
            skLineSegment(sketch, "E2843", {"start": v(-27.65, 63.02) * mm, "end": v(-27.73, 62.92) * mm});
            skLineSegment(sketch, "E2844", {"start": v(-27.73, 62.92) * mm, "end": v(-27.83, 62.83) * mm});
            skLineSegment(sketch, "E2845", {"start": v(-27.83, 62.83) * mm, "end": v(-27.94, 62.76) * mm});
            skLineSegment(sketch, "E2846", {"start": v(-27.94, 62.76) * mm, "end": v(-28.07, 62.72) * mm});
            skLineSegment(sketch, "E2847", {"start": v(-28.07, 62.72) * mm, "end": v(-28.2, 62.7) * mm});
            skLineSegment(sketch, "E2848", {"start": v(-28.2, 62.7) * mm, "end": v(-28.33, 62.72) * mm});
            skLineSegment(sketch, "E2849", {"start": v(-28.33, 62.72) * mm, "end": v(-28.45, 62.76) * mm});
            skLineSegment(sketch, "E2850", {"start": v(-28.45, 62.76) * mm, "end": v(-28.54, 62.82) * mm});
            skLineSegment(sketch, "E2851", {"start": v(-28.54, 62.82) * mm, "end": v(-28.62, 62.88) * mm});
            skLineSegment(sketch, "E2852", {"start": v(-28.62, 62.88) * mm, "end": v(-28.69, 62.96) * mm});
            skLineSegment(sketch, "E2853", {"start": v(-28.69, 62.96) * mm, "end": v(-28.74, 63.04) * mm});
            skLineSegment(sketch, "E2854", {"start": v(-28.74, 63.04) * mm, "end": v(-28.83, 63.1) * mm});
            skLineSegment(sketch, "E2855", {"start": v(-28.83, 63.1) * mm, "end": v(-28.93, 63.09) * mm});
            skLineSegment(sketch, "E2856", {"start": v(-28.93, 63.09) * mm, "end": v(-29.18, 62.97) * mm});
            skLineSegment(sketch, "E2857", {"start": v(-29.18, 62.97) * mm, "end": v(-29.26, 62.9) * mm});
            skLineSegment(sketch, "E2858", {"start": v(-29.26, 62.9) * mm, "end": v(-29.27, 62.8) * mm});
            skLineSegment(sketch, "E2859", {"start": v(-29.27, 62.8) * mm, "end": v(-29.24, 62.7) * mm});
            skLineSegment(sketch, "E2860", {"start": v(-29.24, 62.7) * mm, "end": v(-29.23, 62.6) * mm});
            skLineSegment(sketch, "E2861", {"start": v(-29.23, 62.6) * mm, "end": v(-29.23, 62.5) * mm});
            skLineSegment(sketch, "E2862", {"start": v(-29.23, 62.5) * mm, "end": v(-29.24, 62.4) * mm});
            skLineSegment(sketch, "E2863", {"start": v(-29.24, 62.4) * mm, "end": v(-29.3, 62.28) * mm});
            skLineSegment(sketch, "E2864", {"start": v(-29.3, 62.28) * mm, "end": v(-29.37, 62.17) * mm});
            skLineSegment(sketch, "E2865", {"start": v(-29.37, 62.17) * mm, "end": v(-29.46, 62.08) * mm});
            skLineSegment(sketch, "E2866", {"start": v(-29.46, 62.08) * mm, "end": v(-29.58, 62.01) * mm});
            skLineSegment(sketch, "E2867", {"start": v(-29.58, 62.01) * mm, "end": v(-29.7, 61.97) * mm});
            skLineSegment(sketch, "E2868", {"start": v(-29.7, 61.97) * mm, "end": v(-29.83, 61.95) * mm});
            skLineSegment(sketch, "E2869", {"start": v(-29.83, 61.95) * mm, "end": v(-29.96, 61.96) * mm});
            skLineSegment(sketch, "E2870", {"start": v(-29.96, 61.96) * mm, "end": v(-30.09, 62) * mm});
            skLineSegment(sketch, "E2871", {"start": v(-30.09, 62) * mm, "end": v(-30.17, 62.05) * mm});
            skLineSegment(sketch, "E2872", {"start": v(-30.17, 62.05) * mm, "end": v(-30.25, 62.11) * mm});
            skLineSegment(sketch, "E2873", {"start": v(-30.25, 62.11) * mm, "end": v(-30.32, 62.19) * mm});
            skLineSegment(sketch, "E2874", {"start": v(-30.32, 62.19) * mm, "end": v(-30.38, 62.27) * mm});
            skLineSegment(sketch, "E2875", {"start": v(-30.38, 62.27) * mm, "end": v(-30.47, 62.32) * mm});
            skLineSegment(sketch, "E2876", {"start": v(-30.47, 62.32) * mm, "end": v(-30.57, 62.3) * mm});
            skLineSegment(sketch, "E2877", {"start": v(-30.57, 62.3) * mm, "end": v(-30.82, 62.19) * mm});
            skLineSegment(sketch, "E2878", {"start": v(-30.82, 62.19) * mm, "end": v(-30.9, 62.11) * mm});
            skLineSegment(sketch, "E2879", {"start": v(-30.9, 62.11) * mm, "end": v(-30.9, 62.01) * mm});
            skLineSegment(sketch, "E2880", {"start": v(-30.9, 62.01) * mm, "end": v(-30.88, 61.91) * mm});
            skLineSegment(sketch, "E2881", {"start": v(-30.88, 61.91) * mm, "end": v(-30.86, 61.81) * mm});
            skLineSegment(sketch, "E2882", {"start": v(-30.86, 61.81) * mm, "end": v(-30.86, 61.71) * mm});
            skLineSegment(sketch, "E2883", {"start": v(-30.86, 61.71) * mm, "end": v(-30.87, 61.6) * mm});
            skLineSegment(sketch, "E2884", {"start": v(-30.87, 61.6) * mm, "end": v(-30.91, 61.49) * mm});
            skLineSegment(sketch, "E2885", {"start": v(-30.91, 61.49) * mm, "end": v(-30.99, 61.38) * mm});
            skLineSegment(sketch, "E2886", {"start": v(-30.99, 61.38) * mm, "end": v(-31.08, 61.29) * mm});
            skLineSegment(sketch, "E2887", {"start": v(-31.08, 61.29) * mm, "end": v(-31.2, 61.22) * mm});
            skLineSegment(sketch, "E2888", {"start": v(-31.2, 61.22) * mm, "end": v(-31.31, 61.17) * mm});
            skLineSegment(sketch, "E2889", {"start": v(-31.31, 61.17) * mm, "end": v(-31.44, 61.15) * mm});
            skLineSegment(sketch, "E2890", {"start": v(-31.44, 61.15) * mm, "end": v(-31.57, 61.15) * mm});
            skLineSegment(sketch, "E2891", {"start": v(-31.57, 61.15) * mm, "end": v(-31.7, 61.19) * mm});
            skLineSegment(sketch, "E2892", {"start": v(-31.7, 61.19) * mm, "end": v(-31.79, 61.24) * mm});
            skLineSegment(sketch, "E2893", {"start": v(-31.79, 61.24) * mm, "end": v(-31.87, 61.3) * mm});
            skLineSegment(sketch, "E2894", {"start": v(-31.87, 61.3) * mm, "end": v(-31.94, 61.37) * mm});
            skLineSegment(sketch, "E2895", {"start": v(-31.94, 61.37) * mm, "end": v(-32, 61.45) * mm});
            skLineSegment(sketch, "E2896", {"start": v(-32, 61.45) * mm, "end": v(-32.09, 61.5) * mm});
            skLineSegment(sketch, "E2897", {"start": v(-32.09, 61.5) * mm, "end": v(-32.2, 61.49) * mm});
            skLineSegment(sketch, "E2898", {"start": v(-32.2, 61.49) * mm, "end": v(-32.44, 61.36) * mm});
            skLineSegment(sketch, "E2899", {"start": v(-32.44, 61.36) * mm, "end": v(-32.51, 61.28) * mm});
            skLineSegment(sketch, "E2900", {"start": v(-32.51, 61.28) * mm, "end": v(-32.51, 61.18) * mm});
            skLineSegment(sketch, "E2901", {"start": v(-32.51, 61.18) * mm, "end": v(-32.49, 61.08) * mm});
            skLineSegment(sketch, "E2902", {"start": v(-32.49, 61.08) * mm, "end": v(-32.47, 60.99) * mm});
            skLineSegment(sketch, "E2903", {"start": v(-32.47, 60.99) * mm, "end": v(-32.46, 60.88) * mm});
            skLineSegment(sketch, "E2904", {"start": v(-32.46, 60.88) * mm, "end": v(-32.47, 60.78) * mm});
            skLineSegment(sketch, "E2905", {"start": v(-32.47, 60.78) * mm, "end": v(-32.51, 60.66) * mm});
            skLineSegment(sketch, "E2906", {"start": v(-32.51, 60.66) * mm, "end": v(-32.58, 60.55) * mm});
            skLineSegment(sketch, "E2907", {"start": v(-32.58, 60.55) * mm, "end": v(-32.67, 60.45) * mm});
            skLineSegment(sketch, "E2908", {"start": v(-32.67, 60.45) * mm, "end": v(-32.78, 60.38) * mm});
            skLineSegment(sketch, "E2909", {"start": v(-32.78, 60.38) * mm, "end": v(-32.9, 60.33) * mm});
            skLineSegment(sketch, "E2910", {"start": v(-32.9, 60.33) * mm, "end": v(-33.03, 60.3) * mm});
            skLineSegment(sketch, "E2911", {"start": v(-33.03, 60.3) * mm, "end": v(-33.16, 60.3) * mm});
            skLineSegment(sketch, "E2912", {"start": v(-33.16, 60.3) * mm, "end": v(-33.3, 60.34) * mm});
            skLineSegment(sketch, "E2913", {"start": v(-33.3, 60.34) * mm, "end": v(-33.38, 60.39) * mm});
            skLineSegment(sketch, "E2914", {"start": v(-33.38, 60.39) * mm, "end": v(-33.46, 60.45) * mm});
            skLineSegment(sketch, "E2915", {"start": v(-33.46, 60.45) * mm, "end": v(-33.54, 60.51) * mm});
            skLineSegment(sketch, "E2916", {"start": v(-33.54, 60.51) * mm, "end": v(-33.6, 60.6) * mm});
            skLineSegment(sketch, "E2917", {"start": v(-33.6, 60.6) * mm, "end": v(-33.69, 60.64) * mm});
            skLineSegment(sketch, "E2918", {"start": v(-33.69, 60.64) * mm, "end": v(-33.8, 60.62) * mm});
            skLineSegment(sketch, "E2919", {"start": v(-33.8, 60.62) * mm, "end": v(-34.03, 60.49) * mm});
            skLineSegment(sketch, "E2920", {"start": v(-34.03, 60.49) * mm, "end": v(-34.1, 60.4) * mm});
            skLineSegment(sketch, "E2921", {"start": v(-34.1, 60.4) * mm, "end": v(-34.1, 60.3) * mm});
            skLineSegment(sketch, "E2922", {"start": v(-34.1, 60.3) * mm, "end": v(-34.07, 60.21) * mm});
            skLineSegment(sketch, "E2923", {"start": v(-34.07, 60.21) * mm, "end": v(-34.05, 60.11) * mm});
            skLineSegment(sketch, "E2924", {"start": v(-34.05, 60.11) * mm, "end": v(-34.05, 60.01) * mm});
            skLineSegment(sketch, "E2925", {"start": v(-34.05, 60.01) * mm, "end": v(-34.05, 59.9) * mm});
            skLineSegment(sketch, "E2926", {"start": v(-34.05, 59.9) * mm, "end": v(-34.09, 59.78) * mm});
            skLineSegment(sketch, "E2927", {"start": v(-34.09, 59.78) * mm, "end": v(-34.16, 59.67) * mm});
            skLineSegment(sketch, "E2928", {"start": v(-34.16, 59.67) * mm, "end": v(-34.24, 59.58) * mm});
            skLineSegment(sketch, "E2929", {"start": v(-34.24, 59.58) * mm, "end": v(-34.35, 59.5) * mm});
            skLineSegment(sketch, "E2930", {"start": v(-34.35, 59.5) * mm, "end": v(-34.47, 59.44) * mm});
            skLineSegment(sketch, "E2931", {"start": v(-34.47, 59.44) * mm, "end": v(-34.6, 59.42) * mm});
            skLineSegment(sketch, "E2932", {"start": v(-34.6, 59.42) * mm, "end": v(-34.73, 59.41) * mm});
            skLineSegment(sketch, "E2933", {"start": v(-34.73, 59.41) * mm, "end": v(-34.86, 59.44) * mm});
            skLineSegment(sketch, "E2934", {"start": v(-34.86, 59.44) * mm, "end": v(-34.95, 59.5) * mm});
            skLineSegment(sketch, "E2935", {"start": v(-34.95, 59.5) * mm, "end": v(-35.03, 59.55) * mm});
            skLineSegment(sketch, "E2936", {"start": v(-35.03, 59.55) * mm, "end": v(-35.1, 59.62) * mm});
            skLineSegment(sketch, "E2937", {"start": v(-35.1, 59.62) * mm, "end": v(-35.18, 59.7) * mm});
            skLineSegment(sketch, "E2938", {"start": v(-35.18, 59.7) * mm, "end": v(-35.26, 59.74) * mm});
            skLineSegment(sketch, "E2939", {"start": v(-35.26, 59.74) * mm, "end": v(-35.37, 59.72) * mm});
            skLineSegment(sketch, "E2940", {"start": v(-35.37, 59.72) * mm, "end": v(-35.6, 59.58) * mm});
            skLineSegment(sketch, "E2941", {"start": v(-35.6, 59.58) * mm, "end": v(-35.67, 59.5) * mm});
            skLineSegment(sketch, "E2942", {"start": v(-35.67, 59.5) * mm, "end": v(-35.67, 59.4) * mm});
            skLineSegment(sketch, "E2943", {"start": v(-35.67, 59.4) * mm, "end": v(-35.64, 59.3) * mm});
            skLineSegment(sketch, "E2944", {"start": v(-35.64, 59.3) * mm, "end": v(-35.62, 59.2) * mm});
            skLineSegment(sketch, "E2945", {"start": v(-35.62, 59.2) * mm, "end": v(-35.6, 59.1) * mm});
            skLineSegment(sketch, "E2946", {"start": v(-35.6, 59.1) * mm, "end": v(-35.6, 59) * mm});
            skLineSegment(sketch, "E2947", {"start": v(-35.6, 59) * mm, "end": v(-35.64, 58.87) * mm});
            skLineSegment(sketch, "E2948", {"start": v(-35.64, 58.87) * mm, "end": v(-35.7, 58.76) * mm});
            skLineSegment(sketch, "E2949", {"start": v(-35.7, 58.76) * mm, "end": v(-35.8, 58.66) * mm});
            skLineSegment(sketch, "E2950", {"start": v(-35.8, 58.66) * mm, "end": v(-35.9, 58.58) * mm});
            skLineSegment(sketch, "E2951", {"start": v(-35.9, 58.58) * mm, "end": v(-36.02, 58.52) * mm});
            skLineSegment(sketch, "E2952", {"start": v(-36.02, 58.52) * mm, "end": v(-36.14, 58.49) * mm});
            skLineSegment(sketch, "E2953", {"start": v(-36.14, 58.49) * mm, "end": v(-36.27, 58.49) * mm});
            skLineSegment(sketch, "E2954", {"start": v(-36.27, 58.49) * mm, "end": v(-36.4, 58.51) * mm});
            skLineSegment(sketch, "E2955", {"start": v(-36.4, 58.51) * mm, "end": v(-36.5, 58.56) * mm});
            skLineSegment(sketch, "E2956", {"start": v(-36.5, 58.56) * mm, "end": v(-36.58, 58.61) * mm});
            skLineSegment(sketch, "E2957", {"start": v(-36.58, 58.61) * mm, "end": v(-36.66, 58.68) * mm});
            skLineSegment(sketch, "E2958", {"start": v(-36.66, 58.68) * mm, "end": v(-36.73, 58.75) * mm});
            skLineSegment(sketch, "E2959", {"start": v(-36.73, 58.75) * mm, "end": v(-36.81, 58.8) * mm});
            skLineSegment(sketch, "E2960", {"start": v(-36.81, 58.8) * mm, "end": v(-36.92, 58.77) * mm});
            skLineSegment(sketch, "E2961", {"start": v(-36.92, 58.77) * mm, "end": v(-37.15, 58.62) * mm});
            skLineSegment(sketch, "E2962", {"start": v(-37.15, 58.62) * mm, "end": v(-37.22, 58.54) * mm});
            skLineSegment(sketch, "E2963", {"start": v(-37.22, 58.54) * mm, "end": v(-37.21, 58.44) * mm});
            skLineSegment(sketch, "E2964", {"start": v(-37.21, 58.44) * mm, "end": v(-37.18, 58.35) * mm});
            skLineSegment(sketch, "E2965", {"start": v(-37.18, 58.35) * mm, "end": v(-37.15, 58.25) * mm});
            skLineSegment(sketch, "E2966", {"start": v(-37.15, 58.25) * mm, "end": v(-37.14, 58.15) * mm});
            skLineSegment(sketch, "E2967", {"start": v(-37.14, 58.15) * mm, "end": v(-37.14, 58.05) * mm});
            skLineSegment(sketch, "E2968", {"start": v(-37.14, 58.05) * mm, "end": v(-37.17, 57.92) * mm});
            skLineSegment(sketch, "E2969", {"start": v(-37.17, 57.92) * mm, "end": v(-37.23, 57.8) * mm});
            skLineSegment(sketch, "E2970", {"start": v(-37.23, 57.8) * mm, "end": v(-37.32, 57.7) * mm});
            skLineSegment(sketch, "E2971", {"start": v(-37.32, 57.7) * mm, "end": v(-37.42, 57.62) * mm});
            skLineSegment(sketch, "E2972", {"start": v(-37.42, 57.62) * mm, "end": v(-37.54, 57.56) * mm});
            skLineSegment(sketch, "E2973", {"start": v(-37.54, 57.56) * mm, "end": v(-37.66, 57.52) * mm});
            skLineSegment(sketch, "E2974", {"start": v(-37.66, 57.52) * mm, "end": v(-37.8, 57.52) * mm});
            skLineSegment(sketch, "E2975", {"start": v(-37.8, 57.52) * mm, "end": v(-37.92, 57.54) * mm});
            skLineSegment(sketch, "E2976", {"start": v(-37.92, 57.54) * mm, "end": v(-38.02, 57.58) * mm});
            skLineSegment(sketch, "E2977", {"start": v(-38.02, 57.58) * mm, "end": v(-38.1, 57.63) * mm});
            skLineSegment(sketch, "E2978", {"start": v(-38.1, 57.63) * mm, "end": v(-38.18, 57.7) * mm});
            skLineSegment(sketch, "E2979", {"start": v(-38.18, 57.7) * mm, "end": v(-38.25, 57.77) * mm});
            skLineSegment(sketch, "E2980", {"start": v(-38.25, 57.77) * mm, "end": v(-38.34, 57.81) * mm});
            skLineSegment(sketch, "E2981", {"start": v(-38.34, 57.81) * mm, "end": v(-38.44, 57.78) * mm});
            skLineSegment(sketch, "E2982", {"start": v(-38.44, 57.78) * mm, "end": v(-38.67, 57.63) * mm});
            skLineSegment(sketch, "E2983", {"start": v(-38.67, 57.63) * mm, "end": v(-38.74, 57.55) * mm});
            skLineSegment(sketch, "E2984", {"start": v(-38.74, 57.55) * mm, "end": v(-38.73, 57.45) * mm});
            skLineSegment(sketch, "E2985", {"start": v(-38.73, 57.45) * mm, "end": v(-38.7, 57.35) * mm});
            skLineSegment(sketch, "E2986", {"start": v(-38.7, 57.35) * mm, "end": v(-38.67, 57.26) * mm});
            skLineSegment(sketch, "E2987", {"start": v(-38.67, 57.26) * mm, "end": v(-38.65, 57.16) * mm});
            skLineSegment(sketch, "E2988", {"start": v(-38.65, 57.16) * mm, "end": v(-38.65, 57.05) * mm});
            skLineSegment(sketch, "E2989", {"start": v(-38.65, 57.05) * mm, "end": v(-38.67, 56.93) * mm});
            skLineSegment(sketch, "E2990", {"start": v(-38.67, 56.93) * mm, "end": v(-38.73, 56.8) * mm});
            skLineSegment(sketch, "E2991", {"start": v(-38.73, 56.8) * mm, "end": v(-38.81, 56.7) * mm});
            skLineSegment(sketch, "E2992", {"start": v(-38.81, 56.7) * mm, "end": v(-38.91, 56.62) * mm});
            skLineSegment(sketch, "E2993", {"start": v(-38.91, 56.62) * mm, "end": v(-39.03, 56.56) * mm});
            skLineSegment(sketch, "E2994", {"start": v(-39.03, 56.56) * mm, "end": v(-39.16, 56.52) * mm});
            skLineSegment(sketch, "E2995", {"start": v(-39.16, 56.52) * mm, "end": v(-39.29, 56.5) * mm});
            skLineSegment(sketch, "E2996", {"start": v(-39.29, 56.5) * mm, "end": v(-39.41, 56.53) * mm});
            skLineSegment(sketch, "E2997", {"start": v(-39.41, 56.53) * mm, "end": v(-39.5, 56.57) * mm});
            skLineSegment(sketch, "E2998", {"start": v(-39.5, 56.57) * mm, "end": v(-39.6, 56.62) * mm});
            skLineSegment(sketch, "E2999", {"start": v(-39.6, 56.62) * mm, "end": v(-39.68, 56.68) * mm});
            skLineSegment(sketch, "E3000", {"start": v(-39.68, 56.68) * mm, "end": v(-39.75, 56.75) * mm});
            skLineSegment(sketch, "E3001", {"start": v(-39.75, 56.75) * mm, "end": v(-39.84, 56.79) * mm});
            skLineSegment(sketch, "E3002", {"start": v(-39.84, 56.79) * mm, "end": v(-39.94, 56.76) * mm});
            skLineSegment(sketch, "E3003", {"start": v(-39.94, 56.76) * mm, "end": v(-40.17, 56.6) * mm});
            skLineSegment(sketch, "E3004", {"start": v(-40.17, 56.6) * mm, "end": v(-40.23, 56.51) * mm});
            skLineSegment(sketch, "E3005", {"start": v(-40.23, 56.51) * mm, "end": v(-40.22, 56.41) * mm});
            skLineSegment(sketch, "E3006", {"start": v(-40.22, 56.41) * mm, "end": v(-40.18, 56.32) * mm});
            skLineSegment(sketch, "E3007", {"start": v(-40.18, 56.32) * mm, "end": v(-40.15, 56.23) * mm});
            skLineSegment(sketch, "E3008", {"start": v(-40.15, 56.23) * mm, "end": v(-40.13, 56.13) * mm});
            skLineSegment(sketch, "E3009", {"start": v(-40.13, 56.13) * mm, "end": v(-40.13, 56.02) * mm});
            skLineSegment(sketch, "E3010", {"start": v(-40.13, 56.02) * mm, "end": v(-40.15, 55.9) * mm});
            skLineSegment(sketch, "E3011", {"start": v(-40.15, 55.9) * mm, "end": v(-40.2, 55.78) * mm});
            skLineSegment(sketch, "E3012", {"start": v(-40.2, 55.78) * mm, "end": v(-40.28, 55.67) * mm});
            skLineSegment(sketch, "E3013", {"start": v(-40.28, 55.67) * mm, "end": v(-40.38, 55.58) * mm});
            skLineSegment(sketch, "E3014", {"start": v(-40.38, 55.58) * mm, "end": v(-40.5, 55.52) * mm});
            skLineSegment(sketch, "E3015", {"start": v(-40.5, 55.52) * mm, "end": v(-40.62, 55.47) * mm});
            skLineSegment(sketch, "E3016", {"start": v(-40.62, 55.47) * mm, "end": v(-40.75, 55.46) * mm});
            skLineSegment(sketch, "E3017", {"start": v(-40.75, 55.46) * mm, "end": v(-40.88, 55.47) * mm});
            skLineSegment(sketch, "E3018", {"start": v(-40.88, 55.47) * mm, "end": v(-40.98, 55.51) * mm});
            skLineSegment(sketch, "E3019", {"start": v(-40.98, 55.51) * mm, "end": v(-41.07, 55.56) * mm});
            skLineSegment(sketch, "E3020", {"start": v(-41.07, 55.56) * mm, "end": v(-41.15, 55.62) * mm});
            skLineSegment(sketch, "E3021", {"start": v(-41.15, 55.62) * mm, "end": v(-41.22, 55.69) * mm});
            skLineSegment(sketch, "E3022", {"start": v(-41.22, 55.69) * mm, "end": v(-41.31, 55.73) * mm});
            skLineSegment(sketch, "E3023", {"start": v(-41.31, 55.73) * mm, "end": v(-41.42, 55.7) * mm});
            skLineSegment(sketch, "E3024", {"start": v(-41.42, 55.7) * mm, "end": v(-41.64, 55.53) * mm});
            skLineSegment(sketch, "E3025", {"start": v(-41.64, 55.53) * mm, "end": v(-41.7, 55.44) * mm});
            skLineSegment(sketch, "E3026", {"start": v(-41.7, 55.44) * mm, "end": v(-41.69, 55.34) * mm});
            skLineSegment(sketch, "E3027", {"start": v(-41.69, 55.34) * mm, "end": v(-41.64, 55.25) * mm});
            skLineSegment(sketch, "E3028", {"start": v(-41.64, 55.25) * mm, "end": v(-41.6, 55.16) * mm});
            skLineSegment(sketch, "E3029", {"start": v(-41.6, 55.16) * mm, "end": v(-41.59, 55.06) * mm});
            skLineSegment(sketch, "E3030", {"start": v(-41.59, 55.06) * mm, "end": v(-41.58, 54.95) * mm});
            skLineSegment(sketch, "E3031", {"start": v(-41.58, 54.95) * mm, "end": v(-41.6, 54.82) * mm});
            skLineSegment(sketch, "E3032", {"start": v(-41.6, 54.82) * mm, "end": v(-41.65, 54.7) * mm});
            skLineSegment(sketch, "E3033", {"start": v(-41.65, 54.7) * mm, "end": v(-41.73, 54.6) * mm});
            skLineSegment(sketch, "E3034", {"start": v(-41.73, 54.6) * mm, "end": v(-41.82, 54.5) * mm});
            skLineSegment(sketch, "E3035", {"start": v(-41.82, 54.5) * mm, "end": v(-41.94, 54.44) * mm});
            skLineSegment(sketch, "E3036", {"start": v(-41.94, 54.44) * mm, "end": v(-42.06, 54.4) * mm});
            skLineSegment(sketch, "E3037", {"start": v(-42.06, 54.4) * mm, "end": v(-42.19, 54.37) * mm});
            skLineSegment(sketch, "E3038", {"start": v(-42.19, 54.37) * mm, "end": v(-42.32, 54.38) * mm});
            skLineSegment(sketch, "E3039", {"start": v(-42.32, 54.38) * mm, "end": v(-42.42, 54.42) * mm});
            skLineSegment(sketch, "E3040", {"start": v(-42.42, 54.42) * mm, "end": v(-42.5, 54.47) * mm});
            skLineSegment(sketch, "E3041", {"start": v(-42.5, 54.47) * mm, "end": v(-42.6, 54.52) * mm});
            skLineSegment(sketch, "E3042", {"start": v(-42.6, 54.52) * mm, "end": v(-42.67, 54.59) * mm});
            skLineSegment(sketch, "E3043", {"start": v(-42.67, 54.59) * mm, "end": v(-42.76, 54.62) * mm});
            skLineSegment(sketch, "E3044", {"start": v(-42.76, 54.62) * mm, "end": v(-42.86, 54.59) * mm});
            skLineSegment(sketch, "E3045", {"start": v(-42.86, 54.59) * mm, "end": v(-43.08, 54.42) * mm});
            skLineSegment(sketch, "E3046", {"start": v(-43.08, 54.42) * mm, "end": v(-43.13, 54.33) * mm});
            skLineSegment(sketch, "E3047", {"start": v(-43.13, 54.33) * mm, "end": v(-43.12, 54.23) * mm});
            skLineSegment(sketch, "E3048", {"start": v(-43.12, 54.23) * mm, "end": v(-43.07, 54.14) * mm});
            skLineSegment(sketch, "E3049", {"start": v(-43.07, 54.14) * mm, "end": v(-43.04, 54.05) * mm});
            skLineSegment(sketch, "E3050", {"start": v(-43.04, 54.05) * mm, "end": v(-43.02, 53.95) * mm});
            skLineSegment(sketch, "E3051", {"start": v(-43.02, 53.95) * mm, "end": v(-43, 53.85) * mm});
            skLineSegment(sketch, "E3052", {"start": v(-43, 53.85) * mm, "end": v(-43.02, 53.72) * mm});
            skLineSegment(sketch, "E3053", {"start": v(-43.02, 53.72) * mm, "end": v(-43.07, 53.6) * mm});
            skLineSegment(sketch, "E3054", {"start": v(-43.07, 53.6) * mm, "end": v(-43.14, 53.49) * mm});
            skLineSegment(sketch, "E3055", {"start": v(-43.14, 53.49) * mm, "end": v(-43.24, 53.4) * mm});
            skLineSegment(sketch, "E3056", {"start": v(-43.24, 53.4) * mm, "end": v(-43.35, 53.32) * mm});
            skLineSegment(sketch, "E3057", {"start": v(-43.35, 53.32) * mm, "end": v(-43.47, 53.27) * mm});
            skLineSegment(sketch, "E3058", {"start": v(-43.47, 53.27) * mm, "end": v(-43.6, 53.25) * mm});
            skLineSegment(sketch, "E3059", {"start": v(-43.6, 53.25) * mm, "end": v(-43.73, 53.26) * mm});
            skLineSegment(sketch, "E3060", {"start": v(-43.73, 53.26) * mm, "end": v(-43.83, 53.3) * mm});
            skLineSegment(sketch, "E3061", {"start": v(-43.83, 53.3) * mm, "end": v(-43.92, 53.34) * mm});
            skLineSegment(sketch, "E3062", {"start": v(-43.92, 53.34) * mm, "end": v(-44, 53.39) * mm});
            skLineSegment(sketch, "E3063", {"start": v(-44, 53.39) * mm, "end": v(-44.08, 53.45) * mm});
            skLineSegment(sketch, "E3064", {"start": v(-44.08, 53.45) * mm, "end": v(-44.17, 53.49) * mm});
            skLineSegment(sketch, "E3065", {"start": v(-44.17, 53.49) * mm, "end": v(-44.27, 53.45) * mm});
            skLineSegment(sketch, "E3066", {"start": v(-44.27, 53.45) * mm, "end": v(-44.49, 53.27) * mm});
            skLineSegment(sketch, "E3067", {"start": v(-44.49, 53.27) * mm, "end": v(-44.54, 53.18) * mm});
            skLineSegment(sketch, "E3068", {"start": v(-44.54, 53.18) * mm, "end": v(-44.52, 53.08) * mm});
            skLineSegment(sketch, "E3069", {"start": v(-44.52, 53.08) * mm, "end": v(-44.48, 53) * mm});
            skLineSegment(sketch, "E3070", {"start": v(-44.48, 53) * mm, "end": v(-44.44, 52.9) * mm});
            skLineSegment(sketch, "E3071", {"start": v(-44.44, 52.9) * mm, "end": v(-44.41, 52.8) * mm});
            skLineSegment(sketch, "E3072", {"start": v(-44.41, 52.8) * mm, "end": v(-44.4, 52.7) * mm});
            skLineSegment(sketch, "E3073", {"start": v(-44.4, 52.7) * mm, "end": v(-44.41, 52.57) * mm});
            skLineSegment(sketch, "E3074", {"start": v(-44.41, 52.57) * mm, "end": v(-44.46, 52.45) * mm});
            skLineSegment(sketch, "E3075", {"start": v(-44.46, 52.45) * mm, "end": v(-44.53, 52.34) * mm});
            skLineSegment(sketch, "E3076", {"start": v(-44.53, 52.34) * mm, "end": v(-44.62, 52.24) * mm});
            skLineSegment(sketch, "E3077", {"start": v(-44.62, 52.24) * mm, "end": v(-44.73, 52.17) * mm});
            skLineSegment(sketch, "E3078", {"start": v(-44.73, 52.17) * mm, "end": v(-44.85, 52.12) * mm});
            skLineSegment(sketch, "E3079", {"start": v(-44.85, 52.12) * mm, "end": v(-44.98, 52.1) * mm});
            skLineSegment(sketch, "E3080", {"start": v(-44.98, 52.1) * mm, "end": v(-45.1, 52.1) * mm});
            skLineSegment(sketch, "E3081", {"start": v(-45.1, 52.1) * mm, "end": v(-45.2, 52.13) * mm});
            skLineSegment(sketch, "E3082", {"start": v(-45.2, 52.13) * mm, "end": v(-45.3, 52.17) * mm});
            skLineSegment(sketch, "E3083", {"start": v(-45.3, 52.17) * mm, "end": v(-45.39, 52.22) * mm});
            skLineSegment(sketch, "E3084", {"start": v(-45.39, 52.22) * mm, "end": v(-45.46, 52.28) * mm});
            skLineSegment(sketch, "E3085", {"start": v(-45.46, 52.28) * mm, "end": v(-45.56, 52.31) * mm});
            skLineSegment(sketch, "E3086", {"start": v(-45.56, 52.31) * mm, "end": v(-45.66, 52.27) * mm});
            skLineSegment(sketch, "E3087", {"start": v(-45.66, 52.27) * mm, "end": v(-45.86, 52.1) * mm});
            skLineSegment(sketch, "E3088", {"start": v(-45.86, 52.1) * mm, "end": v(-45.92, 52) * mm});
            skLineSegment(sketch, "E3089", {"start": v(-45.92, 52) * mm, "end": v(-45.9, 51.9) * mm});
            skLineSegment(sketch, "E3090", {"start": v(-45.9, 51.9) * mm, "end": v(-45.85, 51.81) * mm});
            skLineSegment(sketch, "E3091", {"start": v(-45.85, 51.81) * mm, "end": v(-45.8, 51.72) * mm});
            skLineSegment(sketch, "E3092", {"start": v(-45.8, 51.72) * mm, "end": v(-45.78, 51.62) * mm});
            skLineSegment(sketch, "E3093", {"start": v(-45.78, 51.62) * mm, "end": v(-45.76, 51.52) * mm});
            skLineSegment(sketch, "E3094", {"start": v(-45.76, 51.52) * mm, "end": v(-45.77, 51.4) * mm});
            skLineSegment(sketch, "E3095", {"start": v(-45.77, 51.4) * mm, "end": v(-45.82, 51.27) * mm});
            skLineSegment(sketch, "E3096", {"start": v(-45.82, 51.27) * mm, "end": v(-45.88, 51.15) * mm});
            skLineSegment(sketch, "E3097", {"start": v(-45.88, 51.15) * mm, "end": v(-45.97, 51.06) * mm});
            skLineSegment(sketch, "E3098", {"start": v(-45.97, 51.06) * mm, "end": v(-46.08, 50.98) * mm});
            skLineSegment(sketch, "E3099", {"start": v(-46.08, 50.98) * mm, "end": v(-46.2, 50.92) * mm});
            skLineSegment(sketch, "E3100", {"start": v(-46.2, 50.92) * mm, "end": v(-46.32, 50.9) * mm});
            skLineSegment(sketch, "E3101", {"start": v(-46.32, 50.9) * mm, "end": v(-46.46, 50.9) * mm});
            skLineSegment(sketch, "E3102", {"start": v(-46.46, 50.9) * mm, "end": v(-46.55, 50.93) * mm});
            skLineSegment(sketch, "E3103", {"start": v(-46.55, 50.93) * mm, "end": v(-46.65, 50.96) * mm});
            skLineSegment(sketch, "E3104", {"start": v(-46.65, 50.96) * mm, "end": v(-46.74, 51.01) * mm});
            skLineSegment(sketch, "E3105", {"start": v(-46.74, 51.01) * mm, "end": v(-46.82, 51.07) * mm});
            skLineSegment(sketch, "E3106", {"start": v(-46.82, 51.07) * mm, "end": v(-46.91, 51.1) * mm});
            skLineSegment(sketch, "E3107", {"start": v(-46.91, 51.1) * mm, "end": v(-47.01, 51.06) * mm});
            skLineSegment(sketch, "E3108", {"start": v(-47.01, 51.06) * mm, "end": v(-47.21, 50.87) * mm});
            skLineSegment(sketch, "E3109", {"start": v(-47.21, 50.87) * mm, "end": v(-47.26, 50.78) * mm});
            skLineSegment(sketch, "E3110", {"start": v(-47.26, 50.78) * mm, "end": v(-47.24, 50.68) * mm});
            skLineSegment(sketch, "E3111", {"start": v(-47.24, 50.68) * mm, "end": v(-47.19, 50.6) * mm});
            skLineSegment(sketch, "E3112", {"start": v(-47.19, 50.6) * mm, "end": v(-47.15, 50.5) * mm});
            skLineSegment(sketch, "E3113", {"start": v(-47.15, 50.5) * mm, "end": v(-47.12, 50.4) * mm});
            skLineSegment(sketch, "E3114", {"start": v(-47.12, 50.4) * mm, "end": v(-47.1, 50.3) * mm});
            skLineSegment(sketch, "E3115", {"start": v(-47.1, 50.3) * mm, "end": v(-47.1, 50.18) * mm});
            skLineSegment(sketch, "E3116", {"start": v(-47.1, 50.18) * mm, "end": v(-47.14, 50.05) * mm});
            skLineSegment(sketch, "E3117", {"start": v(-47.14, 50.05) * mm, "end": v(-47.2, 49.94) * mm});
            skLineSegment(sketch, "E3118", {"start": v(-47.2, 49.94) * mm, "end": v(-47.3, 49.84) * mm});
            skLineSegment(sketch, "E3119", {"start": v(-47.3, 49.84) * mm, "end": v(-47.4, 49.75) * mm});
            skLineSegment(sketch, "E3120", {"start": v(-47.4, 49.75) * mm, "end": v(-47.51, 49.7) * mm});
            skLineSegment(sketch, "E3121", {"start": v(-47.51, 49.7) * mm, "end": v(-47.64, 49.67) * mm});
            skLineSegment(sketch, "E3122", {"start": v(-47.64, 49.67) * mm, "end": v(-47.77, 49.66) * mm});
            skLineSegment(sketch, "E3123", {"start": v(-47.77, 49.66) * mm, "end": v(-47.87, 49.69) * mm});
            skLineSegment(sketch, "E3124", {"start": v(-47.87, 49.69) * mm, "end": v(-47.97, 49.73) * mm});
            skLineSegment(sketch, "E3125", {"start": v(-47.97, 49.73) * mm, "end": v(-48.06, 49.77) * mm});
            skLineSegment(sketch, "E3126", {"start": v(-48.06, 49.77) * mm, "end": v(-48.14, 49.83) * mm});
            skLineSegment(sketch, "E3127", {"start": v(-48.14, 49.83) * mm, "end": v(-48.23, 49.86) * mm});
            skLineSegment(sketch, "E3128", {"start": v(-48.23, 49.86) * mm, "end": v(-48.33, 49.81) * mm});
            skLineSegment(sketch, "E3129", {"start": v(-48.33, 49.81) * mm, "end": v(-48.53, 49.62) * mm});
            skLineSegment(sketch, "E3130", {"start": v(-48.53, 49.62) * mm, "end": v(-48.58, 49.52) * mm});
            skLineSegment(sketch, "E3131", {"start": v(-48.58, 49.52) * mm, "end": v(-48.55, 49.43) * mm});
            skLineSegment(sketch, "E3132", {"start": v(-48.55, 49.43) * mm, "end": v(-48.5, 49.34) * mm});
            skLineSegment(sketch, "E3133", {"start": v(-48.5, 49.34) * mm, "end": v(-48.45, 49.25) * mm});
            skLineSegment(sketch, "E3134", {"start": v(-48.45, 49.25) * mm, "end": v(-48.42, 49.16) * mm});
            skLineSegment(sketch, "E3135", {"start": v(-48.42, 49.16) * mm, "end": v(-48.4, 49.06) * mm});
            skLineSegment(sketch, "E3136", {"start": v(-48.4, 49.06) * mm, "end": v(-48.4, 48.92) * mm});
            skLineSegment(sketch, "E3137", {"start": v(-48.4, 48.92) * mm, "end": v(-48.44, 48.8) * mm});
            skLineSegment(sketch, "E3138", {"start": v(-48.44, 48.8) * mm, "end": v(-48.5, 48.68) * mm});
            skLineSegment(sketch, "E3139", {"start": v(-48.5, 48.68) * mm, "end": v(-48.58, 48.58) * mm});
            skLineSegment(sketch, "E3140", {"start": v(-48.58, 48.58) * mm, "end": v(-48.68, 48.5) * mm});
            skLineSegment(sketch, "E3141", {"start": v(-48.68, 48.5) * mm, "end": v(-48.8, 48.44) * mm});
            skLineSegment(sketch, "E3142", {"start": v(-48.8, 48.44) * mm, "end": v(-48.92, 48.4) * mm});
            skLineSegment(sketch, "E3143", {"start": v(-48.92, 48.4) * mm, "end": v(-49.06, 48.4) * mm});
            skLineSegment(sketch, "E3144", {"start": v(-49.06, 48.4) * mm, "end": v(-49.16, 48.42) * mm});
            skLineSegment(sketch, "E3145", {"start": v(-49.16, 48.42) * mm, "end": v(-49.25, 48.45) * mm});
            skLineSegment(sketch, "E3146", {"start": v(-49.25, 48.45) * mm, "end": v(-49.34, 48.5) * mm});
            skLineSegment(sketch, "E3147", {"start": v(-49.34, 48.5) * mm, "end": v(-49.43, 48.55) * mm});
            skLineSegment(sketch, "E3148", {"start": v(-49.43, 48.55) * mm, "end": v(-49.52, 48.58) * mm});
            skLineSegment(sketch, "E3149", {"start": v(-49.52, 48.58) * mm, "end": v(-49.62, 48.53) * mm});
            skLineSegment(sketch, "E3150", {"start": v(-49.62, 48.53) * mm, "end": v(-49.81, 48.33) * mm});
            skLineSegment(sketch, "E3151", {"start": v(-49.81, 48.33) * mm, "end": v(-49.86, 48.23) * mm});
            skLineSegment(sketch, "E3152", {"start": v(-49.86, 48.23) * mm, "end": v(-49.83, 48.14) * mm});
            skLineSegment(sketch, "E3153", {"start": v(-49.83, 48.14) * mm, "end": v(-49.77, 48.06) * mm});
            skLineSegment(sketch, "E3154", {"start": v(-49.77, 48.06) * mm, "end": v(-49.73, 47.97) * mm});
            skLineSegment(sketch, "E3155", {"start": v(-49.73, 47.97) * mm, "end": v(-49.69, 47.87) * mm});
            skLineSegment(sketch, "E3156", {"start": v(-49.69, 47.87) * mm, "end": v(-49.66, 47.77) * mm});
            skLineSegment(sketch, "E3157", {"start": v(-49.66, 47.77) * mm, "end": v(-49.67, 47.64) * mm});
            skLineSegment(sketch, "E3158", {"start": v(-49.67, 47.64) * mm, "end": v(-49.7, 47.51) * mm});
            skLineSegment(sketch, "E3159", {"start": v(-49.7, 47.51) * mm, "end": v(-49.75, 47.4) * mm});
            skLineSegment(sketch, "E3160", {"start": v(-49.75, 47.4) * mm, "end": v(-49.84, 47.3) * mm});
            skLineSegment(sketch, "E3161", {"start": v(-49.84, 47.3) * mm, "end": v(-49.94, 47.2) * mm});
            skLineSegment(sketch, "E3162", {"start": v(-49.94, 47.2) * mm, "end": v(-50.05, 47.14) * mm});
            skLineSegment(sketch, "E3163", {"start": v(-50.05, 47.14) * mm, "end": v(-50.18, 47.1) * mm});
            skLineSegment(sketch, "E3164", {"start": v(-50.18, 47.1) * mm, "end": v(-50.3, 47.1) * mm});
            skLineSegment(sketch, "E3165", {"start": v(-50.3, 47.1) * mm, "end": v(-50.4, 47.12) * mm});
            skLineSegment(sketch, "E3166", {"start": v(-50.4, 47.12) * mm, "end": v(-50.5, 47.15) * mm});
            skLineSegment(sketch, "E3167", {"start": v(-50.5, 47.15) * mm, "end": v(-50.6, 47.19) * mm});
            skLineSegment(sketch, "E3168", {"start": v(-50.6, 47.19) * mm, "end": v(-50.68, 47.24) * mm});
            skLineSegment(sketch, "E3169", {"start": v(-50.68, 47.24) * mm, "end": v(-50.78, 47.26) * mm});
            skLineSegment(sketch, "E3170", {"start": v(-50.78, 47.26) * mm, "end": v(-50.87, 47.21) * mm});
            skLineSegment(sketch, "E3171", {"start": v(-50.87, 47.21) * mm, "end": v(-51.06, 47.01) * mm});
            skLineSegment(sketch, "E3172", {"start": v(-51.06, 47.01) * mm, "end": v(-51.1, 46.91) * mm});
            skLineSegment(sketch, "E3173", {"start": v(-51.1, 46.91) * mm, "end": v(-51.07, 46.82) * mm});
            skLineSegment(sketch, "E3174", {"start": v(-51.07, 46.82) * mm, "end": v(-51.01, 46.74) * mm});
            skLineSegment(sketch, "E3175", {"start": v(-51.01, 46.74) * mm, "end": v(-50.96, 46.65) * mm});
            skLineSegment(sketch, "E3176", {"start": v(-50.96, 46.65) * mm, "end": v(-50.93, 46.56) * mm});
            skLineSegment(sketch, "E3177", {"start": v(-50.93, 46.56) * mm, "end": v(-50.9, 46.46) * mm});
            skLineSegment(sketch, "E3178", {"start": v(-50.9, 46.46) * mm, "end": v(-50.9, 46.32) * mm});
            skLineSegment(sketch, "E3179", {"start": v(-50.9, 46.32) * mm, "end": v(-50.92, 46.2) * mm});
            skLineSegment(sketch, "E3180", {"start": v(-50.92, 46.2) * mm, "end": v(-50.98, 46.08) * mm});
            skLineSegment(sketch, "E3181", {"start": v(-50.98, 46.08) * mm, "end": v(-51.06, 45.97) * mm});
            skLineSegment(sketch, "E3182", {"start": v(-51.06, 45.97) * mm, "end": v(-51.15, 45.88) * mm});
            skLineSegment(sketch, "E3183", {"start": v(-51.15, 45.88) * mm, "end": v(-51.27, 45.82) * mm});
            skLineSegment(sketch, "E3184", {"start": v(-51.27, 45.82) * mm, "end": v(-51.4, 45.77) * mm});
            skLineSegment(sketch, "E3185", {"start": v(-51.4, 45.77) * mm, "end": v(-51.52, 45.76) * mm});
            skLineSegment(sketch, "E3186", {"start": v(-51.52, 45.76) * mm, "end": v(-51.62, 45.78) * mm});
            skLineSegment(sketch, "E3187", {"start": v(-51.62, 45.78) * mm, "end": v(-51.72, 45.8) * mm});
            skLineSegment(sketch, "E3188", {"start": v(-51.72, 45.8) * mm, "end": v(-51.81, 45.85) * mm});
            skLineSegment(sketch, "E3189", {"start": v(-51.81, 45.85) * mm, "end": v(-51.9, 45.9) * mm});
            skLineSegment(sketch, "E3190", {"start": v(-51.9, 45.9) * mm, "end": v(-52, 45.92) * mm});
            skLineSegment(sketch, "E3191", {"start": v(-52, 45.92) * mm, "end": v(-52.1, 45.86) * mm});
            skLineSegment(sketch, "E3192", {"start": v(-52.1, 45.86) * mm, "end": v(-52.27, 45.66) * mm});
            skLineSegment(sketch, "E3193", {"start": v(-52.27, 45.66) * mm, "end": v(-52.31, 45.56) * mm});
            skLineSegment(sketch, "E3194", {"start": v(-52.31, 45.56) * mm, "end": v(-52.28, 45.46) * mm});
            skLineSegment(sketch, "E3195", {"start": v(-52.28, 45.46) * mm, "end": v(-52.22, 45.39) * mm});
            skLineSegment(sketch, "E3196", {"start": v(-52.22, 45.39) * mm, "end": v(-52.17, 45.3) * mm});
            skLineSegment(sketch, "E3197", {"start": v(-52.17, 45.3) * mm, "end": v(-52.13, 45.2) * mm});
            skLineSegment(sketch, "E3198", {"start": v(-52.13, 45.2) * mm, "end": v(-52.1, 45.1) * mm});
            skLineSegment(sketch, "E3199", {"start": v(-52.1, 45.1) * mm, "end": v(-52.1, 44.98) * mm});
            skLineSegment(sketch, "E3200", {"start": v(-52.1, 44.98) * mm, "end": v(-52.12, 44.85) * mm});
            skLineSegment(sketch, "E3201", {"start": v(-52.12, 44.85) * mm, "end": v(-52.17, 44.73) * mm});
            skLineSegment(sketch, "E3202", {"start": v(-52.17, 44.73) * mm, "end": v(-52.24, 44.62) * mm});
            skLineSegment(sketch, "E3203", {"start": v(-52.24, 44.62) * mm, "end": v(-52.34, 44.53) * mm});
            skLineSegment(sketch, "E3204", {"start": v(-52.34, 44.53) * mm, "end": v(-52.45, 44.46) * mm});
            skLineSegment(sketch, "E3205", {"start": v(-52.45, 44.46) * mm, "end": v(-52.57, 44.41) * mm});
            skLineSegment(sketch, "E3206", {"start": v(-52.57, 44.41) * mm, "end": v(-52.7, 44.4) * mm});
            skLineSegment(sketch, "E3207", {"start": v(-52.7, 44.4) * mm, "end": v(-52.8, 44.41) * mm});
            skLineSegment(sketch, "E3208", {"start": v(-52.8, 44.41) * mm, "end": v(-52.9, 44.44) * mm});
            skLineSegment(sketch, "E3209", {"start": v(-52.9, 44.44) * mm, "end": v(-53, 44.48) * mm});
            skLineSegment(sketch, "E3210", {"start": v(-53, 44.48) * mm, "end": v(-53.08, 44.52) * mm});
            skLineSegment(sketch, "E3211", {"start": v(-53.08, 44.52) * mm, "end": v(-53.18, 44.54) * mm});
            skLineSegment(sketch, "E3212", {"start": v(-53.18, 44.54) * mm, "end": v(-53.27, 44.49) * mm});
            skLineSegment(sketch, "E3213", {"start": v(-53.27, 44.49) * mm, "end": v(-53.45, 44.27) * mm});
            skLineSegment(sketch, "E3214", {"start": v(-53.45, 44.27) * mm, "end": v(-53.49, 44.17) * mm});
            skLineSegment(sketch, "E3215", {"start": v(-53.49, 44.17) * mm, "end": v(-53.45, 44.08) * mm});
            skLineSegment(sketch, "E3216", {"start": v(-53.45, 44.08) * mm, "end": v(-53.39, 44) * mm});
            skLineSegment(sketch, "E3217", {"start": v(-53.39, 44) * mm, "end": v(-53.34, 43.92) * mm});
            skLineSegment(sketch, "E3218", {"start": v(-53.34, 43.92) * mm, "end": v(-53.3, 43.83) * mm});
            skLineSegment(sketch, "E3219", {"start": v(-53.3, 43.83) * mm, "end": v(-53.26, 43.73) * mm});
            skLineSegment(sketch, "E3220", {"start": v(-53.26, 43.73) * mm, "end": v(-53.25, 43.6) * mm});
            skLineSegment(sketch, "E3221", {"start": v(-53.25, 43.6) * mm, "end": v(-53.27, 43.47) * mm});
            skLineSegment(sketch, "E3222", {"start": v(-53.27, 43.47) * mm, "end": v(-53.32, 43.35) * mm});
            skLineSegment(sketch, "E3223", {"start": v(-53.32, 43.35) * mm, "end": v(-53.4, 43.24) * mm});
            skLineSegment(sketch, "E3224", {"start": v(-53.4, 43.24) * mm, "end": v(-53.49, 43.14) * mm});
            skLineSegment(sketch, "E3225", {"start": v(-53.49, 43.14) * mm, "end": v(-53.6, 43.07) * mm});
            skLineSegment(sketch, "E3226", {"start": v(-53.6, 43.07) * mm, "end": v(-53.72, 43.02) * mm});
            skLineSegment(sketch, "E3227", {"start": v(-53.72, 43.02) * mm, "end": v(-53.85, 43) * mm});
            skLineSegment(sketch, "E3228", {"start": v(-53.85, 43) * mm, "end": v(-53.95, 43.02) * mm});
            skLineSegment(sketch, "E3229", {"start": v(-53.95, 43.02) * mm, "end": v(-54.05, 43.04) * mm});
            skLineSegment(sketch, "E3230", {"start": v(-54.05, 43.04) * mm, "end": v(-54.14, 43.07) * mm});
            skLineSegment(sketch, "E3231", {"start": v(-54.14, 43.07) * mm, "end": v(-54.23, 43.12) * mm});
            skLineSegment(sketch, "E3232", {"start": v(-54.23, 43.12) * mm, "end": v(-54.33, 43.13) * mm});
            skLineSegment(sketch, "E3233", {"start": v(-54.33, 43.13) * mm, "end": v(-54.42, 43.08) * mm});
            skLineSegment(sketch, "E3234", {"start": v(-54.42, 43.08) * mm, "end": v(-54.59, 42.86) * mm});
            skLineSegment(sketch, "E3235", {"start": v(-54.59, 42.86) * mm, "end": v(-54.62, 42.76) * mm});
            skLineSegment(sketch, "E3236", {"start": v(-54.62, 42.76) * mm, "end": v(-54.59, 42.67) * mm});
            skLineSegment(sketch, "E3237", {"start": v(-54.59, 42.67) * mm, "end": v(-54.52, 42.6) * mm});
            skLineSegment(sketch, "E3238", {"start": v(-54.52, 42.6) * mm, "end": v(-54.47, 42.5) * mm});
            skLineSegment(sketch, "E3239", {"start": v(-54.47, 42.5) * mm, "end": v(-54.42, 42.42) * mm});
            skLineSegment(sketch, "E3240", {"start": v(-54.42, 42.42) * mm, "end": v(-54.38, 42.32) * mm});
            skLineSegment(sketch, "E3241", {"start": v(-54.38, 42.32) * mm, "end": v(-54.37, 42.19) * mm});
            skLineSegment(sketch, "E3242", {"start": v(-54.37, 42.19) * mm, "end": v(-54.4, 42.06) * mm});
            skLineSegment(sketch, "E3243", {"start": v(-54.4, 42.06) * mm, "end": v(-54.44, 41.94) * mm});
            skLineSegment(sketch, "E3244", {"start": v(-54.44, 41.94) * mm, "end": v(-54.5, 41.82) * mm});
            skLineSegment(sketch, "E3245", {"start": v(-54.5, 41.82) * mm, "end": v(-54.6, 41.73) * mm});
            skLineSegment(sketch, "E3246", {"start": v(-54.6, 41.73) * mm, "end": v(-54.7, 41.65) * mm});
            skLineSegment(sketch, "E3247", {"start": v(-54.7, 41.65) * mm, "end": v(-54.82, 41.6) * mm});
            skLineSegment(sketch, "E3248", {"start": v(-54.82, 41.6) * mm, "end": v(-54.95, 41.58) * mm});
            skLineSegment(sketch, "E3249", {"start": v(-54.95, 41.58) * mm, "end": v(-55.06, 41.59) * mm});
            skLineSegment(sketch, "E3250", {"start": v(-55.06, 41.59) * mm, "end": v(-55.16, 41.6) * mm});
            skLineSegment(sketch, "E3251", {"start": v(-55.16, 41.6) * mm, "end": v(-55.25, 41.64) * mm});
            skLineSegment(sketch, "E3252", {"start": v(-55.25, 41.64) * mm, "end": v(-55.34, 41.69) * mm});
            skLineSegment(sketch, "E3253", {"start": v(-55.34, 41.69) * mm, "end": v(-55.44, 41.7) * mm});
            skLineSegment(sketch, "E3254", {"start": v(-55.44, 41.7) * mm, "end": v(-55.53, 41.64) * mm});
            skLineSegment(sketch, "E3255", {"start": v(-55.53, 41.64) * mm, "end": v(-55.7, 41.42) * mm});
            skLineSegment(sketch, "E3256", {"start": v(-55.7, 41.42) * mm, "end": v(-55.73, 41.31) * mm});
            skLineSegment(sketch, "E3257", {"start": v(-55.73, 41.31) * mm, "end": v(-55.69, 41.22) * mm});
            skLineSegment(sketch, "E3258", {"start": v(-55.69, 41.22) * mm, "end": v(-55.62, 41.15) * mm});
            skLineSegment(sketch, "E3259", {"start": v(-55.62, 41.15) * mm, "end": v(-55.56, 41.07) * mm});
            skLineSegment(sketch, "E3260", {"start": v(-55.56, 41.07) * mm, "end": v(-55.51, 40.98) * mm});
            skLineSegment(sketch, "E3261", {"start": v(-55.51, 40.98) * mm, "end": v(-55.47, 40.88) * mm});
            skLineSegment(sketch, "E3262", {"start": v(-55.47, 40.88) * mm, "end": v(-55.46, 40.75) * mm});
            skLineSegment(sketch, "E3263", {"start": v(-55.46, 40.75) * mm, "end": v(-55.47, 40.62) * mm});
            skLineSegment(sketch, "E3264", {"start": v(-55.47, 40.62) * mm, "end": v(-55.52, 40.5) * mm});
            skLineSegment(sketch, "E3265", {"start": v(-55.52, 40.5) * mm, "end": v(-55.58, 40.38) * mm});
            skLineSegment(sketch, "E3266", {"start": v(-55.58, 40.38) * mm, "end": v(-55.67, 40.28) * mm});
            skLineSegment(sketch, "E3267", {"start": v(-55.67, 40.28) * mm, "end": v(-55.78, 40.2) * mm});
            skLineSegment(sketch, "E3268", {"start": v(-55.78, 40.2) * mm, "end": v(-55.9, 40.15) * mm});
            skLineSegment(sketch, "E3269", {"start": v(-55.9, 40.15) * mm, "end": v(-56.02, 40.13) * mm});
            skLineSegment(sketch, "E3270", {"start": v(-56.02, 40.13) * mm, "end": v(-56.13, 40.13) * mm});
            skLineSegment(sketch, "E3271", {"start": v(-56.13, 40.13) * mm, "end": v(-56.23, 40.15) * mm});
            skLineSegment(sketch, "E3272", {"start": v(-56.23, 40.15) * mm, "end": v(-56.32, 40.18) * mm});
            skLineSegment(sketch, "E3273", {"start": v(-56.32, 40.18) * mm, "end": v(-56.41, 40.22) * mm});
            skLineSegment(sketch, "E3274", {"start": v(-56.41, 40.22) * mm, "end": v(-56.51, 40.23) * mm});
            skLineSegment(sketch, "E3275", {"start": v(-56.51, 40.23) * mm, "end": v(-56.6, 40.17) * mm});
            skLineSegment(sketch, "E3276", {"start": v(-56.6, 40.17) * mm, "end": v(-56.76, 39.94) * mm});
            skLineSegment(sketch, "E3277", {"start": v(-56.76, 39.94) * mm, "end": v(-56.79, 39.84) * mm});
            skLineSegment(sketch, "E3278", {"start": v(-56.79, 39.84) * mm, "end": v(-56.75, 39.75) * mm});
            skLineSegment(sketch, "E3279", {"start": v(-56.75, 39.75) * mm, "end": v(-56.68, 39.68) * mm});
            skLineSegment(sketch, "E3280", {"start": v(-56.68, 39.68) * mm, "end": v(-56.62, 39.6) * mm});
            skLineSegment(sketch, "E3281", {"start": v(-56.62, 39.6) * mm, "end": v(-56.57, 39.5) * mm});
            skLineSegment(sketch, "E3282", {"start": v(-56.57, 39.5) * mm, "end": v(-56.53, 39.41) * mm});
            skLineSegment(sketch, "E3283", {"start": v(-56.53, 39.41) * mm, "end": v(-56.5, 39.29) * mm});
            skLineSegment(sketch, "E3284", {"start": v(-56.5, 39.29) * mm, "end": v(-56.52, 39.16) * mm});
            skLineSegment(sketch, "E3285", {"start": v(-56.52, 39.16) * mm, "end": v(-56.56, 39.03) * mm});
            skLineSegment(sketch, "E3286", {"start": v(-56.56, 39.03) * mm, "end": v(-56.62, 38.91) * mm});
            skLineSegment(sketch, "E3287", {"start": v(-56.62, 38.91) * mm, "end": v(-56.7, 38.81) * mm});
            skLineSegment(sketch, "E3288", {"start": v(-56.7, 38.81) * mm, "end": v(-56.8, 38.73) * mm});
            skLineSegment(sketch, "E3289", {"start": v(-56.8, 38.73) * mm, "end": v(-56.93, 38.67) * mm});
            skLineSegment(sketch, "E3290", {"start": v(-56.93, 38.67) * mm, "end": v(-57.05, 38.65) * mm});
            skLineSegment(sketch, "E3291", {"start": v(-57.05, 38.65) * mm, "end": v(-57.16, 38.65) * mm});
            skLineSegment(sketch, "E3292", {"start": v(-57.16, 38.65) * mm, "end": v(-57.26, 38.67) * mm});
            skLineSegment(sketch, "E3293", {"start": v(-57.26, 38.67) * mm, "end": v(-57.35, 38.7) * mm});
            skLineSegment(sketch, "E3294", {"start": v(-57.35, 38.7) * mm, "end": v(-57.45, 38.73) * mm});
            skLineSegment(sketch, "E3295", {"start": v(-57.45, 38.73) * mm, "end": v(-57.55, 38.74) * mm});
            skLineSegment(sketch, "E3296", {"start": v(-57.55, 38.74) * mm, "end": v(-57.63, 38.67) * mm});
            skLineSegment(sketch, "E3297", {"start": v(-57.63, 38.67) * mm, "end": v(-57.78, 38.44) * mm});
            skLineSegment(sketch, "E3298", {"start": v(-57.78, 38.44) * mm, "end": v(-57.81, 38.34) * mm});
            skLineSegment(sketch, "E3299", {"start": v(-57.81, 38.34) * mm, "end": v(-57.77, 38.25) * mm});
            skLineSegment(sketch, "E3300", {"start": v(-57.77, 38.25) * mm, "end": v(-57.7, 38.18) * mm});
            skLineSegment(sketch, "E3301", {"start": v(-57.7, 38.18) * mm, "end": v(-57.63, 38.1) * mm});
            skLineSegment(sketch, "E3302", {"start": v(-57.63, 38.1) * mm, "end": v(-57.58, 38.02) * mm});
            skLineSegment(sketch, "E3303", {"start": v(-57.58, 38.02) * mm, "end": v(-57.54, 37.92) * mm});
            skLineSegment(sketch, "E3304", {"start": v(-57.54, 37.92) * mm, "end": v(-57.52, 37.8) * mm});
            skLineSegment(sketch, "E3305", {"start": v(-57.52, 37.8) * mm, "end": v(-57.52, 37.66) * mm});
            skLineSegment(sketch, "E3306", {"start": v(-57.52, 37.66) * mm, "end": v(-57.56, 37.54) * mm});
            skLineSegment(sketch, "E3307", {"start": v(-57.56, 37.54) * mm, "end": v(-57.62, 37.42) * mm});
            skLineSegment(sketch, "E3308", {"start": v(-57.62, 37.42) * mm, "end": v(-57.7, 37.32) * mm});
            skLineSegment(sketch, "E3309", {"start": v(-57.7, 37.32) * mm, "end": v(-57.8, 37.23) * mm});
            skLineSegment(sketch, "E3310", {"start": v(-57.8, 37.23) * mm, "end": v(-57.92, 37.17) * mm});
            skLineSegment(sketch, "E3311", {"start": v(-57.92, 37.17) * mm, "end": v(-58.05, 37.14) * mm});
            skLineSegment(sketch, "E3312", {"start": v(-58.05, 37.14) * mm, "end": v(-58.15, 37.14) * mm});
            skLineSegment(sketch, "E3313", {"start": v(-58.15, 37.14) * mm, "end": v(-58.25, 37.15) * mm});
            skLineSegment(sketch, "E3314", {"start": v(-58.25, 37.15) * mm, "end": v(-58.35, 37.18) * mm});
            skLineSegment(sketch, "E3315", {"start": v(-58.35, 37.18) * mm, "end": v(-58.44, 37.21) * mm});
            skLineSegment(sketch, "E3316", {"start": v(-58.44, 37.21) * mm, "end": v(-58.54, 37.22) * mm});
            skLineSegment(sketch, "E3317", {"start": v(-58.54, 37.22) * mm, "end": v(-58.62, 37.15) * mm});
            skLineSegment(sketch, "E3318", {"start": v(-58.62, 37.15) * mm, "end": v(-58.77, 36.92) * mm});
            skLineSegment(sketch, "E3319", {"start": v(-58.77, 36.92) * mm, "end": v(-58.8, 36.82) * mm});
            skLineSegment(sketch, "E3320", {"start": v(-58.8, 36.82) * mm, "end": v(-58.75, 36.73) * mm});
            skLineSegment(sketch, "E3321", {"start": v(-58.75, 36.73) * mm, "end": v(-58.68, 36.66) * mm});
            skLineSegment(sketch, "E3322", {"start": v(-58.68, 36.66) * mm, "end": v(-58.61, 36.58) * mm});
            skLineSegment(sketch, "E3323", {"start": v(-58.61, 36.58) * mm, "end": v(-58.56, 36.5) * mm});
            skLineSegment(sketch, "E3324", {"start": v(-58.56, 36.5) * mm, "end": v(-58.51, 36.4) * mm});
            skLineSegment(sketch, "E3325", {"start": v(-58.51, 36.4) * mm, "end": v(-58.49, 36.27) * mm});
            skLineSegment(sketch, "E3326", {"start": v(-58.49, 36.27) * mm, "end": v(-58.49, 36.14) * mm});
            skLineSegment(sketch, "E3327", {"start": v(-58.49, 36.14) * mm, "end": v(-58.52, 36.02) * mm});
            skLineSegment(sketch, "E3328", {"start": v(-58.52, 36.02) * mm, "end": v(-58.58, 35.9) * mm});
            skLineSegment(sketch, "E3329", {"start": v(-58.58, 35.9) * mm, "end": v(-58.66, 35.8) * mm});
            skLineSegment(sketch, "E3330", {"start": v(-58.66, 35.8) * mm, "end": v(-58.76, 35.7) * mm});
            skLineSegment(sketch, "E3331", {"start": v(-58.76, 35.7) * mm, "end": v(-58.87, 35.64) * mm});
            skLineSegment(sketch, "E3332", {"start": v(-58.87, 35.64) * mm, "end": v(-59, 35.6) * mm});
            skLineSegment(sketch, "E3333", {"start": v(-59, 35.6) * mm, "end": v(-59.1, 35.6) * mm});
            skLineSegment(sketch, "E3334", {"start": v(-59.1, 35.6) * mm, "end": v(-59.2, 35.62) * mm});
            skLineSegment(sketch, "E3335", {"start": v(-59.2, 35.62) * mm, "end": v(-59.3, 35.64) * mm});
            skLineSegment(sketch, "E3336", {"start": v(-59.3, 35.64) * mm, "end": v(-59.4, 35.67) * mm});
            skLineSegment(sketch, "E3337", {"start": v(-59.4, 35.67) * mm, "end": v(-59.5, 35.67) * mm});
            skLineSegment(sketch, "E3338", {"start": v(-59.5, 35.67) * mm, "end": v(-59.58, 35.6) * mm});
            skLineSegment(sketch, "E3339", {"start": v(-59.58, 35.6) * mm, "end": v(-59.72, 35.37) * mm});
            skLineSegment(sketch, "E3340", {"start": v(-59.72, 35.37) * mm, "end": v(-59.74, 35.26) * mm});
            skLineSegment(sketch, "E3341", {"start": v(-59.74, 35.26) * mm, "end": v(-59.7, 35.18) * mm});
            skLineSegment(sketch, "E3342", {"start": v(-59.7, 35.18) * mm, "end": v(-59.62, 35.1) * mm});
            skLineSegment(sketch, "E3343", {"start": v(-59.62, 35.1) * mm, "end": v(-59.55, 35.03) * mm});
            skLineSegment(sketch, "E3344", {"start": v(-59.55, 35.03) * mm, "end": v(-59.5, 34.95) * mm});
            skLineSegment(sketch, "E3345", {"start": v(-59.5, 34.95) * mm, "end": v(-59.44, 34.86) * mm});
            skLineSegment(sketch, "E3346", {"start": v(-59.44, 34.86) * mm, "end": v(-59.41, 34.73) * mm});
            skLineSegment(sketch, "E3347", {"start": v(-59.41, 34.73) * mm, "end": v(-59.42, 34.6) * mm});
            skLineSegment(sketch, "E3348", {"start": v(-59.42, 34.6) * mm, "end": v(-59.44, 34.47) * mm});
            skLineSegment(sketch, "E3349", {"start": v(-59.44, 34.47) * mm, "end": v(-59.5, 34.35) * mm});
            skLineSegment(sketch, "E3350", {"start": v(-59.5, 34.35) * mm, "end": v(-59.58, 34.24) * mm});
            skLineSegment(sketch, "E3351", {"start": v(-59.58, 34.24) * mm, "end": v(-59.67, 34.16) * mm});
            skLineSegment(sketch, "E3352", {"start": v(-59.67, 34.16) * mm, "end": v(-59.78, 34.09) * mm});
            skLineSegment(sketch, "E3353", {"start": v(-59.78, 34.09) * mm, "end": v(-59.9, 34.05) * mm});
            skLineSegment(sketch, "E3354", {"start": v(-59.9, 34.05) * mm, "end": v(-60.01, 34.05) * mm});
            skLineSegment(sketch, "E3355", {"start": v(-60.01, 34.05) * mm, "end": v(-60.11, 34.05) * mm});
            skLineSegment(sketch, "E3356", {"start": v(-60.11, 34.05) * mm, "end": v(-60.21, 34.07) * mm});
            skLineSegment(sketch, "E3357", {"start": v(-60.21, 34.07) * mm, "end": v(-60.3, 34.1) * mm});
            skLineSegment(sketch, "E3358", {"start": v(-60.3, 34.1) * mm, "end": v(-60.4, 34.1) * mm});
            skLineSegment(sketch, "E3359", {"start": v(-60.4, 34.1) * mm, "end": v(-60.49, 34.03) * mm});
            skLineSegment(sketch, "E3360", {"start": v(-60.49, 34.03) * mm, "end": v(-60.62, 33.8) * mm});
            skLineSegment(sketch, "E3361", {"start": v(-60.62, 33.8) * mm, "end": v(-60.64, 33.69) * mm});
            skLineSegment(sketch, "E3362", {"start": v(-60.64, 33.69) * mm, "end": v(-60.6, 33.6) * mm});
            skLineSegment(sketch, "E3363", {"start": v(-60.6, 33.6) * mm, "end": v(-60.51, 33.54) * mm});
            skLineSegment(sketch, "E3364", {"start": v(-60.51, 33.54) * mm, "end": v(-60.45, 33.46) * mm});
            skLineSegment(sketch, "E3365", {"start": v(-60.45, 33.46) * mm, "end": v(-60.39, 33.38) * mm});
            skLineSegment(sketch, "E3366", {"start": v(-60.39, 33.38) * mm, "end": v(-60.34, 33.3) * mm});
            skLineSegment(sketch, "E3367", {"start": v(-60.34, 33.3) * mm, "end": v(-60.3, 33.16) * mm});
            skLineSegment(sketch, "E3368", {"start": v(-60.3, 33.16) * mm, "end": v(-60.3, 33.03) * mm});
            skLineSegment(sketch, "E3369", {"start": v(-60.3, 33.03) * mm, "end": v(-60.33, 32.9) * mm});
            skLineSegment(sketch, "E3370", {"start": v(-60.33, 32.9) * mm, "end": v(-60.38, 32.78) * mm});
            skLineSegment(sketch, "E3371", {"start": v(-60.38, 32.78) * mm, "end": v(-60.45, 32.67) * mm});
            skLineSegment(sketch, "E3372", {"start": v(-60.45, 32.67) * mm, "end": v(-60.55, 32.58) * mm});
            skLineSegment(sketch, "E3373", {"start": v(-60.55, 32.58) * mm, "end": v(-60.66, 32.51) * mm});
            skLineSegment(sketch, "E3374", {"start": v(-60.66, 32.51) * mm, "end": v(-60.78, 32.47) * mm});
            skLineSegment(sketch, "E3375", {"start": v(-60.78, 32.47) * mm, "end": v(-60.88, 32.46) * mm});
            skLineSegment(sketch, "E3376", {"start": v(-60.88, 32.46) * mm, "end": v(-60.99, 32.47) * mm});
            skLineSegment(sketch, "E3377", {"start": v(-60.99, 32.47) * mm, "end": v(-61.08, 32.49) * mm});
            skLineSegment(sketch, "E3378", {"start": v(-61.08, 32.49) * mm, "end": v(-61.18, 32.51) * mm});
            skLineSegment(sketch, "E3379", {"start": v(-61.18, 32.51) * mm, "end": v(-61.28, 32.51) * mm});
            skLineSegment(sketch, "E3380", {"start": v(-61.28, 32.51) * mm, "end": v(-61.36, 32.44) * mm});
            skLineSegment(sketch, "E3381", {"start": v(-61.36, 32.44) * mm, "end": v(-61.49, 32.2) * mm});
            skLineSegment(sketch, "E3382", {"start": v(-61.49, 32.2) * mm, "end": v(-61.5, 32.09) * mm});
            skLineSegment(sketch, "E3383", {"start": v(-61.5, 32.09) * mm, "end": v(-61.45, 32) * mm});
            skLineSegment(sketch, "E3384", {"start": v(-61.45, 32) * mm, "end": v(-61.37, 31.94) * mm});
            skLineSegment(sketch, "E3385", {"start": v(-61.37, 31.94) * mm, "end": v(-61.3, 31.87) * mm});
            skLineSegment(sketch, "E3386", {"start": v(-61.3, 31.87) * mm, "end": v(-61.24, 31.79) * mm});
            skLineSegment(sketch, "E3387", {"start": v(-61.24, 31.79) * mm, "end": v(-61.19, 31.7) * mm});
            skLineSegment(sketch, "E3388", {"start": v(-61.19, 31.7) * mm, "end": v(-61.15, 31.57) * mm});
            skLineSegment(sketch, "E3389", {"start": v(-61.15, 31.57) * mm, "end": v(-61.15, 31.44) * mm});
            skLineSegment(sketch, "E3390", {"start": v(-61.15, 31.44) * mm, "end": v(-61.17, 31.31) * mm});
            skLineSegment(sketch, "E3391", {"start": v(-61.17, 31.31) * mm, "end": v(-61.22, 31.2) * mm});
            skLineSegment(sketch, "E3392", {"start": v(-61.22, 31.2) * mm, "end": v(-61.29, 31.08) * mm});
            skLineSegment(sketch, "E3393", {"start": v(-61.29, 31.08) * mm, "end": v(-61.38, 30.99) * mm});
            skLineSegment(sketch, "E3394", {"start": v(-61.38, 30.99) * mm, "end": v(-61.49, 30.91) * mm});
            skLineSegment(sketch, "E3395", {"start": v(-61.49, 30.91) * mm, "end": v(-61.6, 30.87) * mm});
            skLineSegment(sketch, "E3396", {"start": v(-61.6, 30.87) * mm, "end": v(-61.71, 30.86) * mm});
            skLineSegment(sketch, "E3397", {"start": v(-61.71, 30.86) * mm, "end": v(-61.81, 30.86) * mm});
            skLineSegment(sketch, "E3398", {"start": v(-61.81, 30.86) * mm, "end": v(-61.91, 30.88) * mm});
            skLineSegment(sketch, "E3399", {"start": v(-61.91, 30.88) * mm, "end": v(-62.01, 30.9) * mm});
            skLineSegment(sketch, "E3400", {"start": v(-62.01, 30.9) * mm, "end": v(-62.11, 30.9) * mm});
            skLineSegment(sketch, "E3401", {"start": v(-62.11, 30.9) * mm, "end": v(-62.19, 30.82) * mm});
            skLineSegment(sketch, "E3402", {"start": v(-62.19, 30.82) * mm, "end": v(-62.3, 30.57) * mm});
            skLineSegment(sketch, "E3403", {"start": v(-62.3, 30.57) * mm, "end": v(-62.32, 30.47) * mm});
            skLineSegment(sketch, "E3404", {"start": v(-62.32, 30.47) * mm, "end": v(-62.27, 30.38) * mm});
            skLineSegment(sketch, "E3405", {"start": v(-62.27, 30.38) * mm, "end": v(-62.19, 30.32) * mm});
            skLineSegment(sketch, "E3406", {"start": v(-62.19, 30.32) * mm, "end": v(-62.11, 30.25) * mm});
            skLineSegment(sketch, "E3407", {"start": v(-62.11, 30.25) * mm, "end": v(-62.05, 30.17) * mm});
            skLineSegment(sketch, "E3408", {"start": v(-62.05, 30.17) * mm, "end": v(-62, 30.09) * mm});
            skLineSegment(sketch, "E3409", {"start": v(-62, 30.09) * mm, "end": v(-61.96, 29.96) * mm});
            skLineSegment(sketch, "E3410", {"start": v(-61.96, 29.96) * mm, "end": v(-61.95, 29.83) * mm});
            skLineSegment(sketch, "E3411", {"start": v(-61.95, 29.83) * mm, "end": v(-61.97, 29.7) * mm});
            skLineSegment(sketch, "E3412", {"start": v(-61.97, 29.7) * mm, "end": v(-62.01, 29.58) * mm});
            skLineSegment(sketch, "E3413", {"start": v(-62.01, 29.58) * mm, "end": v(-62.08, 29.46) * mm});
            skLineSegment(sketch, "E3414", {"start": v(-62.08, 29.46) * mm, "end": v(-62.17, 29.37) * mm});
            skLineSegment(sketch, "E3415", {"start": v(-62.17, 29.37) * mm, "end": v(-62.28, 29.3) * mm});
            skLineSegment(sketch, "E3416", {"start": v(-62.28, 29.3) * mm, "end": v(-62.4, 29.24) * mm});
            skLineSegment(sketch, "E3417", {"start": v(-62.4, 29.24) * mm, "end": v(-62.5, 29.23) * mm});
            skLineSegment(sketch, "E3418", {"start": v(-62.5, 29.23) * mm, "end": v(-62.6, 29.23) * mm});
            skLineSegment(sketch, "E3419", {"start": v(-62.6, 29.23) * mm, "end": v(-62.7, 29.24) * mm});
            skLineSegment(sketch, "E3420", {"start": v(-62.7, 29.24) * mm, "end": v(-62.8, 29.27) * mm});
            skLineSegment(sketch, "E3421", {"start": v(-62.8, 29.27) * mm, "end": v(-62.9, 29.26) * mm});
            skLineSegment(sketch, "E3422", {"start": v(-62.9, 29.26) * mm, "end": v(-62.97, 29.18) * mm});
            skLineSegment(sketch, "E3423", {"start": v(-62.97, 29.18) * mm, "end": v(-63.09, 28.93) * mm});
            skLineSegment(sketch, "E3424", {"start": v(-63.09, 28.93) * mm, "end": v(-63.1, 28.83) * mm});
            skLineSegment(sketch, "E3425", {"start": v(-63.1, 28.83) * mm, "end": v(-63.04, 28.74) * mm});
            skLineSegment(sketch, "E3426", {"start": v(-63.04, 28.74) * mm, "end": v(-62.96, 28.69) * mm});
            skLineSegment(sketch, "E3427", {"start": v(-62.96, 28.69) * mm, "end": v(-62.88, 28.62) * mm});
            skLineSegment(sketch, "E3428", {"start": v(-62.88, 28.62) * mm, "end": v(-62.82, 28.54) * mm});
            skLineSegment(sketch, "E3429", {"start": v(-62.82, 28.54) * mm, "end": v(-62.76, 28.45) * mm});
            skLineSegment(sketch, "E3430", {"start": v(-62.76, 28.45) * mm, "end": v(-62.72, 28.33) * mm});
            skLineSegment(sketch, "E3431", {"start": v(-62.72, 28.33) * mm, "end": v(-62.7, 28.2) * mm});
            skLineSegment(sketch, "E3432", {"start": v(-62.7, 28.2) * mm, "end": v(-62.72, 28.07) * mm});
            skLineSegment(sketch, "E3433", {"start": v(-62.72, 28.07) * mm, "end": v(-62.76, 27.94) * mm});
            skLineSegment(sketch, "E3434", {"start": v(-62.76, 27.94) * mm, "end": v(-62.83, 27.83) * mm});
            skLineSegment(sketch, "E3435", {"start": v(-62.83, 27.83) * mm, "end": v(-62.92, 27.73) * mm});
            skLineSegment(sketch, "E3436", {"start": v(-62.92, 27.73) * mm, "end": v(-63.02, 27.65) * mm});
            skLineSegment(sketch, "E3437", {"start": v(-63.02, 27.65) * mm, "end": v(-63.14, 27.6) * mm});
            skLineSegment(sketch, "E3438", {"start": v(-63.14, 27.6) * mm, "end": v(-63.24, 27.59) * mm});
            skLineSegment(sketch, "E3439", {"start": v(-63.24, 27.59) * mm, "end": v(-63.34, 27.58) * mm});
            skLineSegment(sketch, "E3440", {"start": v(-63.34, 27.58) * mm, "end": v(-63.45, 27.6) * mm});
            skLineSegment(sketch, "E3441", {"start": v(-63.45, 27.6) * mm, "end": v(-63.54, 27.61) * mm});
            skLineSegment(sketch, "E3442", {"start": v(-63.54, 27.61) * mm, "end": v(-63.64, 27.6) * mm});
            skLineSegment(sketch, "E3443", {"start": v(-63.64, 27.6) * mm, "end": v(-63.71, 27.52) * mm});
            skLineSegment(sketch, "E3444", {"start": v(-63.71, 27.52) * mm, "end": v(-63.82, 27.27) * mm});
            skLineSegment(sketch, "E3445", {"start": v(-63.82, 27.27) * mm, "end": v(-63.83, 27.16) * mm});
            skLineSegment(sketch, "E3446", {"start": v(-63.83, 27.16) * mm, "end": v(-63.77, 27.08) * mm});
            skLineSegment(sketch, "E3447", {"start": v(-63.77, 27.08) * mm, "end": v(-63.69, 27.03) * mm});
            skLineSegment(sketch, "E3448", {"start": v(-63.69, 27.03) * mm, "end": v(-63.61, 26.96) * mm});
            skLineSegment(sketch, "E3449", {"start": v(-63.61, 26.96) * mm, "end": v(-63.54, 26.89) * mm});
            skLineSegment(sketch, "E3450", {"start": v(-63.54, 26.89) * mm, "end": v(-63.48, 26.8) * mm});
            skLineSegment(sketch, "E3451", {"start": v(-63.48, 26.8) * mm, "end": v(-63.44, 26.68) * mm});
            skLineSegment(sketch, "E3452", {"start": v(-63.44, 26.68) * mm, "end": v(-63.42, 26.55) * mm});
            skLineSegment(sketch, "E3453", {"start": v(-63.42, 26.55) * mm, "end": v(-63.44, 26.42) * mm});
            skLineSegment(sketch, "E3454", {"start": v(-63.44, 26.42) * mm, "end": v(-63.47, 26.3) * mm});
            skLineSegment(sketch, "E3455", {"start": v(-63.47, 26.3) * mm, "end": v(-63.54, 26.18) * mm});
            skLineSegment(sketch, "E3456", {"start": v(-63.54, 26.18) * mm, "end": v(-63.62, 26.07) * mm});
            skLineSegment(sketch, "E3457", {"start": v(-63.62, 26.07) * mm, "end": v(-63.72, 26) * mm});
            skLineSegment(sketch, "E3458", {"start": v(-63.72, 26) * mm, "end": v(-63.84, 25.94) * mm});
            skLineSegment(sketch, "E3459", {"start": v(-63.84, 25.94) * mm, "end": v(-63.94, 25.92) * mm});
            skLineSegment(sketch, "E3460", {"start": v(-63.94, 25.92) * mm, "end": v(-64.05, 25.92) * mm});
            skLineSegment(sketch, "E3461", {"start": v(-64.05, 25.92) * mm, "end": v(-64.15, 25.92) * mm});
            skLineSegment(sketch, "E3462", {"start": v(-64.15, 25.92) * mm, "end": v(-64.24, 25.94) * mm});
            skLineSegment(sketch, "E3463", {"start": v(-64.24, 25.94) * mm, "end": v(-64.34, 25.93) * mm});
            skLineSegment(sketch, "E3464", {"start": v(-64.34, 25.93) * mm, "end": v(-64.41, 25.85) * mm});
            skLineSegment(sketch, "E3465", {"start": v(-64.41, 25.85) * mm, "end": v(-64.51, 25.6) * mm});
            skLineSegment(sketch, "E3466", {"start": v(-64.51, 25.6) * mm, "end": v(-64.52, 25.48) * mm});
            skLineSegment(sketch, "E3467", {"start": v(-64.52, 25.48) * mm, "end": v(-64.46, 25.4) * mm});
            skLineSegment(sketch, "E3468", {"start": v(-64.46, 25.4) * mm, "end": v(-64.37, 25.35) * mm});
            skLineSegment(sketch, "E3469", {"start": v(-64.37, 25.35) * mm, "end": v(-64.3, 25.29) * mm});
            skLineSegment(sketch, "E3470", {"start": v(-64.3, 25.29) * mm, "end": v(-64.23, 25.21) * mm});
            skLineSegment(sketch, "E3471", {"start": v(-64.23, 25.21) * mm, "end": v(-64.16, 25.13) * mm});
            skLineSegment(sketch, "E3472", {"start": v(-64.16, 25.13) * mm, "end": v(-64.12, 25) * mm});
            skLineSegment(sketch, "E3473", {"start": v(-64.12, 25) * mm, "end": v(-64.1, 24.88) * mm});
            skLineSegment(sketch, "E3474", {"start": v(-64.1, 24.88) * mm, "end": v(-64.1, 24.75) * mm});
            skLineSegment(sketch, "E3475", {"start": v(-64.1, 24.75) * mm, "end": v(-64.14, 24.62) * mm});
            skLineSegment(sketch, "E3476", {"start": v(-64.14, 24.62) * mm, "end": v(-64.2, 24.5) * mm});
            skLineSegment(sketch, "E3477", {"start": v(-64.2, 24.5) * mm, "end": v(-64.28, 24.4) * mm});
            skLineSegment(sketch, "E3478", {"start": v(-64.28, 24.4) * mm, "end": v(-64.38, 24.32) * mm});
            skLineSegment(sketch, "E3479", {"start": v(-64.38, 24.32) * mm, "end": v(-64.5, 24.26) * mm});
            skLineSegment(sketch, "E3480", {"start": v(-64.5, 24.26) * mm, "end": v(-64.6, 24.24) * mm});
            skLineSegment(sketch, "E3481", {"start": v(-64.6, 24.24) * mm, "end": v(-64.7, 24.23) * mm});
            skLineSegment(sketch, "E3482", {"start": v(-64.7, 24.23) * mm, "end": v(-64.8, 24.23) * mm});
            skLineSegment(sketch, "E3483", {"start": v(-64.8, 24.23) * mm, "end": v(-64.9, 24.25) * mm});
            skLineSegment(sketch, "E3484", {"start": v(-64.9, 24.25) * mm, "end": v(-65, 24.23) * mm});
            skLineSegment(sketch, "E3485", {"start": v(-65, 24.23) * mm, "end": v(-65.07, 24.15) * mm});
            skLineSegment(sketch, "E3486", {"start": v(-65.07, 24.15) * mm, "end": v(-65.16, 23.9) * mm});
            skLineSegment(sketch, "E3487", {"start": v(-65.16, 23.9) * mm, "end": v(-65.16, 23.79) * mm});
            skLineSegment(sketch, "E3488", {"start": v(-65.16, 23.79) * mm, "end": v(-65.1, 23.7) * mm});
            skLineSegment(sketch, "E3489", {"start": v(-65.1, 23.7) * mm, "end": v(-65.02, 23.66) * mm});
            skLineSegment(sketch, "E3490", {"start": v(-65.02, 23.66) * mm, "end": v(-64.94, 23.6) * mm});
            skLineSegment(sketch, "E3491", {"start": v(-64.94, 23.6) * mm, "end": v(-64.86, 23.52) * mm});
            skLineSegment(sketch, "E3492", {"start": v(-64.86, 23.52) * mm, "end": v(-64.8, 23.44) * mm});
            skLineSegment(sketch, "E3493", {"start": v(-64.8, 23.44) * mm, "end": v(-64.75, 23.32) * mm});
            skLineSegment(sketch, "E3494", {"start": v(-64.75, 23.32) * mm, "end": v(-64.73, 23.2) * mm});
            skLineSegment(sketch, "E3495", {"start": v(-64.73, 23.2) * mm, "end": v(-64.73, 23.06) * mm});
            skLineSegment(sketch, "E3496", {"start": v(-64.73, 23.06) * mm, "end": v(-64.76, 22.93) * mm});
            skLineSegment(sketch, "E3497", {"start": v(-64.76, 22.93) * mm, "end": v(-64.82, 22.81) * mm});
            skLineSegment(sketch, "E3498", {"start": v(-64.82, 22.81) * mm, "end": v(-64.9, 22.7) * mm});
            skLineSegment(sketch, "E3499", {"start": v(-64.9, 22.7) * mm, "end": v(-65, 22.62) * mm});
            skLineSegment(sketch, "E3500", {"start": v(-65, 22.62) * mm, "end": v(-65.11, 22.56) * mm});
            skLineSegment(sketch, "E3501", {"start": v(-65.11, 22.56) * mm, "end": v(-65.21, 22.54) * mm});
            skLineSegment(sketch, "E3502", {"start": v(-65.21, 22.54) * mm, "end": v(-65.31, 22.53) * mm});
            skLineSegment(sketch, "E3503", {"start": v(-65.31, 22.53) * mm, "end": v(-65.41, 22.53) * mm});
            skLineSegment(sketch, "E3504", {"start": v(-65.41, 22.53) * mm, "end": v(-65.51, 22.54) * mm});
            skLineSegment(sketch, "E3505", {"start": v(-65.51, 22.54) * mm, "end": v(-65.61, 22.52) * mm});
            skLineSegment(sketch, "E3506", {"start": v(-65.61, 22.52) * mm, "end": v(-65.68, 22.44) * mm});
            skLineSegment(sketch, "E3507", {"start": v(-65.68, 22.44) * mm, "end": v(-65.77, 22.18) * mm});
            skLineSegment(sketch, "E3508", {"start": v(-65.77, 22.18) * mm, "end": v(-65.76, 22.07) * mm});
            skLineSegment(sketch, "E3509", {"start": v(-65.76, 22.07) * mm, "end": v(-65.7, 22) * mm});
            skLineSegment(sketch, "E3510", {"start": v(-65.7, 22) * mm, "end": v(-65.61, 21.95) * mm});
            skLineSegment(sketch, "E3511", {"start": v(-65.61, 21.95) * mm, "end": v(-65.53, 21.89) * mm});
            skLineSegment(sketch, "E3512", {"start": v(-65.53, 21.89) * mm, "end": v(-65.46, 21.82) * mm});
            skLineSegment(sketch, "E3513", {"start": v(-65.46, 21.82) * mm, "end": v(-65.4, 21.74) * mm});
            skLineSegment(sketch, "E3514", {"start": v(-65.4, 21.74) * mm, "end": v(-65.34, 21.62) * mm});
            skLineSegment(sketch, "E3515", {"start": v(-65.34, 21.62) * mm, "end": v(-65.31, 21.5) * mm});
            skLineSegment(sketch, "E3516", {"start": v(-65.31, 21.5) * mm, "end": v(-65.31, 21.36) * mm});
            skLineSegment(sketch, "E3517", {"start": v(-65.31, 21.36) * mm, "end": v(-65.34, 21.23) * mm});
            skLineSegment(sketch, "E3518", {"start": v(-65.34, 21.23) * mm, "end": v(-65.4, 21.1) * mm});
            skLineSegment(sketch, "E3519", {"start": v(-65.4, 21.1) * mm, "end": v(-65.47, 21) * mm});
            skLineSegment(sketch, "E3520", {"start": v(-65.47, 21) * mm, "end": v(-65.57, 20.91) * mm});
            skLineSegment(sketch, "E3521", {"start": v(-65.57, 20.91) * mm, "end": v(-65.68, 20.85) * mm});
            skLineSegment(sketch, "E3522", {"start": v(-65.68, 20.85) * mm, "end": v(-65.78, 20.82) * mm});
            skLineSegment(sketch, "E3523", {"start": v(-65.78, 20.82) * mm, "end": v(-65.88, 20.81) * mm});
            skLineSegment(sketch, "E3524", {"start": v(-65.88, 20.81) * mm, "end": v(-65.98, 20.81) * mm});
            skLineSegment(sketch, "E3525", {"start": v(-65.98, 20.81) * mm, "end": v(-66.08, 20.82) * mm});
            skLineSegment(sketch, "E3526", {"start": v(-66.08, 20.82) * mm, "end": v(-66.18, 20.8) * mm});
            skLineSegment(sketch, "E3527", {"start": v(-66.18, 20.8) * mm, "end": v(-66.24, 20.71) * mm});
            skLineSegment(sketch, "E3528", {"start": v(-66.24, 20.71) * mm, "end": v(-66.32, 20.45) * mm});
            skLineSegment(sketch, "E3529", {"start": v(-66.32, 20.45) * mm, "end": v(-66.32, 20.34) * mm});
            skLineSegment(sketch, "E3530", {"start": v(-66.32, 20.34) * mm, "end": v(-66.25, 20.27) * mm});
            skLineSegment(sketch, "E3531", {"start": v(-66.25, 20.27) * mm, "end": v(-66.16, 20.22) * mm});
            skLineSegment(sketch, "E3532", {"start": v(-66.16, 20.22) * mm, "end": v(-66.08, 20.16) * mm});
            skLineSegment(sketch, "E3533", {"start": v(-66.08, 20.16) * mm, "end": v(-66, 20.1) * mm});
            skLineSegment(sketch, "E3534", {"start": v(-66, 20.1) * mm, "end": v(-65.94, 20.02) * mm});
            skLineSegment(sketch, "E3535", {"start": v(-65.94, 20.02) * mm, "end": v(-65.88, 19.9) * mm});
            skLineSegment(sketch, "E3536", {"start": v(-65.88, 19.9) * mm, "end": v(-65.85, 19.77) * mm});
            skLineSegment(sketch, "E3537", {"start": v(-65.85, 19.77) * mm, "end": v(-65.85, 19.64) * mm});
            skLineSegment(sketch, "E3538", {"start": v(-65.85, 19.64) * mm, "end": v(-65.87, 19.51) * mm});
            skLineSegment(sketch, "E3539", {"start": v(-65.87, 19.51) * mm, "end": v(-65.92, 19.4) * mm});
            skLineSegment(sketch, "E3540", {"start": v(-65.92, 19.4) * mm, "end": v(-66, 19.28) * mm});
            skLineSegment(sketch, "E3541", {"start": v(-66, 19.28) * mm, "end": v(-66.1, 19.2) * mm});
            skLineSegment(sketch, "E3542", {"start": v(-66.1, 19.2) * mm, "end": v(-66.2, 19.12) * mm});
            skLineSegment(sketch, "E3543", {"start": v(-66.2, 19.12) * mm, "end": v(-66.3, 19.1) * mm});
            skLineSegment(sketch, "E3544", {"start": v(-66.3, 19.1) * mm, "end": v(-66.4, 19.08) * mm});
            skLineSegment(sketch, "E3545", {"start": v(-66.4, 19.08) * mm, "end": v(-66.5, 19.08) * mm});
            skLineSegment(sketch, "E3546", {"start": v(-66.5, 19.08) * mm, "end": v(-66.6, 19.08) * mm});
            skLineSegment(sketch, "E3547", {"start": v(-66.6, 19.08) * mm, "end": v(-66.7, 19.06) * mm});
            skLineSegment(sketch, "E3548", {"start": v(-66.7, 19.06) * mm, "end": v(-66.76, 18.97) * mm});
            skLineSegment(sketch, "E3549", {"start": v(-66.76, 18.97) * mm, "end": v(-66.84, 18.7) * mm});
            skLineSegment(sketch, "E3550", {"start": v(-66.84, 18.7) * mm, "end": v(-66.83, 18.6) * mm});
            skLineSegment(sketch, "E3551", {"start": v(-66.83, 18.6) * mm, "end": v(-66.76, 18.53) * mm});
            skLineSegment(sketch, "E3552", {"start": v(-66.76, 18.53) * mm, "end": v(-66.67, 18.48) * mm});
            skLineSegment(sketch, "E3553", {"start": v(-66.67, 18.48) * mm, "end": v(-66.59, 18.43) * mm});
            skLineSegment(sketch, "E3554", {"start": v(-66.59, 18.43) * mm, "end": v(-66.51, 18.36) * mm});
            skLineSegment(sketch, "E3555", {"start": v(-66.51, 18.36) * mm, "end": v(-66.44, 18.29) * mm});
            skLineSegment(sketch, "E3556", {"start": v(-66.44, 18.29) * mm, "end": v(-66.38, 18.17) * mm});
            skLineSegment(sketch, "E3557", {"start": v(-66.38, 18.17) * mm, "end": v(-66.35, 18.04) * mm});
            skLineSegment(sketch, "E3558", {"start": v(-66.35, 18.04) * mm, "end": v(-66.34, 17.91) * mm});
            skLineSegment(sketch, "E3559", {"start": v(-66.34, 17.91) * mm, "end": v(-66.36, 17.78) * mm});
            skLineSegment(sketch, "E3560", {"start": v(-66.36, 17.78) * mm, "end": v(-66.4, 17.66) * mm});
            skLineSegment(sketch, "E3561", {"start": v(-66.4, 17.66) * mm, "end": v(-66.48, 17.55) * mm});
            skLineSegment(sketch, "E3562", {"start": v(-66.48, 17.55) * mm, "end": v(-66.57, 17.45) * mm});
            skLineSegment(sketch, "E3563", {"start": v(-66.57, 17.45) * mm, "end": v(-66.68, 17.38) * mm});
            skLineSegment(sketch, "E3564", {"start": v(-66.68, 17.38) * mm, "end": v(-66.78, 17.35) * mm});
            skLineSegment(sketch, "E3565", {"start": v(-66.78, 17.35) * mm, "end": v(-66.88, 17.33) * mm});
            skLineSegment(sketch, "E3566", {"start": v(-66.88, 17.33) * mm, "end": v(-66.98, 17.33) * mm});
            skLineSegment(sketch, "E3567", {"start": v(-66.98, 17.33) * mm, "end": v(-67.08, 17.33) * mm});
            skLineSegment(sketch, "E3568", {"start": v(-67.08, 17.33) * mm, "end": v(-67.18, 17.3) * mm});
            skLineSegment(sketch, "E3569", {"start": v(-67.18, 17.3) * mm, "end": v(-67.24, 17.22) * mm});
            skLineSegment(sketch, "E3570", {"start": v(-67.24, 17.22) * mm, "end": v(-67.3, 16.95) * mm});
            skLineSegment(sketch, "E3571", {"start": v(-67.3, 16.95) * mm, "end": v(-67.3, 16.84) * mm});
            skLineSegment(sketch, "E3572", {"start": v(-67.3, 16.84) * mm, "end": v(-67.22, 16.77) * mm});
            skLineSegment(sketch, "E3573", {"start": v(-67.22, 16.77) * mm, "end": v(-67.13, 16.73) * mm});
            skLineSegment(sketch, "E3574", {"start": v(-67.13, 16.73) * mm, "end": v(-67.05, 16.68) * mm});
            skLineSegment(sketch, "E3575", {"start": v(-67.05, 16.68) * mm, "end": v(-66.97, 16.61) * mm});
            skLineSegment(sketch, "E3576", {"start": v(-66.97, 16.61) * mm, "end": v(-66.9, 16.54) * mm});
            skLineSegment(sketch, "E3577", {"start": v(-66.9, 16.54) * mm, "end": v(-66.83, 16.43) * mm});
            skLineSegment(sketch, "E3578", {"start": v(-66.83, 16.43) * mm, "end": v(-66.8, 16.3) * mm});
            skLineSegment(sketch, "E3579", {"start": v(-66.8, 16.3) * mm, "end": v(-66.79, 16.17) * mm});
            skLineSegment(sketch, "E3580", {"start": v(-66.79, 16.17) * mm, "end": v(-66.8, 16.04) * mm});
            skLineSegment(sketch, "E3581", {"start": v(-66.8, 16.04) * mm, "end": v(-66.85, 15.91) * mm});
            skLineSegment(sketch, "E3582", {"start": v(-66.85, 15.91) * mm, "end": v(-66.92, 15.8) * mm});
            skLineSegment(sketch, "E3583", {"start": v(-66.92, 15.8) * mm, "end": v(-67, 15.7) * mm});
            skLineSegment(sketch, "E3584", {"start": v(-67, 15.7) * mm, "end": v(-67.11, 15.63) * mm});
            skLineSegment(sketch, "E3585", {"start": v(-67.11, 15.63) * mm, "end": v(-67.21, 15.6) * mm});
            skLineSegment(sketch, "E3586", {"start": v(-67.21, 15.6) * mm, "end": v(-67.31, 15.58) * mm});
            skLineSegment(sketch, "E3587", {"start": v(-67.31, 15.58) * mm, "end": v(-67.41, 15.57) * mm});
            skLineSegment(sketch, "E3588", {"start": v(-67.41, 15.57) * mm, "end": v(-67.51, 15.57) * mm});
            skLineSegment(sketch, "E3589", {"start": v(-67.51, 15.57) * mm, "end": v(-67.6, 15.54) * mm});
            skLineSegment(sketch, "E3590", {"start": v(-67.6, 15.54) * mm, "end": v(-67.66, 15.45) * mm});
            skLineSegment(sketch, "E3591", {"start": v(-67.66, 15.45) * mm, "end": v(-67.72, 15.18) * mm});
            skLineSegment(sketch, "E3592", {"start": v(-67.72, 15.18) * mm, "end": v(-67.71, 15.08) * mm});
            skLineSegment(sketch, "E3593", {"start": v(-67.71, 15.08) * mm, "end": v(-67.64, 15) * mm});
            skLineSegment(sketch, "E3594", {"start": v(-67.64, 15) * mm, "end": v(-67.55, 14.97) * mm});
            skLineSegment(sketch, "E3595", {"start": v(-67.55, 14.97) * mm, "end": v(-67.46, 14.92) * mm});
            skLineSegment(sketch, "E3596", {"start": v(-67.46, 14.92) * mm, "end": v(-67.38, 14.86) * mm});
            skLineSegment(sketch, "E3597", {"start": v(-67.38, 14.86) * mm, "end": v(-67.3, 14.78) * mm});
            skLineSegment(sketch, "E3598", {"start": v(-67.3, 14.78) * mm, "end": v(-67.24, 14.67) * mm});
            skLineSegment(sketch, "E3599", {"start": v(-67.24, 14.67) * mm, "end": v(-67.2, 14.55) * mm});
            skLineSegment(sketch, "E3600", {"start": v(-67.2, 14.55) * mm, "end": v(-67.19, 14.42) * mm});
            skLineSegment(sketch, "E3601", {"start": v(-67.19, 14.42) * mm, "end": v(-67.2, 14.28) * mm});
            skLineSegment(sketch, "E3602", {"start": v(-67.2, 14.28) * mm, "end": v(-67.24, 14.16) * mm});
            skLineSegment(sketch, "E3603", {"start": v(-67.24, 14.16) * mm, "end": v(-67.3, 14.04) * mm});
            skLineSegment(sketch, "E3604", {"start": v(-67.3, 14.04) * mm, "end": v(-67.4, 13.95) * mm});
            skLineSegment(sketch, "E3605", {"start": v(-67.4, 13.95) * mm, "end": v(-67.5, 13.87) * mm});
            skLineSegment(sketch, "E3606", {"start": v(-67.5, 13.87) * mm, "end": v(-67.6, 13.83) * mm});
            skLineSegment(sketch, "E3607", {"start": v(-67.6, 13.83) * mm, "end": v(-67.7, 13.81) * mm});
            skLineSegment(sketch, "E3608", {"start": v(-67.7, 13.81) * mm, "end": v(-67.8, 13.8) * mm});
            skLineSegment(sketch, "E3609", {"start": v(-67.8, 13.8) * mm, "end": v(-67.9, 13.8) * mm});
            skLineSegment(sketch, "E3610", {"start": v(-67.9, 13.8) * mm, "end": v(-68, 13.77) * mm});
            skLineSegment(sketch, "E3611", {"start": v(-68, 13.77) * mm, "end": v(-68.04, 13.67) * mm});
            skLineSegment(sketch, "E3612", {"start": v(-68.04, 13.67) * mm, "end": v(-68.1, 13.4) * mm});
            skLineSegment(sketch, "E3613", {"start": v(-68.1, 13.4) * mm, "end": v(-68.08, 13.3) * mm});
            skLineSegment(sketch, "E3614", {"start": v(-68.08, 13.3) * mm, "end": v(-68, 13.23) * mm});
            skLineSegment(sketch, "E3615", {"start": v(-68, 13.23) * mm, "end": v(-67.92, 13.2) * mm});
            skLineSegment(sketch, "E3616", {"start": v(-67.92, 13.2) * mm, "end": v(-67.83, 13.15) * mm});
            skLineSegment(sketch, "E3617", {"start": v(-67.83, 13.15) * mm, "end": v(-67.75, 13.09) * mm});
            skLineSegment(sketch, "E3618", {"start": v(-67.75, 13.09) * mm, "end": v(-67.67, 13.02) * mm});
            skLineSegment(sketch, "E3619", {"start": v(-67.67, 13.02) * mm, "end": v(-67.6, 12.9) * mm});
            skLineSegment(sketch, "E3620", {"start": v(-67.6, 12.9) * mm, "end": v(-67.56, 12.78) * mm});
            skLineSegment(sketch, "E3621", {"start": v(-67.56, 12.78) * mm, "end": v(-67.54, 12.65) * mm});
            skLineSegment(sketch, "E3622", {"start": v(-67.54, 12.65) * mm, "end": v(-67.55, 12.52) * mm});
            skLineSegment(sketch, "E3623", {"start": v(-67.55, 12.52) * mm, "end": v(-67.6, 12.4) * mm});
            skLineSegment(sketch, "E3624", {"start": v(-67.6, 12.4) * mm, "end": v(-67.65, 12.28) * mm});
            skLineSegment(sketch, "E3625", {"start": v(-67.65, 12.28) * mm, "end": v(-67.74, 12.18) * mm});
            skLineSegment(sketch, "E3626", {"start": v(-67.74, 12.18) * mm, "end": v(-67.84, 12.1) * mm});
            skLineSegment(sketch, "E3627", {"start": v(-67.84, 12.1) * mm, "end": v(-67.94, 12.06) * mm});
            skLineSegment(sketch, "E3628", {"start": v(-67.94, 12.06) * mm, "end": v(-68.03, 12.03) * mm});
            skLineSegment(sketch, "E3629", {"start": v(-68.03, 12.03) * mm, "end": v(-68.13, 12.02) * mm});
            skLineSegment(sketch, "E3630", {"start": v(-68.13, 12.02) * mm, "end": v(-68.23, 12.02) * mm});
            skLineSegment(sketch, "E3631", {"start": v(-68.23, 12.02) * mm, "end": v(-68.33, 11.98) * mm});
            skLineSegment(sketch, "E3632", {"start": v(-68.33, 11.98) * mm, "end": v(-68.38, 11.89) * mm});
            skLineSegment(sketch, "E3633", {"start": v(-68.38, 11.89) * mm, "end": v(-68.43, 11.62) * mm});
            skLineSegment(sketch, "E3634", {"start": v(-68.43, 11.62) * mm, "end": v(-68.4, 11.51) * mm});
            skLineSegment(sketch, "E3635", {"start": v(-68.4, 11.51) * mm, "end": v(-68.33, 11.45) * mm});
            skLineSegment(sketch, "E3636", {"start": v(-68.33, 11.45) * mm, "end": v(-68.24, 11.41) * mm});
            skLineSegment(sketch, "E3637", {"start": v(-68.24, 11.41) * mm, "end": v(-68.15, 11.37) * mm});
            skLineSegment(sketch, "E3638", {"start": v(-68.15, 11.37) * mm, "end": v(-68.07, 11.3) * mm});
            skLineSegment(sketch, "E3639", {"start": v(-68.07, 11.3) * mm, "end": v(-67.99, 11.24) * mm});
            skLineSegment(sketch, "E3640", {"start": v(-67.99, 11.24) * mm, "end": v(-67.91, 11.13) * mm});
            skLineSegment(sketch, "E3641", {"start": v(-67.91, 11.13) * mm, "end": v(-67.87, 11) * mm});
            skLineSegment(sketch, "E3642", {"start": v(-67.87, 11) * mm, "end": v(-67.85, 10.88) * mm});
            skLineSegment(sketch, "E3643", {"start": v(-67.85, 10.88) * mm, "end": v(-67.86, 10.75) * mm});
            skLineSegment(sketch, "E3644", {"start": v(-67.86, 10.75) * mm, "end": v(-67.9, 10.62) * mm});
            skLineSegment(sketch, "E3645", {"start": v(-67.9, 10.62) * mm, "end": v(-67.95, 10.5) * mm});
            skLineSegment(sketch, "E3646", {"start": v(-67.95, 10.5) * mm, "end": v(-68.03, 10.4) * mm});
            skLineSegment(sketch, "E3647", {"start": v(-68.03, 10.4) * mm, "end": v(-68.13, 10.32) * mm});
            skLineSegment(sketch, "E3648", {"start": v(-68.13, 10.32) * mm, "end": v(-68.23, 10.28) * mm});
            skLineSegment(sketch, "E3649", {"start": v(-68.23, 10.28) * mm, "end": v(-68.33, 10.25) * mm});
            skLineSegment(sketch, "E3650", {"start": v(-68.33, 10.25) * mm, "end": v(-68.42, 10.23) * mm});
            skLineSegment(sketch, "E3651", {"start": v(-68.42, 10.23) * mm, "end": v(-68.53, 10.23) * mm});
            skLineSegment(sketch, "E3652", {"start": v(-68.53, 10.23) * mm, "end": v(-68.62, 10.19) * mm});
            skLineSegment(sketch, "E3653", {"start": v(-68.62, 10.19) * mm, "end": v(-68.67, 10.1) * mm});
            skLineSegment(sketch, "E3654", {"start": v(-68.67, 10.1) * mm, "end": v(-68.7, 9.82) * mm});
            skLineSegment(sketch, "E3655", {"start": v(-68.7, 9.82) * mm, "end": v(-68.69, 9.72) * mm});
            skLineSegment(sketch, "E3656", {"start": v(-68.69, 9.72) * mm, "end": v(-68.6, 9.66) * mm});
            skLineSegment(sketch, "E3657", {"start": v(-68.6, 9.66) * mm, "end": v(-68.51, 9.62) * mm});
            skLineSegment(sketch, "E3658", {"start": v(-68.51, 9.62) * mm, "end": v(-68.42, 9.58) * mm});
            skLineSegment(sketch, "E3659", {"start": v(-68.42, 9.58) * mm, "end": v(-68.34, 9.52) * mm});
            skLineSegment(sketch, "E3660", {"start": v(-68.34, 9.52) * mm, "end": v(-68.26, 9.46) * mm});
            skLineSegment(sketch, "E3661", {"start": v(-68.26, 9.46) * mm, "end": v(-68.18, 9.35) * mm});
            skLineSegment(sketch, "E3662", {"start": v(-68.18, 9.35) * mm, "end": v(-68.13, 9.23) * mm});
            skLineSegment(sketch, "E3663", {"start": v(-68.13, 9.23) * mm, "end": v(-68.11, 9.1) * mm});
            skLineSegment(sketch, "E3664", {"start": v(-68.11, 9.1) * mm, "end": v(-68.12, 8.97) * mm});
            skLineSegment(sketch, "E3665", {"start": v(-68.12, 8.97) * mm, "end": v(-68.15, 8.84) * mm});
            skLineSegment(sketch, "E3666", {"start": v(-68.15, 8.84) * mm, "end": v(-68.2, 8.72) * mm});
            skLineSegment(sketch, "E3667", {"start": v(-68.2, 8.72) * mm, "end": v(-68.28, 8.62) * mm});
            skLineSegment(sketch, "E3668", {"start": v(-68.28, 8.62) * mm, "end": v(-68.38, 8.53) * mm});
            skLineSegment(sketch, "E3669", {"start": v(-68.38, 8.53) * mm, "end": v(-68.47, 8.49) * mm});
            skLineSegment(sketch, "E3670", {"start": v(-68.47, 8.49) * mm, "end": v(-68.57, 8.46) * mm});
            skLineSegment(sketch, "E3671", {"start": v(-68.57, 8.46) * mm, "end": v(-68.67, 8.44) * mm});
            skLineSegment(sketch, "E3672", {"start": v(-68.67, 8.44) * mm, "end": v(-68.77, 8.43) * mm});
            skLineSegment(sketch, "E3673", {"start": v(-68.77, 8.43) * mm, "end": v(-68.86, 8.4) * mm});
            skLineSegment(sketch, "E3674", {"start": v(-68.86, 8.4) * mm, "end": v(-68.9, 8.3) * mm});
            skLineSegment(sketch, "E3675", {"start": v(-68.9, 8.3) * mm, "end": v(-68.94, 8.02) * mm});
            skLineSegment(sketch, "E3676", {"start": v(-68.94, 8.02) * mm, "end": v(-68.92, 7.92) * mm});
            skLineSegment(sketch, "E3677", {"start": v(-68.92, 7.92) * mm, "end": v(-68.84, 7.86) * mm});
            skLineSegment(sketch, "E3678", {"start": v(-68.84, 7.86) * mm, "end": v(-68.74, 7.83) * mm});
            skLineSegment(sketch, "E3679", {"start": v(-68.74, 7.83) * mm, "end": v(-68.65, 7.78) * mm});
            skLineSegment(sketch, "E3680", {"start": v(-68.65, 7.78) * mm, "end": v(-68.56, 7.73) * mm});
            skLineSegment(sketch, "E3681", {"start": v(-68.56, 7.73) * mm, "end": v(-68.48, 7.67) * mm});
            skLineSegment(sketch, "E3682", {"start": v(-68.48, 7.67) * mm, "end": v(-68.4, 7.56) * mm});
            skLineSegment(sketch, "E3683", {"start": v(-68.4, 7.56) * mm, "end": v(-68.35, 7.44) * mm});
            skLineSegment(sketch, "E3684", {"start": v(-68.35, 7.44) * mm, "end": v(-68.33, 7.31) * mm});
            skLineSegment(sketch, "E3685", {"start": v(-68.33, 7.31) * mm, "end": v(-68.33, 7.18) * mm});
            skLineSegment(sketch, "E3686", {"start": v(-68.33, 7.18) * mm, "end": v(-68.35, 7.05) * mm});
            skLineSegment(sketch, "E3687", {"start": v(-68.35, 7.05) * mm, "end": v(-68.4, 6.93) * mm});
            skLineSegment(sketch, "E3688", {"start": v(-68.4, 6.93) * mm, "end": v(-68.48, 6.83) * mm});
            skLineSegment(sketch, "E3689", {"start": v(-68.48, 6.83) * mm, "end": v(-68.58, 6.74) * mm});
            skLineSegment(sketch, "E3690", {"start": v(-68.58, 6.74) * mm, "end": v(-68.67, 6.7) * mm});
            skLineSegment(sketch, "E3691", {"start": v(-68.67, 6.7) * mm, "end": v(-68.77, 6.66) * mm});
            skLineSegment(sketch, "E3692", {"start": v(-68.77, 6.66) * mm, "end": v(-68.87, 6.64) * mm});
            skLineSegment(sketch, "E3693", {"start": v(-68.87, 6.64) * mm, "end": v(-68.97, 6.63) * mm});
            skLineSegment(sketch, "E3694", {"start": v(-68.97, 6.63) * mm, "end": v(-69.06, 6.58) * mm});
            skLineSegment(sketch, "E3695", {"start": v(-69.06, 6.58) * mm, "end": v(-69.1, 6.49) * mm});
            skLineSegment(sketch, "E3696", {"start": v(-69.1, 6.49) * mm, "end": v(-69.13, 6.21) * mm});
            skLineSegment(sketch, "E3697", {"start": v(-69.13, 6.21) * mm, "end": v(-69.1, 6.11) * mm});
            skLineSegment(sketch, "E3698", {"start": v(-69.1, 6.11) * mm, "end": v(-69.02, 6.05) * mm});
            skLineSegment(sketch, "E3699", {"start": v(-69.02, 6.05) * mm, "end": v(-68.92, 6.02) * mm});
            skLineSegment(sketch, "E3700", {"start": v(-68.92, 6.02) * mm, "end": v(-68.83, 5.98) * mm});
            skLineSegment(sketch, "E3701", {"start": v(-68.83, 5.98) * mm, "end": v(-68.74, 5.93) * mm});
            skLineSegment(sketch, "E3702", {"start": v(-68.74, 5.93) * mm, "end": v(-68.66, 5.87) * mm});
            skLineSegment(sketch, "E3703", {"start": v(-68.66, 5.87) * mm, "end": v(-68.58, 5.77) * mm});
            skLineSegment(sketch, "E3704", {"start": v(-68.58, 5.77) * mm, "end": v(-68.52, 5.65) * mm});
            skLineSegment(sketch, "E3705", {"start": v(-68.52, 5.65) * mm, "end": v(-68.5, 5.52) * mm});
            skLineSegment(sketch, "E3706", {"start": v(-68.5, 5.52) * mm, "end": v(-68.5, 5.4) * mm});
            skLineSegment(sketch, "E3707", {"start": v(-68.5, 5.4) * mm, "end": v(-68.52, 5.26) * mm});
            skLineSegment(sketch, "E3708", {"start": v(-68.52, 5.26) * mm, "end": v(-68.56, 5.14) * mm});
            skLineSegment(sketch, "E3709", {"start": v(-68.56, 5.14) * mm, "end": v(-68.64, 5.03) * mm});
            skLineSegment(sketch, "E3710", {"start": v(-68.64, 5.03) * mm, "end": v(-68.73, 4.94) * mm});
            skLineSegment(sketch, "E3711", {"start": v(-68.73, 4.94) * mm, "end": v(-68.82, 4.9) * mm});
            skLineSegment(sketch, "E3712", {"start": v(-68.82, 4.9) * mm, "end": v(-68.92, 4.86) * mm});
            skLineSegment(sketch, "E3713", {"start": v(-68.92, 4.86) * mm, "end": v(-69.02, 4.83) * mm});
            skLineSegment(sketch, "E3714", {"start": v(-69.02, 4.83) * mm, "end": v(-69.12, 4.82) * mm});
            skLineSegment(sketch, "E3715", {"start": v(-69.12, 4.82) * mm, "end": v(-69.2, 4.77) * mm});
            skLineSegment(sketch, "E3716", {"start": v(-69.2, 4.77) * mm, "end": v(-69.25, 4.68) * mm});
            skLineSegment(sketch, "E3717", {"start": v(-69.25, 4.68) * mm, "end": v(-69.26, 4.4) * mm});
            skLineSegment(sketch, "E3718", {"start": v(-69.26, 4.4) * mm, "end": v(-69.24, 4.3) * mm});
            skLineSegment(sketch, "E3719", {"start": v(-69.24, 4.3) * mm, "end": v(-69.15, 4.24) * mm});
            skLineSegment(sketch, "E3720", {"start": v(-69.15, 4.24) * mm, "end": v(-69.06, 4.22) * mm});
            skLineSegment(sketch, "E3721", {"start": v(-69.06, 4.22) * mm, "end": v(-68.96, 4.18) * mm});
            skLineSegment(sketch, "E3722", {"start": v(-68.96, 4.18) * mm, "end": v(-68.87, 4.13) * mm});
            skLineSegment(sketch, "E3723", {"start": v(-68.87, 4.13) * mm, "end": v(-68.79, 4.07) * mm});
            skLineSegment(sketch, "E3724", {"start": v(-68.79, 4.07) * mm, "end": v(-68.7, 3.97) * mm});
            skLineSegment(sketch, "E3725", {"start": v(-68.7, 3.97) * mm, "end": v(-68.65, 3.85) * mm});
            skLineSegment(sketch, "E3726", {"start": v(-68.65, 3.85) * mm, "end": v(-68.62, 3.73) * mm});
            skLineSegment(sketch, "E3727", {"start": v(-68.62, 3.73) * mm, "end": v(-68.6, 3.6) * mm});
            skLineSegment(sketch, "E3728", {"start": v(-68.6, 3.6) * mm, "end": v(-68.63, 3.47) * mm});
            skLineSegment(sketch, "E3729", {"start": v(-68.63, 3.47) * mm, "end": v(-68.68, 3.34) * mm});
            skLineSegment(sketch, "E3730", {"start": v(-68.68, 3.34) * mm, "end": v(-68.75, 3.23) * mm});
            skLineSegment(sketch, "E3731", {"start": v(-68.75, 3.23) * mm, "end": v(-68.84, 3.14) * mm});
            skLineSegment(sketch, "E3732", {"start": v(-68.84, 3.14) * mm, "end": v(-68.93, 3.1) * mm});
            skLineSegment(sketch, "E3733", {"start": v(-68.93, 3.1) * mm, "end": v(-69.02, 3.05) * mm});
            skLineSegment(sketch, "E3734", {"start": v(-69.02, 3.05) * mm, "end": v(-69.12, 3.02) * mm});
            skLineSegment(sketch, "E3735", {"start": v(-69.12, 3.02) * mm, "end": v(-69.22, 3) * mm});
            skLineSegment(sketch, "E3736", {"start": v(-69.22, 3) * mm, "end": v(-69.3, 2.96) * mm});
            skLineSegment(sketch, "E3737", {"start": v(-69.3, 2.96) * mm, "end": v(-69.35, 2.86) * mm});
            skLineSegment(sketch, "E3738", {"start": v(-69.35, 2.86) * mm, "end": v(-69.36, 2.59) * mm});
            skLineSegment(sketch, "E3739", {"start": v(-69.36, 2.59) * mm, "end": v(-69.33, 2.49) * mm});
            skLineSegment(sketch, "E3740", {"start": v(-69.33, 2.49) * mm, "end": v(-69.24, 2.43) * mm});
            skLineSegment(sketch, "E3741", {"start": v(-69.24, 2.43) * mm, "end": v(-69.14, 2.4) * mm});
            skLineSegment(sketch, "E3742", {"start": v(-69.14, 2.4) * mm, "end": v(-69.05, 2.37) * mm});
            skLineSegment(sketch, "E3743", {"start": v(-69.05, 2.37) * mm, "end": v(-68.96, 2.33) * mm});
            skLineSegment(sketch, "E3744", {"start": v(-68.96, 2.33) * mm, "end": v(-68.87, 2.27) * mm});
            skLineSegment(sketch, "E3745", {"start": v(-68.87, 2.27) * mm, "end": v(-68.79, 2.17) * mm});
            skLineSegment(sketch, "E3746", {"start": v(-68.79, 2.17) * mm, "end": v(-68.73, 2.06) * mm});
            skLineSegment(sketch, "E3747", {"start": v(-68.73, 2.06) * mm, "end": v(-68.69, 1.93) * mm});
            skLineSegment(sketch, "E3748", {"start": v(-68.69, 1.93) * mm, "end": v(-68.68, 1.8) * mm});
            skLineSegment(sketch, "E3749", {"start": v(-68.68, 1.8) * mm, "end": v(-68.7, 1.67) * mm});
            skLineSegment(sketch, "E3750", {"start": v(-68.7, 1.67) * mm, "end": v(-68.74, 1.54) * mm});
            skLineSegment(sketch, "E3751", {"start": v(-68.74, 1.54) * mm, "end": v(-68.8, 1.43) * mm});
            skLineSegment(sketch, "E3752", {"start": v(-68.8, 1.43) * mm, "end": v(-68.9, 1.34) * mm});
            skLineSegment(sketch, "E3753", {"start": v(-68.9, 1.34) * mm, "end": v(-68.99, 1.28) * mm});
            skLineSegment(sketch, "E3754", {"start": v(-68.99, 1.28) * mm, "end": v(-69.08, 1.24) * mm});
            skLineSegment(sketch, "E3755", {"start": v(-69.08, 1.24) * mm, "end": v(-69.18, 1.21) * mm});
            skLineSegment(sketch, "E3756", {"start": v(-69.18, 1.21) * mm, "end": v(-69.27, 1.2) * mm});
            skLineSegment(sketch, "E3757", {"start": v(-69.27, 1.2) * mm, "end": v(-69.36, 1.15) * mm});
            skLineSegment(sketch, "E3758", {"start": v(-69.36, 1.15) * mm, "end": v(-69.4, 1.05) * mm});
            skLineSegment(sketch, "E3759", {"start": v(-69.4, 1.05) * mm, "end": v(-69.4, 0.77) * mm});
            skLineSegment(sketch, "E3760", {"start": v(-69.4, 0.77) * mm, "end": v(-69.37, 0.67) * mm});
            skLineSegment(sketch, "E3761", {"start": v(-69.37, 0.67) * mm, "end": v(-69.28, 0.62) * mm});
            skLineSegment(sketch, "E3762", {"start": v(-69.28, 0.62) * mm, "end": v(-69.18, 0.6) * mm});
            skLineSegment(sketch, "E3763", {"start": v(-69.18, 0.6) * mm, "end": v(-69.09, 0.57) * mm});
            skLineSegment(sketch, "E3764", {"start": v(-69.09, 0.57) * mm, "end": v(-69, 0.52) * mm});
            skLineSegment(sketch, "E3765", {"start": v(-69, 0.52) * mm, "end": v(-68.9, 0.47) * mm});
            skLineSegment(sketch, "E3766", {"start": v(-68.9, 0.47) * mm, "end": v(-68.82, 0.37) * mm});
            skLineSegment(sketch, "E3767", {"start": v(-68.82, 0.37) * mm, "end": v(-68.76, 0.26) * mm});
            skLineSegment(sketch, "E3768", {"start": v(-68.76, 0.26) * mm, "end": v(-68.72, 0.13) * mm});
            skLineSegment(sketch, "E3769", {"start": v(-68.72, 0.13) * mm, "end": v(-68.7, 0) * mm});
            skLineSegment(sketch, "E3770", {"start": v(-68.7, 0) * mm, "end": v(-68.72, -0.13) * mm});
            skLineSegment(sketch, "E3771", {"start": v(-68.72, -0.13) * mm, "end": v(-68.76, -0.26) * mm});
            skLineSegment(sketch, "E3772", {"start": v(-68.76, -0.26) * mm, "end": v(-68.82, -0.37) * mm});
            skLineSegment(sketch, "E3773", {"start": v(-68.82, -0.37) * mm, "end": v(-68.9, -0.47) * mm});
            skLineSegment(sketch, "E3774", {"start": v(-68.9, -0.47) * mm, "end": v(-69, -0.52) * mm});
            skLineSegment(sketch, "E3775", {"start": v(-69, -0.52) * mm, "end": v(-69.09, -0.57) * mm});
            skLineSegment(sketch, "E3776", {"start": v(-69.09, -0.57) * mm, "end": v(-69.18, -0.6) * mm});
            skLineSegment(sketch, "E3777", {"start": v(-69.18, -0.6) * mm, "end": v(-69.28, -0.62) * mm});
            skLineSegment(sketch, "E3778", {"start": v(-69.28, -0.62) * mm, "end": v(-69.37, -0.67) * mm});
            skLineSegment(sketch, "E3779", {"start": v(-69.37, -0.67) * mm, "end": v(-69.4, -0.77) * mm});
            skLineSegment(sketch, "E3780", {"start": v(-69.4, -0.77) * mm, "end": v(-69.4, -1.05) * mm});
            skLineSegment(sketch, "E3781", {"start": v(-69.4, -1.05) * mm, "end": v(-69.36, -1.15) * mm});
            skLineSegment(sketch, "E3782", {"start": v(-69.36, -1.15) * mm, "end": v(-69.27, -1.2) * mm});
            skLineSegment(sketch, "E3783", {"start": v(-69.27, -1.2) * mm, "end": v(-69.18, -1.21) * mm});
            skLineSegment(sketch, "E3784", {"start": v(-69.18, -1.21) * mm, "end": v(-69.08, -1.24) * mm});
            skLineSegment(sketch, "E3785", {"start": v(-69.08, -1.24) * mm, "end": v(-68.99, -1.28) * mm});
            skLineSegment(sketch, "E3786", {"start": v(-68.99, -1.28) * mm, "end": v(-68.9, -1.34) * mm});
            skLineSegment(sketch, "E3787", {"start": v(-68.9, -1.34) * mm, "end": v(-68.8, -1.43) * mm});
            skLineSegment(sketch, "E3788", {"start": v(-68.8, -1.43) * mm, "end": v(-68.74, -1.54) * mm});
            skLineSegment(sketch, "E3789", {"start": v(-68.74, -1.54) * mm, "end": v(-68.7, -1.67) * mm});
            skLineSegment(sketch, "E3790", {"start": v(-68.7, -1.67) * mm, "end": v(-68.68, -1.8) * mm});
            skLineSegment(sketch, "E3791", {"start": v(-68.68, -1.8) * mm, "end": v(-68.69, -1.93) * mm});
            skLineSegment(sketch, "E3792", {"start": v(-68.69, -1.93) * mm, "end": v(-68.73, -2.06) * mm});
            skLineSegment(sketch, "E3793", {"start": v(-68.73, -2.06) * mm, "end": v(-68.79, -2.17) * mm});
            skLineSegment(sketch, "E3794", {"start": v(-68.79, -2.17) * mm, "end": v(-68.87, -2.27) * mm});
            skLineSegment(sketch, "E3795", {"start": v(-68.87, -2.27) * mm, "end": v(-68.96, -2.33) * mm});
            skLineSegment(sketch, "E3796", {"start": v(-68.96, -2.33) * mm, "end": v(-69.05, -2.37) * mm});
            skLineSegment(sketch, "E3797", {"start": v(-69.05, -2.37) * mm, "end": v(-69.14, -2.4) * mm});
            skLineSegment(sketch, "E3798", {"start": v(-69.14, -2.4) * mm, "end": v(-69.24, -2.43) * mm});
            skLineSegment(sketch, "E3799", {"start": v(-69.24, -2.43) * mm, "end": v(-69.33, -2.49) * mm});
            skLineSegment(sketch, "E3800", {"start": v(-69.33, -2.49) * mm, "end": v(-69.36, -2.59) * mm});
            skLineSegment(sketch, "E3801", {"start": v(-69.36, -2.59) * mm, "end": v(-69.35, -2.86) * mm});
            skLineSegment(sketch, "E3802", {"start": v(-69.35, -2.86) * mm, "end": v(-69.3, -2.96) * mm});
            skLineSegment(sketch, "E3803", {"start": v(-69.3, -2.96) * mm, "end": v(-69.22, -3) * mm});
            skLineSegment(sketch, "E3804", {"start": v(-69.22, -3) * mm, "end": v(-69.12, -3.02) * mm});
            skLineSegment(sketch, "E3805", {"start": v(-69.12, -3.02) * mm, "end": v(-69.02, -3.05) * mm});
            skLineSegment(sketch, "E3806", {"start": v(-69.02, -3.05) * mm, "end": v(-68.93, -3.09) * mm});
            skLineSegment(sketch, "E3807", {"start": v(-68.93, -3.09) * mm, "end": v(-68.84, -3.14) * mm});
            skLineSegment(sketch, "E3808", {"start": v(-68.84, -3.14) * mm, "end": v(-68.75, -3.23) * mm});
            skLineSegment(sketch, "E3809", {"start": v(-68.75, -3.23) * mm, "end": v(-68.68, -3.34) * mm});
            skLineSegment(sketch, "E3810", {"start": v(-68.68, -3.34) * mm, "end": v(-68.63, -3.47) * mm});
            skLineSegment(sketch, "E3811", {"start": v(-68.63, -3.47) * mm, "end": v(-68.6, -3.6) * mm});
            skLineSegment(sketch, "E3812", {"start": v(-68.6, -3.6) * mm, "end": v(-68.62, -3.73) * mm});
            skLineSegment(sketch, "E3813", {"start": v(-68.62, -3.73) * mm, "end": v(-68.65, -3.85) * mm});
            skLineSegment(sketch, "E3814", {"start": v(-68.65, -3.85) * mm, "end": v(-68.7, -3.97) * mm});
            skLineSegment(sketch, "E3815", {"start": v(-68.7, -3.97) * mm, "end": v(-68.79, -4.07) * mm});
            skLineSegment(sketch, "E3816", {"start": v(-68.79, -4.07) * mm, "end": v(-68.87, -4.13) * mm});
            skLineSegment(sketch, "E3817", {"start": v(-68.87, -4.13) * mm, "end": v(-68.96, -4.18) * mm});
            skLineSegment(sketch, "E3818", {"start": v(-68.96, -4.18) * mm, "end": v(-69.06, -4.22) * mm});
            skLineSegment(sketch, "E3819", {"start": v(-69.06, -4.22) * mm, "end": v(-69.15, -4.24) * mm});
            skLineSegment(sketch, "E3820", {"start": v(-69.15, -4.24) * mm, "end": v(-69.24, -4.3) * mm});
            skLineSegment(sketch, "E3821", {"start": v(-69.24, -4.3) * mm, "end": v(-69.26, -4.4) * mm});
            skLineSegment(sketch, "E3822", {"start": v(-69.26, -4.4) * mm, "end": v(-69.25, -4.68) * mm});
            skLineSegment(sketch, "E3823", {"start": v(-69.25, -4.68) * mm, "end": v(-69.2, -4.77) * mm});
            skLineSegment(sketch, "E3824", {"start": v(-69.2, -4.77) * mm, "end": v(-69.12, -4.82) * mm});
            skLineSegment(sketch, "E3825", {"start": v(-69.12, -4.82) * mm, "end": v(-69.02, -4.83) * mm});
            skLineSegment(sketch, "E3826", {"start": v(-69.02, -4.83) * mm, "end": v(-68.92, -4.86) * mm});
            skLineSegment(sketch, "E3827", {"start": v(-68.92, -4.86) * mm, "end": v(-68.82, -4.9) * mm});
            skLineSegment(sketch, "E3828", {"start": v(-68.82, -4.9) * mm, "end": v(-68.73, -4.94) * mm});
            skLineSegment(sketch, "E3829", {"start": v(-68.73, -4.94) * mm, "end": v(-68.64, -5.03) * mm});
            skLineSegment(sketch, "E3830", {"start": v(-68.64, -5.03) * mm, "end": v(-68.56, -5.14) * mm});
            skLineSegment(sketch, "E3831", {"start": v(-68.56, -5.14) * mm, "end": v(-68.52, -5.26) * mm});
            skLineSegment(sketch, "E3832", {"start": v(-68.52, -5.26) * mm, "end": v(-68.5, -5.4) * mm});
            skLineSegment(sketch, "E3833", {"start": v(-68.5, -5.4) * mm, "end": v(-68.5, -5.52) * mm});
            skLineSegment(sketch, "E3834", {"start": v(-68.5, -5.52) * mm, "end": v(-68.52, -5.65) * mm});
            skLineSegment(sketch, "E3835", {"start": v(-68.52, -5.65) * mm, "end": v(-68.58, -5.77) * mm});
            skLineSegment(sketch, "E3836", {"start": v(-68.58, -5.77) * mm, "end": v(-68.66, -5.87) * mm});
            skLineSegment(sketch, "E3837", {"start": v(-68.66, -5.87) * mm, "end": v(-68.74, -5.93) * mm});
            skLineSegment(sketch, "E3838", {"start": v(-68.74, -5.93) * mm, "end": v(-68.83, -5.98) * mm});
            skLineSegment(sketch, "E3839", {"start": v(-68.83, -5.98) * mm, "end": v(-68.92, -6.02) * mm});
            skLineSegment(sketch, "E3840", {"start": v(-68.92, -6.02) * mm, "end": v(-69.02, -6.05) * mm});
            skLineSegment(sketch, "E3841", {"start": v(-69.02, -6.05) * mm, "end": v(-69.1, -6.1) * mm});
            skLineSegment(sketch, "E3842", {"start": v(-69.1, -6.1) * mm, "end": v(-69.13, -6.21) * mm});
            skLineSegment(sketch, "E3843", {"start": v(-69.13, -6.21) * mm, "end": v(-69.1, -6.49) * mm});
            skLineSegment(sketch, "E3844", {"start": v(-69.1, -6.49) * mm, "end": v(-69.06, -6.58) * mm});
            skLineSegment(sketch, "E3845", {"start": v(-69.06, -6.58) * mm, "end": v(-68.97, -6.63) * mm});
            skLineSegment(sketch, "E3846", {"start": v(-68.97, -6.63) * mm, "end": v(-68.87, -6.64) * mm});
            skLineSegment(sketch, "E3847", {"start": v(-68.87, -6.64) * mm, "end": v(-68.77, -6.66) * mm});
            skLineSegment(sketch, "E3848", {"start": v(-68.77, -6.66) * mm, "end": v(-68.67, -6.7) * mm});
            skLineSegment(sketch, "E3849", {"start": v(-68.67, -6.7) * mm, "end": v(-68.58, -6.74) * mm});
            skLineSegment(sketch, "E3850", {"start": v(-68.58, -6.74) * mm, "end": v(-68.48, -6.83) * mm});
            skLineSegment(sketch, "E3851", {"start": v(-68.48, -6.83) * mm, "end": v(-68.4, -6.93) * mm});
            skLineSegment(sketch, "E3852", {"start": v(-68.4, -6.93) * mm, "end": v(-68.35, -7.05) * mm});
            skLineSegment(sketch, "E3853", {"start": v(-68.35, -7.05) * mm, "end": v(-68.33, -7.18) * mm});
            skLineSegment(sketch, "E3854", {"start": v(-68.33, -7.18) * mm, "end": v(-68.33, -7.31) * mm});
            skLineSegment(sketch, "E3855", {"start": v(-68.33, -7.31) * mm, "end": v(-68.35, -7.44) * mm});
            skLineSegment(sketch, "E3856", {"start": v(-68.35, -7.44) * mm, "end": v(-68.4, -7.56) * mm});
            skLineSegment(sketch, "E3857", {"start": v(-68.4, -7.56) * mm, "end": v(-68.48, -7.67) * mm});
            skLineSegment(sketch, "E3858", {"start": v(-68.48, -7.67) * mm, "end": v(-68.56, -7.73) * mm});
            skLineSegment(sketch, "E3859", {"start": v(-68.56, -7.73) * mm, "end": v(-68.65, -7.78) * mm});
            skLineSegment(sketch, "E3860", {"start": v(-68.65, -7.78) * mm, "end": v(-68.74, -7.83) * mm});
            skLineSegment(sketch, "E3861", {"start": v(-68.74, -7.83) * mm, "end": v(-68.84, -7.86) * mm});
            skLineSegment(sketch, "E3862", {"start": v(-68.84, -7.86) * mm, "end": v(-68.92, -7.92) * mm});
            skLineSegment(sketch, "E3863", {"start": v(-68.92, -7.92) * mm, "end": v(-68.94, -8.02) * mm});
            skLineSegment(sketch, "E3864", {"start": v(-68.94, -8.02) * mm, "end": v(-68.9, -8.3) * mm});
            skLineSegment(sketch, "E3865", {"start": v(-68.9, -8.3) * mm, "end": v(-68.86, -8.4) * mm});
            skLineSegment(sketch, "E3866", {"start": v(-68.86, -8.4) * mm, "end": v(-68.77, -8.43) * mm});
            skLineSegment(sketch, "E3867", {"start": v(-68.77, -8.43) * mm, "end": v(-68.67, -8.44) * mm});
            skLineSegment(sketch, "E3868", {"start": v(-68.67, -8.44) * mm, "end": v(-68.57, -8.46) * mm});
            skLineSegment(sketch, "E3869", {"start": v(-68.57, -8.46) * mm, "end": v(-68.47, -8.49) * mm});
            skLineSegment(sketch, "E3870", {"start": v(-68.47, -8.49) * mm, "end": v(-68.38, -8.53) * mm});
            skLineSegment(sketch, "E3871", {"start": v(-68.38, -8.53) * mm, "end": v(-68.28, -8.62) * mm});
            skLineSegment(sketch, "E3872", {"start": v(-68.28, -8.62) * mm, "end": v(-68.2, -8.72) * mm});
            skLineSegment(sketch, "E3873", {"start": v(-68.2, -8.72) * mm, "end": v(-68.15, -8.84) * mm});
            skLineSegment(sketch, "E3874", {"start": v(-68.15, -8.84) * mm, "end": v(-68.12, -8.97) * mm});
            skLineSegment(sketch, "E3875", {"start": v(-68.12, -8.97) * mm, "end": v(-68.11, -9.1) * mm});
            skLineSegment(sketch, "E3876", {"start": v(-68.11, -9.1) * mm, "end": v(-68.13, -9.23) * mm});
            skLineSegment(sketch, "E3877", {"start": v(-68.13, -9.23) * mm, "end": v(-68.18, -9.35) * mm});
            skLineSegment(sketch, "E3878", {"start": v(-68.18, -9.35) * mm, "end": v(-68.26, -9.46) * mm});
            skLineSegment(sketch, "E3879", {"start": v(-68.26, -9.46) * mm, "end": v(-68.34, -9.52) * mm});
            skLineSegment(sketch, "E3880", {"start": v(-68.34, -9.52) * mm, "end": v(-68.42, -9.58) * mm});
            skLineSegment(sketch, "E3881", {"start": v(-68.42, -9.58) * mm, "end": v(-68.51, -9.62) * mm});
            skLineSegment(sketch, "E3882", {"start": v(-68.51, -9.62) * mm, "end": v(-68.6, -9.66) * mm});
            skLineSegment(sketch, "E3883", {"start": v(-68.6, -9.66) * mm, "end": v(-68.69, -9.72) * mm});
            skLineSegment(sketch, "E3884", {"start": v(-68.69, -9.72) * mm, "end": v(-68.7, -9.82) * mm});
            skLineSegment(sketch, "E3885", {"start": v(-68.7, -9.82) * mm, "end": v(-68.67, -10.1) * mm});
            skLineSegment(sketch, "E3886", {"start": v(-68.67, -10.1) * mm, "end": v(-68.62, -10.19) * mm});
            skLineSegment(sketch, "E3887", {"start": v(-68.62, -10.19) * mm, "end": v(-68.53, -10.23) * mm});
            skLineSegment(sketch, "E3888", {"start": v(-68.53, -10.23) * mm, "end": v(-68.43, -10.23) * mm});
            skLineSegment(sketch, "E3889", {"start": v(-68.43, -10.23) * mm, "end": v(-68.33, -10.25) * mm});
            skLineSegment(sketch, "E3890", {"start": v(-68.33, -10.25) * mm, "end": v(-68.23, -10.28) * mm});
            skLineSegment(sketch, "E3891", {"start": v(-68.23, -10.28) * mm, "end": v(-68.13, -10.32) * mm});
            skLineSegment(sketch, "E3892", {"start": v(-68.13, -10.32) * mm, "end": v(-68.03, -10.4) * mm});
            skLineSegment(sketch, "E3893", {"start": v(-68.03, -10.4) * mm, "end": v(-67.95, -10.5) * mm});
            skLineSegment(sketch, "E3894", {"start": v(-67.95, -10.5) * mm, "end": v(-67.9, -10.62) * mm});
            skLineSegment(sketch, "E3895", {"start": v(-67.9, -10.62) * mm, "end": v(-67.86, -10.75) * mm});
            skLineSegment(sketch, "E3896", {"start": v(-67.86, -10.75) * mm, "end": v(-67.85, -10.88) * mm});
            skLineSegment(sketch, "E3897", {"start": v(-67.85, -10.88) * mm, "end": v(-67.87, -11) * mm});
            skLineSegment(sketch, "E3898", {"start": v(-67.87, -11) * mm, "end": v(-67.91, -11.13) * mm});
            skLineSegment(sketch, "E3899", {"start": v(-67.91, -11.13) * mm, "end": v(-67.99, -11.24) * mm});
            skLineSegment(sketch, "E3900", {"start": v(-67.99, -11.24) * mm, "end": v(-68.07, -11.3) * mm});
            skLineSegment(sketch, "E3901", {"start": v(-68.07, -11.3) * mm, "end": v(-68.15, -11.37) * mm});
            skLineSegment(sketch, "E3902", {"start": v(-68.15, -11.37) * mm, "end": v(-68.24, -11.41) * mm});
            skLineSegment(sketch, "E3903", {"start": v(-68.24, -11.41) * mm, "end": v(-68.33, -11.45) * mm});
            skLineSegment(sketch, "E3904", {"start": v(-68.33, -11.45) * mm, "end": v(-68.4, -11.51) * mm});
            skLineSegment(sketch, "E3905", {"start": v(-68.4, -11.51) * mm, "end": v(-68.43, -11.62) * mm});
            skLineSegment(sketch, "E3906", {"start": v(-68.43, -11.62) * mm, "end": v(-68.38, -11.89) * mm});
            skLineSegment(sketch, "E3907", {"start": v(-68.38, -11.89) * mm, "end": v(-68.33, -11.98) * mm});
            skLineSegment(sketch, "E3908", {"start": v(-68.33, -11.98) * mm, "end": v(-68.23, -12.02) * mm});
            skLineSegment(sketch, "E3909", {"start": v(-68.23, -12.02) * mm, "end": v(-68.13, -12.02) * mm});
            skLineSegment(sketch, "E3910", {"start": v(-68.13, -12.02) * mm, "end": v(-68.03, -12.03) * mm});
            skLineSegment(sketch, "E3911", {"start": v(-68.03, -12.03) * mm, "end": v(-67.94, -12.06) * mm});
            skLineSegment(sketch, "E3912", {"start": v(-67.94, -12.06) * mm, "end": v(-67.84, -12.1) * mm});
            skLineSegment(sketch, "E3913", {"start": v(-67.84, -12.1) * mm, "end": v(-67.74, -12.18) * mm});
            skLineSegment(sketch, "E3914", {"start": v(-67.74, -12.18) * mm, "end": v(-67.65, -12.28) * mm});
            skLineSegment(sketch, "E3915", {"start": v(-67.65, -12.28) * mm, "end": v(-67.6, -12.4) * mm});
            skLineSegment(sketch, "E3916", {"start": v(-67.6, -12.4) * mm, "end": v(-67.55, -12.52) * mm});
            skLineSegment(sketch, "E3917", {"start": v(-67.55, -12.52) * mm, "end": v(-67.54, -12.65) * mm});
            skLineSegment(sketch, "E3918", {"start": v(-67.54, -12.65) * mm, "end": v(-67.56, -12.78) * mm});
            skLineSegment(sketch, "E3919", {"start": v(-67.56, -12.78) * mm, "end": v(-67.6, -12.9) * mm});
            skLineSegment(sketch, "E3920", {"start": v(-67.6, -12.9) * mm, "end": v(-67.67, -13.02) * mm});
            skLineSegment(sketch, "E3921", {"start": v(-67.67, -13.02) * mm, "end": v(-67.75, -13.09) * mm});
            skLineSegment(sketch, "E3922", {"start": v(-67.75, -13.09) * mm, "end": v(-67.83, -13.15) * mm});
            skLineSegment(sketch, "E3923", {"start": v(-67.83, -13.15) * mm, "end": v(-67.92, -13.2) * mm});
            skLineSegment(sketch, "E3924", {"start": v(-67.92, -13.2) * mm, "end": v(-68, -13.23) * mm});
            skLineSegment(sketch, "E3925", {"start": v(-68, -13.23) * mm, "end": v(-68.08, -13.3) * mm});
            skLineSegment(sketch, "E3926", {"start": v(-68.08, -13.3) * mm, "end": v(-68.1, -13.4) * mm});
            skLineSegment(sketch, "E3927", {"start": v(-68.1, -13.4) * mm, "end": v(-68.04, -13.67) * mm});
            skLineSegment(sketch, "E3928", {"start": v(-68.04, -13.67) * mm, "end": v(-68, -13.77) * mm});
            skLineSegment(sketch, "E3929", {"start": v(-68, -13.77) * mm, "end": v(-67.9, -13.8) * mm});
            skLineSegment(sketch, "E3930", {"start": v(-67.9, -13.8) * mm, "end": v(-67.8, -13.8) * mm});
            skLineSegment(sketch, "E3931", {"start": v(-67.8, -13.8) * mm, "end": v(-67.7, -13.81) * mm});
            skLineSegment(sketch, "E3932", {"start": v(-67.7, -13.81) * mm, "end": v(-67.6, -13.83) * mm});
            skLineSegment(sketch, "E3933", {"start": v(-67.6, -13.83) * mm, "end": v(-67.5, -13.87) * mm});
            skLineSegment(sketch, "E3934", {"start": v(-67.5, -13.87) * mm, "end": v(-67.4, -13.95) * mm});
            skLineSegment(sketch, "E3935", {"start": v(-67.4, -13.95) * mm, "end": v(-67.3, -14.04) * mm});
            skLineSegment(sketch, "E3936", {"start": v(-67.3, -14.04) * mm, "end": v(-67.24, -14.16) * mm});
            skLineSegment(sketch, "E3937", {"start": v(-67.24, -14.16) * mm, "end": v(-67.2, -14.28) * mm});
            skLineSegment(sketch, "E3938", {"start": v(-67.2, -14.28) * mm, "end": v(-67.19, -14.42) * mm});
            skLineSegment(sketch, "E3939", {"start": v(-67.19, -14.42) * mm, "end": v(-67.2, -14.55) * mm});
            skLineSegment(sketch, "E3940", {"start": v(-67.2, -14.55) * mm, "end": v(-67.24, -14.67) * mm});
            skLineSegment(sketch, "E3941", {"start": v(-67.24, -14.67) * mm, "end": v(-67.3, -14.78) * mm});
            skLineSegment(sketch, "E3942", {"start": v(-67.3, -14.78) * mm, "end": v(-67.38, -14.86) * mm});
            skLineSegment(sketch, "E3943", {"start": v(-67.38, -14.86) * mm, "end": v(-67.46, -14.92) * mm});
            skLineSegment(sketch, "E3944", {"start": v(-67.46, -14.92) * mm, "end": v(-67.55, -14.97) * mm});
            skLineSegment(sketch, "E3945", {"start": v(-67.55, -14.97) * mm, "end": v(-67.64, -15) * mm});
            skLineSegment(sketch, "E3946", {"start": v(-67.64, -15) * mm, "end": v(-67.71, -15.08) * mm});
            skLineSegment(sketch, "E3947", {"start": v(-67.71, -15.08) * mm, "end": v(-67.72, -15.18) * mm});
            skLineSegment(sketch, "E3948", {"start": v(-67.72, -15.18) * mm, "end": v(-67.66, -15.45) * mm});
            skLineSegment(sketch, "E3949", {"start": v(-67.66, -15.45) * mm, "end": v(-67.6, -15.54) * mm});
            skLineSegment(sketch, "E3950", {"start": v(-67.6, -15.54) * mm, "end": v(-67.51, -15.57) * mm});
            skLineSegment(sketch, "E3951", {"start": v(-67.51, -15.57) * mm, "end": v(-67.41, -15.57) * mm});
            skLineSegment(sketch, "E3952", {"start": v(-67.41, -15.57) * mm, "end": v(-67.31, -15.58) * mm});
            skLineSegment(sketch, "E3953", {"start": v(-67.31, -15.58) * mm, "end": v(-67.21, -15.6) * mm});
            skLineSegment(sketch, "E3954", {"start": v(-67.21, -15.6) * mm, "end": v(-67.11, -15.63) * mm});
            skLineSegment(sketch, "E3955", {"start": v(-67.11, -15.63) * mm, "end": v(-67, -15.7) * mm});
            skLineSegment(sketch, "E3956", {"start": v(-67, -15.7) * mm, "end": v(-66.92, -15.8) * mm});
            skLineSegment(sketch, "E3957", {"start": v(-66.92, -15.8) * mm, "end": v(-66.85, -15.91) * mm});
            skLineSegment(sketch, "E3958", {"start": v(-66.85, -15.91) * mm, "end": v(-66.8, -16.04) * mm});
            skLineSegment(sketch, "E3959", {"start": v(-66.8, -16.04) * mm, "end": v(-66.79, -16.17) * mm});
            skLineSegment(sketch, "E3960", {"start": v(-66.79, -16.17) * mm, "end": v(-66.8, -16.3) * mm});
            skLineSegment(sketch, "E3961", {"start": v(-66.8, -16.3) * mm, "end": v(-66.83, -16.43) * mm});
            skLineSegment(sketch, "E3962", {"start": v(-66.83, -16.43) * mm, "end": v(-66.9, -16.54) * mm});
            skLineSegment(sketch, "E3963", {"start": v(-66.9, -16.54) * mm, "end": v(-66.97, -16.61) * mm});
            skLineSegment(sketch, "E3964", {"start": v(-66.97, -16.61) * mm, "end": v(-67.05, -16.68) * mm});
            skLineSegment(sketch, "E3965", {"start": v(-67.05, -16.68) * mm, "end": v(-67.13, -16.73) * mm});
            skLineSegment(sketch, "E3966", {"start": v(-67.13, -16.73) * mm, "end": v(-67.22, -16.77) * mm});
            skLineSegment(sketch, "E3967", {"start": v(-67.22, -16.77) * mm, "end": v(-67.3, -16.84) * mm});
            skLineSegment(sketch, "E3968", {"start": v(-67.3, -16.84) * mm, "end": v(-67.3, -16.95) * mm});
            skLineSegment(sketch, "E3969", {"start": v(-67.3, -16.95) * mm, "end": v(-67.24, -17.22) * mm});
            skLineSegment(sketch, "E3970", {"start": v(-67.24, -17.22) * mm, "end": v(-67.18, -17.3) * mm});
            skLineSegment(sketch, "E3971", {"start": v(-67.18, -17.3) * mm, "end": v(-67.08, -17.33) * mm});
            skLineSegment(sketch, "E3972", {"start": v(-67.08, -17.33) * mm, "end": v(-66.98, -17.33) * mm});
            skLineSegment(sketch, "E3973", {"start": v(-66.98, -17.33) * mm, "end": v(-66.88, -17.33) * mm});
            skLineSegment(sketch, "E3974", {"start": v(-66.88, -17.33) * mm, "end": v(-66.78, -17.35) * mm});
            skLineSegment(sketch, "E3975", {"start": v(-66.78, -17.35) * mm, "end": v(-66.68, -17.38) * mm});
            skLineSegment(sketch, "E3976", {"start": v(-66.68, -17.38) * mm, "end": v(-66.57, -17.45) * mm});
            skLineSegment(sketch, "E3977", {"start": v(-66.57, -17.45) * mm, "end": v(-66.48, -17.55) * mm});
            skLineSegment(sketch, "E3978", {"start": v(-66.48, -17.55) * mm, "end": v(-66.4, -17.66) * mm});
            skLineSegment(sketch, "E3979", {"start": v(-66.4, -17.66) * mm, "end": v(-66.36, -17.78) * mm});
            skLineSegment(sketch, "E3980", {"start": v(-66.36, -17.78) * mm, "end": v(-66.34, -17.91) * mm});
            skLineSegment(sketch, "E3981", {"start": v(-66.34, -17.91) * mm, "end": v(-66.35, -18.04) * mm});
            skLineSegment(sketch, "E3982", {"start": v(-66.35, -18.04) * mm, "end": v(-66.38, -18.17) * mm});
            skLineSegment(sketch, "E3983", {"start": v(-66.38, -18.17) * mm, "end": v(-66.44, -18.29) * mm});
            skLineSegment(sketch, "E3984", {"start": v(-66.44, -18.29) * mm, "end": v(-66.51, -18.36) * mm});
            skLineSegment(sketch, "E3985", {"start": v(-66.51, -18.36) * mm, "end": v(-66.59, -18.43) * mm});
            skLineSegment(sketch, "E3986", {"start": v(-66.59, -18.43) * mm, "end": v(-66.67, -18.48) * mm});
            skLineSegment(sketch, "E3987", {"start": v(-66.67, -18.48) * mm, "end": v(-66.76, -18.53) * mm});
            skLineSegment(sketch, "E3988", {"start": v(-66.76, -18.53) * mm, "end": v(-66.83, -18.6) * mm});
            skLineSegment(sketch, "E3989", {"start": v(-66.83, -18.6) * mm, "end": v(-66.84, -18.7) * mm});
            skLineSegment(sketch, "E3990", {"start": v(-66.84, -18.7) * mm, "end": v(-66.76, -18.97) * mm});
            skLineSegment(sketch, "E3991", {"start": v(-66.76, -18.97) * mm, "end": v(-66.7, -19.06) * mm});
            skLineSegment(sketch, "E3992", {"start": v(-66.7, -19.06) * mm, "end": v(-66.6, -19.08) * mm});
            skLineSegment(sketch, "E3993", {"start": v(-66.6, -19.08) * mm, "end": v(-66.5, -19.08) * mm});
            skLineSegment(sketch, "E3994", {"start": v(-66.5, -19.08) * mm, "end": v(-66.4, -19.08) * mm});
            skLineSegment(sketch, "E3995", {"start": v(-66.4, -19.08) * mm, "end": v(-66.3, -19.1) * mm});
            skLineSegment(sketch, "E3996", {"start": v(-66.3, -19.1) * mm, "end": v(-66.2, -19.12) * mm});
            skLineSegment(sketch, "E3997", {"start": v(-66.2, -19.12) * mm, "end": v(-66.1, -19.2) * mm});
            skLineSegment(sketch, "E3998", {"start": v(-66.1, -19.2) * mm, "end": v(-66, -19.28) * mm});
            skLineSegment(sketch, "E3999", {"start": v(-66, -19.28) * mm, "end": v(-65.92, -19.4) * mm});
            skLineSegment(sketch, "E4000", {"start": v(-65.92, -19.4) * mm, "end": v(-65.87, -19.51) * mm});
            skLineSegment(sketch, "E4001", {"start": v(-65.87, -19.51) * mm, "end": v(-65.85, -19.64) * mm});
            skLineSegment(sketch, "E4002", {"start": v(-65.85, -19.64) * mm, "end": v(-65.85, -19.77) * mm});
            skLineSegment(sketch, "E4003", {"start": v(-65.85, -19.77) * mm, "end": v(-65.88, -19.9) * mm});
            skLineSegment(sketch, "E4004", {"start": v(-65.88, -19.9) * mm, "end": v(-65.94, -20.02) * mm});
            skLineSegment(sketch, "E4005", {"start": v(-65.94, -20.02) * mm, "end": v(-66, -20.1) * mm});
            skLineSegment(sketch, "E4006", {"start": v(-66, -20.1) * mm, "end": v(-66.08, -20.16) * mm});
            skLineSegment(sketch, "E4007", {"start": v(-66.08, -20.16) * mm, "end": v(-66.16, -20.22) * mm});
            skLineSegment(sketch, "E4008", {"start": v(-66.16, -20.22) * mm, "end": v(-66.25, -20.27) * mm});
            skLineSegment(sketch, "E4009", {"start": v(-66.25, -20.27) * mm, "end": v(-66.32, -20.34) * mm});
            skLineSegment(sketch, "E4010", {"start": v(-66.32, -20.34) * mm, "end": v(-66.32, -20.45) * mm});
            skLineSegment(sketch, "E4011", {"start": v(-66.32, -20.45) * mm, "end": v(-66.24, -20.71) * mm});
            skLineSegment(sketch, "E4012", {"start": v(-66.24, -20.71) * mm, "end": v(-66.18, -20.8) * mm});
            skLineSegment(sketch, "E4013", {"start": v(-66.18, -20.8) * mm, "end": v(-66.08, -20.82) * mm});
            skLineSegment(sketch, "E4014", {"start": v(-66.08, -20.82) * mm, "end": v(-65.98, -20.81) * mm});
            skLineSegment(sketch, "E4015", {"start": v(-65.98, -20.81) * mm, "end": v(-65.88, -20.81) * mm});
            skLineSegment(sketch, "E4016", {"start": v(-65.88, -20.81) * mm, "end": v(-65.78, -20.82) * mm});
            skLineSegment(sketch, "E4017", {"start": v(-65.78, -20.82) * mm, "end": v(-65.68, -20.85) * mm});
            skLineSegment(sketch, "E4018", {"start": v(-65.68, -20.85) * mm, "end": v(-65.57, -20.91) * mm});
            skLineSegment(sketch, "E4019", {"start": v(-65.57, -20.91) * mm, "end": v(-65.47, -21) * mm});
            skLineSegment(sketch, "E4020", {"start": v(-65.47, -21) * mm, "end": v(-65.4, -21.1) * mm});
            skLineSegment(sketch, "E4021", {"start": v(-65.4, -21.1) * mm, "end": v(-65.34, -21.23) * mm});
            skLineSegment(sketch, "E4022", {"start": v(-65.34, -21.23) * mm, "end": v(-65.31, -21.36) * mm});
            skLineSegment(sketch, "E4023", {"start": v(-65.31, -21.36) * mm, "end": v(-65.31, -21.5) * mm});
            skLineSegment(sketch, "E4024", {"start": v(-65.31, -21.5) * mm, "end": v(-65.34, -21.62) * mm});
            skLineSegment(sketch, "E4025", {"start": v(-65.34, -21.62) * mm, "end": v(-65.4, -21.74) * mm});
            skLineSegment(sketch, "E4026", {"start": v(-65.4, -21.74) * mm, "end": v(-65.46, -21.82) * mm});
            skLineSegment(sketch, "E4027", {"start": v(-65.46, -21.82) * mm, "end": v(-65.53, -21.89) * mm});
            skLineSegment(sketch, "E4028", {"start": v(-65.53, -21.89) * mm, "end": v(-65.61, -21.95) * mm});
            skLineSegment(sketch, "E4029", {"start": v(-65.61, -21.95) * mm, "end": v(-65.7, -22) * mm});
            skLineSegment(sketch, "E4030", {"start": v(-65.7, -22) * mm, "end": v(-65.76, -22.07) * mm});
            skLineSegment(sketch, "E4031", {"start": v(-65.76, -22.07) * mm, "end": v(-65.77, -22.18) * mm});
            skLineSegment(sketch, "E4032", {"start": v(-65.77, -22.18) * mm, "end": v(-65.68, -22.44) * mm});
            skLineSegment(sketch, "E4033", {"start": v(-65.68, -22.44) * mm, "end": v(-65.61, -22.52) * mm});
            skLineSegment(sketch, "E4034", {"start": v(-65.61, -22.52) * mm, "end": v(-65.51, -22.54) * mm});
            skLineSegment(sketch, "E4035", {"start": v(-65.51, -22.54) * mm, "end": v(-65.41, -22.53) * mm});
            skLineSegment(sketch, "E4036", {"start": v(-65.41, -22.53) * mm, "end": v(-65.31, -22.53) * mm});
            skLineSegment(sketch, "E4037", {"start": v(-65.31, -22.53) * mm, "end": v(-65.21, -22.54) * mm});
            skLineSegment(sketch, "E4038", {"start": v(-65.21, -22.54) * mm, "end": v(-65.11, -22.56) * mm});
            skLineSegment(sketch, "E4039", {"start": v(-65.11, -22.56) * mm, "end": v(-65, -22.62) * mm});
            skLineSegment(sketch, "E4040", {"start": v(-65, -22.62) * mm, "end": v(-64.9, -22.7) * mm});
            skLineSegment(sketch, "E4041", {"start": v(-64.9, -22.7) * mm, "end": v(-64.82, -22.81) * mm});
            skLineSegment(sketch, "E4042", {"start": v(-64.82, -22.81) * mm, "end": v(-64.76, -22.93) * mm});
            skLineSegment(sketch, "E4043", {"start": v(-64.76, -22.93) * mm, "end": v(-64.73, -23.06) * mm});
            skLineSegment(sketch, "E4044", {"start": v(-64.73, -23.06) * mm, "end": v(-64.73, -23.2) * mm});
            skLineSegment(sketch, "E4045", {"start": v(-64.73, -23.2) * mm, "end": v(-64.75, -23.32) * mm});
            skLineSegment(sketch, "E4046", {"start": v(-64.75, -23.32) * mm, "end": v(-64.8, -23.44) * mm});
            skLineSegment(sketch, "E4047", {"start": v(-64.8, -23.44) * mm, "end": v(-64.86, -23.52) * mm});
            skLineSegment(sketch, "E4048", {"start": v(-64.86, -23.52) * mm, "end": v(-64.94, -23.6) * mm});
            skLineSegment(sketch, "E4049", {"start": v(-64.94, -23.6) * mm, "end": v(-65.02, -23.66) * mm});
            skLineSegment(sketch, "E4050", {"start": v(-65.02, -23.66) * mm, "end": v(-65.1, -23.7) * mm});
            skLineSegment(sketch, "E4051", {"start": v(-65.1, -23.7) * mm, "end": v(-65.16, -23.79) * mm});
            skLineSegment(sketch, "E4052", {"start": v(-65.16, -23.79) * mm, "end": v(-65.16, -23.9) * mm});
            skLineSegment(sketch, "E4053", {"start": v(-65.16, -23.9) * mm, "end": v(-65.07, -24.15) * mm});
            skLineSegment(sketch, "E4054", {"start": v(-65.07, -24.15) * mm, "end": v(-65, -24.23) * mm});
            skLineSegment(sketch, "E4055", {"start": v(-65, -24.23) * mm, "end": v(-64.9, -24.25) * mm});
            skLineSegment(sketch, "E4056", {"start": v(-64.9, -24.25) * mm, "end": v(-64.8, -24.23) * mm});
            skLineSegment(sketch, "E4057", {"start": v(-64.8, -24.23) * mm, "end": v(-64.7, -24.23) * mm});
            skLineSegment(sketch, "E4058", {"start": v(-64.7, -24.23) * mm, "end": v(-64.6, -24.24) * mm});
            skLineSegment(sketch, "E4059", {"start": v(-64.6, -24.24) * mm, "end": v(-64.5, -24.26) * mm});
            skLineSegment(sketch, "E4060", {"start": v(-64.5, -24.26) * mm, "end": v(-64.38, -24.32) * mm});
            skLineSegment(sketch, "E4061", {"start": v(-64.38, -24.32) * mm, "end": v(-64.28, -24.4) * mm});
            skLineSegment(sketch, "E4062", {"start": v(-64.28, -24.4) * mm, "end": v(-64.2, -24.5) * mm});
            skLineSegment(sketch, "E4063", {"start": v(-64.2, -24.5) * mm, "end": v(-64.14, -24.62) * mm});
            skLineSegment(sketch, "E4064", {"start": v(-64.14, -24.62) * mm, "end": v(-64.1, -24.75) * mm});
            skLineSegment(sketch, "E4065", {"start": v(-64.1, -24.75) * mm, "end": v(-64.1, -24.88) * mm});
            skLineSegment(sketch, "E4066", {"start": v(-64.1, -24.88) * mm, "end": v(-64.12, -25) * mm});
            skLineSegment(sketch, "E4067", {"start": v(-64.12, -25) * mm, "end": v(-64.16, -25.13) * mm});
            skLineSegment(sketch, "E4068", {"start": v(-64.16, -25.13) * mm, "end": v(-64.23, -25.21) * mm});
            skLineSegment(sketch, "E4069", {"start": v(-64.23, -25.21) * mm, "end": v(-64.3, -25.29) * mm});
            skLineSegment(sketch, "E4070", {"start": v(-64.3, -25.29) * mm, "end": v(-64.37, -25.35) * mm});
            skLineSegment(sketch, "E4071", {"start": v(-64.37, -25.35) * mm, "end": v(-64.46, -25.4) * mm});
            skLineSegment(sketch, "E4072", {"start": v(-64.46, -25.4) * mm, "end": v(-64.52, -25.48) * mm});
            skLineSegment(sketch, "E4073", {"start": v(-64.52, -25.48) * mm, "end": v(-64.51, -25.6) * mm});
            skLineSegment(sketch, "E4074", {"start": v(-64.51, -25.6) * mm, "end": v(-64.41, -25.85) * mm});
            skLineSegment(sketch, "E4075", {"start": v(-64.41, -25.85) * mm, "end": v(-64.34, -25.93) * mm});
            skLineSegment(sketch, "E4076", {"start": v(-64.34, -25.93) * mm, "end": v(-64.24, -25.94) * mm});
            skLineSegment(sketch, "E4077", {"start": v(-64.24, -25.94) * mm, "end": v(-64.15, -25.92) * mm});
            skLineSegment(sketch, "E4078", {"start": v(-64.15, -25.92) * mm, "end": v(-64.05, -25.92) * mm});
            skLineSegment(sketch, "E4079", {"start": v(-64.05, -25.92) * mm, "end": v(-63.94, -25.92) * mm});
            skLineSegment(sketch, "E4080", {"start": v(-63.94, -25.92) * mm, "end": v(-63.84, -25.94) * mm});
            skLineSegment(sketch, "E4081", {"start": v(-63.84, -25.94) * mm, "end": v(-63.72, -26) * mm});
            skLineSegment(sketch, "E4082", {"start": v(-63.72, -26) * mm, "end": v(-63.62, -26.07) * mm});
            skLineSegment(sketch, "E4083", {"start": v(-63.62, -26.07) * mm, "end": v(-63.54, -26.18) * mm});
            skLineSegment(sketch, "E4084", {"start": v(-63.54, -26.18) * mm, "end": v(-63.47, -26.3) * mm});
            skLineSegment(sketch, "E4085", {"start": v(-63.47, -26.3) * mm, "end": v(-63.44, -26.42) * mm});
            skLineSegment(sketch, "E4086", {"start": v(-63.44, -26.42) * mm, "end": v(-63.42, -26.55) * mm});
            skLineSegment(sketch, "E4087", {"start": v(-63.42, -26.55) * mm, "end": v(-63.44, -26.68) * mm});
            skLineSegment(sketch, "E4088", {"start": v(-63.44, -26.68) * mm, "end": v(-63.48, -26.8) * mm});
            skLineSegment(sketch, "E4089", {"start": v(-63.48, -26.8) * mm, "end": v(-63.54, -26.89) * mm});
            skLineSegment(sketch, "E4090", {"start": v(-63.54, -26.89) * mm, "end": v(-63.61, -26.96) * mm});
            skLineSegment(sketch, "E4091", {"start": v(-63.61, -26.96) * mm, "end": v(-63.69, -27.03) * mm});
            skLineSegment(sketch, "E4092", {"start": v(-63.69, -27.03) * mm, "end": v(-63.77, -27.08) * mm});
            skLineSegment(sketch, "E4093", {"start": v(-63.77, -27.08) * mm, "end": v(-63.83, -27.16) * mm});
            skLineSegment(sketch, "E4094", {"start": v(-63.83, -27.16) * mm, "end": v(-63.82, -27.27) * mm});
            skLineSegment(sketch, "E4095", {"start": v(-63.82, -27.27) * mm, "end": v(-63.71, -27.52) * mm});
            skLineSegment(sketch, "E4096", {"start": v(-63.71, -27.52) * mm, "end": v(-63.64, -27.6) * mm});
            skLineSegment(sketch, "E4097", {"start": v(-63.64, -27.6) * mm, "end": v(-63.54, -27.61) * mm});
            skLineSegment(sketch, "E4098", {"start": v(-63.54, -27.61) * mm, "end": v(-63.45, -27.6) * mm});
            skLineSegment(sketch, "E4099", {"start": v(-63.45, -27.6) * mm, "end": v(-63.34, -27.58) * mm});
            skLineSegment(sketch, "E4100", {"start": v(-63.34, -27.58) * mm, "end": v(-63.24, -27.59) * mm});
            skLineSegment(sketch, "E4101", {"start": v(-63.24, -27.59) * mm, "end": v(-63.14, -27.6) * mm});
            skLineSegment(sketch, "E4102", {"start": v(-63.14, -27.6) * mm, "end": v(-63.02, -27.65) * mm});
            skLineSegment(sketch, "E4103", {"start": v(-63.02, -27.65) * mm, "end": v(-62.92, -27.73) * mm});
            skLineSegment(sketch, "E4104", {"start": v(-62.92, -27.73) * mm, "end": v(-62.83, -27.83) * mm});
            skLineSegment(sketch, "E4105", {"start": v(-62.83, -27.83) * mm, "end": v(-62.76, -27.94) * mm});
            skLineSegment(sketch, "E4106", {"start": v(-62.76, -27.94) * mm, "end": v(-62.72, -28.07) * mm});
            skLineSegment(sketch, "E4107", {"start": v(-62.72, -28.07) * mm, "end": v(-62.7, -28.2) * mm});
            skLineSegment(sketch, "E4108", {"start": v(-62.7, -28.2) * mm, "end": v(-62.72, -28.33) * mm});
            skLineSegment(sketch, "E4109", {"start": v(-62.72, -28.33) * mm, "end": v(-62.76, -28.45) * mm});
            skLineSegment(sketch, "E4110", {"start": v(-62.76, -28.45) * mm, "end": v(-62.82, -28.54) * mm});
            skLineSegment(sketch, "E4111", {"start": v(-62.82, -28.54) * mm, "end": v(-62.88, -28.62) * mm});
            skLineSegment(sketch, "E4112", {"start": v(-62.88, -28.62) * mm, "end": v(-62.96, -28.69) * mm});
            skLineSegment(sketch, "E4113", {"start": v(-62.96, -28.69) * mm, "end": v(-63.04, -28.74) * mm});
            skLineSegment(sketch, "E4114", {"start": v(-63.04, -28.74) * mm, "end": v(-63.1, -28.83) * mm});
            skLineSegment(sketch, "E4115", {"start": v(-63.1, -28.83) * mm, "end": v(-63.09, -28.93) * mm});
            skLineSegment(sketch, "E4116", {"start": v(-63.09, -28.93) * mm, "end": v(-62.97, -29.18) * mm});
            skLineSegment(sketch, "E4117", {"start": v(-62.97, -29.18) * mm, "end": v(-62.9, -29.26) * mm});
            skLineSegment(sketch, "E4118", {"start": v(-62.9, -29.26) * mm, "end": v(-62.8, -29.27) * mm});
            skLineSegment(sketch, "E4119", {"start": v(-62.8, -29.27) * mm, "end": v(-62.7, -29.24) * mm});
            skLineSegment(sketch, "E4120", {"start": v(-62.7, -29.24) * mm, "end": v(-62.6, -29.23) * mm});
            skLineSegment(sketch, "E4121", {"start": v(-62.6, -29.23) * mm, "end": v(-62.5, -29.23) * mm});
            skLineSegment(sketch, "E4122", {"start": v(-62.5, -29.23) * mm, "end": v(-62.4, -29.24) * mm});
            skLineSegment(sketch, "E4123", {"start": v(-62.4, -29.24) * mm, "end": v(-62.28, -29.3) * mm});
            skLineSegment(sketch, "E4124", {"start": v(-62.28, -29.3) * mm, "end": v(-62.17, -29.37) * mm});
            skLineSegment(sketch, "E4125", {"start": v(-62.17, -29.37) * mm, "end": v(-62.08, -29.46) * mm});
            skLineSegment(sketch, "E4126", {"start": v(-62.08, -29.46) * mm, "end": v(-62.01, -29.58) * mm});
            skLineSegment(sketch, "E4127", {"start": v(-62.01, -29.58) * mm, "end": v(-61.97, -29.7) * mm});
            skLineSegment(sketch, "E4128", {"start": v(-61.97, -29.7) * mm, "end": v(-61.95, -29.83) * mm});
            skLineSegment(sketch, "E4129", {"start": v(-61.95, -29.83) * mm, "end": v(-61.96, -29.96) * mm});
            skLineSegment(sketch, "E4130", {"start": v(-61.96, -29.96) * mm, "end": v(-62, -30.09) * mm});
            skLineSegment(sketch, "E4131", {"start": v(-62, -30.09) * mm, "end": v(-62.05, -30.17) * mm});
            skLineSegment(sketch, "E4132", {"start": v(-62.05, -30.17) * mm, "end": v(-62.11, -30.25) * mm});
            skLineSegment(sketch, "E4133", {"start": v(-62.11, -30.25) * mm, "end": v(-62.19, -30.32) * mm});
            skLineSegment(sketch, "E4134", {"start": v(-62.19, -30.32) * mm, "end": v(-62.27, -30.38) * mm});
            skLineSegment(sketch, "E4135", {"start": v(-62.27, -30.38) * mm, "end": v(-62.32, -30.47) * mm});
            skLineSegment(sketch, "E4136", {"start": v(-62.32, -30.47) * mm, "end": v(-62.3, -30.57) * mm});
            skLineSegment(sketch, "E4137", {"start": v(-62.3, -30.57) * mm, "end": v(-62.19, -30.82) * mm});
            skLineSegment(sketch, "E4138", {"start": v(-62.19, -30.82) * mm, "end": v(-62.11, -30.9) * mm});
            skLineSegment(sketch, "E4139", {"start": v(-62.11, -30.9) * mm, "end": v(-62.01, -30.9) * mm});
            skLineSegment(sketch, "E4140", {"start": v(-62.01, -30.9) * mm, "end": v(-61.91, -30.88) * mm});
            skLineSegment(sketch, "E4141", {"start": v(-61.91, -30.88) * mm, "end": v(-61.81, -30.86) * mm});
            skLineSegment(sketch, "E4142", {"start": v(-61.81, -30.86) * mm, "end": v(-61.71, -30.86) * mm});
            skLineSegment(sketch, "E4143", {"start": v(-61.71, -30.86) * mm, "end": v(-61.6, -30.87) * mm});
            skLineSegment(sketch, "E4144", {"start": v(-61.6, -30.87) * mm, "end": v(-61.49, -30.91) * mm});
            skLineSegment(sketch, "E4145", {"start": v(-61.49, -30.91) * mm, "end": v(-61.38, -30.99) * mm});
            skLineSegment(sketch, "E4146", {"start": v(-61.38, -30.99) * mm, "end": v(-61.29, -31.08) * mm});
            skLineSegment(sketch, "E4147", {"start": v(-61.29, -31.08) * mm, "end": v(-61.22, -31.2) * mm});
            skLineSegment(sketch, "E4148", {"start": v(-61.22, -31.2) * mm, "end": v(-61.17, -31.31) * mm});
            skLineSegment(sketch, "E4149", {"start": v(-61.17, -31.31) * mm, "end": v(-61.15, -31.44) * mm});
            skLineSegment(sketch, "E4150", {"start": v(-61.15, -31.44) * mm, "end": v(-61.15, -31.57) * mm});
            skLineSegment(sketch, "E4151", {"start": v(-61.15, -31.57) * mm, "end": v(-61.19, -31.7) * mm});
            skLineSegment(sketch, "E4152", {"start": v(-61.19, -31.7) * mm, "end": v(-61.24, -31.79) * mm});
            skLineSegment(sketch, "E4153", {"start": v(-61.24, -31.79) * mm, "end": v(-61.3, -31.87) * mm});
            skLineSegment(sketch, "E4154", {"start": v(-61.3, -31.87) * mm, "end": v(-61.37, -31.94) * mm});
            skLineSegment(sketch, "E4155", {"start": v(-61.37, -31.94) * mm, "end": v(-61.45, -32) * mm});
            skLineSegment(sketch, "E4156", {"start": v(-61.45, -32) * mm, "end": v(-61.5, -32.09) * mm});
            skLineSegment(sketch, "E4157", {"start": v(-61.5, -32.09) * mm, "end": v(-61.49, -32.2) * mm});
            skLineSegment(sketch, "E4158", {"start": v(-61.49, -32.2) * mm, "end": v(-61.36, -32.44) * mm});
            skLineSegment(sketch, "E4159", {"start": v(-61.36, -32.44) * mm, "end": v(-61.28, -32.51) * mm});
            skLineSegment(sketch, "E4160", {"start": v(-61.28, -32.51) * mm, "end": v(-61.18, -32.51) * mm});
            skLineSegment(sketch, "E4161", {"start": v(-61.18, -32.51) * mm, "end": v(-61.08, -32.49) * mm});
            skLineSegment(sketch, "E4162", {"start": v(-61.08, -32.49) * mm, "end": v(-60.99, -32.47) * mm});
            skLineSegment(sketch, "E4163", {"start": v(-60.99, -32.47) * mm, "end": v(-60.88, -32.46) * mm});
            skLineSegment(sketch, "E4164", {"start": v(-60.88, -32.46) * mm, "end": v(-60.78, -32.47) * mm});
            skLineSegment(sketch, "E4165", {"start": v(-60.78, -32.47) * mm, "end": v(-60.66, -32.51) * mm});
            skLineSegment(sketch, "E4166", {"start": v(-60.66, -32.51) * mm, "end": v(-60.55, -32.58) * mm});
            skLineSegment(sketch, "E4167", {"start": v(-60.55, -32.58) * mm, "end": v(-60.45, -32.67) * mm});
            skLineSegment(sketch, "E4168", {"start": v(-60.45, -32.67) * mm, "end": v(-60.38, -32.78) * mm});
            skLineSegment(sketch, "E4169", {"start": v(-60.38, -32.78) * mm, "end": v(-60.33, -32.9) * mm});
            skLineSegment(sketch, "E4170", {"start": v(-60.33, -32.9) * mm, "end": v(-60.3, -33.03) * mm});
            skLineSegment(sketch, "E4171", {"start": v(-60.3, -33.03) * mm, "end": v(-60.3, -33.16) * mm});
            skLineSegment(sketch, "E4172", {"start": v(-60.3, -33.16) * mm, "end": v(-60.34, -33.3) * mm});
            skLineSegment(sketch, "E4173", {"start": v(-60.34, -33.3) * mm, "end": v(-60.39, -33.38) * mm});
            skLineSegment(sketch, "E4174", {"start": v(-60.39, -33.38) * mm, "end": v(-60.45, -33.46) * mm});
            skLineSegment(sketch, "E4175", {"start": v(-60.45, -33.46) * mm, "end": v(-60.51, -33.54) * mm});
            skLineSegment(sketch, "E4176", {"start": v(-60.51, -33.54) * mm, "end": v(-60.6, -33.6) * mm});
            skLineSegment(sketch, "E4177", {"start": v(-60.6, -33.6) * mm, "end": v(-60.64, -33.69) * mm});
            skLineSegment(sketch, "E4178", {"start": v(-60.64, -33.69) * mm, "end": v(-60.62, -33.8) * mm});
            skLineSegment(sketch, "E4179", {"start": v(-60.62, -33.8) * mm, "end": v(-60.49, -34.03) * mm});
            skLineSegment(sketch, "E4180", {"start": v(-60.49, -34.03) * mm, "end": v(-60.4, -34.1) * mm});
            skLineSegment(sketch, "E4181", {"start": v(-60.4, -34.1) * mm, "end": v(-60.3, -34.1) * mm});
            skLineSegment(sketch, "E4182", {"start": v(-60.3, -34.1) * mm, "end": v(-60.21, -34.07) * mm});
            skLineSegment(sketch, "E4183", {"start": v(-60.21, -34.07) * mm, "end": v(-60.11, -34.05) * mm});
            skLineSegment(sketch, "E4184", {"start": v(-60.11, -34.05) * mm, "end": v(-60.01, -34.05) * mm});
            skLineSegment(sketch, "E4185", {"start": v(-60.01, -34.05) * mm, "end": v(-59.9, -34.05) * mm});
            skLineSegment(sketch, "E4186", {"start": v(-59.9, -34.05) * mm, "end": v(-59.78, -34.09) * mm});
            skLineSegment(sketch, "E4187", {"start": v(-59.78, -34.09) * mm, "end": v(-59.67, -34.16) * mm});
            skLineSegment(sketch, "E4188", {"start": v(-59.67, -34.16) * mm, "end": v(-59.58, -34.24) * mm});
            skLineSegment(sketch, "E4189", {"start": v(-59.58, -34.24) * mm, "end": v(-59.5, -34.35) * mm});
            skLineSegment(sketch, "E4190", {"start": v(-59.5, -34.35) * mm, "end": v(-59.44, -34.47) * mm});
            skLineSegment(sketch, "E4191", {"start": v(-59.44, -34.47) * mm, "end": v(-59.42, -34.6) * mm});
            skLineSegment(sketch, "E4192", {"start": v(-59.42, -34.6) * mm, "end": v(-59.41, -34.73) * mm});
            skLineSegment(sketch, "E4193", {"start": v(-59.41, -34.73) * mm, "end": v(-59.44, -34.86) * mm});
            skLineSegment(sketch, "E4194", {"start": v(-59.44, -34.86) * mm, "end": v(-59.5, -34.95) * mm});
            skLineSegment(sketch, "E4195", {"start": v(-59.5, -34.95) * mm, "end": v(-59.55, -35.03) * mm});
            skLineSegment(sketch, "E4196", {"start": v(-59.55, -35.03) * mm, "end": v(-59.62, -35.1) * mm});
            skLineSegment(sketch, "E4197", {"start": v(-59.62, -35.1) * mm, "end": v(-59.7, -35.18) * mm});
            skLineSegment(sketch, "E4198", {"start": v(-59.7, -35.18) * mm, "end": v(-59.74, -35.26) * mm});
            skLineSegment(sketch, "E4199", {"start": v(-59.74, -35.26) * mm, "end": v(-59.72, -35.37) * mm});
            skLineSegment(sketch, "E4200", {"start": v(-59.72, -35.37) * mm, "end": v(-59.58, -35.6) * mm});
            skLineSegment(sketch, "E4201", {"start": v(-59.58, -35.6) * mm, "end": v(-59.5, -35.67) * mm});
            skLineSegment(sketch, "E4202", {"start": v(-59.5, -35.67) * mm, "end": v(-59.4, -35.67) * mm});
            skLineSegment(sketch, "E4203", {"start": v(-59.4, -35.67) * mm, "end": v(-59.3, -35.64) * mm});
            skLineSegment(sketch, "E4204", {"start": v(-59.3, -35.64) * mm, "end": v(-59.2, -35.62) * mm});
            skLineSegment(sketch, "E4205", {"start": v(-59.2, -35.62) * mm, "end": v(-59.1, -35.6) * mm});
            skLineSegment(sketch, "E4206", {"start": v(-59.1, -35.6) * mm, "end": v(-59, -35.6) * mm});
            skLineSegment(sketch, "E4207", {"start": v(-59, -35.6) * mm, "end": v(-58.87, -35.64) * mm});
            skLineSegment(sketch, "E4208", {"start": v(-58.87, -35.64) * mm, "end": v(-58.76, -35.7) * mm});
            skLineSegment(sketch, "E4209", {"start": v(-58.76, -35.7) * mm, "end": v(-58.66, -35.8) * mm});
            skLineSegment(sketch, "E4210", {"start": v(-58.66, -35.8) * mm, "end": v(-58.58, -35.9) * mm});
            skLineSegment(sketch, "E4211", {"start": v(-58.58, -35.9) * mm, "end": v(-58.52, -36.02) * mm});
            skLineSegment(sketch, "E4212", {"start": v(-58.52, -36.02) * mm, "end": v(-58.49, -36.14) * mm});
            skLineSegment(sketch, "E4213", {"start": v(-58.49, -36.14) * mm, "end": v(-58.49, -36.27) * mm});
            skLineSegment(sketch, "E4214", {"start": v(-58.49, -36.27) * mm, "end": v(-58.51, -36.4) * mm});
            skLineSegment(sketch, "E4215", {"start": v(-58.51, -36.4) * mm, "end": v(-58.56, -36.5) * mm});
            skLineSegment(sketch, "E4216", {"start": v(-58.56, -36.5) * mm, "end": v(-58.61, -36.58) * mm});
            skLineSegment(sketch, "E4217", {"start": v(-58.61, -36.58) * mm, "end": v(-58.68, -36.66) * mm});
            skLineSegment(sketch, "E4218", {"start": v(-58.68, -36.66) * mm, "end": v(-58.75, -36.73) * mm});
            skLineSegment(sketch, "E4219", {"start": v(-58.75, -36.73) * mm, "end": v(-58.8, -36.81) * mm});
            skLineSegment(sketch, "E4220", {"start": v(-58.8, -36.81) * mm, "end": v(-58.77, -36.92) * mm});
            skLineSegment(sketch, "E4221", {"start": v(-58.77, -36.92) * mm, "end": v(-58.62, -37.15) * mm});
            skLineSegment(sketch, "E4222", {"start": v(-58.62, -37.15) * mm, "end": v(-58.54, -37.22) * mm});
            skLineSegment(sketch, "E4223", {"start": v(-58.54, -37.22) * mm, "end": v(-58.44, -37.21) * mm});
            skLineSegment(sketch, "E4224", {"start": v(-58.44, -37.21) * mm, "end": v(-58.35, -37.18) * mm});
            skLineSegment(sketch, "E4225", {"start": v(-58.35, -37.18) * mm, "end": v(-58.25, -37.15) * mm});
            skLineSegment(sketch, "E4226", {"start": v(-58.25, -37.15) * mm, "end": v(-58.15, -37.14) * mm});
            skLineSegment(sketch, "E4227", {"start": v(-58.15, -37.14) * mm, "end": v(-58.05, -37.14) * mm});
            skLineSegment(sketch, "E4228", {"start": v(-58.05, -37.14) * mm, "end": v(-57.92, -37.17) * mm});
            skLineSegment(sketch, "E4229", {"start": v(-57.92, -37.17) * mm, "end": v(-57.8, -37.23) * mm});
            skLineSegment(sketch, "E4230", {"start": v(-57.8, -37.23) * mm, "end": v(-57.7, -37.32) * mm});
            skLineSegment(sketch, "E4231", {"start": v(-57.7, -37.32) * mm, "end": v(-57.62, -37.42) * mm});
            skLineSegment(sketch, "E4232", {"start": v(-57.62, -37.42) * mm, "end": v(-57.56, -37.54) * mm});
            skLineSegment(sketch, "E4233", {"start": v(-57.56, -37.54) * mm, "end": v(-57.52, -37.66) * mm});
            skLineSegment(sketch, "E4234", {"start": v(-57.52, -37.66) * mm, "end": v(-57.52, -37.8) * mm});
            skLineSegment(sketch, "E4235", {"start": v(-57.52, -37.8) * mm, "end": v(-57.54, -37.92) * mm});
            skLineSegment(sketch, "E4236", {"start": v(-57.54, -37.92) * mm, "end": v(-57.58, -38.02) * mm});
            skLineSegment(sketch, "E4237", {"start": v(-57.58, -38.02) * mm, "end": v(-57.63, -38.1) * mm});
            skLineSegment(sketch, "E4238", {"start": v(-57.63, -38.1) * mm, "end": v(-57.7, -38.18) * mm});
            skLineSegment(sketch, "E4239", {"start": v(-57.7, -38.18) * mm, "end": v(-57.77, -38.25) * mm});
            skLineSegment(sketch, "E4240", {"start": v(-57.77, -38.25) * mm, "end": v(-57.81, -38.34) * mm});
            skLineSegment(sketch, "E4241", {"start": v(-57.81, -38.34) * mm, "end": v(-57.78, -38.44) * mm});
            skLineSegment(sketch, "E4242", {"start": v(-57.78, -38.44) * mm, "end": v(-57.63, -38.67) * mm});
            skLineSegment(sketch, "E4243", {"start": v(-57.63, -38.67) * mm, "end": v(-57.55, -38.74) * mm});
            skLineSegment(sketch, "E4244", {"start": v(-57.55, -38.74) * mm, "end": v(-57.45, -38.73) * mm});
            skLineSegment(sketch, "E4245", {"start": v(-57.45, -38.73) * mm, "end": v(-57.35, -38.7) * mm});
            skLineSegment(sketch, "E4246", {"start": v(-57.35, -38.7) * mm, "end": v(-57.26, -38.67) * mm});
            skLineSegment(sketch, "E4247", {"start": v(-57.26, -38.67) * mm, "end": v(-57.16, -38.65) * mm});
            skLineSegment(sketch, "E4248", {"start": v(-57.16, -38.65) * mm, "end": v(-57.05, -38.65) * mm});
            skLineSegment(sketch, "E4249", {"start": v(-57.05, -38.65) * mm, "end": v(-56.93, -38.67) * mm});
            skLineSegment(sketch, "E4250", {"start": v(-56.93, -38.67) * mm, "end": v(-56.8, -38.73) * mm});
            skLineSegment(sketch, "E4251", {"start": v(-56.8, -38.73) * mm, "end": v(-56.7, -38.81) * mm});
            skLineSegment(sketch, "E4252", {"start": v(-56.7, -38.81) * mm, "end": v(-56.62, -38.91) * mm});
            skLineSegment(sketch, "E4253", {"start": v(-56.62, -38.91) * mm, "end": v(-56.56, -39.03) * mm});
            skLineSegment(sketch, "E4254", {"start": v(-56.56, -39.03) * mm, "end": v(-56.52, -39.16) * mm});
            skLineSegment(sketch, "E4255", {"start": v(-56.52, -39.16) * mm, "end": v(-56.5, -39.29) * mm});
            skLineSegment(sketch, "E4256", {"start": v(-56.5, -39.29) * mm, "end": v(-56.53, -39.41) * mm});
            skLineSegment(sketch, "E4257", {"start": v(-56.53, -39.41) * mm, "end": v(-56.57, -39.5) * mm});
            skLineSegment(sketch, "E4258", {"start": v(-56.57, -39.5) * mm, "end": v(-56.62, -39.6) * mm});
            skLineSegment(sketch, "E4259", {"start": v(-56.62, -39.6) * mm, "end": v(-56.68, -39.68) * mm});
            skLineSegment(sketch, "E4260", {"start": v(-56.68, -39.68) * mm, "end": v(-56.75, -39.75) * mm});
            skLineSegment(sketch, "E4261", {"start": v(-56.75, -39.75) * mm, "end": v(-56.79, -39.84) * mm});
            skLineSegment(sketch, "E4262", {"start": v(-56.79, -39.84) * mm, "end": v(-56.76, -39.94) * mm});
            skLineSegment(sketch, "E4263", {"start": v(-56.76, -39.94) * mm, "end": v(-56.6, -40.17) * mm});
            skLineSegment(sketch, "E4264", {"start": v(-56.6, -40.17) * mm, "end": v(-56.51, -40.23) * mm});
            skLineSegment(sketch, "E4265", {"start": v(-56.51, -40.23) * mm, "end": v(-56.41, -40.22) * mm});
            skLineSegment(sketch, "E4266", {"start": v(-56.41, -40.22) * mm, "end": v(-56.32, -40.18) * mm});
            skLineSegment(sketch, "E4267", {"start": v(-56.32, -40.18) * mm, "end": v(-56.23, -40.15) * mm});
            skLineSegment(sketch, "E4268", {"start": v(-56.23, -40.15) * mm, "end": v(-56.13, -40.13) * mm});
            skLineSegment(sketch, "E4269", {"start": v(-56.13, -40.13) * mm, "end": v(-56.02, -40.13) * mm});
            skLineSegment(sketch, "E4270", {"start": v(-56.02, -40.13) * mm, "end": v(-55.9, -40.15) * mm});
            skLineSegment(sketch, "E4271", {"start": v(-55.9, -40.15) * mm, "end": v(-55.78, -40.2) * mm});
            skLineSegment(sketch, "E4272", {"start": v(-55.78, -40.2) * mm, "end": v(-55.67, -40.28) * mm});
            skLineSegment(sketch, "E4273", {"start": v(-55.67, -40.28) * mm, "end": v(-55.58, -40.38) * mm});
            skLineSegment(sketch, "E4274", {"start": v(-55.58, -40.38) * mm, "end": v(-55.52, -40.5) * mm});
            skLineSegment(sketch, "E4275", {"start": v(-55.52, -40.5) * mm, "end": v(-55.47, -40.62) * mm});
            skLineSegment(sketch, "E4276", {"start": v(-55.47, -40.62) * mm, "end": v(-55.46, -40.75) * mm});
            skLineSegment(sketch, "E4277", {"start": v(-55.46, -40.75) * mm, "end": v(-55.47, -40.88) * mm});
            skLineSegment(sketch, "E4278", {"start": v(-55.47, -40.88) * mm, "end": v(-55.51, -40.98) * mm});
            skLineSegment(sketch, "E4279", {"start": v(-55.51, -40.98) * mm, "end": v(-55.56, -41.07) * mm});
            skLineSegment(sketch, "E4280", {"start": v(-55.56, -41.07) * mm, "end": v(-55.62, -41.15) * mm});
            skLineSegment(sketch, "E4281", {"start": v(-55.62, -41.15) * mm, "end": v(-55.69, -41.22) * mm});
            skLineSegment(sketch, "E4282", {"start": v(-55.69, -41.22) * mm, "end": v(-55.73, -41.31) * mm});
            skLineSegment(sketch, "E4283", {"start": v(-55.73, -41.31) * mm, "end": v(-55.7, -41.42) * mm});
            skLineSegment(sketch, "E4284", {"start": v(-55.7, -41.42) * mm, "end": v(-55.53, -41.64) * mm});
            skLineSegment(sketch, "E4285", {"start": v(-55.53, -41.64) * mm, "end": v(-55.44, -41.7) * mm});
            skLineSegment(sketch, "E4286", {"start": v(-55.44, -41.7) * mm, "end": v(-55.34, -41.69) * mm});
            skLineSegment(sketch, "E4287", {"start": v(-55.34, -41.69) * mm, "end": v(-55.25, -41.64) * mm});
            skLineSegment(sketch, "E4288", {"start": v(-55.25, -41.64) * mm, "end": v(-55.16, -41.6) * mm});
            skLineSegment(sketch, "E4289", {"start": v(-55.16, -41.6) * mm, "end": v(-55.06, -41.59) * mm});
            skLineSegment(sketch, "E4290", {"start": v(-55.06, -41.59) * mm, "end": v(-54.95, -41.58) * mm});
            skLineSegment(sketch, "E4291", {"start": v(-54.95, -41.58) * mm, "end": v(-54.82, -41.6) * mm});
            skLineSegment(sketch, "E4292", {"start": v(-54.82, -41.6) * mm, "end": v(-54.7, -41.65) * mm});
            skLineSegment(sketch, "E4293", {"start": v(-54.7, -41.65) * mm, "end": v(-54.6, -41.73) * mm});
            skLineSegment(sketch, "E4294", {"start": v(-54.6, -41.73) * mm, "end": v(-54.5, -41.82) * mm});
            skLineSegment(sketch, "E4295", {"start": v(-54.5, -41.82) * mm, "end": v(-54.44, -41.94) * mm});
            skLineSegment(sketch, "E4296", {"start": v(-54.44, -41.94) * mm, "end": v(-54.4, -42.06) * mm});
            skLineSegment(sketch, "E4297", {"start": v(-54.4, -42.06) * mm, "end": v(-54.37, -42.19) * mm});
            skLineSegment(sketch, "E4298", {"start": v(-54.37, -42.19) * mm, "end": v(-54.38, -42.32) * mm});
            skLineSegment(sketch, "E4299", {"start": v(-54.38, -42.32) * mm, "end": v(-54.42, -42.42) * mm});
            skLineSegment(sketch, "E4300", {"start": v(-54.42, -42.42) * mm, "end": v(-54.47, -42.5) * mm});
            skLineSegment(sketch, "E4301", {"start": v(-54.47, -42.5) * mm, "end": v(-54.52, -42.6) * mm});
            skLineSegment(sketch, "E4302", {"start": v(-54.52, -42.6) * mm, "end": v(-54.59, -42.67) * mm});
            skLineSegment(sketch, "E4303", {"start": v(-54.59, -42.67) * mm, "end": v(-54.62, -42.76) * mm});
            skLineSegment(sketch, "E4304", {"start": v(-54.62, -42.76) * mm, "end": v(-54.59, -42.86) * mm});
            skLineSegment(sketch, "E4305", {"start": v(-54.59, -42.86) * mm, "end": v(-54.42, -43.08) * mm});
            skLineSegment(sketch, "E4306", {"start": v(-54.42, -43.08) * mm, "end": v(-54.33, -43.13) * mm});
            skLineSegment(sketch, "E4307", {"start": v(-54.33, -43.13) * mm, "end": v(-54.23, -43.12) * mm});
            skLineSegment(sketch, "E4308", {"start": v(-54.23, -43.12) * mm, "end": v(-54.14, -43.07) * mm});
            skLineSegment(sketch, "E4309", {"start": v(-54.14, -43.07) * mm, "end": v(-54.05, -43.04) * mm});
            skLineSegment(sketch, "E4310", {"start": v(-54.05, -43.04) * mm, "end": v(-53.95, -43.02) * mm});
            skLineSegment(sketch, "E4311", {"start": v(-53.95, -43.02) * mm, "end": v(-53.85, -43) * mm});
            skLineSegment(sketch, "E4312", {"start": v(-53.85, -43) * mm, "end": v(-53.72, -43.02) * mm});
            skLineSegment(sketch, "E4313", {"start": v(-53.72, -43.02) * mm, "end": v(-53.6, -43.07) * mm});
            skLineSegment(sketch, "E4314", {"start": v(-53.6, -43.07) * mm, "end": v(-53.49, -43.14) * mm});
            skLineSegment(sketch, "E4315", {"start": v(-53.49, -43.14) * mm, "end": v(-53.4, -43.24) * mm});
            skLineSegment(sketch, "E4316", {"start": v(-53.4, -43.24) * mm, "end": v(-53.32, -43.35) * mm});
            skLineSegment(sketch, "E4317", {"start": v(-53.32, -43.35) * mm, "end": v(-53.27, -43.47) * mm});
            skLineSegment(sketch, "E4318", {"start": v(-53.27, -43.47) * mm, "end": v(-53.25, -43.6) * mm});
            skLineSegment(sketch, "E4319", {"start": v(-53.25, -43.6) * mm, "end": v(-53.26, -43.73) * mm});
            skLineSegment(sketch, "E4320", {"start": v(-53.26, -43.73) * mm, "end": v(-53.3, -43.83) * mm});
            skLineSegment(sketch, "E4321", {"start": v(-53.3, -43.83) * mm, "end": v(-53.34, -43.92) * mm});
            skLineSegment(sketch, "E4322", {"start": v(-53.34, -43.92) * mm, "end": v(-53.39, -44) * mm});
            skLineSegment(sketch, "E4323", {"start": v(-53.39, -44) * mm, "end": v(-53.45, -44.08) * mm});
            skLineSegment(sketch, "E4324", {"start": v(-53.45, -44.08) * mm, "end": v(-53.49, -44.17) * mm});
            skLineSegment(sketch, "E4325", {"start": v(-53.49, -44.17) * mm, "end": v(-53.45, -44.27) * mm});
            skLineSegment(sketch, "E4326", {"start": v(-53.45, -44.27) * mm, "end": v(-53.27, -44.49) * mm});
            skLineSegment(sketch, "E4327", {"start": v(-53.27, -44.49) * mm, "end": v(-53.18, -44.54) * mm});
            skLineSegment(sketch, "E4328", {"start": v(-53.18, -44.54) * mm, "end": v(-53.08, -44.52) * mm});
            skLineSegment(sketch, "E4329", {"start": v(-53.08, -44.52) * mm, "end": v(-53, -44.48) * mm});
            skLineSegment(sketch, "E4330", {"start": v(-53, -44.48) * mm, "end": v(-52.9, -44.44) * mm});
            skLineSegment(sketch, "E4331", {"start": v(-52.9, -44.44) * mm, "end": v(-52.8, -44.41) * mm});
            skLineSegment(sketch, "E4332", {"start": v(-52.8, -44.41) * mm, "end": v(-52.7, -44.4) * mm});
            skLineSegment(sketch, "E4333", {"start": v(-52.7, -44.4) * mm, "end": v(-52.57, -44.41) * mm});
            skLineSegment(sketch, "E4334", {"start": v(-52.57, -44.41) * mm, "end": v(-52.45, -44.46) * mm});
            skLineSegment(sketch, "E4335", {"start": v(-52.45, -44.46) * mm, "end": v(-52.34, -44.53) * mm});
            skLineSegment(sketch, "E4336", {"start": v(-52.34, -44.53) * mm, "end": v(-52.24, -44.62) * mm});
            skLineSegment(sketch, "E4337", {"start": v(-52.24, -44.62) * mm, "end": v(-52.17, -44.73) * mm});
            skLineSegment(sketch, "E4338", {"start": v(-52.17, -44.73) * mm, "end": v(-52.12, -44.85) * mm});
            skLineSegment(sketch, "E4339", {"start": v(-52.12, -44.85) * mm, "end": v(-52.1, -44.98) * mm});
            skLineSegment(sketch, "E4340", {"start": v(-52.1, -44.98) * mm, "end": v(-52.1, -45.1) * mm});
            skLineSegment(sketch, "E4341", {"start": v(-52.1, -45.1) * mm, "end": v(-52.13, -45.2) * mm});
            skLineSegment(sketch, "E4342", {"start": v(-52.13, -45.2) * mm, "end": v(-52.17, -45.3) * mm});
            skLineSegment(sketch, "E4343", {"start": v(-52.17, -45.3) * mm, "end": v(-52.22, -45.39) * mm});
            skLineSegment(sketch, "E4344", {"start": v(-52.22, -45.39) * mm, "end": v(-52.28, -45.46) * mm});
            skLineSegment(sketch, "E4345", {"start": v(-52.28, -45.46) * mm, "end": v(-52.31, -45.56) * mm});
            skLineSegment(sketch, "E4346", {"start": v(-52.31, -45.56) * mm, "end": v(-52.27, -45.66) * mm});
            skLineSegment(sketch, "E4347", {"start": v(-52.27, -45.66) * mm, "end": v(-52.1, -45.86) * mm});
            skLineSegment(sketch, "E4348", {"start": v(-52.1, -45.86) * mm, "end": v(-52, -45.92) * mm});
            skLineSegment(sketch, "E4349", {"start": v(-52, -45.92) * mm, "end": v(-51.9, -45.9) * mm});
            skLineSegment(sketch, "E4350", {"start": v(-51.9, -45.9) * mm, "end": v(-51.81, -45.85) * mm});
            skLineSegment(sketch, "E4351", {"start": v(-51.81, -45.85) * mm, "end": v(-51.72, -45.8) * mm});
            skLineSegment(sketch, "E4352", {"start": v(-51.72, -45.8) * mm, "end": v(-51.62, -45.78) * mm});
            skLineSegment(sketch, "E4353", {"start": v(-51.62, -45.78) * mm, "end": v(-51.52, -45.76) * mm});
            skLineSegment(sketch, "E4354", {"start": v(-51.52, -45.76) * mm, "end": v(-51.4, -45.77) * mm});
            skLineSegment(sketch, "E4355", {"start": v(-51.4, -45.77) * mm, "end": v(-51.27, -45.82) * mm});
            skLineSegment(sketch, "E4356", {"start": v(-51.27, -45.82) * mm, "end": v(-51.15, -45.88) * mm});
            skLineSegment(sketch, "E4357", {"start": v(-51.15, -45.88) * mm, "end": v(-51.06, -45.97) * mm});
            skLineSegment(sketch, "E4358", {"start": v(-51.06, -45.97) * mm, "end": v(-50.98, -46.08) * mm});
            skLineSegment(sketch, "E4359", {"start": v(-50.98, -46.08) * mm, "end": v(-50.92, -46.2) * mm});
            skLineSegment(sketch, "E4360", {"start": v(-50.92, -46.2) * mm, "end": v(-50.9, -46.32) * mm});
            skLineSegment(sketch, "E4361", {"start": v(-50.9, -46.32) * mm, "end": v(-50.9, -46.46) * mm});
            skLineSegment(sketch, "E4362", {"start": v(-50.9, -46.46) * mm, "end": v(-50.93, -46.55) * mm});
            skLineSegment(sketch, "E4363", {"start": v(-50.93, -46.55) * mm, "end": v(-50.96, -46.65) * mm});
            skLineSegment(sketch, "E4364", {"start": v(-50.96, -46.65) * mm, "end": v(-51.01, -46.74) * mm});
            skLineSegment(sketch, "E4365", {"start": v(-51.01, -46.74) * mm, "end": v(-51.07, -46.82) * mm});
            skLineSegment(sketch, "E4366", {"start": v(-51.07, -46.82) * mm, "end": v(-51.1, -46.91) * mm});
            skLineSegment(sketch, "E4367", {"start": v(-51.1, -46.91) * mm, "end": v(-51.06, -47.01) * mm});
            skLineSegment(sketch, "E4368", {"start": v(-51.06, -47.01) * mm, "end": v(-50.87, -47.21) * mm});
            skLineSegment(sketch, "E4369", {"start": v(-50.87, -47.21) * mm, "end": v(-50.78, -47.26) * mm});
            skLineSegment(sketch, "E4370", {"start": v(-50.78, -47.26) * mm, "end": v(-50.68, -47.24) * mm});
            skLineSegment(sketch, "E4371", {"start": v(-50.68, -47.24) * mm, "end": v(-50.6, -47.19) * mm});
            skLineSegment(sketch, "E4372", {"start": v(-50.6, -47.19) * mm, "end": v(-50.5, -47.15) * mm});
            skLineSegment(sketch, "E4373", {"start": v(-50.5, -47.15) * mm, "end": v(-50.4, -47.12) * mm});
            skLineSegment(sketch, "E4374", {"start": v(-50.4, -47.12) * mm, "end": v(-50.3, -47.1) * mm});
            skLineSegment(sketch, "E4375", {"start": v(-50.3, -47.1) * mm, "end": v(-50.18, -47.1) * mm});
            skLineSegment(sketch, "E4376", {"start": v(-50.18, -47.1) * mm, "end": v(-50.05, -47.14) * mm});
            skLineSegment(sketch, "E4377", {"start": v(-50.05, -47.14) * mm, "end": v(-49.94, -47.2) * mm});
            skLineSegment(sketch, "E4378", {"start": v(-49.94, -47.2) * mm, "end": v(-49.84, -47.3) * mm});
            skLineSegment(sketch, "E4379", {"start": v(-49.84, -47.3) * mm, "end": v(-49.75, -47.4) * mm});
            skLineSegment(sketch, "E4380", {"start": v(-49.75, -47.4) * mm, "end": v(-49.7, -47.51) * mm});
            skLineSegment(sketch, "E4381", {"start": v(-49.7, -47.51) * mm, "end": v(-49.67, -47.64) * mm});
            skLineSegment(sketch, "E4382", {"start": v(-49.67, -47.64) * mm, "end": v(-49.66, -47.77) * mm});
            skLineSegment(sketch, "E4383", {"start": v(-49.66, -47.77) * mm, "end": v(-49.69, -47.87) * mm});
            skLineSegment(sketch, "E4384", {"start": v(-49.69, -47.87) * mm, "end": v(-49.73, -47.97) * mm});
            skLineSegment(sketch, "E4385", {"start": v(-49.73, -47.97) * mm, "end": v(-49.77, -48.06) * mm});
            skLineSegment(sketch, "E4386", {"start": v(-49.77, -48.06) * mm, "end": v(-49.83, -48.14) * mm});
            skLineSegment(sketch, "E4387", {"start": v(-49.83, -48.14) * mm, "end": v(-49.86, -48.23) * mm});
            skLineSegment(sketch, "E4388", {"start": v(-49.86, -48.23) * mm, "end": v(-49.81, -48.33) * mm});
            skLineSegment(sketch, "E4389", {"start": v(-49.81, -48.33) * mm, "end": v(-49.62, -48.53) * mm});
            skLineSegment(sketch, "E4390", {"start": v(-49.62, -48.53) * mm, "end": v(-49.52, -48.58) * mm});
            skLineSegment(sketch, "E4391", {"start": v(-49.52, -48.58) * mm, "end": v(-49.43, -48.55) * mm});
            skLineSegment(sketch, "E4392", {"start": v(-49.43, -48.55) * mm, "end": v(-49.34, -48.5) * mm});
            skLineSegment(sketch, "E4393", {"start": v(-49.34, -48.5) * mm, "end": v(-49.25, -48.45) * mm});
            skLineSegment(sketch, "E4394", {"start": v(-49.25, -48.45) * mm, "end": v(-49.16, -48.42) * mm});
            skLineSegment(sketch, "E4395", {"start": v(-49.16, -48.42) * mm, "end": v(-49.06, -48.4) * mm});
            skLineSegment(sketch, "E4396", {"start": v(-49.06, -48.4) * mm, "end": v(-48.92, -48.4) * mm});
            skLineSegment(sketch, "E4397", {"start": v(-48.92, -48.4) * mm, "end": v(-48.8, -48.44) * mm});
            skLineSegment(sketch, "E4398", {"start": v(-48.8, -48.44) * mm, "end": v(-48.68, -48.5) * mm});
            skLineSegment(sketch, "E4399", {"start": v(-48.68, -48.5) * mm, "end": v(-48.58, -48.58) * mm});
            skLineSegment(sketch, "E4400", {"start": v(-48.58, -48.58) * mm, "end": v(-48.5, -48.68) * mm});
            skLineSegment(sketch, "E4401", {"start": v(-48.5, -48.68) * mm, "end": v(-48.44, -48.8) * mm});
            skLineSegment(sketch, "E4402", {"start": v(-48.44, -48.8) * mm, "end": v(-48.4, -48.92) * mm});
            skLineSegment(sketch, "E4403", {"start": v(-48.4, -48.92) * mm, "end": v(-48.4, -49.06) * mm});
            skLineSegment(sketch, "E4404", {"start": v(-48.4, -49.06) * mm, "end": v(-48.42, -49.16) * mm});
            skLineSegment(sketch, "E4405", {"start": v(-48.42, -49.16) * mm, "end": v(-48.45, -49.25) * mm});
            skLineSegment(sketch, "E4406", {"start": v(-48.45, -49.25) * mm, "end": v(-48.5, -49.34) * mm});
            skLineSegment(sketch, "E4407", {"start": v(-48.5, -49.34) * mm, "end": v(-48.55, -49.43) * mm});
            skLineSegment(sketch, "E4408", {"start": v(-48.55, -49.43) * mm, "end": v(-48.58, -49.52) * mm});
            skLineSegment(sketch, "E4409", {"start": v(-48.58, -49.52) * mm, "end": v(-48.53, -49.62) * mm});
            skLineSegment(sketch, "E4410", {"start": v(-48.53, -49.62) * mm, "end": v(-48.33, -49.81) * mm});
            skLineSegment(sketch, "E4411", {"start": v(-48.33, -49.81) * mm, "end": v(-48.23, -49.86) * mm});
            skLineSegment(sketch, "E4412", {"start": v(-48.23, -49.86) * mm, "end": v(-48.14, -49.83) * mm});
            skLineSegment(sketch, "E4413", {"start": v(-48.14, -49.83) * mm, "end": v(-48.06, -49.77) * mm});
            skLineSegment(sketch, "E4414", {"start": v(-48.06, -49.77) * mm, "end": v(-47.97, -49.73) * mm});
            skLineSegment(sketch, "E4415", {"start": v(-47.97, -49.73) * mm, "end": v(-47.87, -49.69) * mm});
            skLineSegment(sketch, "E4416", {"start": v(-47.87, -49.69) * mm, "end": v(-47.77, -49.66) * mm});
            skLineSegment(sketch, "E4417", {"start": v(-47.77, -49.66) * mm, "end": v(-47.64, -49.67) * mm});
            skLineSegment(sketch, "E4418", {"start": v(-47.64, -49.67) * mm, "end": v(-47.51, -49.7) * mm});
            skLineSegment(sketch, "E4419", {"start": v(-47.51, -49.7) * mm, "end": v(-47.4, -49.75) * mm});
            skLineSegment(sketch, "E4420", {"start": v(-47.4, -49.75) * mm, "end": v(-47.3, -49.84) * mm});
            skLineSegment(sketch, "E4421", {"start": v(-47.3, -49.84) * mm, "end": v(-47.2, -49.94) * mm});
            skLineSegment(sketch, "E4422", {"start": v(-47.2, -49.94) * mm, "end": v(-47.14, -50.05) * mm});
            skLineSegment(sketch, "E4423", {"start": v(-47.14, -50.05) * mm, "end": v(-47.1, -50.18) * mm});
            skLineSegment(sketch, "E4424", {"start": v(-47.1, -50.18) * mm, "end": v(-47.1, -50.3) * mm});
            skLineSegment(sketch, "E4425", {"start": v(-47.1, -50.3) * mm, "end": v(-47.12, -50.4) * mm});
            skLineSegment(sketch, "E4426", {"start": v(-47.12, -50.4) * mm, "end": v(-47.15, -50.5) * mm});
            skLineSegment(sketch, "E4427", {"start": v(-47.15, -50.5) * mm, "end": v(-47.19, -50.6) * mm});
            skLineSegment(sketch, "E4428", {"start": v(-47.19, -50.6) * mm, "end": v(-47.24, -50.68) * mm});
            skLineSegment(sketch, "E4429", {"start": v(-47.24, -50.68) * mm, "end": v(-47.26, -50.78) * mm});
            skLineSegment(sketch, "E4430", {"start": v(-47.26, -50.78) * mm, "end": v(-47.21, -50.87) * mm});
            skLineSegment(sketch, "E4431", {"start": v(-47.21, -50.87) * mm, "end": v(-47.01, -51.06) * mm});
            skLineSegment(sketch, "E4432", {"start": v(-47.01, -51.06) * mm, "end": v(-46.91, -51.1) * mm});
            skLineSegment(sketch, "E4433", {"start": v(-46.91, -51.1) * mm, "end": v(-46.82, -51.07) * mm});
            skLineSegment(sketch, "E4434", {"start": v(-46.82, -51.07) * mm, "end": v(-46.74, -51.01) * mm});
            skLineSegment(sketch, "E4435", {"start": v(-46.74, -51.01) * mm, "end": v(-46.65, -50.96) * mm});
            skLineSegment(sketch, "E4436", {"start": v(-46.65, -50.96) * mm, "end": v(-46.56, -50.93) * mm});
            skLineSegment(sketch, "E4437", {"start": v(-46.56, -50.93) * mm, "end": v(-46.46, -50.9) * mm});
            skLineSegment(sketch, "E4438", {"start": v(-46.46, -50.9) * mm, "end": v(-46.32, -50.9) * mm});
            skLineSegment(sketch, "E4439", {"start": v(-46.32, -50.9) * mm, "end": v(-46.2, -50.92) * mm});
            skLineSegment(sketch, "E4440", {"start": v(-46.2, -50.92) * mm, "end": v(-46.08, -50.98) * mm});
            skLineSegment(sketch, "E4441", {"start": v(-46.08, -50.98) * mm, "end": v(-45.97, -51.06) * mm});
            skLineSegment(sketch, "E4442", {"start": v(-45.97, -51.06) * mm, "end": v(-45.88, -51.15) * mm});
            skLineSegment(sketch, "E4443", {"start": v(-45.88, -51.15) * mm, "end": v(-45.82, -51.27) * mm});
            skLineSegment(sketch, "E4444", {"start": v(-45.82, -51.27) * mm, "end": v(-45.77, -51.4) * mm});
            skLineSegment(sketch, "E4445", {"start": v(-45.77, -51.4) * mm, "end": v(-45.76, -51.52) * mm});
            skLineSegment(sketch, "E4446", {"start": v(-45.76, -51.52) * mm, "end": v(-45.78, -51.62) * mm});
            skLineSegment(sketch, "E4447", {"start": v(-45.78, -51.62) * mm, "end": v(-45.8, -51.72) * mm});
            skLineSegment(sketch, "E4448", {"start": v(-45.8, -51.72) * mm, "end": v(-45.85, -51.81) * mm});
            skLineSegment(sketch, "E4449", {"start": v(-45.85, -51.81) * mm, "end": v(-45.9, -51.9) * mm});
            skLineSegment(sketch, "E4450", {"start": v(-45.9, -51.9) * mm, "end": v(-45.92, -52) * mm});
            skLineSegment(sketch, "E4451", {"start": v(-45.92, -52) * mm, "end": v(-45.86, -52.1) * mm});
            skLineSegment(sketch, "E4452", {"start": v(-45.86, -52.1) * mm, "end": v(-45.66, -52.27) * mm});
            skLineSegment(sketch, "E4453", {"start": v(-45.66, -52.27) * mm, "end": v(-45.56, -52.31) * mm});
            skLineSegment(sketch, "E4454", {"start": v(-45.56, -52.31) * mm, "end": v(-45.46, -52.28) * mm});
            skLineSegment(sketch, "E4455", {"start": v(-45.46, -52.28) * mm, "end": v(-45.39, -52.22) * mm});
            skLineSegment(sketch, "E4456", {"start": v(-45.39, -52.22) * mm, "end": v(-45.3, -52.17) * mm});
            skLineSegment(sketch, "E4457", {"start": v(-45.3, -52.17) * mm, "end": v(-45.2, -52.13) * mm});
            skLineSegment(sketch, "E4458", {"start": v(-45.2, -52.13) * mm, "end": v(-45.1, -52.1) * mm});
            skLineSegment(sketch, "E4459", {"start": v(-45.1, -52.1) * mm, "end": v(-44.98, -52.1) * mm});
            skLineSegment(sketch, "E4460", {"start": v(-44.98, -52.1) * mm, "end": v(-44.85, -52.12) * mm});
            skLineSegment(sketch, "E4461", {"start": v(-44.85, -52.12) * mm, "end": v(-44.73, -52.17) * mm});
            skLineSegment(sketch, "E4462", {"start": v(-44.73, -52.17) * mm, "end": v(-44.62, -52.24) * mm});
            skLineSegment(sketch, "E4463", {"start": v(-44.62, -52.24) * mm, "end": v(-44.53, -52.34) * mm});
            skLineSegment(sketch, "E4464", {"start": v(-44.53, -52.34) * mm, "end": v(-44.46, -52.45) * mm});
            skLineSegment(sketch, "E4465", {"start": v(-44.46, -52.45) * mm, "end": v(-44.41, -52.57) * mm});
            skLineSegment(sketch, "E4466", {"start": v(-44.41, -52.57) * mm, "end": v(-44.4, -52.7) * mm});
            skLineSegment(sketch, "E4467", {"start": v(-44.4, -52.7) * mm, "end": v(-44.41, -52.8) * mm});
            skLineSegment(sketch, "E4468", {"start": v(-44.41, -52.8) * mm, "end": v(-44.44, -52.9) * mm});
            skLineSegment(sketch, "E4469", {"start": v(-44.44, -52.9) * mm, "end": v(-44.48, -53) * mm});
            skLineSegment(sketch, "E4470", {"start": v(-44.48, -53) * mm, "end": v(-44.52, -53.08) * mm});
            skLineSegment(sketch, "E4471", {"start": v(-44.52, -53.08) * mm, "end": v(-44.54, -53.18) * mm});
            skLineSegment(sketch, "E4472", {"start": v(-44.54, -53.18) * mm, "end": v(-44.49, -53.27) * mm});
            skLineSegment(sketch, "E4473", {"start": v(-44.49, -53.27) * mm, "end": v(-44.27, -53.45) * mm});
            skLineSegment(sketch, "E4474", {"start": v(-44.27, -53.45) * mm, "end": v(-44.17, -53.49) * mm});
            skLineSegment(sketch, "E4475", {"start": v(-44.17, -53.49) * mm, "end": v(-44.08, -53.45) * mm});
            skLineSegment(sketch, "E4476", {"start": v(-44.08, -53.45) * mm, "end": v(-44, -53.39) * mm});
            skLineSegment(sketch, "E4477", {"start": v(-44, -53.39) * mm, "end": v(-43.92, -53.34) * mm});
            skLineSegment(sketch, "E4478", {"start": v(-43.92, -53.34) * mm, "end": v(-43.83, -53.3) * mm});
            skLineSegment(sketch, "E4479", {"start": v(-43.83, -53.3) * mm, "end": v(-43.73, -53.26) * mm});
            skLineSegment(sketch, "E4480", {"start": v(-43.73, -53.26) * mm, "end": v(-43.6, -53.25) * mm});
            skLineSegment(sketch, "E4481", {"start": v(-43.6, -53.25) * mm, "end": v(-43.47, -53.27) * mm});
            skLineSegment(sketch, "E4482", {"start": v(-43.47, -53.27) * mm, "end": v(-43.35, -53.32) * mm});
            skLineSegment(sketch, "E4483", {"start": v(-43.35, -53.32) * mm, "end": v(-43.24, -53.4) * mm});
            skLineSegment(sketch, "E4484", {"start": v(-43.24, -53.4) * mm, "end": v(-43.14, -53.49) * mm});
            skLineSegment(sketch, "E4485", {"start": v(-43.14, -53.49) * mm, "end": v(-43.07, -53.6) * mm});
            skLineSegment(sketch, "E4486", {"start": v(-43.07, -53.6) * mm, "end": v(-43.02, -53.72) * mm});
            skLineSegment(sketch, "E4487", {"start": v(-43.02, -53.72) * mm, "end": v(-43, -53.85) * mm});
            skLineSegment(sketch, "E4488", {"start": v(-43, -53.85) * mm, "end": v(-43.02, -53.95) * mm});
            skLineSegment(sketch, "E4489", {"start": v(-43.02, -53.95) * mm, "end": v(-43.04, -54.05) * mm});
            skLineSegment(sketch, "E4490", {"start": v(-43.04, -54.05) * mm, "end": v(-43.07, -54.14) * mm});
            skLineSegment(sketch, "E4491", {"start": v(-43.07, -54.14) * mm, "end": v(-43.12, -54.23) * mm});
            skLineSegment(sketch, "E4492", {"start": v(-43.12, -54.23) * mm, "end": v(-43.13, -54.33) * mm});
            skLineSegment(sketch, "E4493", {"start": v(-43.13, -54.33) * mm, "end": v(-43.08, -54.42) * mm});
            skLineSegment(sketch, "E4494", {"start": v(-43.08, -54.42) * mm, "end": v(-42.86, -54.59) * mm});
            skLineSegment(sketch, "E4495", {"start": v(-42.86, -54.59) * mm, "end": v(-42.76, -54.62) * mm});
            skLineSegment(sketch, "E4496", {"start": v(-42.76, -54.62) * mm, "end": v(-42.67, -54.59) * mm});
            skLineSegment(sketch, "E4497", {"start": v(-42.67, -54.59) * mm, "end": v(-42.6, -54.52) * mm});
            skLineSegment(sketch, "E4498", {"start": v(-42.6, -54.52) * mm, "end": v(-42.5, -54.47) * mm});
            skLineSegment(sketch, "E4499", {"start": v(-42.5, -54.47) * mm, "end": v(-42.42, -54.42) * mm});
            skLineSegment(sketch, "E4500", {"start": v(-42.42, -54.42) * mm, "end": v(-42.32, -54.38) * mm});
            skLineSegment(sketch, "E4501", {"start": v(-42.32, -54.38) * mm, "end": v(-42.19, -54.37) * mm});
            skLineSegment(sketch, "E4502", {"start": v(-42.19, -54.37) * mm, "end": v(-42.06, -54.4) * mm});
            skLineSegment(sketch, "E4503", {"start": v(-42.06, -54.4) * mm, "end": v(-41.94, -54.44) * mm});
            skLineSegment(sketch, "E4504", {"start": v(-41.94, -54.44) * mm, "end": v(-41.82, -54.5) * mm});
            skLineSegment(sketch, "E4505", {"start": v(-41.82, -54.5) * mm, "end": v(-41.73, -54.6) * mm});
            skLineSegment(sketch, "E4506", {"start": v(-41.73, -54.6) * mm, "end": v(-41.65, -54.7) * mm});
            skLineSegment(sketch, "E4507", {"start": v(-41.65, -54.7) * mm, "end": v(-41.6, -54.82) * mm});
            skLineSegment(sketch, "E4508", {"start": v(-41.6, -54.82) * mm, "end": v(-41.58, -54.95) * mm});
            skLineSegment(sketch, "E4509", {"start": v(-41.58, -54.95) * mm, "end": v(-41.59, -55.06) * mm});
            skLineSegment(sketch, "E4510", {"start": v(-41.59, -55.06) * mm, "end": v(-41.6, -55.16) * mm});
            skLineSegment(sketch, "E4511", {"start": v(-41.6, -55.16) * mm, "end": v(-41.64, -55.25) * mm});
            skLineSegment(sketch, "E4512", {"start": v(-41.64, -55.25) * mm, "end": v(-41.69, -55.34) * mm});
            skLineSegment(sketch, "E4513", {"start": v(-41.69, -55.34) * mm, "end": v(-41.7, -55.44) * mm});
            skLineSegment(sketch, "E4514", {"start": v(-41.7, -55.44) * mm, "end": v(-41.64, -55.53) * mm});
            skLineSegment(sketch, "E4515", {"start": v(-41.64, -55.53) * mm, "end": v(-41.42, -55.7) * mm});
            skLineSegment(sketch, "E4516", {"start": v(-41.42, -55.7) * mm, "end": v(-41.31, -55.73) * mm});
            skLineSegment(sketch, "E4517", {"start": v(-41.31, -55.73) * mm, "end": v(-41.22, -55.69) * mm});
            skLineSegment(sketch, "E4518", {"start": v(-41.22, -55.69) * mm, "end": v(-41.15, -55.62) * mm});
            skLineSegment(sketch, "E4519", {"start": v(-41.15, -55.62) * mm, "end": v(-41.07, -55.56) * mm});
            skLineSegment(sketch, "E4520", {"start": v(-41.07, -55.56) * mm, "end": v(-40.98, -55.51) * mm});
            skLineSegment(sketch, "E4521", {"start": v(-40.98, -55.51) * mm, "end": v(-40.88, -55.47) * mm});
            skLineSegment(sketch, "E4522", {"start": v(-40.88, -55.47) * mm, "end": v(-40.75, -55.46) * mm});
            skLineSegment(sketch, "E4523", {"start": v(-40.75, -55.46) * mm, "end": v(-40.62, -55.47) * mm});
            skLineSegment(sketch, "E4524", {"start": v(-40.62, -55.47) * mm, "end": v(-40.5, -55.52) * mm});
            skLineSegment(sketch, "E4525", {"start": v(-40.5, -55.52) * mm, "end": v(-40.38, -55.58) * mm});
            skLineSegment(sketch, "E4526", {"start": v(-40.38, -55.58) * mm, "end": v(-40.28, -55.67) * mm});
            skLineSegment(sketch, "E4527", {"start": v(-40.28, -55.67) * mm, "end": v(-40.2, -55.78) * mm});
            skLineSegment(sketch, "E4528", {"start": v(-40.2, -55.78) * mm, "end": v(-40.15, -55.9) * mm});
            skLineSegment(sketch, "E4529", {"start": v(-40.15, -55.9) * mm, "end": v(-40.13, -56.02) * mm});
            skLineSegment(sketch, "E4530", {"start": v(-40.13, -56.02) * mm, "end": v(-40.13, -56.13) * mm});
            skLineSegment(sketch, "E4531", {"start": v(-40.13, -56.13) * mm, "end": v(-40.15, -56.23) * mm});
            skLineSegment(sketch, "E4532", {"start": v(-40.15, -56.23) * mm, "end": v(-40.18, -56.32) * mm});
            skLineSegment(sketch, "E4533", {"start": v(-40.18, -56.32) * mm, "end": v(-40.22, -56.41) * mm});
            skLineSegment(sketch, "E4534", {"start": v(-40.22, -56.41) * mm, "end": v(-40.23, -56.51) * mm});
            skLineSegment(sketch, "E4535", {"start": v(-40.23, -56.51) * mm, "end": v(-40.17, -56.6) * mm});
            skLineSegment(sketch, "E4536", {"start": v(-40.17, -56.6) * mm, "end": v(-39.94, -56.76) * mm});
            skLineSegment(sketch, "E4537", {"start": v(-39.94, -56.76) * mm, "end": v(-39.84, -56.79) * mm});
            skLineSegment(sketch, "E4538", {"start": v(-39.84, -56.79) * mm, "end": v(-39.75, -56.75) * mm});
            skLineSegment(sketch, "E4539", {"start": v(-39.75, -56.75) * mm, "end": v(-39.68, -56.68) * mm});
            skLineSegment(sketch, "E4540", {"start": v(-39.68, -56.68) * mm, "end": v(-39.6, -56.62) * mm});
            skLineSegment(sketch, "E4541", {"start": v(-39.6, -56.62) * mm, "end": v(-39.5, -56.57) * mm});
            skLineSegment(sketch, "E4542", {"start": v(-39.5, -56.57) * mm, "end": v(-39.41, -56.53) * mm});
            skLineSegment(sketch, "E4543", {"start": v(-39.41, -56.53) * mm, "end": v(-39.29, -56.5) * mm});
            skLineSegment(sketch, "E4544", {"start": v(-39.29, -56.5) * mm, "end": v(-39.16, -56.52) * mm});
            skLineSegment(sketch, "E4545", {"start": v(-39.16, -56.52) * mm, "end": v(-39.03, -56.56) * mm});
            skLineSegment(sketch, "E4546", {"start": v(-39.03, -56.56) * mm, "end": v(-38.91, -56.62) * mm});
            skLineSegment(sketch, "E4547", {"start": v(-38.91, -56.62) * mm, "end": v(-38.81, -56.7) * mm});
            skLineSegment(sketch, "E4548", {"start": v(-38.81, -56.7) * mm, "end": v(-38.73, -56.8) * mm});
            skLineSegment(sketch, "E4549", {"start": v(-38.73, -56.8) * mm, "end": v(-38.67, -56.93) * mm});
            skLineSegment(sketch, "E4550", {"start": v(-38.67, -56.93) * mm, "end": v(-38.65, -57.05) * mm});
            skLineSegment(sketch, "E4551", {"start": v(-38.65, -57.05) * mm, "end": v(-38.65, -57.16) * mm});
            skLineSegment(sketch, "E4552", {"start": v(-38.65, -57.16) * mm, "end": v(-38.67, -57.26) * mm});
            skLineSegment(sketch, "E4553", {"start": v(-38.67, -57.26) * mm, "end": v(-38.7, -57.35) * mm});
            skLineSegment(sketch, "E4554", {"start": v(-38.7, -57.35) * mm, "end": v(-38.73, -57.45) * mm});
            skLineSegment(sketch, "E4555", {"start": v(-38.73, -57.45) * mm, "end": v(-38.74, -57.55) * mm});
            skLineSegment(sketch, "E4556", {"start": v(-38.74, -57.55) * mm, "end": v(-38.67, -57.63) * mm});
            skLineSegment(sketch, "E4557", {"start": v(-38.67, -57.63) * mm, "end": v(-38.44, -57.78) * mm});
            skLineSegment(sketch, "E4558", {"start": v(-38.44, -57.78) * mm, "end": v(-38.34, -57.81) * mm});
            skLineSegment(sketch, "E4559", {"start": v(-38.34, -57.81) * mm, "end": v(-38.25, -57.77) * mm});
            skLineSegment(sketch, "E4560", {"start": v(-38.25, -57.77) * mm, "end": v(-38.18, -57.7) * mm});
            skLineSegment(sketch, "E4561", {"start": v(-38.18, -57.7) * mm, "end": v(-38.1, -57.63) * mm});
            skLineSegment(sketch, "E4562", {"start": v(-38.1, -57.63) * mm, "end": v(-38.02, -57.58) * mm});
            skLineSegment(sketch, "E4563", {"start": v(-38.02, -57.58) * mm, "end": v(-37.92, -57.54) * mm});
            skLineSegment(sketch, "E4564", {"start": v(-37.92, -57.54) * mm, "end": v(-37.8, -57.52) * mm});
            skLineSegment(sketch, "E4565", {"start": v(-37.8, -57.52) * mm, "end": v(-37.66, -57.52) * mm});
            skLineSegment(sketch, "E4566", {"start": v(-37.66, -57.52) * mm, "end": v(-37.54, -57.56) * mm});
            skLineSegment(sketch, "E4567", {"start": v(-37.54, -57.56) * mm, "end": v(-37.42, -57.62) * mm});
            skLineSegment(sketch, "E4568", {"start": v(-37.42, -57.62) * mm, "end": v(-37.32, -57.7) * mm});
            skLineSegment(sketch, "E4569", {"start": v(-37.32, -57.7) * mm, "end": v(-37.23, -57.8) * mm});
            skLineSegment(sketch, "E4570", {"start": v(-37.23, -57.8) * mm, "end": v(-37.17, -57.92) * mm});
            skLineSegment(sketch, "E4571", {"start": v(-37.17, -57.92) * mm, "end": v(-37.14, -58.05) * mm});
            skLineSegment(sketch, "E4572", {"start": v(-37.14, -58.05) * mm, "end": v(-37.14, -58.15) * mm});
            skLineSegment(sketch, "E4573", {"start": v(-37.14, -58.15) * mm, "end": v(-37.15, -58.25) * mm});
            skLineSegment(sketch, "E4574", {"start": v(-37.15, -58.25) * mm, "end": v(-37.18, -58.35) * mm});
            skLineSegment(sketch, "E4575", {"start": v(-37.18, -58.35) * mm, "end": v(-37.21, -58.44) * mm});
            skLineSegment(sketch, "E4576", {"start": v(-37.21, -58.44) * mm, "end": v(-37.22, -58.54) * mm});
            skLineSegment(sketch, "E4577", {"start": v(-37.22, -58.54) * mm, "end": v(-37.15, -58.62) * mm});
            skLineSegment(sketch, "E4578", {"start": v(-37.15, -58.62) * mm, "end": v(-36.92, -58.77) * mm});
            skLineSegment(sketch, "E4579", {"start": v(-36.92, -58.77) * mm, "end": v(-36.82, -58.8) * mm});
            skLineSegment(sketch, "E4580", {"start": v(-36.82, -58.8) * mm, "end": v(-36.73, -58.75) * mm});
            skLineSegment(sketch, "E4581", {"start": v(-36.73, -58.75) * mm, "end": v(-36.66, -58.68) * mm});
            skLineSegment(sketch, "E4582", {"start": v(-36.66, -58.68) * mm, "end": v(-36.58, -58.61) * mm});
            skLineSegment(sketch, "E4583", {"start": v(-36.58, -58.61) * mm, "end": v(-36.5, -58.56) * mm});
            skLineSegment(sketch, "E4584", {"start": v(-36.5, -58.56) * mm, "end": v(-36.4, -58.51) * mm});
            skLineSegment(sketch, "E4585", {"start": v(-36.4, -58.51) * mm, "end": v(-36.27, -58.49) * mm});
            skLineSegment(sketch, "E4586", {"start": v(-36.27, -58.49) * mm, "end": v(-36.14, -58.49) * mm});
            skLineSegment(sketch, "E4587", {"start": v(-36.14, -58.49) * mm, "end": v(-36.02, -58.52) * mm});
            skLineSegment(sketch, "E4588", {"start": v(-36.02, -58.52) * mm, "end": v(-35.9, -58.58) * mm});
            skLineSegment(sketch, "E4589", {"start": v(-35.9, -58.58) * mm, "end": v(-35.8, -58.66) * mm});
            skLineSegment(sketch, "E4590", {"start": v(-35.8, -58.66) * mm, "end": v(-35.7, -58.76) * mm});
            skLineSegment(sketch, "E4591", {"start": v(-35.7, -58.76) * mm, "end": v(-35.64, -58.87) * mm});
            skLineSegment(sketch, "E4592", {"start": v(-35.64, -58.87) * mm, "end": v(-35.6, -59) * mm});
            skLineSegment(sketch, "E4593", {"start": v(-35.6, -59) * mm, "end": v(-35.6, -59.1) * mm});
            skLineSegment(sketch, "E4594", {"start": v(-35.6, -59.1) * mm, "end": v(-35.62, -59.2) * mm});
            skLineSegment(sketch, "E4595", {"start": v(-35.62, -59.2) * mm, "end": v(-35.64, -59.3) * mm});
            skLineSegment(sketch, "E4596", {"start": v(-35.64, -59.3) * mm, "end": v(-35.67, -59.4) * mm});
            skLineSegment(sketch, "E4597", {"start": v(-35.67, -59.4) * mm, "end": v(-35.67, -59.5) * mm});
            skLineSegment(sketch, "E4598", {"start": v(-35.67, -59.5) * mm, "end": v(-35.6, -59.58) * mm});
            skLineSegment(sketch, "E4599", {"start": v(-35.6, -59.58) * mm, "end": v(-35.37, -59.72) * mm});
            skLineSegment(sketch, "E4600", {"start": v(-35.37, -59.72) * mm, "end": v(-35.26, -59.74) * mm});
            skLineSegment(sketch, "E4601", {"start": v(-35.26, -59.74) * mm, "end": v(-35.18, -59.7) * mm});
            skLineSegment(sketch, "E4602", {"start": v(-35.18, -59.7) * mm, "end": v(-35.1, -59.62) * mm});
            skLineSegment(sketch, "E4603", {"start": v(-35.1, -59.62) * mm, "end": v(-35.03, -59.55) * mm});
            skLineSegment(sketch, "E4604", {"start": v(-35.03, -59.55) * mm, "end": v(-34.95, -59.5) * mm});
            skLineSegment(sketch, "E4605", {"start": v(-34.95, -59.5) * mm, "end": v(-34.86, -59.44) * mm});
            skLineSegment(sketch, "E4606", {"start": v(-34.86, -59.44) * mm, "end": v(-34.73, -59.41) * mm});
            skLineSegment(sketch, "E4607", {"start": v(-34.73, -59.41) * mm, "end": v(-34.6, -59.42) * mm});
            skLineSegment(sketch, "E4608", {"start": v(-34.6, -59.42) * mm, "end": v(-34.47, -59.44) * mm});
            skLineSegment(sketch, "E4609", {"start": v(-34.47, -59.44) * mm, "end": v(-34.35, -59.5) * mm});
            skLineSegment(sketch, "E4610", {"start": v(-34.35, -59.5) * mm, "end": v(-34.24, -59.58) * mm});
            skLineSegment(sketch, "E4611", {"start": v(-34.24, -59.58) * mm, "end": v(-34.16, -59.67) * mm});
            skLineSegment(sketch, "E4612", {"start": v(-34.16, -59.67) * mm, "end": v(-34.09, -59.78) * mm});
            skLineSegment(sketch, "E4613", {"start": v(-34.09, -59.78) * mm, "end": v(-34.05, -59.9) * mm});
            skLineSegment(sketch, "E4614", {"start": v(-34.05, -59.9) * mm, "end": v(-34.05, -60.01) * mm});
            skLineSegment(sketch, "E4615", {"start": v(-34.05, -60.01) * mm, "end": v(-34.05, -60.11) * mm});
            skLineSegment(sketch, "E4616", {"start": v(-34.05, -60.11) * mm, "end": v(-34.07, -60.21) * mm});
            skLineSegment(sketch, "E4617", {"start": v(-34.07, -60.21) * mm, "end": v(-34.1, -60.3) * mm});
            skLineSegment(sketch, "E4618", {"start": v(-34.1, -60.3) * mm, "end": v(-34.1, -60.4) * mm});
            skLineSegment(sketch, "E4619", {"start": v(-34.1, -60.4) * mm, "end": v(-34.03, -60.49) * mm});
            skLineSegment(sketch, "E4620", {"start": v(-34.03, -60.49) * mm, "end": v(-33.8, -60.62) * mm});
            skLineSegment(sketch, "E4621", {"start": v(-33.8, -60.62) * mm, "end": v(-33.69, -60.64) * mm});
            skLineSegment(sketch, "E4622", {"start": v(-33.69, -60.64) * mm, "end": v(-33.6, -60.6) * mm});
            skLineSegment(sketch, "E4623", {"start": v(-33.6, -60.6) * mm, "end": v(-33.54, -60.51) * mm});
            skLineSegment(sketch, "E4624", {"start": v(-33.54, -60.51) * mm, "end": v(-33.46, -60.45) * mm});
            skLineSegment(sketch, "E4625", {"start": v(-33.46, -60.45) * mm, "end": v(-33.38, -60.39) * mm});
            skLineSegment(sketch, "E4626", {"start": v(-33.38, -60.39) * mm, "end": v(-33.3, -60.34) * mm});
            skLineSegment(sketch, "E4627", {"start": v(-33.3, -60.34) * mm, "end": v(-33.16, -60.3) * mm});
            skLineSegment(sketch, "E4628", {"start": v(-33.16, -60.3) * mm, "end": v(-33.03, -60.3) * mm});
            skLineSegment(sketch, "E4629", {"start": v(-33.03, -60.3) * mm, "end": v(-32.9, -60.33) * mm});
            skLineSegment(sketch, "E4630", {"start": v(-32.9, -60.33) * mm, "end": v(-32.78, -60.38) * mm});
            skLineSegment(sketch, "E4631", {"start": v(-32.78, -60.38) * mm, "end": v(-32.67, -60.45) * mm});
            skLineSegment(sketch, "E4632", {"start": v(-32.67, -60.45) * mm, "end": v(-32.58, -60.55) * mm});
            skLineSegment(sketch, "E4633", {"start": v(-32.58, -60.55) * mm, "end": v(-32.51, -60.66) * mm});
            skLineSegment(sketch, "E4634", {"start": v(-32.51, -60.66) * mm, "end": v(-32.47, -60.78) * mm});
            skLineSegment(sketch, "E4635", {"start": v(-32.47, -60.78) * mm, "end": v(-32.46, -60.88) * mm});
            skLineSegment(sketch, "E4636", {"start": v(-32.46, -60.88) * mm, "end": v(-32.47, -60.99) * mm});
            skLineSegment(sketch, "E4637", {"start": v(-32.47, -60.99) * mm, "end": v(-32.49, -61.08) * mm});
            skLineSegment(sketch, "E4638", {"start": v(-32.49, -61.08) * mm, "end": v(-32.51, -61.18) * mm});
            skLineSegment(sketch, "E4639", {"start": v(-32.51, -61.18) * mm, "end": v(-32.51, -61.28) * mm});
            skLineSegment(sketch, "E4640", {"start": v(-32.51, -61.28) * mm, "end": v(-32.44, -61.36) * mm});
            skLineSegment(sketch, "E4641", {"start": v(-32.44, -61.36) * mm, "end": v(-32.2, -61.49) * mm});
            skLineSegment(sketch, "E4642", {"start": v(-32.2, -61.49) * mm, "end": v(-32.09, -61.5) * mm});
            skLineSegment(sketch, "E4643", {"start": v(-32.09, -61.5) * mm, "end": v(-32, -61.45) * mm});
            skLineSegment(sketch, "E4644", {"start": v(-32, -61.45) * mm, "end": v(-31.94, -61.37) * mm});
            skLineSegment(sketch, "E4645", {"start": v(-31.94, -61.37) * mm, "end": v(-31.87, -61.3) * mm});
            skLineSegment(sketch, "E4646", {"start": v(-31.87, -61.3) * mm, "end": v(-31.79, -61.24) * mm});
            skLineSegment(sketch, "E4647", {"start": v(-31.79, -61.24) * mm, "end": v(-31.7, -61.19) * mm});
            skLineSegment(sketch, "E4648", {"start": v(-31.7, -61.19) * mm, "end": v(-31.57, -61.15) * mm});
            skLineSegment(sketch, "E4649", {"start": v(-31.57, -61.15) * mm, "end": v(-31.44, -61.15) * mm});
            skLineSegment(sketch, "E4650", {"start": v(-31.44, -61.15) * mm, "end": v(-31.31, -61.17) * mm});
            skLineSegment(sketch, "E4651", {"start": v(-31.31, -61.17) * mm, "end": v(-31.2, -61.22) * mm});
            skLineSegment(sketch, "E4652", {"start": v(-31.2, -61.22) * mm, "end": v(-31.08, -61.29) * mm});
            skLineSegment(sketch, "E4653", {"start": v(-31.08, -61.29) * mm, "end": v(-30.99, -61.38) * mm});
            skLineSegment(sketch, "E4654", {"start": v(-30.99, -61.38) * mm, "end": v(-30.91, -61.49) * mm});
            skLineSegment(sketch, "E4655", {"start": v(-30.91, -61.49) * mm, "end": v(-30.87, -61.6) * mm});
            skLineSegment(sketch, "E4656", {"start": v(-30.87, -61.6) * mm, "end": v(-30.86, -61.71) * mm});
            skLineSegment(sketch, "E4657", {"start": v(-30.86, -61.71) * mm, "end": v(-30.86, -61.81) * mm});
            skLineSegment(sketch, "E4658", {"start": v(-30.86, -61.81) * mm, "end": v(-30.88, -61.91) * mm});
            skLineSegment(sketch, "E4659", {"start": v(-30.88, -61.91) * mm, "end": v(-30.9, -62.01) * mm});
            skLineSegment(sketch, "E4660", {"start": v(-30.9, -62.01) * mm, "end": v(-30.9, -62.11) * mm});
            skLineSegment(sketch, "E4661", {"start": v(-30.9, -62.11) * mm, "end": v(-30.82, -62.19) * mm});
            skLineSegment(sketch, "E4662", {"start": v(-30.82, -62.19) * mm, "end": v(-30.57, -62.3) * mm});
            skLineSegment(sketch, "E4663", {"start": v(-30.57, -62.3) * mm, "end": v(-30.47, -62.32) * mm});
            skLineSegment(sketch, "E4664", {"start": v(-30.47, -62.32) * mm, "end": v(-30.38, -62.27) * mm});
            skLineSegment(sketch, "E4665", {"start": v(-30.38, -62.27) * mm, "end": v(-30.32, -62.19) * mm});
            skLineSegment(sketch, "E4666", {"start": v(-30.32, -62.19) * mm, "end": v(-30.25, -62.11) * mm});
            skLineSegment(sketch, "E4667", {"start": v(-30.25, -62.11) * mm, "end": v(-30.17, -62.05) * mm});
            skLineSegment(sketch, "E4668", {"start": v(-30.17, -62.05) * mm, "end": v(-30.09, -62) * mm});
            skLineSegment(sketch, "E4669", {"start": v(-30.09, -62) * mm, "end": v(-29.96, -61.96) * mm});
            skLineSegment(sketch, "E4670", {"start": v(-29.96, -61.96) * mm, "end": v(-29.83, -61.95) * mm});
            skLineSegment(sketch, "E4671", {"start": v(-29.83, -61.95) * mm, "end": v(-29.7, -61.97) * mm});
            skLineSegment(sketch, "E4672", {"start": v(-29.7, -61.97) * mm, "end": v(-29.58, -62.01) * mm});
            skLineSegment(sketch, "E4673", {"start": v(-29.58, -62.01) * mm, "end": v(-29.46, -62.08) * mm});
            skLineSegment(sketch, "E4674", {"start": v(-29.46, -62.08) * mm, "end": v(-29.37, -62.17) * mm});
            skLineSegment(sketch, "E4675", {"start": v(-29.37, -62.17) * mm, "end": v(-29.3, -62.28) * mm});
            skLineSegment(sketch, "E4676", {"start": v(-29.3, -62.28) * mm, "end": v(-29.24, -62.4) * mm});
            skLineSegment(sketch, "E4677", {"start": v(-29.24, -62.4) * mm, "end": v(-29.23, -62.5) * mm});
            skLineSegment(sketch, "E4678", {"start": v(-29.23, -62.5) * mm, "end": v(-29.23, -62.6) * mm});
            skLineSegment(sketch, "E4679", {"start": v(-29.23, -62.6) * mm, "end": v(-29.24, -62.7) * mm});
            skLineSegment(sketch, "E4680", {"start": v(-29.24, -62.7) * mm, "end": v(-29.27, -62.8) * mm});
            skLineSegment(sketch, "E4681", {"start": v(-29.27, -62.8) * mm, "end": v(-29.26, -62.9) * mm});
            skLineSegment(sketch, "E4682", {"start": v(-29.26, -62.9) * mm, "end": v(-29.18, -62.97) * mm});
            skLineSegment(sketch, "E4683", {"start": v(-29.18, -62.97) * mm, "end": v(-28.93, -63.09) * mm});
            skLineSegment(sketch, "E4684", {"start": v(-28.93, -63.09) * mm, "end": v(-28.83, -63.1) * mm});
            skLineSegment(sketch, "E4685", {"start": v(-28.83, -63.1) * mm, "end": v(-28.74, -63.04) * mm});
            skLineSegment(sketch, "E4686", {"start": v(-28.74, -63.04) * mm, "end": v(-28.69, -62.96) * mm});
            skLineSegment(sketch, "E4687", {"start": v(-28.69, -62.96) * mm, "end": v(-28.62, -62.88) * mm});
            skLineSegment(sketch, "E4688", {"start": v(-28.62, -62.88) * mm, "end": v(-28.54, -62.82) * mm});
            skLineSegment(sketch, "E4689", {"start": v(-28.54, -62.82) * mm, "end": v(-28.45, -62.76) * mm});
            skLineSegment(sketch, "E4690", {"start": v(-28.45, -62.76) * mm, "end": v(-28.33, -62.72) * mm});
            skLineSegment(sketch, "E4691", {"start": v(-28.33, -62.72) * mm, "end": v(-28.2, -62.7) * mm});
            skLineSegment(sketch, "E4692", {"start": v(-28.2, -62.7) * mm, "end": v(-28.07, -62.72) * mm});
            skLineSegment(sketch, "E4693", {"start": v(-28.07, -62.72) * mm, "end": v(-27.94, -62.76) * mm});
            skLineSegment(sketch, "E4694", {"start": v(-27.94, -62.76) * mm, "end": v(-27.83, -62.83) * mm});
            skLineSegment(sketch, "E4695", {"start": v(-27.83, -62.83) * mm, "end": v(-27.73, -62.92) * mm});
            skLineSegment(sketch, "E4696", {"start": v(-27.73, -62.92) * mm, "end": v(-27.65, -63.02) * mm});
            skLineSegment(sketch, "E4697", {"start": v(-27.65, -63.02) * mm, "end": v(-27.6, -63.14) * mm});
            skLineSegment(sketch, "E4698", {"start": v(-27.6, -63.14) * mm, "end": v(-27.59, -63.24) * mm});
            skLineSegment(sketch, "E4699", {"start": v(-27.59, -63.24) * mm, "end": v(-27.58, -63.34) * mm});
            skLineSegment(sketch, "E4700", {"start": v(-27.58, -63.34) * mm, "end": v(-27.6, -63.45) * mm});
            skLineSegment(sketch, "E4701", {"start": v(-27.6, -63.45) * mm, "end": v(-27.61, -63.54) * mm});
            skLineSegment(sketch, "E4702", {"start": v(-27.61, -63.54) * mm, "end": v(-27.6, -63.64) * mm});
            skLineSegment(sketch, "E4703", {"start": v(-27.6, -63.64) * mm, "end": v(-27.52, -63.71) * mm});
            skLineSegment(sketch, "E4704", {"start": v(-27.52, -63.71) * mm, "end": v(-27.27, -63.82) * mm});
            skLineSegment(sketch, "E4705", {"start": v(-27.27, -63.82) * mm, "end": v(-27.16, -63.83) * mm});
            skLineSegment(sketch, "E4706", {"start": v(-27.16, -63.83) * mm, "end": v(-27.08, -63.77) * mm});
            skLineSegment(sketch, "E4707", {"start": v(-27.08, -63.77) * mm, "end": v(-27.03, -63.69) * mm});
            skLineSegment(sketch, "E4708", {"start": v(-27.03, -63.69) * mm, "end": v(-26.96, -63.61) * mm});
            skLineSegment(sketch, "E4709", {"start": v(-26.96, -63.61) * mm, "end": v(-26.89, -63.54) * mm});
            skLineSegment(sketch, "E4710", {"start": v(-26.89, -63.54) * mm, "end": v(-26.8, -63.48) * mm});
            skLineSegment(sketch, "E4711", {"start": v(-26.8, -63.48) * mm, "end": v(-26.68, -63.44) * mm});
            skLineSegment(sketch, "E4712", {"start": v(-26.68, -63.44) * mm, "end": v(-26.55, -63.42) * mm});
            skLineSegment(sketch, "E4713", {"start": v(-26.55, -63.42) * mm, "end": v(-26.42, -63.44) * mm});
            skLineSegment(sketch, "E4714", {"start": v(-26.42, -63.44) * mm, "end": v(-26.3, -63.47) * mm});
            skLineSegment(sketch, "E4715", {"start": v(-26.3, -63.47) * mm, "end": v(-26.18, -63.54) * mm});
            skLineSegment(sketch, "E4716", {"start": v(-26.18, -63.54) * mm, "end": v(-26.07, -63.62) * mm});
            skLineSegment(sketch, "E4717", {"start": v(-26.07, -63.62) * mm, "end": v(-26, -63.72) * mm});
            skLineSegment(sketch, "E4718", {"start": v(-26, -63.72) * mm, "end": v(-25.94, -63.84) * mm});
            skLineSegment(sketch, "E4719", {"start": v(-25.94, -63.84) * mm, "end": v(-25.92, -63.94) * mm});
            skLineSegment(sketch, "E4720", {"start": v(-25.92, -63.94) * mm, "end": v(-25.92, -64.05) * mm});
            skLineSegment(sketch, "E4721", {"start": v(-25.92, -64.05) * mm, "end": v(-25.92, -64.15) * mm});
            skLineSegment(sketch, "E4722", {"start": v(-25.92, -64.15) * mm, "end": v(-25.94, -64.24) * mm});
            skLineSegment(sketch, "E4723", {"start": v(-25.94, -64.24) * mm, "end": v(-25.93, -64.34) * mm});
            skLineSegment(sketch, "E4724", {"start": v(-25.93, -64.34) * mm, "end": v(-25.85, -64.41) * mm});
            skLineSegment(sketch, "E4725", {"start": v(-25.85, -64.41) * mm, "end": v(-25.6, -64.51) * mm});
            skLineSegment(sketch, "E4726", {"start": v(-25.6, -64.51) * mm, "end": v(-25.48, -64.52) * mm});
            skLineSegment(sketch, "E4727", {"start": v(-25.48, -64.52) * mm, "end": v(-25.4, -64.46) * mm});
            skLineSegment(sketch, "E4728", {"start": v(-25.4, -64.46) * mm, "end": v(-25.35, -64.37) * mm});
            skLineSegment(sketch, "E4729", {"start": v(-25.35, -64.37) * mm, "end": v(-25.29, -64.3) * mm});
            skLineSegment(sketch, "E4730", {"start": v(-25.29, -64.3) * mm, "end": v(-25.21, -64.23) * mm});
            skLineSegment(sketch, "E4731", {"start": v(-25.21, -64.23) * mm, "end": v(-25.13, -64.16) * mm});
            skLineSegment(sketch, "E4732", {"start": v(-25.13, -64.16) * mm, "end": v(-25, -64.12) * mm});
            skLineSegment(sketch, "E4733", {"start": v(-25, -64.12) * mm, "end": v(-24.88, -64.1) * mm});
            skLineSegment(sketch, "E4734", {"start": v(-24.88, -64.1) * mm, "end": v(-24.75, -64.1) * mm});
            skLineSegment(sketch, "E4735", {"start": v(-24.75, -64.1) * mm, "end": v(-24.62, -64.14) * mm});
            skLineSegment(sketch, "E4736", {"start": v(-24.62, -64.14) * mm, "end": v(-24.5, -64.2) * mm});
            skLineSegment(sketch, "E4737", {"start": v(-24.5, -64.2) * mm, "end": v(-24.4, -64.28) * mm});
            skLineSegment(sketch, "E4738", {"start": v(-24.4, -64.28) * mm, "end": v(-24.32, -64.38) * mm});
            skLineSegment(sketch, "E4739", {"start": v(-24.32, -64.38) * mm, "end": v(-24.26, -64.5) * mm});
            skLineSegment(sketch, "E4740", {"start": v(-24.26, -64.5) * mm, "end": v(-24.24, -64.6) * mm});
            skLineSegment(sketch, "E4741", {"start": v(-24.24, -64.6) * mm, "end": v(-24.23, -64.7) * mm});
            skLineSegment(sketch, "E4742", {"start": v(-24.23, -64.7) * mm, "end": v(-24.23, -64.8) * mm});
            skLineSegment(sketch, "E4743", {"start": v(-24.23, -64.8) * mm, "end": v(-24.25, -64.9) * mm});
            skLineSegment(sketch, "E4744", {"start": v(-24.25, -64.9) * mm, "end": v(-24.23, -65) * mm});
            skLineSegment(sketch, "E4745", {"start": v(-24.23, -65) * mm, "end": v(-24.15, -65.07) * mm});
            skLineSegment(sketch, "E4746", {"start": v(-24.15, -65.07) * mm, "end": v(-23.9, -65.16) * mm});
            skLineSegment(sketch, "E4747", {"start": v(-23.9, -65.16) * mm, "end": v(-23.79, -65.16) * mm});
            skLineSegment(sketch, "E4748", {"start": v(-23.79, -65.16) * mm, "end": v(-23.7, -65.1) * mm});
            skLineSegment(sketch, "E4749", {"start": v(-23.7, -65.1) * mm, "end": v(-23.66, -65.02) * mm});
            skLineSegment(sketch, "E4750", {"start": v(-23.66, -65.02) * mm, "end": v(-23.6, -64.94) * mm});
            skLineSegment(sketch, "E4751", {"start": v(-23.6, -64.94) * mm, "end": v(-23.52, -64.86) * mm});
            skLineSegment(sketch, "E4752", {"start": v(-23.52, -64.86) * mm, "end": v(-23.44, -64.8) * mm});
            skLineSegment(sketch, "E4753", {"start": v(-23.44, -64.8) * mm, "end": v(-23.32, -64.75) * mm});
            skLineSegment(sketch, "E4754", {"start": v(-23.32, -64.75) * mm, "end": v(-23.2, -64.73) * mm});
            skLineSegment(sketch, "E4755", {"start": v(-23.2, -64.73) * mm, "end": v(-23.06, -64.73) * mm});
            skLineSegment(sketch, "E4756", {"start": v(-23.06, -64.73) * mm, "end": v(-22.93, -64.76) * mm});
            skLineSegment(sketch, "E4757", {"start": v(-22.93, -64.76) * mm, "end": v(-22.81, -64.82) * mm});
            skLineSegment(sketch, "E4758", {"start": v(-22.81, -64.82) * mm, "end": v(-22.7, -64.9) * mm});
            skLineSegment(sketch, "E4759", {"start": v(-22.7, -64.9) * mm, "end": v(-22.62, -65) * mm});
            skLineSegment(sketch, "E4760", {"start": v(-22.62, -65) * mm, "end": v(-22.56, -65.11) * mm});
            skLineSegment(sketch, "E4761", {"start": v(-22.56, -65.11) * mm, "end": v(-22.54, -65.21) * mm});
            skLineSegment(sketch, "E4762", {"start": v(-22.54, -65.21) * mm, "end": v(-22.53, -65.31) * mm});
            skLineSegment(sketch, "E4763", {"start": v(-22.53, -65.31) * mm, "end": v(-22.53, -65.41) * mm});
            skLineSegment(sketch, "E4764", {"start": v(-22.53, -65.41) * mm, "end": v(-22.54, -65.51) * mm});
            skLineSegment(sketch, "E4765", {"start": v(-22.54, -65.51) * mm, "end": v(-22.52, -65.61) * mm});
            skLineSegment(sketch, "E4766", {"start": v(-22.52, -65.61) * mm, "end": v(-22.44, -65.68) * mm});
            skLineSegment(sketch, "E4767", {"start": v(-22.44, -65.68) * mm, "end": v(-22.18, -65.77) * mm});
            skLineSegment(sketch, "E4768", {"start": v(-22.18, -65.77) * mm, "end": v(-22.07, -65.76) * mm});
            skLineSegment(sketch, "E4769", {"start": v(-22.07, -65.76) * mm, "end": v(-22, -65.7) * mm});
            skLineSegment(sketch, "E4770", {"start": v(-22, -65.7) * mm, "end": v(-21.95, -65.61) * mm});
            skLineSegment(sketch, "E4771", {"start": v(-21.95, -65.61) * mm, "end": v(-21.89, -65.53) * mm});
            skLineSegment(sketch, "E4772", {"start": v(-21.89, -65.53) * mm, "end": v(-21.82, -65.46) * mm});
            skLineSegment(sketch, "E4773", {"start": v(-21.82, -65.46) * mm, "end": v(-21.74, -65.4) * mm});
            skLineSegment(sketch, "E4774", {"start": v(-21.74, -65.4) * mm, "end": v(-21.62, -65.34) * mm});
            skLineSegment(sketch, "E4775", {"start": v(-21.62, -65.34) * mm, "end": v(-21.5, -65.31) * mm});
            skLineSegment(sketch, "E4776", {"start": v(-21.5, -65.31) * mm, "end": v(-21.36, -65.31) * mm});
            skLineSegment(sketch, "E4777", {"start": v(-21.36, -65.31) * mm, "end": v(-21.23, -65.34) * mm});
            skLineSegment(sketch, "E4778", {"start": v(-21.23, -65.34) * mm, "end": v(-21.1, -65.4) * mm});
            skLineSegment(sketch, "E4779", {"start": v(-21.1, -65.4) * mm, "end": v(-21, -65.47) * mm});
            skLineSegment(sketch, "E4780", {"start": v(-21, -65.47) * mm, "end": v(-20.91, -65.57) * mm});
            skLineSegment(sketch, "E4781", {"start": v(-20.91, -65.57) * mm, "end": v(-20.85, -65.68) * mm});
            skLineSegment(sketch, "E4782", {"start": v(-20.85, -65.68) * mm, "end": v(-20.82, -65.78) * mm});
            skLineSegment(sketch, "E4783", {"start": v(-20.82, -65.78) * mm, "end": v(-20.81, -65.88) * mm});
            skLineSegment(sketch, "E4784", {"start": v(-20.81, -65.88) * mm, "end": v(-20.81, -65.98) * mm});
            skLineSegment(sketch, "E4785", {"start": v(-20.81, -65.98) * mm, "end": v(-20.82, -66.08) * mm});
            skLineSegment(sketch, "E4786", {"start": v(-20.82, -66.08) * mm, "end": v(-20.8, -66.18) * mm});
            skLineSegment(sketch, "E4787", {"start": v(-20.8, -66.18) * mm, "end": v(-20.71, -66.24) * mm});
            skLineSegment(sketch, "E4788", {"start": v(-20.71, -66.24) * mm, "end": v(-20.45, -66.32) * mm});
            skLineSegment(sketch, "E4789", {"start": v(-20.45, -66.32) * mm, "end": v(-20.34, -66.32) * mm});
            skLineSegment(sketch, "E4790", {"start": v(-20.34, -66.32) * mm, "end": v(-20.27, -66.25) * mm});
            skLineSegment(sketch, "E4791", {"start": v(-20.27, -66.25) * mm, "end": v(-20.22, -66.16) * mm});
            skLineSegment(sketch, "E4792", {"start": v(-20.22, -66.16) * mm, "end": v(-20.16, -66.08) * mm});
            skLineSegment(sketch, "E4793", {"start": v(-20.16, -66.08) * mm, "end": v(-20.1, -66) * mm});
            skLineSegment(sketch, "E4794", {"start": v(-20.1, -66) * mm, "end": v(-20.02, -65.94) * mm});
            skLineSegment(sketch, "E4795", {"start": v(-20.02, -65.94) * mm, "end": v(-19.9, -65.88) * mm});
            skLineSegment(sketch, "E4796", {"start": v(-19.9, -65.88) * mm, "end": v(-19.77, -65.85) * mm});
            skLineSegment(sketch, "E4797", {"start": v(-19.77, -65.85) * mm, "end": v(-19.64, -65.85) * mm});
            skLineSegment(sketch, "E4798", {"start": v(-19.64, -65.85) * mm, "end": v(-19.51, -65.87) * mm});
            skLineSegment(sketch, "E4799", {"start": v(-19.51, -65.87) * mm, "end": v(-19.4, -65.92) * mm});
            skLineSegment(sketch, "E4800", {"start": v(-19.4, -65.92) * mm, "end": v(-19.28, -66) * mm});
            skLineSegment(sketch, "E4801", {"start": v(-19.28, -66) * mm, "end": v(-19.2, -66.1) * mm});
            skLineSegment(sketch, "E4802", {"start": v(-19.2, -66.1) * mm, "end": v(-19.12, -66.2) * mm});
            skLineSegment(sketch, "E4803", {"start": v(-19.12, -66.2) * mm, "end": v(-19.1, -66.3) * mm});
            skLineSegment(sketch, "E4804", {"start": v(-19.1, -66.3) * mm, "end": v(-19.08, -66.4) * mm});
            skLineSegment(sketch, "E4805", {"start": v(-19.08, -66.4) * mm, "end": v(-19.08, -66.5) * mm});
            skLineSegment(sketch, "E4806", {"start": v(-19.08, -66.5) * mm, "end": v(-19.08, -66.6) * mm});
            skLineSegment(sketch, "E4807", {"start": v(-19.08, -66.6) * mm, "end": v(-19.06, -66.7) * mm});
            skLineSegment(sketch, "E4808", {"start": v(-19.06, -66.7) * mm, "end": v(-18.97, -66.76) * mm});
            skLineSegment(sketch, "E4809", {"start": v(-18.97, -66.76) * mm, "end": v(-18.7, -66.84) * mm});
            skLineSegment(sketch, "E4810", {"start": v(-18.7, -66.84) * mm, "end": v(-18.6, -66.83) * mm});
            skLineSegment(sketch, "E4811", {"start": v(-18.6, -66.83) * mm, "end": v(-18.53, -66.76) * mm});
            skLineSegment(sketch, "E4812", {"start": v(-18.53, -66.76) * mm, "end": v(-18.48, -66.67) * mm});
            skLineSegment(sketch, "E4813", {"start": v(-18.48, -66.67) * mm, "end": v(-18.43, -66.59) * mm});
            skLineSegment(sketch, "E4814", {"start": v(-18.43, -66.59) * mm, "end": v(-18.36, -66.51) * mm});
            skLineSegment(sketch, "E4815", {"start": v(-18.36, -66.51) * mm, "end": v(-18.29, -66.44) * mm});
            skLineSegment(sketch, "E4816", {"start": v(-18.29, -66.44) * mm, "end": v(-18.17, -66.38) * mm});
            skLineSegment(sketch, "E4817", {"start": v(-18.17, -66.38) * mm, "end": v(-18.04, -66.35) * mm});
            skLineSegment(sketch, "E4818", {"start": v(-18.04, -66.35) * mm, "end": v(-17.91, -66.34) * mm});
            skLineSegment(sketch, "E4819", {"start": v(-17.91, -66.34) * mm, "end": v(-17.78, -66.36) * mm});
            skLineSegment(sketch, "E4820", {"start": v(-17.78, -66.36) * mm, "end": v(-17.66, -66.4) * mm});
            skLineSegment(sketch, "E4821", {"start": v(-17.66, -66.4) * mm, "end": v(-17.55, -66.48) * mm});
            skLineSegment(sketch, "E4822", {"start": v(-17.55, -66.48) * mm, "end": v(-17.45, -66.57) * mm});
            skLineSegment(sketch, "E4823", {"start": v(-17.45, -66.57) * mm, "end": v(-17.38, -66.68) * mm});
            skLineSegment(sketch, "E4824", {"start": v(-17.38, -66.68) * mm, "end": v(-17.35, -66.78) * mm});
            skLineSegment(sketch, "E4825", {"start": v(-17.35, -66.78) * mm, "end": v(-17.33, -66.88) * mm});
            skLineSegment(sketch, "E4826", {"start": v(-17.33, -66.88) * mm, "end": v(-17.33, -66.98) * mm});
            skLineSegment(sketch, "E4827", {"start": v(-17.33, -66.98) * mm, "end": v(-17.33, -67.08) * mm});
            skLineSegment(sketch, "E4828", {"start": v(-17.33, -67.08) * mm, "end": v(-17.3, -67.18) * mm});
            skLineSegment(sketch, "E4829", {"start": v(-17.3, -67.18) * mm, "end": v(-17.22, -67.24) * mm});
            skLineSegment(sketch, "E4830", {"start": v(-17.22, -67.24) * mm, "end": v(-16.95, -67.3) * mm});
            skLineSegment(sketch, "E4831", {"start": v(-16.95, -67.3) * mm, "end": v(-16.84, -67.3) * mm});
            skLineSegment(sketch, "E4832", {"start": v(-16.84, -67.3) * mm, "end": v(-16.77, -67.22) * mm});
            skLineSegment(sketch, "E4833", {"start": v(-16.77, -67.22) * mm, "end": v(-16.73, -67.13) * mm});
            skLineSegment(sketch, "E4834", {"start": v(-16.73, -67.13) * mm, "end": v(-16.68, -67.05) * mm});
            skLineSegment(sketch, "E4835", {"start": v(-16.68, -67.05) * mm, "end": v(-16.61, -66.97) * mm});
            skLineSegment(sketch, "E4836", {"start": v(-16.61, -66.97) * mm, "end": v(-16.54, -66.9) * mm});
            skLineSegment(sketch, "E4837", {"start": v(-16.54, -66.9) * mm, "end": v(-16.43, -66.83) * mm});
            skLineSegment(sketch, "E4838", {"start": v(-16.43, -66.83) * mm, "end": v(-16.3, -66.8) * mm});
            skLineSegment(sketch, "E4839", {"start": v(-16.3, -66.8) * mm, "end": v(-16.17, -66.79) * mm});
            skLineSegment(sketch, "E4840", {"start": v(-16.17, -66.79) * mm, "end": v(-16.04, -66.8) * mm});
            skLineSegment(sketch, "E4841", {"start": v(-16.04, -66.8) * mm, "end": v(-15.91, -66.85) * mm});
            skLineSegment(sketch, "E4842", {"start": v(-15.91, -66.85) * mm, "end": v(-15.8, -66.92) * mm});
            skLineSegment(sketch, "E4843", {"start": v(-15.8, -66.92) * mm, "end": v(-15.7, -67) * mm});
            skLineSegment(sketch, "E4844", {"start": v(-15.7, -67) * mm, "end": v(-15.63, -67.11) * mm});
            skLineSegment(sketch, "E4845", {"start": v(-15.63, -67.11) * mm, "end": v(-15.6, -67.21) * mm});
            skLineSegment(sketch, "E4846", {"start": v(-15.6, -67.21) * mm, "end": v(-15.58, -67.31) * mm});
            skLineSegment(sketch, "E4847", {"start": v(-15.58, -67.31) * mm, "end": v(-15.57, -67.41) * mm});
            skLineSegment(sketch, "E4848", {"start": v(-15.57, -67.41) * mm, "end": v(-15.57, -67.51) * mm});
            skLineSegment(sketch, "E4849", {"start": v(-15.57, -67.51) * mm, "end": v(-15.54, -67.6) * mm});
            skLineSegment(sketch, "E4850", {"start": v(-15.54, -67.6) * mm, "end": v(-15.45, -67.66) * mm});
            skLineSegment(sketch, "E4851", {"start": v(-15.45, -67.66) * mm, "end": v(-15.18, -67.72) * mm});
            skLineSegment(sketch, "E4852", {"start": v(-15.18, -67.72) * mm, "end": v(-15.08, -67.71) * mm});
            skLineSegment(sketch, "E4853", {"start": v(-15.08, -67.71) * mm, "end": v(-15, -67.64) * mm});
            skLineSegment(sketch, "E4854", {"start": v(-15, -67.64) * mm, "end": v(-14.97, -67.55) * mm});
            skLineSegment(sketch, "E4855", {"start": v(-14.97, -67.55) * mm, "end": v(-14.92, -67.46) * mm});
            skLineSegment(sketch, "E4856", {"start": v(-14.92, -67.46) * mm, "end": v(-14.86, -67.38) * mm});
            skLineSegment(sketch, "E4857", {"start": v(-14.86, -67.38) * mm, "end": v(-14.78, -67.3) * mm});
            skLineSegment(sketch, "E4858", {"start": v(-14.78, -67.3) * mm, "end": v(-14.67, -67.24) * mm});
            skLineSegment(sketch, "E4859", {"start": v(-14.67, -67.24) * mm, "end": v(-14.55, -67.2) * mm});
            skLineSegment(sketch, "E4860", {"start": v(-14.55, -67.2) * mm, "end": v(-14.42, -67.19) * mm});
            skLineSegment(sketch, "E4861", {"start": v(-14.42, -67.19) * mm, "end": v(-14.28, -67.2) * mm});
            skLineSegment(sketch, "E4862", {"start": v(-14.28, -67.2) * mm, "end": v(-14.16, -67.24) * mm});
            skLineSegment(sketch, "E4863", {"start": v(-14.16, -67.24) * mm, "end": v(-14.04, -67.3) * mm});
            skLineSegment(sketch, "E4864", {"start": v(-14.04, -67.3) * mm, "end": v(-13.95, -67.4) * mm});
            skLineSegment(sketch, "E4865", {"start": v(-13.95, -67.4) * mm, "end": v(-13.87, -67.5) * mm});
            skLineSegment(sketch, "E4866", {"start": v(-13.87, -67.5) * mm, "end": v(-13.83, -67.6) * mm});
            skLineSegment(sketch, "E4867", {"start": v(-13.83, -67.6) * mm, "end": v(-13.81, -67.7) * mm});
            skLineSegment(sketch, "E4868", {"start": v(-13.81, -67.7) * mm, "end": v(-13.8, -67.8) * mm});
            skLineSegment(sketch, "E4869", {"start": v(-13.8, -67.8) * mm, "end": v(-13.8, -67.9) * mm});
            skLineSegment(sketch, "E4870", {"start": v(-13.8, -67.9) * mm, "end": v(-13.77, -68) * mm});
            skLineSegment(sketch, "E4871", {"start": v(-13.77, -68) * mm, "end": v(-13.67, -68.04) * mm});
            skLineSegment(sketch, "E4872", {"start": v(-13.67, -68.04) * mm, "end": v(-13.4, -68.1) * mm});
            skLineSegment(sketch, "E4873", {"start": v(-13.4, -68.1) * mm, "end": v(-13.3, -68.08) * mm});
            skLineSegment(sketch, "E4874", {"start": v(-13.3, -68.08) * mm, "end": v(-13.23, -68) * mm});
            skLineSegment(sketch, "E4875", {"start": v(-13.23, -68) * mm, "end": v(-13.2, -67.92) * mm});
            skLineSegment(sketch, "E4876", {"start": v(-13.2, -67.92) * mm, "end": v(-13.15, -67.83) * mm});
            skLineSegment(sketch, "E4877", {"start": v(-13.15, -67.83) * mm, "end": v(-13.09, -67.75) * mm});
            skLineSegment(sketch, "E4878", {"start": v(-13.09, -67.75) * mm, "end": v(-13.02, -67.67) * mm});
            skLineSegment(sketch, "E4879", {"start": v(-13.02, -67.67) * mm, "end": v(-12.9, -67.6) * mm});
            skLineSegment(sketch, "E4880", {"start": v(-12.9, -67.6) * mm, "end": v(-12.78, -67.56) * mm});
            skLineSegment(sketch, "E4881", {"start": v(-12.78, -67.56) * mm, "end": v(-12.65, -67.54) * mm});
            skLineSegment(sketch, "E4882", {"start": v(-12.65, -67.54) * mm, "end": v(-12.52, -67.55) * mm});
            skLineSegment(sketch, "E4883", {"start": v(-12.52, -67.55) * mm, "end": v(-12.4, -67.6) * mm});
            skLineSegment(sketch, "E4884", {"start": v(-12.4, -67.6) * mm, "end": v(-12.28, -67.65) * mm});
            skLineSegment(sketch, "E4885", {"start": v(-12.28, -67.65) * mm, "end": v(-12.18, -67.74) * mm});
            skLineSegment(sketch, "E4886", {"start": v(-12.18, -67.74) * mm, "end": v(-12.1, -67.84) * mm});
            skLineSegment(sketch, "E4887", {"start": v(-12.1, -67.84) * mm, "end": v(-12.06, -67.94) * mm});
            skLineSegment(sketch, "E4888", {"start": v(-12.06, -67.94) * mm, "end": v(-12.03, -68.03) * mm});
            skLineSegment(sketch, "E4889", {"start": v(-12.03, -68.03) * mm, "end": v(-12.02, -68.13) * mm});
            skLineSegment(sketch, "E4890", {"start": v(-12.02, -68.13) * mm, "end": v(-12.02, -68.23) * mm});
            skLineSegment(sketch, "E4891", {"start": v(-12.02, -68.23) * mm, "end": v(-11.98, -68.33) * mm});
            skLineSegment(sketch, "E4892", {"start": v(-11.98, -68.33) * mm, "end": v(-11.89, -68.38) * mm});
            skLineSegment(sketch, "E4893", {"start": v(-11.89, -68.38) * mm, "end": v(-11.62, -68.43) * mm});
            skLineSegment(sketch, "E4894", {"start": v(-11.62, -68.43) * mm, "end": v(-11.51, -68.4) * mm});
            skLineSegment(sketch, "E4895", {"start": v(-11.51, -68.4) * mm, "end": v(-11.45, -68.33) * mm});
            skLineSegment(sketch, "E4896", {"start": v(-11.45, -68.33) * mm, "end": v(-11.41, -68.24) * mm});
            skLineSegment(sketch, "E4897", {"start": v(-11.41, -68.24) * mm, "end": v(-11.37, -68.15) * mm});
            skLineSegment(sketch, "E4898", {"start": v(-11.37, -68.15) * mm, "end": v(-11.3, -68.07) * mm});
            skLineSegment(sketch, "E4899", {"start": v(-11.3, -68.07) * mm, "end": v(-11.24, -67.99) * mm});
            skLineSegment(sketch, "E4900", {"start": v(-11.24, -67.99) * mm, "end": v(-11.13, -67.91) * mm});
            skLineSegment(sketch, "E4901", {"start": v(-11.13, -67.91) * mm, "end": v(-11, -67.87) * mm});
            skLineSegment(sketch, "E4902", {"start": v(-11, -67.87) * mm, "end": v(-10.88, -67.85) * mm});
            skLineSegment(sketch, "E4903", {"start": v(-10.88, -67.85) * mm, "end": v(-10.75, -67.86) * mm});
            skLineSegment(sketch, "E4904", {"start": v(-10.75, -67.86) * mm, "end": v(-10.62, -67.9) * mm});
            skLineSegment(sketch, "E4905", {"start": v(-10.62, -67.9) * mm, "end": v(-10.5, -67.95) * mm});
            skLineSegment(sketch, "E4906", {"start": v(-10.5, -67.95) * mm, "end": v(-10.4, -68.03) * mm});
            skLineSegment(sketch, "E4907", {"start": v(-10.4, -68.03) * mm, "end": v(-10.32, -68.13) * mm});
            skLineSegment(sketch, "E4908", {"start": v(-10.32, -68.13) * mm, "end": v(-10.28, -68.23) * mm});
            skLineSegment(sketch, "E4909", {"start": v(-10.28, -68.23) * mm, "end": v(-10.25, -68.33) * mm});
            skLineSegment(sketch, "E4910", {"start": v(-10.25, -68.33) * mm, "end": v(-10.23, -68.42) * mm});
            skLineSegment(sketch, "E4911", {"start": v(-10.23, -68.42) * mm, "end": v(-10.23, -68.53) * mm});
            skLineSegment(sketch, "E4912", {"start": v(-10.23, -68.53) * mm, "end": v(-10.19, -68.62) * mm});
            skLineSegment(sketch, "E4913", {"start": v(-10.19, -68.62) * mm, "end": v(-10.1, -68.67) * mm});
            skLineSegment(sketch, "E4914", {"start": v(-10.1, -68.67) * mm, "end": v(-9.82, -68.7) * mm});
            skLineSegment(sketch, "E4915", {"start": v(-9.82, -68.7) * mm, "end": v(-9.72, -68.69) * mm});
            skLineSegment(sketch, "E4916", {"start": v(-9.72, -68.69) * mm, "end": v(-9.66, -68.6) * mm});
            skLineSegment(sketch, "E4917", {"start": v(-9.66, -68.6) * mm, "end": v(-9.62, -68.51) * mm});
            skLineSegment(sketch, "E4918", {"start": v(-9.62, -68.51) * mm, "end": v(-9.58, -68.42) * mm});
            skLineSegment(sketch, "E4919", {"start": v(-9.58, -68.42) * mm, "end": v(-9.52, -68.34) * mm});
            skLineSegment(sketch, "E4920", {"start": v(-9.52, -68.34) * mm, "end": v(-9.46, -68.26) * mm});
            skLineSegment(sketch, "E4921", {"start": v(-9.46, -68.26) * mm, "end": v(-9.35, -68.18) * mm});
            skLineSegment(sketch, "E4922", {"start": v(-9.35, -68.18) * mm, "end": v(-9.23, -68.13) * mm});
            skLineSegment(sketch, "E4923", {"start": v(-9.23, -68.13) * mm, "end": v(-9.1, -68.11) * mm});
            skLineSegment(sketch, "E4924", {"start": v(-9.1, -68.11) * mm, "end": v(-8.97, -68.12) * mm});
            skLineSegment(sketch, "E4925", {"start": v(-8.97, -68.12) * mm, "end": v(-8.84, -68.15) * mm});
            skLineSegment(sketch, "E4926", {"start": v(-8.84, -68.15) * mm, "end": v(-8.72, -68.2) * mm});
            skLineSegment(sketch, "E4927", {"start": v(-8.72, -68.2) * mm, "end": v(-8.62, -68.28) * mm});
            skLineSegment(sketch, "E4928", {"start": v(-8.62, -68.28) * mm, "end": v(-8.53, -68.38) * mm});
            skLineSegment(sketch, "E4929", {"start": v(-8.53, -68.38) * mm, "end": v(-8.49, -68.47) * mm});
            skLineSegment(sketch, "E4930", {"start": v(-8.49, -68.47) * mm, "end": v(-8.46, -68.57) * mm});
            skLineSegment(sketch, "E4931", {"start": v(-8.46, -68.57) * mm, "end": v(-8.44, -68.67) * mm});
            skLineSegment(sketch, "E4932", {"start": v(-8.44, -68.67) * mm, "end": v(-8.43, -68.77) * mm});
            skLineSegment(sketch, "E4933", {"start": v(-8.43, -68.77) * mm, "end": v(-8.4, -68.86) * mm});
            skLineSegment(sketch, "E4934", {"start": v(-8.4, -68.86) * mm, "end": v(-8.3, -68.9) * mm});
            skLineSegment(sketch, "E4935", {"start": v(-8.3, -68.9) * mm, "end": v(-8.02, -68.94) * mm});
            skLineSegment(sketch, "E4936", {"start": v(-8.02, -68.94) * mm, "end": v(-7.92, -68.92) * mm});
            skLineSegment(sketch, "E4937", {"start": v(-7.92, -68.92) * mm, "end": v(-7.86, -68.84) * mm});
            skLineSegment(sketch, "E4938", {"start": v(-7.86, -68.84) * mm, "end": v(-7.83, -68.74) * mm});
            skLineSegment(sketch, "E4939", {"start": v(-7.83, -68.74) * mm, "end": v(-7.78, -68.65) * mm});
            skLineSegment(sketch, "E4940", {"start": v(-7.78, -68.65) * mm, "end": v(-7.73, -68.56) * mm});
            skLineSegment(sketch, "E4941", {"start": v(-7.73, -68.56) * mm, "end": v(-7.67, -68.48) * mm});
            skLineSegment(sketch, "E4942", {"start": v(-7.67, -68.48) * mm, "end": v(-7.56, -68.4) * mm});
            skLineSegment(sketch, "E4943", {"start": v(-7.56, -68.4) * mm, "end": v(-7.44, -68.35) * mm});
            skLineSegment(sketch, "E4944", {"start": v(-7.44, -68.35) * mm, "end": v(-7.31, -68.33) * mm});
            skLineSegment(sketch, "E4945", {"start": v(-7.31, -68.33) * mm, "end": v(-7.18, -68.33) * mm});
            skLineSegment(sketch, "E4946", {"start": v(-7.18, -68.33) * mm, "end": v(-7.05, -68.35) * mm});
            skLineSegment(sketch, "E4947", {"start": v(-7.05, -68.35) * mm, "end": v(-6.93, -68.4) * mm});
            skLineSegment(sketch, "E4948", {"start": v(-6.93, -68.4) * mm, "end": v(-6.83, -68.48) * mm});
            skLineSegment(sketch, "E4949", {"start": v(-6.83, -68.48) * mm, "end": v(-6.74, -68.58) * mm});
            skLineSegment(sketch, "E4950", {"start": v(-6.74, -68.58) * mm, "end": v(-6.7, -68.67) * mm});
            skLineSegment(sketch, "E4951", {"start": v(-6.7, -68.67) * mm, "end": v(-6.66, -68.77) * mm});
            skLineSegment(sketch, "E4952", {"start": v(-6.66, -68.77) * mm, "end": v(-6.64, -68.87) * mm});
            skLineSegment(sketch, "E4953", {"start": v(-6.64, -68.87) * mm, "end": v(-6.63, -68.97) * mm});
            skLineSegment(sketch, "E4954", {"start": v(-6.63, -68.97) * mm, "end": v(-6.58, -69.06) * mm});
            skLineSegment(sketch, "E4955", {"start": v(-6.58, -69.06) * mm, "end": v(-6.49, -69.1) * mm});
            skLineSegment(sketch, "E4956", {"start": v(-6.49, -69.1) * mm, "end": v(-6.21, -69.13) * mm});
            skLineSegment(sketch, "E4957", {"start": v(-6.21, -69.13) * mm, "end": v(-6.11, -69.1) * mm});
            skLineSegment(sketch, "E4958", {"start": v(-6.11, -69.1) * mm, "end": v(-6.05, -69.02) * mm});
            skLineSegment(sketch, "E4959", {"start": v(-6.05, -69.02) * mm, "end": v(-6.02, -68.92) * mm});
            skLineSegment(sketch, "E4960", {"start": v(-6.02, -68.92) * mm, "end": v(-5.98, -68.83) * mm});
            skLineSegment(sketch, "E4961", {"start": v(-5.98, -68.83) * mm, "end": v(-5.93, -68.74) * mm});
            skLineSegment(sketch, "E4962", {"start": v(-5.93, -68.74) * mm, "end": v(-5.87, -68.66) * mm});
            skLineSegment(sketch, "E4963", {"start": v(-5.87, -68.66) * mm, "end": v(-5.77, -68.58) * mm});
            skLineSegment(sketch, "E4964", {"start": v(-5.77, -68.58) * mm, "end": v(-5.65, -68.52) * mm});
            skLineSegment(sketch, "E4965", {"start": v(-5.65, -68.52) * mm, "end": v(-5.52, -68.5) * mm});
            skLineSegment(sketch, "E4966", {"start": v(-5.52, -68.5) * mm, "end": v(-5.4, -68.5) * mm});
            skLineSegment(sketch, "E4967", {"start": v(-5.4, -68.5) * mm, "end": v(-5.26, -68.52) * mm});
            skLineSegment(sketch, "E4968", {"start": v(-5.26, -68.52) * mm, "end": v(-5.14, -68.56) * mm});
            skLineSegment(sketch, "E4969", {"start": v(-5.14, -68.56) * mm, "end": v(-5.03, -68.64) * mm});
            skLineSegment(sketch, "E4970", {"start": v(-5.03, -68.64) * mm, "end": v(-4.94, -68.73) * mm});
            skLineSegment(sketch, "E4971", {"start": v(-4.94, -68.73) * mm, "end": v(-4.9, -68.82) * mm});
            skLineSegment(sketch, "E4972", {"start": v(-4.9, -68.82) * mm, "end": v(-4.86, -68.92) * mm});
            skLineSegment(sketch, "E4973", {"start": v(-4.86, -68.92) * mm, "end": v(-4.83, -69.02) * mm});
            skLineSegment(sketch, "E4974", {"start": v(-4.83, -69.02) * mm, "end": v(-4.82, -69.12) * mm});
            skLineSegment(sketch, "E4975", {"start": v(-4.82, -69.12) * mm, "end": v(-4.77, -69.2) * mm});
            skLineSegment(sketch, "E4976", {"start": v(-4.77, -69.2) * mm, "end": v(-4.68, -69.25) * mm});
            skLineSegment(sketch, "E4977", {"start": v(-4.68, -69.25) * mm, "end": v(-4.4, -69.26) * mm});
            skLineSegment(sketch, "E4978", {"start": v(-4.4, -69.26) * mm, "end": v(-4.3, -69.24) * mm});
            skLineSegment(sketch, "E4979", {"start": v(-4.3, -69.24) * mm, "end": v(-4.24, -69.15) * mm});
            skLineSegment(sketch, "E4980", {"start": v(-4.24, -69.15) * mm, "end": v(-4.22, -69.06) * mm});
            skLineSegment(sketch, "E4981", {"start": v(-4.22, -69.06) * mm, "end": v(-4.18, -68.96) * mm});
            skLineSegment(sketch, "E4982", {"start": v(-4.18, -68.96) * mm, "end": v(-4.13, -68.87) * mm});
            skLineSegment(sketch, "E4983", {"start": v(-4.13, -68.87) * mm, "end": v(-4.07, -68.79) * mm});
            skLineSegment(sketch, "E4984", {"start": v(-4.07, -68.79) * mm, "end": v(-3.97, -68.7) * mm});
            skLineSegment(sketch, "E4985", {"start": v(-3.97, -68.7) * mm, "end": v(-3.85, -68.65) * mm});
            skLineSegment(sketch, "E4986", {"start": v(-3.85, -68.65) * mm, "end": v(-3.73, -68.62) * mm});
            skLineSegment(sketch, "E4987", {"start": v(-3.73, -68.62) * mm, "end": v(-3.6, -68.6) * mm});
            skLineSegment(sketch, "E4988", {"start": v(-3.6, -68.6) * mm, "end": v(-3.47, -68.63) * mm});
            skLineSegment(sketch, "E4989", {"start": v(-3.47, -68.63) * mm, "end": v(-3.34, -68.68) * mm});
            skLineSegment(sketch, "E4990", {"start": v(-3.34, -68.68) * mm, "end": v(-3.23, -68.75) * mm});
            skLineSegment(sketch, "E4991", {"start": v(-3.23, -68.75) * mm, "end": v(-3.14, -68.84) * mm});
            skLineSegment(sketch, "E4992", {"start": v(-3.14, -68.84) * mm, "end": v(-3.1, -68.93) * mm});
            skLineSegment(sketch, "E4993", {"start": v(-3.1, -68.93) * mm, "end": v(-3.05, -69.02) * mm});
            skLineSegment(sketch, "E4994", {"start": v(-3.05, -69.02) * mm, "end": v(-3.02, -69.12) * mm});
            skLineSegment(sketch, "E4995", {"start": v(-3.02, -69.12) * mm, "end": v(-3, -69.22) * mm});
            skLineSegment(sketch, "E4996", {"start": v(-3, -69.22) * mm, "end": v(-2.96, -69.3) * mm});
            skLineSegment(sketch, "E4997", {"start": v(-2.96, -69.3) * mm, "end": v(-2.86, -69.35) * mm});
            skLineSegment(sketch, "E4998", {"start": v(-2.86, -69.35) * mm, "end": v(-2.59, -69.36) * mm});
            skLineSegment(sketch, "E4999", {"start": v(-2.59, -69.36) * mm, "end": v(-2.49, -69.33) * mm});
            skLineSegment(sketch, "E5000", {"start": v(-2.49, -69.33) * mm, "end": v(-2.43, -69.24) * mm});
            skLineSegment(sketch, "E5001", {"start": v(-2.43, -69.24) * mm, "end": v(-2.4, -69.14) * mm});
            skLineSegment(sketch, "E5002", {"start": v(-2.4, -69.14) * mm, "end": v(-2.37, -69.05) * mm});
            skLineSegment(sketch, "E5003", {"start": v(-2.37, -69.05) * mm, "end": v(-2.33, -68.96) * mm});
            skLineSegment(sketch, "E5004", {"start": v(-2.33, -68.96) * mm, "end": v(-2.27, -68.87) * mm});
            skLineSegment(sketch, "E5005", {"start": v(-2.27, -68.87) * mm, "end": v(-2.17, -68.79) * mm});
            skLineSegment(sketch, "E5006", {"start": v(-2.17, -68.79) * mm, "end": v(-2.06, -68.73) * mm});
            skLineSegment(sketch, "E5007", {"start": v(-2.06, -68.73) * mm, "end": v(-1.93, -68.69) * mm});
            skLineSegment(sketch, "E5008", {"start": v(-1.93, -68.69) * mm, "end": v(-1.8, -68.68) * mm});
            skLineSegment(sketch, "E5009", {"start": v(-1.8, -68.68) * mm, "end": v(-1.67, -68.7) * mm});
            skLineSegment(sketch, "E5010", {"start": v(-1.67, -68.7) * mm, "end": v(-1.54, -68.74) * mm});
            skLineSegment(sketch, "E5011", {"start": v(-1.54, -68.74) * mm, "end": v(-1.43, -68.8) * mm});
            skLineSegment(sketch, "E5012", {"start": v(-1.43, -68.8) * mm, "end": v(-1.34, -68.9) * mm});
            skLineSegment(sketch, "E5013", {"start": v(-1.34, -68.9) * mm, "end": v(-1.28, -68.99) * mm});
            skLineSegment(sketch, "E5014", {"start": v(-1.28, -68.99) * mm, "end": v(-1.24, -69.08) * mm});
            skLineSegment(sketch, "E5015", {"start": v(-1.24, -69.08) * mm, "end": v(-1.21, -69.18) * mm});
            skLineSegment(sketch, "E5016", {"start": v(-1.21, -69.18) * mm, "end": v(-1.2, -69.27) * mm});
            skLineSegment(sketch, "E5017", {"start": v(-1.2, -69.27) * mm, "end": v(-1.15, -69.36) * mm});
            skLineSegment(sketch, "E5018", {"start": v(-1.15, -69.36) * mm, "end": v(-1.05, -69.4) * mm});
            skLineSegment(sketch, "E5019", {"start": v(-1.05, -69.4) * mm, "end": v(-0.77, -69.4) * mm});
            skLineSegment(sketch, "E5020", {"start": v(-0.77, -69.4) * mm, "end": v(-0.67, -69.37) * mm});
            skLineSegment(sketch, "E5021", {"start": v(-0.67, -69.37) * mm, "end": v(-0.62, -69.28) * mm});
            skLineSegment(sketch, "E5022", {"start": v(-0.62, -69.28) * mm, "end": v(-0.6, -69.18) * mm});
            skLineSegment(sketch, "E5023", {"start": v(-0.6, -69.18) * mm, "end": v(-0.57, -69.09) * mm});
            skLineSegment(sketch, "E5024", {"start": v(-0.57, -69.09) * mm, "end": v(-0.52, -69) * mm});
            skLineSegment(sketch, "E5025", {"start": v(-0.52, -69) * mm, "end": v(-0.47, -68.9) * mm});
            skLineSegment(sketch, "E5026", {"start": v(-0.47, -68.9) * mm, "end": v(-0.37, -68.82) * mm});
            skLineSegment(sketch, "E5027", {"start": v(-0.37, -68.82) * mm, "end": v(-0.26, -68.76) * mm});
            skLineSegment(sketch, "E5028", {"start": v(-0.26, -68.76) * mm, "end": v(-0.13, -68.72) * mm});
            skLineSegment(sketch, "E5029", {"start": v(-0.13, -68.72) * mm, "end": v(0, -68.7) * mm});
            skLineSegment(sketch, "E5030", {"start": v(0, -68.7) * mm, "end": v(0.13, -68.72) * mm});
            skLineSegment(sketch, "E5031", {"start": v(0.13, -68.72) * mm, "end": v(0.26, -68.76) * mm});
            skLineSegment(sketch, "E5032", {"start": v(0.26, -68.76) * mm, "end": v(0.37, -68.82) * mm});
            skLineSegment(sketch, "E5033", {"start": v(0.37, -68.82) * mm, "end": v(0.47, -68.9) * mm});
            skLineSegment(sketch, "E5034", {"start": v(0.47, -68.9) * mm, "end": v(0.52, -69) * mm});
            skLineSegment(sketch, "E5035", {"start": v(0.52, -69) * mm, "end": v(0.57, -69.09) * mm});
            skLineSegment(sketch, "E5036", {"start": v(0.57, -69.09) * mm, "end": v(0.6, -69.18) * mm});
            skLineSegment(sketch, "E5037", {"start": v(0.6, -69.18) * mm, "end": v(0.62, -69.28) * mm});
            skLineSegment(sketch, "E5038", {"start": v(0.62, -69.28) * mm, "end": v(0.67, -69.37) * mm});
            skLineSegment(sketch, "E5039", {"start": v(0.67, -69.37) * mm, "end": v(0.77, -69.4) * mm});
            skLineSegment(sketch, "E5040", {"start": v(-0.73, -2.25) * mm, "end": v(-1.4, -1.92) * mm});
            skLineSegment(sketch, "E5041", {"start": v(-1.4, -1.92) * mm, "end": v(-1.92, -1.4) * mm});
            skLineSegment(sketch, "E5042", {"start": v(-1.92, -1.4) * mm, "end": v(-2.25, -0.73) * mm});
            skLineSegment(sketch, "E5043", {"start": v(-2.25, -0.73) * mm, "end": v(-2.37, 0) * mm});
            skLineSegment(sketch, "E5044", {"start": v(-2.37, 0) * mm, "end": v(-2.25, 0.73) * mm});
            skLineSegment(sketch, "E5045", {"start": v(-2.25, 0.73) * mm, "end": v(-1.92, 1.4) * mm});
            skLineSegment(sketch, "E5046", {"start": v(-1.92, 1.4) * mm, "end": v(-1.4, 1.92) * mm});
            skLineSegment(sketch, "E5047", {"start": v(-1.4, 1.92) * mm, "end": v(-0.73, 2.25) * mm});
            skLineSegment(sketch, "E5048", {"start": v(-0.73, 2.25) * mm, "end": v(0, 2.37) * mm});
            skLineSegment(sketch, "E5049", {"start": v(0, 2.37) * mm, "end": v(0.73, 2.25) * mm});
            skLineSegment(sketch, "E5050", {"start": v(0.73, 2.25) * mm, "end": v(1.4, 1.92) * mm});
            skLineSegment(sketch, "E5051", {"start": v(1.4, 1.92) * mm, "end": v(1.92, 1.4) * mm});
            skLineSegment(sketch, "E5052", {"start": v(1.92, 1.4) * mm, "end": v(2.25, 0.73) * mm});
            skLineSegment(sketch, "E5053", {"start": v(2.25, 0.73) * mm, "end": v(2.37, 0) * mm});
            skLineSegment(sketch, "E5054", {"start": v(2.37, 0) * mm, "end": v(2.25, -0.73) * mm});
            skLineSegment(sketch, "E5055", {"start": v(2.25, -0.73) * mm, "end": v(1.92, -1.4) * mm});
            skLineSegment(sketch, "E5056", {"start": v(1.92, -1.4) * mm, "end": v(1.4, -1.92) * mm});
            skLineSegment(sketch, "E5057", {"start": v(1.4, -1.92) * mm, "end": v(0.73, -2.25) * mm});
            skLineSegment(sketch, "E5058", {"start": v(0.73, -2.25) * mm, "end": v(0, -2.37) * mm});
            skLineSegment(sketch, "E5059", {"start": v(0, -2.37) * mm, "end": v(-0.73, -2.25) * mm});
            skCircle(sketch, "E5060", {"center": v(0, 0) * mm, "radius": 3.18 * mm});
            skSolve(sketch);
        }
        {
            var Q0;
            Q0=makeQuery(id+"F0.imprint","IMPRINT",FACE,{"disambiguationData":[TD([[makeQuery(id+"F0.imprint","IMPRINT",EDGE,{"derivedFrom":sQuery(id+"F0.wireOp",EDGE,"E0")}),1.0]])]});
            extrude(context, id + "F1", {"entities" : qUnion([Q0]), "depth" : 5 * mm, "offsetDistance" : 25 * mm});
        }
    });
